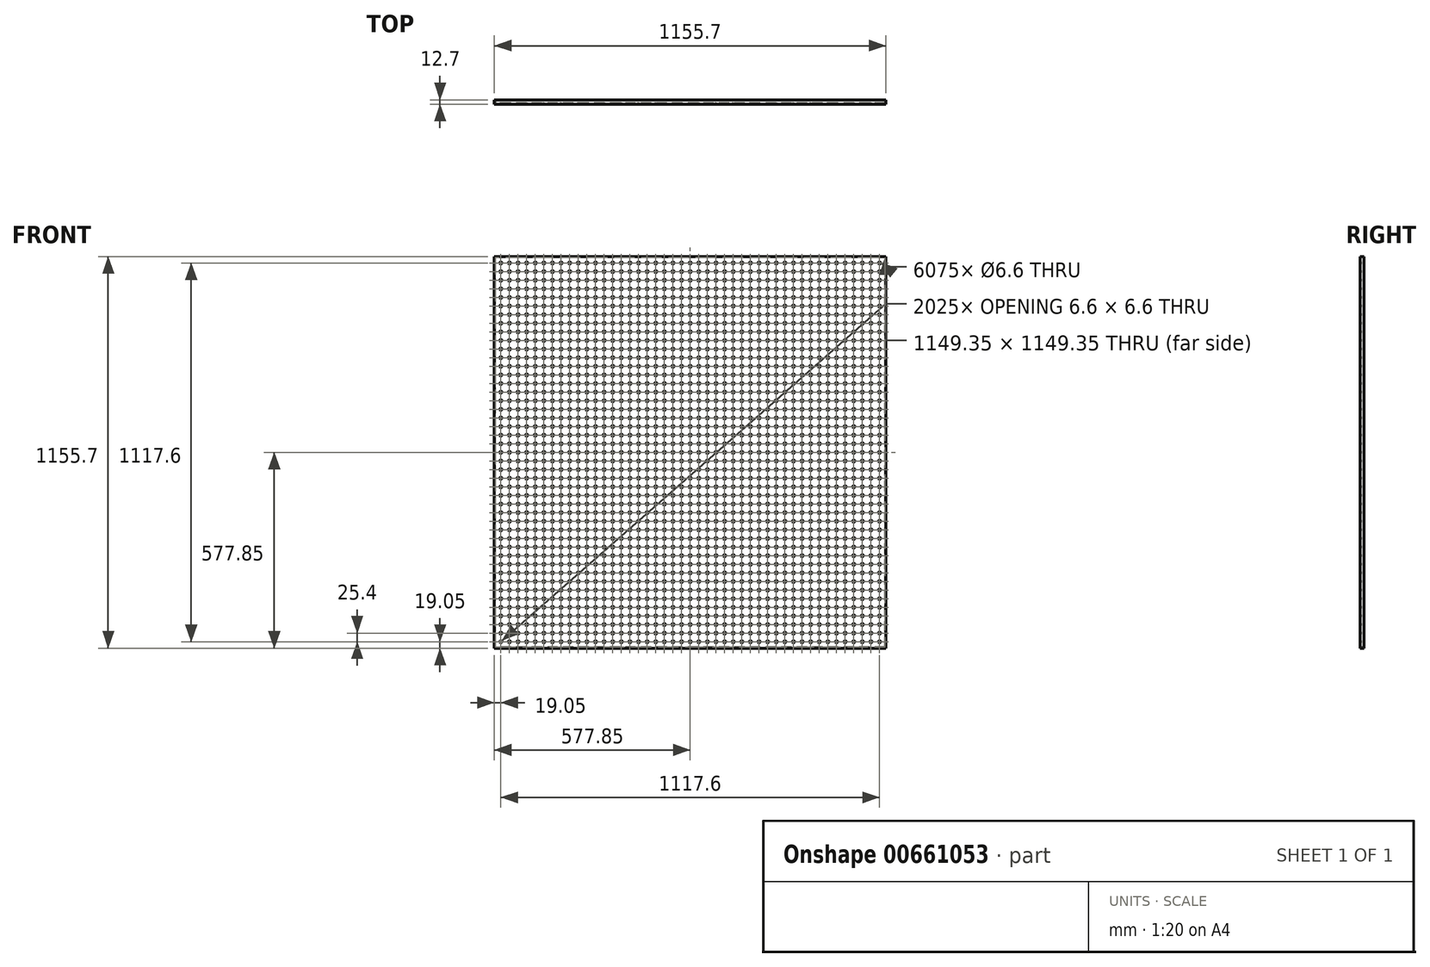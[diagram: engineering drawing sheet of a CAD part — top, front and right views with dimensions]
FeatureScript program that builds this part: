
annotation { "Feature Type Name" : "Feature", "Feature Type Description" : "" }
export const myFeature = defineFeature(function(context is Context, id is Id, definition is map)
    precondition{}
    {
        {
            var Q0;
            Q0=qCreatedBy(makeId("Front.planeOp"),FACE);
            var sketch = newSketch(context, id + "F0", { "sketchPlane" : qUnion([Q0])});
            skLineSegment(sketch, "E0.bottom", {"start": v(577.85, -577.85) * mm, "end": v(-577.85, -577.85) * mm});
            skLineSegment(sketch, "E0.top", {"start": v(577.85, 577.85) * mm, "end": v(-577.85, 577.85) * mm});
            skLineSegment(sketch, "E0.left", {"start": v(577.85, -577.85) * mm, "end": v(577.85, 577.85) * mm});
            skLineSegment(sketch, "E0.right", {"start": v(-577.85, -577.85) * mm, "end": v(-577.85, 577.85) * mm});
            skPoint(sketch, "E0.middle", {"position": v(0, 0) * mm});
            skCircle(sketch, "E1", {"center": v(-558.8, 558.8) * mm, "radius": 3.3 * mm});
            skCircle(sketch, "E2.0.1.0", {"center": v(-558.8, 533.4) * mm, "radius": 3.3 * mm});
            skCircle(sketch, "E2.0.2.0", {"center": v(-558.8, 508) * mm, "radius": 3.3 * mm});
            skCircle(sketch, "E2.0.3.0", {"center": v(-558.8, 482.6) * mm, "radius": 3.3 * mm});
            skCircle(sketch, "E2.0.4.0", {"center": v(-558.8, 457.2) * mm, "radius": 3.3 * mm});
            skCircle(sketch, "E2.0.5.0", {"center": v(-558.8, 431.8) * mm, "radius": 3.3 * mm});
            skCircle(sketch, "E2.0.6.0", {"center": v(-558.8, 406.4) * mm, "radius": 3.3 * mm});
            skCircle(sketch, "E2.0.7.0", {"center": v(-558.8, 381) * mm, "radius": 3.3 * mm});
            skCircle(sketch, "E2.0.8.0", {"center": v(-558.8, 355.6) * mm, "radius": 3.3 * mm});
            skCircle(sketch, "E2.0.9.0", {"center": v(-558.8, 330.2) * mm, "radius": 3.3 * mm});
            skCircle(sketch, "E2.0.10.0", {"center": v(-558.8, 304.8) * mm, "radius": 3.3 * mm});
            skCircle(sketch, "E2.0.11.0", {"center": v(-558.8, 279.4) * mm, "radius": 3.3 * mm});
            skCircle(sketch, "E2.0.12.0", {"center": v(-558.8, 254) * mm, "radius": 3.3 * mm});
            skCircle(sketch, "E2.0.13.0", {"center": v(-558.8, 228.6) * mm, "radius": 3.3 * mm});
            skCircle(sketch, "E2.0.14.0", {"center": v(-558.8, 203.2) * mm, "radius": 3.3 * mm});
            skCircle(sketch, "E2.0.15.0", {"center": v(-558.8, 177.8) * mm, "radius": 3.3 * mm});
            skCircle(sketch, "E2.0.16.0", {"center": v(-558.8, 152.4) * mm, "radius": 3.3 * mm});
            skCircle(sketch, "E2.0.17.0", {"center": v(-558.8, 127) * mm, "radius": 3.3 * mm});
            skCircle(sketch, "E2.0.18.0", {"center": v(-558.8, 101.6) * mm, "radius": 3.3 * mm});
            skCircle(sketch, "E2.0.19.0", {"center": v(-558.8, 76.2) * mm, "radius": 3.3 * mm});
            skCircle(sketch, "E2.0.20.0", {"center": v(-558.8, 50.8) * mm, "radius": 3.3 * mm});
            skCircle(sketch, "E2.0.21.0", {"center": v(-558.8, 25.4) * mm, "radius": 3.3 * mm});
            skCircle(sketch, "E2.0.22.0", {"center": v(-558.8, 0) * mm, "radius": 3.3 * mm});
            skCircle(sketch, "E2.0.23.0", {"center": v(-558.8, -25.4) * mm, "radius": 3.3 * mm});
            skCircle(sketch, "E2.0.24.0", {"center": v(-558.8, -50.8) * mm, "radius": 3.3 * mm});
            skCircle(sketch, "E2.0.25.0", {"center": v(-558.8, -76.2) * mm, "radius": 3.3 * mm});
            skCircle(sketch, "E2.0.26.0", {"center": v(-558.8, -101.6) * mm, "radius": 3.3 * mm});
            skCircle(sketch, "E2.0.27.0", {"center": v(-558.8, -127) * mm, "radius": 3.3 * mm});
            skCircle(sketch, "E2.0.28.0", {"center": v(-558.8, -152.4) * mm, "radius": 3.3 * mm});
            skCircle(sketch, "E2.0.29.0", {"center": v(-558.8, -177.8) * mm, "radius": 3.3 * mm});
            skCircle(sketch, "E2.0.30.0", {"center": v(-558.8, -203.2) * mm, "radius": 3.3 * mm});
            skCircle(sketch, "E2.0.31.0", {"center": v(-558.8, -228.6) * mm, "radius": 3.3 * mm});
            skCircle(sketch, "E2.0.32.0", {"center": v(-558.8, -254) * mm, "radius": 3.3 * mm});
            skCircle(sketch, "E2.0.33.0", {"center": v(-558.8, -279.4) * mm, "radius": 3.3 * mm});
            skCircle(sketch, "E2.0.34.0", {"center": v(-558.8, -304.8) * mm, "radius": 3.3 * mm});
            skCircle(sketch, "E2.0.35.0", {"center": v(-558.8, -330.2) * mm, "radius": 3.3 * mm});
            skCircle(sketch, "E2.0.36.0", {"center": v(-558.8, -355.6) * mm, "radius": 3.3 * mm});
            skCircle(sketch, "E2.0.37.0", {"center": v(-558.8, -381) * mm, "radius": 3.3 * mm});
            skCircle(sketch, "E2.0.38.0", {"center": v(-558.8, -406.4) * mm, "radius": 3.3 * mm});
            skCircle(sketch, "E2.0.39.0", {"center": v(-558.8, -431.8) * mm, "radius": 3.3 * mm});
            skCircle(sketch, "E2.0.40.0", {"center": v(-558.8, -457.2) * mm, "radius": 3.3 * mm});
            skCircle(sketch, "E2.0.41.0", {"center": v(-558.8, -482.6) * mm, "radius": 3.3 * mm});
            skCircle(sketch, "E2.0.42.0", {"center": v(-558.8, -508) * mm, "radius": 3.3 * mm});
            skCircle(sketch, "E2.0.43.0", {"center": v(-558.8, -533.4) * mm, "radius": 3.3 * mm});
            skCircle(sketch, "E2.0.44.0", {"center": v(-558.8, -558.8) * mm, "radius": 3.3 * mm});
            skCircle(sketch, "E2.1.0.0", {"center": v(-533.4, 558.8) * mm, "radius": 3.3 * mm});
            skCircle(sketch, "E2.1.1.0", {"center": v(-533.4, 533.4) * mm, "radius": 3.3 * mm});
            skCircle(sketch, "E2.1.2.0", {"center": v(-533.4, 508) * mm, "radius": 3.3 * mm});
            skCircle(sketch, "E2.1.3.0", {"center": v(-533.4, 482.6) * mm, "radius": 3.3 * mm});
            skCircle(sketch, "E2.1.4.0", {"center": v(-533.4, 457.2) * mm, "radius": 3.3 * mm});
            skCircle(sketch, "E2.1.5.0", {"center": v(-533.4, 431.8) * mm, "radius": 3.3 * mm});
            skCircle(sketch, "E2.1.6.0", {"center": v(-533.4, 406.4) * mm, "radius": 3.3 * mm});
            skCircle(sketch, "E2.1.7.0", {"center": v(-533.4, 381) * mm, "radius": 3.3 * mm});
            skCircle(sketch, "E2.1.8.0", {"center": v(-533.4, 355.6) * mm, "radius": 3.3 * mm});
            skCircle(sketch, "E2.1.9.0", {"center": v(-533.4, 330.2) * mm, "radius": 3.3 * mm});
            skCircle(sketch, "E2.1.10.0", {"center": v(-533.4, 304.8) * mm, "radius": 3.3 * mm});
            skCircle(sketch, "E2.1.11.0", {"center": v(-533.4, 279.4) * mm, "radius": 3.3 * mm});
            skCircle(sketch, "E2.1.12.0", {"center": v(-533.4, 254) * mm, "radius": 3.3 * mm});
            skCircle(sketch, "E2.1.13.0", {"center": v(-533.4, 228.6) * mm, "radius": 3.3 * mm});
            skCircle(sketch, "E2.1.14.0", {"center": v(-533.4, 203.2) * mm, "radius": 3.3 * mm});
            skCircle(sketch, "E2.1.15.0", {"center": v(-533.4, 177.8) * mm, "radius": 3.3 * mm});
            skCircle(sketch, "E2.1.16.0", {"center": v(-533.4, 152.4) * mm, "radius": 3.3 * mm});
            skCircle(sketch, "E2.1.17.0", {"center": v(-533.4, 127) * mm, "radius": 3.3 * mm});
            skCircle(sketch, "E2.1.18.0", {"center": v(-533.4, 101.6) * mm, "radius": 3.3 * mm});
            skCircle(sketch, "E2.1.19.0", {"center": v(-533.4, 76.2) * mm, "radius": 3.3 * mm});
            skCircle(sketch, "E2.1.20.0", {"center": v(-533.4, 50.8) * mm, "radius": 3.3 * mm});
            skCircle(sketch, "E2.1.21.0", {"center": v(-533.4, 25.4) * mm, "radius": 3.3 * mm});
            skCircle(sketch, "E2.1.22.0", {"center": v(-533.4, 0) * mm, "radius": 3.3 * mm});
            skCircle(sketch, "E2.1.23.0", {"center": v(-533.4, -25.4) * mm, "radius": 3.3 * mm});
            skCircle(sketch, "E2.1.24.0", {"center": v(-533.4, -50.8) * mm, "radius": 3.3 * mm});
            skCircle(sketch, "E2.1.25.0", {"center": v(-533.4, -76.2) * mm, "radius": 3.3 * mm});
            skCircle(sketch, "E2.1.26.0", {"center": v(-533.4, -101.6) * mm, "radius": 3.3 * mm});
            skCircle(sketch, "E2.1.27.0", {"center": v(-533.4, -127) * mm, "radius": 3.3 * mm});
            skCircle(sketch, "E2.1.28.0", {"center": v(-533.4, -152.4) * mm, "radius": 3.3 * mm});
            skCircle(sketch, "E2.1.29.0", {"center": v(-533.4, -177.8) * mm, "radius": 3.3 * mm});
            skCircle(sketch, "E2.1.30.0", {"center": v(-533.4, -203.2) * mm, "radius": 3.3 * mm});
            skCircle(sketch, "E2.1.31.0", {"center": v(-533.4, -228.6) * mm, "radius": 3.3 * mm});
            skCircle(sketch, "E2.1.32.0", {"center": v(-533.4, -254) * mm, "radius": 3.3 * mm});
            skCircle(sketch, "E2.1.33.0", {"center": v(-533.4, -279.4) * mm, "radius": 3.3 * mm});
            skCircle(sketch, "E2.1.34.0", {"center": v(-533.4, -304.8) * mm, "radius": 3.3 * mm});
            skCircle(sketch, "E2.1.35.0", {"center": v(-533.4, -330.2) * mm, "radius": 3.3 * mm});
            skCircle(sketch, "E2.1.36.0", {"center": v(-533.4, -355.6) * mm, "radius": 3.3 * mm});
            skCircle(sketch, "E2.1.37.0", {"center": v(-533.4, -381) * mm, "radius": 3.3 * mm});
            skCircle(sketch, "E2.1.38.0", {"center": v(-533.4, -406.4) * mm, "radius": 3.3 * mm});
            skCircle(sketch, "E2.1.39.0", {"center": v(-533.4, -431.8) * mm, "radius": 3.3 * mm});
            skCircle(sketch, "E2.1.40.0", {"center": v(-533.4, -457.2) * mm, "radius": 3.3 * mm});
            skCircle(sketch, "E2.1.41.0", {"center": v(-533.4, -482.6) * mm, "radius": 3.3 * mm});
            skCircle(sketch, "E2.1.42.0", {"center": v(-533.4, -508) * mm, "radius": 3.3 * mm});
            skCircle(sketch, "E2.1.43.0", {"center": v(-533.4, -533.4) * mm, "radius": 3.3 * mm});
            skCircle(sketch, "E2.1.44.0", {"center": v(-533.4, -558.8) * mm, "radius": 3.3 * mm});
            skCircle(sketch, "E2.2.0.0", {"center": v(-508, 558.8) * mm, "radius": 3.3 * mm});
            skCircle(sketch, "E2.2.1.0", {"center": v(-508, 533.4) * mm, "radius": 3.3 * mm});
            skCircle(sketch, "E2.2.2.0", {"center": v(-508, 508) * mm, "radius": 3.3 * mm});
            skCircle(sketch, "E2.2.3.0", {"center": v(-508, 482.6) * mm, "radius": 3.3 * mm});
            skCircle(sketch, "E2.2.4.0", {"center": v(-508, 457.2) * mm, "radius": 3.3 * mm});
            skCircle(sketch, "E2.2.5.0", {"center": v(-508, 431.8) * mm, "radius": 3.3 * mm});
            skCircle(sketch, "E2.2.6.0", {"center": v(-508, 406.4) * mm, "radius": 3.3 * mm});
            skCircle(sketch, "E2.2.7.0", {"center": v(-508, 381) * mm, "radius": 3.3 * mm});
            skCircle(sketch, "E2.2.8.0", {"center": v(-508, 355.6) * mm, "radius": 3.3 * mm});
            skCircle(sketch, "E2.2.9.0", {"center": v(-508, 330.2) * mm, "radius": 3.3 * mm});
            skCircle(sketch, "E2.2.10.0", {"center": v(-508, 304.8) * mm, "radius": 3.3 * mm});
            skCircle(sketch, "E2.2.11.0", {"center": v(-508, 279.4) * mm, "radius": 3.3 * mm});
            skCircle(sketch, "E2.2.12.0", {"center": v(-508, 254) * mm, "radius": 3.3 * mm});
            skCircle(sketch, "E2.2.13.0", {"center": v(-508, 228.6) * mm, "radius": 3.3 * mm});
            skCircle(sketch, "E2.2.14.0", {"center": v(-508, 203.2) * mm, "radius": 3.3 * mm});
            skCircle(sketch, "E2.2.15.0", {"center": v(-508, 177.8) * mm, "radius": 3.3 * mm});
            skCircle(sketch, "E2.2.16.0", {"center": v(-508, 152.4) * mm, "radius": 3.3 * mm});
            skCircle(sketch, "E2.2.17.0", {"center": v(-508, 127) * mm, "radius": 3.3 * mm});
            skCircle(sketch, "E2.2.18.0", {"center": v(-508, 101.6) * mm, "radius": 3.3 * mm});
            skCircle(sketch, "E2.2.19.0", {"center": v(-508, 76.2) * mm, "radius": 3.3 * mm});
            skCircle(sketch, "E2.2.20.0", {"center": v(-508, 50.8) * mm, "radius": 3.3 * mm});
            skCircle(sketch, "E2.2.21.0", {"center": v(-508, 25.4) * mm, "radius": 3.3 * mm});
            skCircle(sketch, "E2.2.22.0", {"center": v(-508, 0) * mm, "radius": 3.3 * mm});
            skCircle(sketch, "E2.2.23.0", {"center": v(-508, -25.4) * mm, "radius": 3.3 * mm});
            skCircle(sketch, "E2.2.24.0", {"center": v(-508, -50.8) * mm, "radius": 3.3 * mm});
            skCircle(sketch, "E2.2.25.0", {"center": v(-508, -76.2) * mm, "radius": 3.3 * mm});
            skCircle(sketch, "E2.2.26.0", {"center": v(-508, -101.6) * mm, "radius": 3.3 * mm});
            skCircle(sketch, "E2.2.27.0", {"center": v(-508, -127) * mm, "radius": 3.3 * mm});
            skCircle(sketch, "E2.2.28.0", {"center": v(-508, -152.4) * mm, "radius": 3.3 * mm});
            skCircle(sketch, "E2.2.29.0", {"center": v(-508, -177.8) * mm, "radius": 3.3 * mm});
            skCircle(sketch, "E2.2.30.0", {"center": v(-508, -203.2) * mm, "radius": 3.3 * mm});
            skCircle(sketch, "E2.2.31.0", {"center": v(-508, -228.6) * mm, "radius": 3.3 * mm});
            skCircle(sketch, "E2.2.32.0", {"center": v(-508, -254) * mm, "radius": 3.3 * mm});
            skCircle(sketch, "E2.2.33.0", {"center": v(-508, -279.4) * mm, "radius": 3.3 * mm});
            skCircle(sketch, "E2.2.34.0", {"center": v(-508, -304.8) * mm, "radius": 3.3 * mm});
            skCircle(sketch, "E2.2.35.0", {"center": v(-508, -330.2) * mm, "radius": 3.3 * mm});
            skCircle(sketch, "E2.2.36.0", {"center": v(-508, -355.6) * mm, "radius": 3.3 * mm});
            skCircle(sketch, "E2.2.37.0", {"center": v(-508, -381) * mm, "radius": 3.3 * mm});
            skCircle(sketch, "E2.2.38.0", {"center": v(-508, -406.4) * mm, "radius": 3.3 * mm});
            skCircle(sketch, "E2.2.39.0", {"center": v(-508, -431.8) * mm, "radius": 3.3 * mm});
            skCircle(sketch, "E2.2.40.0", {"center": v(-508, -457.2) * mm, "radius": 3.3 * mm});
            skCircle(sketch, "E2.2.41.0", {"center": v(-508, -482.6) * mm, "radius": 3.3 * mm});
            skCircle(sketch, "E2.2.42.0", {"center": v(-508, -508) * mm, "radius": 3.3 * mm});
            skCircle(sketch, "E2.2.43.0", {"center": v(-508, -533.4) * mm, "radius": 3.3 * mm});
            skCircle(sketch, "E2.2.44.0", {"center": v(-508, -558.8) * mm, "radius": 3.3 * mm});
            skCircle(sketch, "E2.3.0.0", {"center": v(-482.6, 558.8) * mm, "radius": 3.3 * mm});
            skCircle(sketch, "E2.3.1.0", {"center": v(-482.6, 533.4) * mm, "radius": 3.3 * mm});
            skCircle(sketch, "E2.3.2.0", {"center": v(-482.6, 508) * mm, "radius": 3.3 * mm});
            skCircle(sketch, "E2.3.3.0", {"center": v(-482.6, 482.6) * mm, "radius": 3.3 * mm});
            skCircle(sketch, "E2.3.4.0", {"center": v(-482.6, 457.2) * mm, "radius": 3.3 * mm});
            skCircle(sketch, "E2.3.5.0", {"center": v(-482.6, 431.8) * mm, "radius": 3.3 * mm});
            skCircle(sketch, "E2.3.6.0", {"center": v(-482.6, 406.4) * mm, "radius": 3.3 * mm});
            skCircle(sketch, "E2.3.7.0", {"center": v(-482.6, 381) * mm, "radius": 3.3 * mm});
            skCircle(sketch, "E2.3.8.0", {"center": v(-482.6, 355.6) * mm, "radius": 3.3 * mm});
            skCircle(sketch, "E2.3.9.0", {"center": v(-482.6, 330.2) * mm, "radius": 3.3 * mm});
            skCircle(sketch, "E2.3.10.0", {"center": v(-482.6, 304.8) * mm, "radius": 3.3 * mm});
            skCircle(sketch, "E2.3.11.0", {"center": v(-482.6, 279.4) * mm, "radius": 3.3 * mm});
            skCircle(sketch, "E2.3.12.0", {"center": v(-482.6, 254) * mm, "radius": 3.3 * mm});
            skCircle(sketch, "E2.3.13.0", {"center": v(-482.6, 228.6) * mm, "radius": 3.3 * mm});
            skCircle(sketch, "E2.3.14.0", {"center": v(-482.6, 203.2) * mm, "radius": 3.3 * mm});
            skCircle(sketch, "E2.3.15.0", {"center": v(-482.6, 177.8) * mm, "radius": 3.3 * mm});
            skCircle(sketch, "E2.3.16.0", {"center": v(-482.6, 152.4) * mm, "radius": 3.3 * mm});
            skCircle(sketch, "E2.3.17.0", {"center": v(-482.6, 127) * mm, "radius": 3.3 * mm});
            skCircle(sketch, "E2.3.18.0", {"center": v(-482.6, 101.6) * mm, "radius": 3.3 * mm});
            skCircle(sketch, "E2.3.19.0", {"center": v(-482.6, 76.2) * mm, "radius": 3.3 * mm});
            skCircle(sketch, "E2.3.20.0", {"center": v(-482.6, 50.8) * mm, "radius": 3.3 * mm});
            skCircle(sketch, "E2.3.21.0", {"center": v(-482.6, 25.4) * mm, "radius": 3.3 * mm});
            skCircle(sketch, "E2.3.22.0", {"center": v(-482.6, 0) * mm, "radius": 3.3 * mm});
            skCircle(sketch, "E2.3.23.0", {"center": v(-482.6, -25.4) * mm, "radius": 3.3 * mm});
            skCircle(sketch, "E2.3.24.0", {"center": v(-482.6, -50.8) * mm, "radius": 3.3 * mm});
            skCircle(sketch, "E2.3.25.0", {"center": v(-482.6, -76.2) * mm, "radius": 3.3 * mm});
            skCircle(sketch, "E2.3.26.0", {"center": v(-482.6, -101.6) * mm, "radius": 3.3 * mm});
            skCircle(sketch, "E2.3.27.0", {"center": v(-482.6, -127) * mm, "radius": 3.3 * mm});
            skCircle(sketch, "E2.3.28.0", {"center": v(-482.6, -152.4) * mm, "radius": 3.3 * mm});
            skCircle(sketch, "E2.3.29.0", {"center": v(-482.6, -177.8) * mm, "radius": 3.3 * mm});
            skCircle(sketch, "E2.3.30.0", {"center": v(-482.6, -203.2) * mm, "radius": 3.3 * mm});
            skCircle(sketch, "E2.3.31.0", {"center": v(-482.6, -228.6) * mm, "radius": 3.3 * mm});
            skCircle(sketch, "E2.3.32.0", {"center": v(-482.6, -254) * mm, "radius": 3.3 * mm});
            skCircle(sketch, "E2.3.33.0", {"center": v(-482.6, -279.4) * mm, "radius": 3.3 * mm});
            skCircle(sketch, "E2.3.34.0", {"center": v(-482.6, -304.8) * mm, "radius": 3.3 * mm});
            skCircle(sketch, "E2.3.35.0", {"center": v(-482.6, -330.2) * mm, "radius": 3.3 * mm});
            skCircle(sketch, "E2.3.36.0", {"center": v(-482.6, -355.6) * mm, "radius": 3.3 * mm});
            skCircle(sketch, "E2.3.37.0", {"center": v(-482.6, -381) * mm, "radius": 3.3 * mm});
            skCircle(sketch, "E2.3.38.0", {"center": v(-482.6, -406.4) * mm, "radius": 3.3 * mm});
            skCircle(sketch, "E2.3.39.0", {"center": v(-482.6, -431.8) * mm, "radius": 3.3 * mm});
            skCircle(sketch, "E2.3.40.0", {"center": v(-482.6, -457.2) * mm, "radius": 3.3 * mm});
            skCircle(sketch, "E2.3.41.0", {"center": v(-482.6, -482.6) * mm, "radius": 3.3 * mm});
            skCircle(sketch, "E2.3.42.0", {"center": v(-482.6, -508) * mm, "radius": 3.3 * mm});
            skCircle(sketch, "E2.3.43.0", {"center": v(-482.6, -533.4) * mm, "radius": 3.3 * mm});
            skCircle(sketch, "E2.3.44.0", {"center": v(-482.6, -558.8) * mm, "radius": 3.3 * mm});
            skCircle(sketch, "E2.4.0.0", {"center": v(-457.2, 558.8) * mm, "radius": 3.3 * mm});
            skCircle(sketch, "E2.4.1.0", {"center": v(-457.2, 533.4) * mm, "radius": 3.3 * mm});
            skCircle(sketch, "E2.4.2.0", {"center": v(-457.2, 508) * mm, "radius": 3.3 * mm});
            skCircle(sketch, "E2.4.3.0", {"center": v(-457.2, 482.6) * mm, "radius": 3.3 * mm});
            skCircle(sketch, "E2.4.4.0", {"center": v(-457.2, 457.2) * mm, "radius": 3.3 * mm});
            skCircle(sketch, "E2.4.5.0", {"center": v(-457.2, 431.8) * mm, "radius": 3.3 * mm});
            skCircle(sketch, "E2.4.6.0", {"center": v(-457.2, 406.4) * mm, "radius": 3.3 * mm});
            skCircle(sketch, "E2.4.7.0", {"center": v(-457.2, 381) * mm, "radius": 3.3 * mm});
            skCircle(sketch, "E2.4.8.0", {"center": v(-457.2, 355.6) * mm, "radius": 3.3 * mm});
            skCircle(sketch, "E2.4.9.0", {"center": v(-457.2, 330.2) * mm, "radius": 3.3 * mm});
            skCircle(sketch, "E2.4.10.0", {"center": v(-457.2, 304.8) * mm, "radius": 3.3 * mm});
            skCircle(sketch, "E2.4.11.0", {"center": v(-457.2, 279.4) * mm, "radius": 3.3 * mm});
            skCircle(sketch, "E2.4.12.0", {"center": v(-457.2, 254) * mm, "radius": 3.3 * mm});
            skCircle(sketch, "E2.4.13.0", {"center": v(-457.2, 228.6) * mm, "radius": 3.3 * mm});
            skCircle(sketch, "E2.4.14.0", {"center": v(-457.2, 203.2) * mm, "radius": 3.3 * mm});
            skCircle(sketch, "E2.4.15.0", {"center": v(-457.2, 177.8) * mm, "radius": 3.3 * mm});
            skCircle(sketch, "E2.4.16.0", {"center": v(-457.2, 152.4) * mm, "radius": 3.3 * mm});
            skCircle(sketch, "E2.4.17.0", {"center": v(-457.2, 127) * mm, "radius": 3.3 * mm});
            skCircle(sketch, "E2.4.18.0", {"center": v(-457.2, 101.6) * mm, "radius": 3.3 * mm});
            skCircle(sketch, "E2.4.19.0", {"center": v(-457.2, 76.2) * mm, "radius": 3.3 * mm});
            skCircle(sketch, "E2.4.20.0", {"center": v(-457.2, 50.8) * mm, "radius": 3.3 * mm});
            skCircle(sketch, "E2.4.21.0", {"center": v(-457.2, 25.4) * mm, "radius": 3.3 * mm});
            skCircle(sketch, "E2.4.22.0", {"center": v(-457.2, 0) * mm, "radius": 3.3 * mm});
            skCircle(sketch, "E2.4.23.0", {"center": v(-457.2, -25.4) * mm, "radius": 3.3 * mm});
            skCircle(sketch, "E2.4.24.0", {"center": v(-457.2, -50.8) * mm, "radius": 3.3 * mm});
            skCircle(sketch, "E2.4.25.0", {"center": v(-457.2, -76.2) * mm, "radius": 3.3 * mm});
            skCircle(sketch, "E2.4.26.0", {"center": v(-457.2, -101.6) * mm, "radius": 3.3 * mm});
            skCircle(sketch, "E2.4.27.0", {"center": v(-457.2, -127) * mm, "radius": 3.3 * mm});
            skCircle(sketch, "E2.4.28.0", {"center": v(-457.2, -152.4) * mm, "radius": 3.3 * mm});
            skCircle(sketch, "E2.4.29.0", {"center": v(-457.2, -177.8) * mm, "radius": 3.3 * mm});
            skCircle(sketch, "E2.4.30.0", {"center": v(-457.2, -203.2) * mm, "radius": 3.3 * mm});
            skCircle(sketch, "E2.4.31.0", {"center": v(-457.2, -228.6) * mm, "radius": 3.3 * mm});
            skCircle(sketch, "E2.4.32.0", {"center": v(-457.2, -254) * mm, "radius": 3.3 * mm});
            skCircle(sketch, "E2.4.33.0", {"center": v(-457.2, -279.4) * mm, "radius": 3.3 * mm});
            skCircle(sketch, "E2.4.34.0", {"center": v(-457.2, -304.8) * mm, "radius": 3.3 * mm});
            skCircle(sketch, "E2.4.35.0", {"center": v(-457.2, -330.2) * mm, "radius": 3.3 * mm});
            skCircle(sketch, "E2.4.36.0", {"center": v(-457.2, -355.6) * mm, "radius": 3.3 * mm});
            skCircle(sketch, "E2.4.37.0", {"center": v(-457.2, -381) * mm, "radius": 3.3 * mm});
            skCircle(sketch, "E2.4.38.0", {"center": v(-457.2, -406.4) * mm, "radius": 3.3 * mm});
            skCircle(sketch, "E2.4.39.0", {"center": v(-457.2, -431.8) * mm, "radius": 3.3 * mm});
            skCircle(sketch, "E2.4.40.0", {"center": v(-457.2, -457.2) * mm, "radius": 3.3 * mm});
            skCircle(sketch, "E2.4.41.0", {"center": v(-457.2, -482.6) * mm, "radius": 3.3 * mm});
            skCircle(sketch, "E2.4.42.0", {"center": v(-457.2, -508) * mm, "radius": 3.3 * mm});
            skCircle(sketch, "E2.4.43.0", {"center": v(-457.2, -533.4) * mm, "radius": 3.3 * mm});
            skCircle(sketch, "E2.4.44.0", {"center": v(-457.2, -558.8) * mm, "radius": 3.3 * mm});
            skCircle(sketch, "E2.5.0.0", {"center": v(-431.8, 558.8) * mm, "radius": 3.3 * mm});
            skCircle(sketch, "E2.5.1.0", {"center": v(-431.8, 533.4) * mm, "radius": 3.3 * mm});
            skCircle(sketch, "E2.5.2.0", {"center": v(-431.8, 508) * mm, "radius": 3.3 * mm});
            skCircle(sketch, "E2.5.3.0", {"center": v(-431.8, 482.6) * mm, "radius": 3.3 * mm});
            skCircle(sketch, "E2.5.4.0", {"center": v(-431.8, 457.2) * mm, "radius": 3.3 * mm});
            skCircle(sketch, "E2.5.5.0", {"center": v(-431.8, 431.8) * mm, "radius": 3.3 * mm});
            skCircle(sketch, "E2.5.6.0", {"center": v(-431.8, 406.4) * mm, "radius": 3.3 * mm});
            skCircle(sketch, "E2.5.7.0", {"center": v(-431.8, 381) * mm, "radius": 3.3 * mm});
            skCircle(sketch, "E2.5.8.0", {"center": v(-431.8, 355.6) * mm, "radius": 3.3 * mm});
            skCircle(sketch, "E2.5.9.0", {"center": v(-431.8, 330.2) * mm, "radius": 3.3 * mm});
            skCircle(sketch, "E2.5.10.0", {"center": v(-431.8, 304.8) * mm, "radius": 3.3 * mm});
            skCircle(sketch, "E2.5.11.0", {"center": v(-431.8, 279.4) * mm, "radius": 3.3 * mm});
            skCircle(sketch, "E2.5.12.0", {"center": v(-431.8, 254) * mm, "radius": 3.3 * mm});
            skCircle(sketch, "E2.5.13.0", {"center": v(-431.8, 228.6) * mm, "radius": 3.3 * mm});
            skCircle(sketch, "E2.5.14.0", {"center": v(-431.8, 203.2) * mm, "radius": 3.3 * mm});
            skCircle(sketch, "E2.5.15.0", {"center": v(-431.8, 177.8) * mm, "radius": 3.3 * mm});
            skCircle(sketch, "E2.5.16.0", {"center": v(-431.8, 152.4) * mm, "radius": 3.3 * mm});
            skCircle(sketch, "E2.5.17.0", {"center": v(-431.8, 127) * mm, "radius": 3.3 * mm});
            skCircle(sketch, "E2.5.18.0", {"center": v(-431.8, 101.6) * mm, "radius": 3.3 * mm});
            skCircle(sketch, "E2.5.19.0", {"center": v(-431.8, 76.2) * mm, "radius": 3.3 * mm});
            skCircle(sketch, "E2.5.20.0", {"center": v(-431.8, 50.8) * mm, "radius": 3.3 * mm});
            skCircle(sketch, "E2.5.21.0", {"center": v(-431.8, 25.4) * mm, "radius": 3.3 * mm});
            skCircle(sketch, "E2.5.22.0", {"center": v(-431.8, 0) * mm, "radius": 3.3 * mm});
            skCircle(sketch, "E2.5.23.0", {"center": v(-431.8, -25.4) * mm, "radius": 3.3 * mm});
            skCircle(sketch, "E2.5.24.0", {"center": v(-431.8, -50.8) * mm, "radius": 3.3 * mm});
            skCircle(sketch, "E2.5.25.0", {"center": v(-431.8, -76.2) * mm, "radius": 3.3 * mm});
            skCircle(sketch, "E2.5.26.0", {"center": v(-431.8, -101.6) * mm, "radius": 3.3 * mm});
            skCircle(sketch, "E2.5.27.0", {"center": v(-431.8, -127) * mm, "radius": 3.3 * mm});
            skCircle(sketch, "E2.5.28.0", {"center": v(-431.8, -152.4) * mm, "radius": 3.3 * mm});
            skCircle(sketch, "E2.5.29.0", {"center": v(-431.8, -177.8) * mm, "radius": 3.3 * mm});
            skCircle(sketch, "E2.5.30.0", {"center": v(-431.8, -203.2) * mm, "radius": 3.3 * mm});
            skCircle(sketch, "E2.5.31.0", {"center": v(-431.8, -228.6) * mm, "radius": 3.3 * mm});
            skCircle(sketch, "E2.5.32.0", {"center": v(-431.8, -254) * mm, "radius": 3.3 * mm});
            skCircle(sketch, "E2.5.33.0", {"center": v(-431.8, -279.4) * mm, "radius": 3.3 * mm});
            skCircle(sketch, "E2.5.34.0", {"center": v(-431.8, -304.8) * mm, "radius": 3.3 * mm});
            skCircle(sketch, "E2.5.35.0", {"center": v(-431.8, -330.2) * mm, "radius": 3.3 * mm});
            skCircle(sketch, "E2.5.36.0", {"center": v(-431.8, -355.6) * mm, "radius": 3.3 * mm});
            skCircle(sketch, "E2.5.37.0", {"center": v(-431.8, -381) * mm, "radius": 3.3 * mm});
            skCircle(sketch, "E2.5.38.0", {"center": v(-431.8, -406.4) * mm, "radius": 3.3 * mm});
            skCircle(sketch, "E2.5.39.0", {"center": v(-431.8, -431.8) * mm, "radius": 3.3 * mm});
            skCircle(sketch, "E2.5.40.0", {"center": v(-431.8, -457.2) * mm, "radius": 3.3 * mm});
            skCircle(sketch, "E2.5.41.0", {"center": v(-431.8, -482.6) * mm, "radius": 3.3 * mm});
            skCircle(sketch, "E2.5.42.0", {"center": v(-431.8, -508) * mm, "radius": 3.3 * mm});
            skCircle(sketch, "E2.5.43.0", {"center": v(-431.8, -533.4) * mm, "radius": 3.3 * mm});
            skCircle(sketch, "E2.5.44.0", {"center": v(-431.8, -558.8) * mm, "radius": 3.3 * mm});
            skCircle(sketch, "E2.6.0.0", {"center": v(-406.4, 558.8) * mm, "radius": 3.3 * mm});
            skCircle(sketch, "E2.6.1.0", {"center": v(-406.4, 533.4) * mm, "radius": 3.3 * mm});
            skCircle(sketch, "E2.6.2.0", {"center": v(-406.4, 508) * mm, "radius": 3.3 * mm});
            skCircle(sketch, "E2.6.3.0", {"center": v(-406.4, 482.6) * mm, "radius": 3.3 * mm});
            skCircle(sketch, "E2.6.4.0", {"center": v(-406.4, 457.2) * mm, "radius": 3.3 * mm});
            skCircle(sketch, "E2.6.5.0", {"center": v(-406.4, 431.8) * mm, "radius": 3.3 * mm});
            skCircle(sketch, "E2.6.6.0", {"center": v(-406.4, 406.4) * mm, "radius": 3.3 * mm});
            skCircle(sketch, "E2.6.7.0", {"center": v(-406.4, 381) * mm, "radius": 3.3 * mm});
            skCircle(sketch, "E2.6.8.0", {"center": v(-406.4, 355.6) * mm, "radius": 3.3 * mm});
            skCircle(sketch, "E2.6.9.0", {"center": v(-406.4, 330.2) * mm, "radius": 3.3 * mm});
            skCircle(sketch, "E2.6.10.0", {"center": v(-406.4, 304.8) * mm, "radius": 3.3 * mm});
            skCircle(sketch, "E2.6.11.0", {"center": v(-406.4, 279.4) * mm, "radius": 3.3 * mm});
            skCircle(sketch, "E2.6.12.0", {"center": v(-406.4, 254) * mm, "radius": 3.3 * mm});
            skCircle(sketch, "E2.6.13.0", {"center": v(-406.4, 228.6) * mm, "radius": 3.3 * mm});
            skCircle(sketch, "E2.6.14.0", {"center": v(-406.4, 203.2) * mm, "radius": 3.3 * mm});
            skCircle(sketch, "E2.6.15.0", {"center": v(-406.4, 177.8) * mm, "radius": 3.3 * mm});
            skCircle(sketch, "E2.6.16.0", {"center": v(-406.4, 152.4) * mm, "radius": 3.3 * mm});
            skCircle(sketch, "E2.6.17.0", {"center": v(-406.4, 127) * mm, "radius": 3.3 * mm});
            skCircle(sketch, "E2.6.18.0", {"center": v(-406.4, 101.6) * mm, "radius": 3.3 * mm});
            skCircle(sketch, "E2.6.19.0", {"center": v(-406.4, 76.2) * mm, "radius": 3.3 * mm});
            skCircle(sketch, "E2.6.20.0", {"center": v(-406.4, 50.8) * mm, "radius": 3.3 * mm});
            skCircle(sketch, "E2.6.21.0", {"center": v(-406.4, 25.4) * mm, "radius": 3.3 * mm});
            skCircle(sketch, "E2.6.22.0", {"center": v(-406.4, 0) * mm, "radius": 3.3 * mm});
            skCircle(sketch, "E2.6.23.0", {"center": v(-406.4, -25.4) * mm, "radius": 3.3 * mm});
            skCircle(sketch, "E2.6.24.0", {"center": v(-406.4, -50.8) * mm, "radius": 3.3 * mm});
            skCircle(sketch, "E2.6.25.0", {"center": v(-406.4, -76.2) * mm, "radius": 3.3 * mm});
            skCircle(sketch, "E2.6.26.0", {"center": v(-406.4, -101.6) * mm, "radius": 3.3 * mm});
            skCircle(sketch, "E2.6.27.0", {"center": v(-406.4, -127) * mm, "radius": 3.3 * mm});
            skCircle(sketch, "E2.6.28.0", {"center": v(-406.4, -152.4) * mm, "radius": 3.3 * mm});
            skCircle(sketch, "E2.6.29.0", {"center": v(-406.4, -177.8) * mm, "radius": 3.3 * mm});
            skCircle(sketch, "E2.6.30.0", {"center": v(-406.4, -203.2) * mm, "radius": 3.3 * mm});
            skCircle(sketch, "E2.6.31.0", {"center": v(-406.4, -228.6) * mm, "radius": 3.3 * mm});
            skCircle(sketch, "E2.6.32.0", {"center": v(-406.4, -254) * mm, "radius": 3.3 * mm});
            skCircle(sketch, "E2.6.33.0", {"center": v(-406.4, -279.4) * mm, "radius": 3.3 * mm});
            skCircle(sketch, "E2.6.34.0", {"center": v(-406.4, -304.8) * mm, "radius": 3.3 * mm});
            skCircle(sketch, "E2.6.35.0", {"center": v(-406.4, -330.2) * mm, "radius": 3.3 * mm});
            skCircle(sketch, "E2.6.36.0", {"center": v(-406.4, -355.6) * mm, "radius": 3.3 * mm});
            skCircle(sketch, "E2.6.37.0", {"center": v(-406.4, -381) * mm, "radius": 3.3 * mm});
            skCircle(sketch, "E2.6.38.0", {"center": v(-406.4, -406.4) * mm, "radius": 3.3 * mm});
            skCircle(sketch, "E2.6.39.0", {"center": v(-406.4, -431.8) * mm, "radius": 3.3 * mm});
            skCircle(sketch, "E2.6.40.0", {"center": v(-406.4, -457.2) * mm, "radius": 3.3 * mm});
            skCircle(sketch, "E2.6.41.0", {"center": v(-406.4, -482.6) * mm, "radius": 3.3 * mm});
            skCircle(sketch, "E2.6.42.0", {"center": v(-406.4, -508) * mm, "radius": 3.3 * mm});
            skCircle(sketch, "E2.6.43.0", {"center": v(-406.4, -533.4) * mm, "radius": 3.3 * mm});
            skCircle(sketch, "E2.6.44.0", {"center": v(-406.4, -558.8) * mm, "radius": 3.3 * mm});
            skCircle(sketch, "E2.7.0.0", {"center": v(-381, 558.8) * mm, "radius": 3.3 * mm});
            skCircle(sketch, "E2.7.1.0", {"center": v(-381, 533.4) * mm, "radius": 3.3 * mm});
            skCircle(sketch, "E2.7.2.0", {"center": v(-381, 508) * mm, "radius": 3.3 * mm});
            skCircle(sketch, "E2.7.3.0", {"center": v(-381, 482.6) * mm, "radius": 3.3 * mm});
            skCircle(sketch, "E2.7.4.0", {"center": v(-381, 457.2) * mm, "radius": 3.3 * mm});
            skCircle(sketch, "E2.7.5.0", {"center": v(-381, 431.8) * mm, "radius": 3.3 * mm});
            skCircle(sketch, "E2.7.6.0", {"center": v(-381, 406.4) * mm, "radius": 3.3 * mm});
            skCircle(sketch, "E2.7.7.0", {"center": v(-381, 381) * mm, "radius": 3.3 * mm});
            skCircle(sketch, "E2.7.8.0", {"center": v(-381, 355.6) * mm, "radius": 3.3 * mm});
            skCircle(sketch, "E2.7.9.0", {"center": v(-381, 330.2) * mm, "radius": 3.3 * mm});
            skCircle(sketch, "E2.7.10.0", {"center": v(-381, 304.8) * mm, "radius": 3.3 * mm});
            skCircle(sketch, "E2.7.11.0", {"center": v(-381, 279.4) * mm, "radius": 3.3 * mm});
            skCircle(sketch, "E2.7.12.0", {"center": v(-381, 254) * mm, "radius": 3.3 * mm});
            skCircle(sketch, "E2.7.13.0", {"center": v(-381, 228.6) * mm, "radius": 3.3 * mm});
            skCircle(sketch, "E2.7.14.0", {"center": v(-381, 203.2) * mm, "radius": 3.3 * mm});
            skCircle(sketch, "E2.7.15.0", {"center": v(-381, 177.8) * mm, "radius": 3.3 * mm});
            skCircle(sketch, "E2.7.16.0", {"center": v(-381, 152.4) * mm, "radius": 3.3 * mm});
            skCircle(sketch, "E2.7.17.0", {"center": v(-381, 127) * mm, "radius": 3.3 * mm});
            skCircle(sketch, "E2.7.18.0", {"center": v(-381, 101.6) * mm, "radius": 3.3 * mm});
            skCircle(sketch, "E2.7.19.0", {"center": v(-381, 76.2) * mm, "radius": 3.3 * mm});
            skCircle(sketch, "E2.7.20.0", {"center": v(-381, 50.8) * mm, "radius": 3.3 * mm});
            skCircle(sketch, "E2.7.21.0", {"center": v(-381, 25.4) * mm, "radius": 3.3 * mm});
            skCircle(sketch, "E2.7.22.0", {"center": v(-381, 0) * mm, "radius": 3.3 * mm});
            skCircle(sketch, "E2.7.23.0", {"center": v(-381, -25.4) * mm, "radius": 3.3 * mm});
            skCircle(sketch, "E2.7.24.0", {"center": v(-381, -50.8) * mm, "radius": 3.3 * mm});
            skCircle(sketch, "E2.7.25.0", {"center": v(-381, -76.2) * mm, "radius": 3.3 * mm});
            skCircle(sketch, "E2.7.26.0", {"center": v(-381, -101.6) * mm, "radius": 3.3 * mm});
            skCircle(sketch, "E2.7.27.0", {"center": v(-381, -127) * mm, "radius": 3.3 * mm});
            skCircle(sketch, "E2.7.28.0", {"center": v(-381, -152.4) * mm, "radius": 3.3 * mm});
            skCircle(sketch, "E2.7.29.0", {"center": v(-381, -177.8) * mm, "radius": 3.3 * mm});
            skCircle(sketch, "E2.7.30.0", {"center": v(-381, -203.2) * mm, "radius": 3.3 * mm});
            skCircle(sketch, "E2.7.31.0", {"center": v(-381, -228.6) * mm, "radius": 3.3 * mm});
            skCircle(sketch, "E2.7.32.0", {"center": v(-381, -254) * mm, "radius": 3.3 * mm});
            skCircle(sketch, "E2.7.33.0", {"center": v(-381, -279.4) * mm, "radius": 3.3 * mm});
            skCircle(sketch, "E2.7.34.0", {"center": v(-381, -304.8) * mm, "radius": 3.3 * mm});
            skCircle(sketch, "E2.7.35.0", {"center": v(-381, -330.2) * mm, "radius": 3.3 * mm});
            skCircle(sketch, "E2.7.36.0", {"center": v(-381, -355.6) * mm, "radius": 3.3 * mm});
            skCircle(sketch, "E2.7.37.0", {"center": v(-381, -381) * mm, "radius": 3.3 * mm});
            skCircle(sketch, "E2.7.38.0", {"center": v(-381, -406.4) * mm, "radius": 3.3 * mm});
            skCircle(sketch, "E2.7.39.0", {"center": v(-381, -431.8) * mm, "radius": 3.3 * mm});
            skCircle(sketch, "E2.7.40.0", {"center": v(-381, -457.2) * mm, "radius": 3.3 * mm});
            skCircle(sketch, "E2.7.41.0", {"center": v(-381, -482.6) * mm, "radius": 3.3 * mm});
            skCircle(sketch, "E2.7.42.0", {"center": v(-381, -508) * mm, "radius": 3.3 * mm});
            skCircle(sketch, "E2.7.43.0", {"center": v(-381, -533.4) * mm, "radius": 3.3 * mm});
            skCircle(sketch, "E2.7.44.0", {"center": v(-381, -558.8) * mm, "radius": 3.3 * mm});
            skCircle(sketch, "E2.8.0.0", {"center": v(-355.6, 558.8) * mm, "radius": 3.3 * mm});
            skCircle(sketch, "E2.8.1.0", {"center": v(-355.6, 533.4) * mm, "radius": 3.3 * mm});
            skCircle(sketch, "E2.8.2.0", {"center": v(-355.6, 508) * mm, "radius": 3.3 * mm});
            skCircle(sketch, "E2.8.3.0", {"center": v(-355.6, 482.6) * mm, "radius": 3.3 * mm});
            skCircle(sketch, "E2.8.4.0", {"center": v(-355.6, 457.2) * mm, "radius": 3.3 * mm});
            skCircle(sketch, "E2.8.5.0", {"center": v(-355.6, 431.8) * mm, "radius": 3.3 * mm});
            skCircle(sketch, "E2.8.6.0", {"center": v(-355.6, 406.4) * mm, "radius": 3.3 * mm});
            skCircle(sketch, "E2.8.7.0", {"center": v(-355.6, 381) * mm, "radius": 3.3 * mm});
            skCircle(sketch, "E2.8.8.0", {"center": v(-355.6, 355.6) * mm, "radius": 3.3 * mm});
            skCircle(sketch, "E2.8.9.0", {"center": v(-355.6, 330.2) * mm, "radius": 3.3 * mm});
            skCircle(sketch, "E2.8.10.0", {"center": v(-355.6, 304.8) * mm, "radius": 3.3 * mm});
            skCircle(sketch, "E2.8.11.0", {"center": v(-355.6, 279.4) * mm, "radius": 3.3 * mm});
            skCircle(sketch, "E2.8.12.0", {"center": v(-355.6, 254) * mm, "radius": 3.3 * mm});
            skCircle(sketch, "E2.8.13.0", {"center": v(-355.6, 228.6) * mm, "radius": 3.3 * mm});
            skCircle(sketch, "E2.8.14.0", {"center": v(-355.6, 203.2) * mm, "radius": 3.3 * mm});
            skCircle(sketch, "E2.8.15.0", {"center": v(-355.6, 177.8) * mm, "radius": 3.3 * mm});
            skCircle(sketch, "E2.8.16.0", {"center": v(-355.6, 152.4) * mm, "radius": 3.3 * mm});
            skCircle(sketch, "E2.8.17.0", {"center": v(-355.6, 127) * mm, "radius": 3.3 * mm});
            skCircle(sketch, "E2.8.18.0", {"center": v(-355.6, 101.6) * mm, "radius": 3.3 * mm});
            skCircle(sketch, "E2.8.19.0", {"center": v(-355.6, 76.2) * mm, "radius": 3.3 * mm});
            skCircle(sketch, "E2.8.20.0", {"center": v(-355.6, 50.8) * mm, "radius": 3.3 * mm});
            skCircle(sketch, "E2.8.21.0", {"center": v(-355.6, 25.4) * mm, "radius": 3.3 * mm});
            skCircle(sketch, "E2.8.22.0", {"center": v(-355.6, 0) * mm, "radius": 3.3 * mm});
            skCircle(sketch, "E2.8.23.0", {"center": v(-355.6, -25.4) * mm, "radius": 3.3 * mm});
            skCircle(sketch, "E2.8.24.0", {"center": v(-355.6, -50.8) * mm, "radius": 3.3 * mm});
            skCircle(sketch, "E2.8.25.0", {"center": v(-355.6, -76.2) * mm, "radius": 3.3 * mm});
            skCircle(sketch, "E2.8.26.0", {"center": v(-355.6, -101.6) * mm, "radius": 3.3 * mm});
            skCircle(sketch, "E2.8.27.0", {"center": v(-355.6, -127) * mm, "radius": 3.3 * mm});
            skCircle(sketch, "E2.8.28.0", {"center": v(-355.6, -152.4) * mm, "radius": 3.3 * mm});
            skCircle(sketch, "E2.8.29.0", {"center": v(-355.6, -177.8) * mm, "radius": 3.3 * mm});
            skCircle(sketch, "E2.8.30.0", {"center": v(-355.6, -203.2) * mm, "radius": 3.3 * mm});
            skCircle(sketch, "E2.8.31.0", {"center": v(-355.6, -228.6) * mm, "radius": 3.3 * mm});
            skCircle(sketch, "E2.8.32.0", {"center": v(-355.6, -254) * mm, "radius": 3.3 * mm});
            skCircle(sketch, "E2.8.33.0", {"center": v(-355.6, -279.4) * mm, "radius": 3.3 * mm});
            skCircle(sketch, "E2.8.34.0", {"center": v(-355.6, -304.8) * mm, "radius": 3.3 * mm});
            skCircle(sketch, "E2.8.35.0", {"center": v(-355.6, -330.2) * mm, "radius": 3.3 * mm});
            skCircle(sketch, "E2.8.36.0", {"center": v(-355.6, -355.6) * mm, "radius": 3.3 * mm});
            skCircle(sketch, "E2.8.37.0", {"center": v(-355.6, -381) * mm, "radius": 3.3 * mm});
            skCircle(sketch, "E2.8.38.0", {"center": v(-355.6, -406.4) * mm, "radius": 3.3 * mm});
            skCircle(sketch, "E2.8.39.0", {"center": v(-355.6, -431.8) * mm, "radius": 3.3 * mm});
            skCircle(sketch, "E2.8.40.0", {"center": v(-355.6, -457.2) * mm, "radius": 3.3 * mm});
            skCircle(sketch, "E2.8.41.0", {"center": v(-355.6, -482.6) * mm, "radius": 3.3 * mm});
            skCircle(sketch, "E2.8.42.0", {"center": v(-355.6, -508) * mm, "radius": 3.3 * mm});
            skCircle(sketch, "E2.8.43.0", {"center": v(-355.6, -533.4) * mm, "radius": 3.3 * mm});
            skCircle(sketch, "E2.8.44.0", {"center": v(-355.6, -558.8) * mm, "radius": 3.3 * mm});
            skCircle(sketch, "E2.9.0.0", {"center": v(-330.2, 558.8) * mm, "radius": 3.3 * mm});
            skCircle(sketch, "E2.9.1.0", {"center": v(-330.2, 533.4) * mm, "radius": 3.3 * mm});
            skCircle(sketch, "E2.9.2.0", {"center": v(-330.2, 508) * mm, "radius": 3.3 * mm});
            skCircle(sketch, "E2.9.3.0", {"center": v(-330.2, 482.6) * mm, "radius": 3.3 * mm});
            skCircle(sketch, "E2.9.4.0", {"center": v(-330.2, 457.2) * mm, "radius": 3.3 * mm});
            skCircle(sketch, "E2.9.5.0", {"center": v(-330.2, 431.8) * mm, "radius": 3.3 * mm});
            skCircle(sketch, "E2.9.6.0", {"center": v(-330.2, 406.4) * mm, "radius": 3.3 * mm});
            skCircle(sketch, "E2.9.7.0", {"center": v(-330.2, 381) * mm, "radius": 3.3 * mm});
            skCircle(sketch, "E2.9.8.0", {"center": v(-330.2, 355.6) * mm, "radius": 3.3 * mm});
            skCircle(sketch, "E2.9.9.0", {"center": v(-330.2, 330.2) * mm, "radius": 3.3 * mm});
            skCircle(sketch, "E2.9.10.0", {"center": v(-330.2, 304.8) * mm, "radius": 3.3 * mm});
            skCircle(sketch, "E2.9.11.0", {"center": v(-330.2, 279.4) * mm, "radius": 3.3 * mm});
            skCircle(sketch, "E2.9.12.0", {"center": v(-330.2, 254) * mm, "radius": 3.3 * mm});
            skCircle(sketch, "E2.9.13.0", {"center": v(-330.2, 228.6) * mm, "radius": 3.3 * mm});
            skCircle(sketch, "E2.9.14.0", {"center": v(-330.2, 203.2) * mm, "radius": 3.3 * mm});
            skCircle(sketch, "E2.9.15.0", {"center": v(-330.2, 177.8) * mm, "radius": 3.3 * mm});
            skCircle(sketch, "E2.9.16.0", {"center": v(-330.2, 152.4) * mm, "radius": 3.3 * mm});
            skCircle(sketch, "E2.9.17.0", {"center": v(-330.2, 127) * mm, "radius": 3.3 * mm});
            skCircle(sketch, "E2.9.18.0", {"center": v(-330.2, 101.6) * mm, "radius": 3.3 * mm});
            skCircle(sketch, "E2.9.19.0", {"center": v(-330.2, 76.2) * mm, "radius": 3.3 * mm});
            skCircle(sketch, "E2.9.20.0", {"center": v(-330.2, 50.8) * mm, "radius": 3.3 * mm});
            skCircle(sketch, "E2.9.21.0", {"center": v(-330.2, 25.4) * mm, "radius": 3.3 * mm});
            skCircle(sketch, "E2.9.22.0", {"center": v(-330.2, 0) * mm, "radius": 3.3 * mm});
            skCircle(sketch, "E2.9.23.0", {"center": v(-330.2, -25.4) * mm, "radius": 3.3 * mm});
            skCircle(sketch, "E2.9.24.0", {"center": v(-330.2, -50.8) * mm, "radius": 3.3 * mm});
            skCircle(sketch, "E2.9.25.0", {"center": v(-330.2, -76.2) * mm, "radius": 3.3 * mm});
            skCircle(sketch, "E2.9.26.0", {"center": v(-330.2, -101.6) * mm, "radius": 3.3 * mm});
            skCircle(sketch, "E2.9.27.0", {"center": v(-330.2, -127) * mm, "radius": 3.3 * mm});
            skCircle(sketch, "E2.9.28.0", {"center": v(-330.2, -152.4) * mm, "radius": 3.3 * mm});
            skCircle(sketch, "E2.9.29.0", {"center": v(-330.2, -177.8) * mm, "radius": 3.3 * mm});
            skCircle(sketch, "E2.9.30.0", {"center": v(-330.2, -203.2) * mm, "radius": 3.3 * mm});
            skCircle(sketch, "E2.9.31.0", {"center": v(-330.2, -228.6) * mm, "radius": 3.3 * mm});
            skCircle(sketch, "E2.9.32.0", {"center": v(-330.2, -254) * mm, "radius": 3.3 * mm});
            skCircle(sketch, "E2.9.33.0", {"center": v(-330.2, -279.4) * mm, "radius": 3.3 * mm});
            skCircle(sketch, "E2.9.34.0", {"center": v(-330.2, -304.8) * mm, "radius": 3.3 * mm});
            skCircle(sketch, "E2.9.35.0", {"center": v(-330.2, -330.2) * mm, "radius": 3.3 * mm});
            skCircle(sketch, "E2.9.36.0", {"center": v(-330.2, -355.6) * mm, "radius": 3.3 * mm});
            skCircle(sketch, "E2.9.37.0", {"center": v(-330.2, -381) * mm, "radius": 3.3 * mm});
            skCircle(sketch, "E2.9.38.0", {"center": v(-330.2, -406.4) * mm, "radius": 3.3 * mm});
            skCircle(sketch, "E2.9.39.0", {"center": v(-330.2, -431.8) * mm, "radius": 3.3 * mm});
            skCircle(sketch, "E2.9.40.0", {"center": v(-330.2, -457.2) * mm, "radius": 3.3 * mm});
            skCircle(sketch, "E2.9.41.0", {"center": v(-330.2, -482.6) * mm, "radius": 3.3 * mm});
            skCircle(sketch, "E2.9.42.0", {"center": v(-330.2, -508) * mm, "radius": 3.3 * mm});
            skCircle(sketch, "E2.9.43.0", {"center": v(-330.2, -533.4) * mm, "radius": 3.3 * mm});
            skCircle(sketch, "E2.9.44.0", {"center": v(-330.2, -558.8) * mm, "radius": 3.3 * mm});
            skCircle(sketch, "E2.10.0.0", {"center": v(-304.8, 558.8) * mm, "radius": 3.3 * mm});
            skCircle(sketch, "E2.10.1.0", {"center": v(-304.8, 533.4) * mm, "radius": 3.3 * mm});
            skCircle(sketch, "E2.10.2.0", {"center": v(-304.8, 508) * mm, "radius": 3.3 * mm});
            skCircle(sketch, "E2.10.3.0", {"center": v(-304.8, 482.6) * mm, "radius": 3.3 * mm});
            skCircle(sketch, "E2.10.4.0", {"center": v(-304.8, 457.2) * mm, "radius": 3.3 * mm});
            skCircle(sketch, "E2.10.5.0", {"center": v(-304.8, 431.8) * mm, "radius": 3.3 * mm});
            skCircle(sketch, "E2.10.6.0", {"center": v(-304.8, 406.4) * mm, "radius": 3.3 * mm});
            skCircle(sketch, "E2.10.7.0", {"center": v(-304.8, 381) * mm, "radius": 3.3 * mm});
            skCircle(sketch, "E2.10.8.0", {"center": v(-304.8, 355.6) * mm, "radius": 3.3 * mm});
            skCircle(sketch, "E2.10.9.0", {"center": v(-304.8, 330.2) * mm, "radius": 3.3 * mm});
            skCircle(sketch, "E2.10.10.0", {"center": v(-304.8, 304.8) * mm, "radius": 3.3 * mm});
            skCircle(sketch, "E2.10.11.0", {"center": v(-304.8, 279.4) * mm, "radius": 3.3 * mm});
            skCircle(sketch, "E2.10.12.0", {"center": v(-304.8, 254) * mm, "radius": 3.3 * mm});
            skCircle(sketch, "E2.10.13.0", {"center": v(-304.8, 228.6) * mm, "radius": 3.3 * mm});
            skCircle(sketch, "E2.10.14.0", {"center": v(-304.8, 203.2) * mm, "radius": 3.3 * mm});
            skCircle(sketch, "E2.10.15.0", {"center": v(-304.8, 177.8) * mm, "radius": 3.3 * mm});
            skCircle(sketch, "E2.10.16.0", {"center": v(-304.8, 152.4) * mm, "radius": 3.3 * mm});
            skCircle(sketch, "E2.10.17.0", {"center": v(-304.8, 127) * mm, "radius": 3.3 * mm});
            skCircle(sketch, "E2.10.18.0", {"center": v(-304.8, 101.6) * mm, "radius": 3.3 * mm});
            skCircle(sketch, "E2.10.19.0", {"center": v(-304.8, 76.2) * mm, "radius": 3.3 * mm});
            skCircle(sketch, "E2.10.20.0", {"center": v(-304.8, 50.8) * mm, "radius": 3.3 * mm});
            skCircle(sketch, "E2.10.21.0", {"center": v(-304.8, 25.4) * mm, "radius": 3.3 * mm});
            skCircle(sketch, "E2.10.22.0", {"center": v(-304.8, 0) * mm, "radius": 3.3 * mm});
            skCircle(sketch, "E2.10.23.0", {"center": v(-304.8, -25.4) * mm, "radius": 3.3 * mm});
            skCircle(sketch, "E2.10.24.0", {"center": v(-304.8, -50.8) * mm, "radius": 3.3 * mm});
            skCircle(sketch, "E2.10.25.0", {"center": v(-304.8, -76.2) * mm, "radius": 3.3 * mm});
            skCircle(sketch, "E2.10.26.0", {"center": v(-304.8, -101.6) * mm, "radius": 3.3 * mm});
            skCircle(sketch, "E2.10.27.0", {"center": v(-304.8, -127) * mm, "radius": 3.3 * mm});
            skCircle(sketch, "E2.10.28.0", {"center": v(-304.8, -152.4) * mm, "radius": 3.3 * mm});
            skCircle(sketch, "E2.10.29.0", {"center": v(-304.8, -177.8) * mm, "radius": 3.3 * mm});
            skCircle(sketch, "E2.10.30.0", {"center": v(-304.8, -203.2) * mm, "radius": 3.3 * mm});
            skCircle(sketch, "E2.10.31.0", {"center": v(-304.8, -228.6) * mm, "radius": 3.3 * mm});
            skCircle(sketch, "E2.10.32.0", {"center": v(-304.8, -254) * mm, "radius": 3.3 * mm});
            skCircle(sketch, "E2.10.33.0", {"center": v(-304.8, -279.4) * mm, "radius": 3.3 * mm});
            skCircle(sketch, "E2.10.34.0", {"center": v(-304.8, -304.8) * mm, "radius": 3.3 * mm});
            skCircle(sketch, "E2.10.35.0", {"center": v(-304.8, -330.2) * mm, "radius": 3.3 * mm});
            skCircle(sketch, "E2.10.36.0", {"center": v(-304.8, -355.6) * mm, "radius": 3.3 * mm});
            skCircle(sketch, "E2.10.37.0", {"center": v(-304.8, -381) * mm, "radius": 3.3 * mm});
            skCircle(sketch, "E2.10.38.0", {"center": v(-304.8, -406.4) * mm, "radius": 3.3 * mm});
            skCircle(sketch, "E2.10.39.0", {"center": v(-304.8, -431.8) * mm, "radius": 3.3 * mm});
            skCircle(sketch, "E2.10.40.0", {"center": v(-304.8, -457.2) * mm, "radius": 3.3 * mm});
            skCircle(sketch, "E2.10.41.0", {"center": v(-304.8, -482.6) * mm, "radius": 3.3 * mm});
            skCircle(sketch, "E2.10.42.0", {"center": v(-304.8, -508) * mm, "radius": 3.3 * mm});
            skCircle(sketch, "E2.10.43.0", {"center": v(-304.8, -533.4) * mm, "radius": 3.3 * mm});
            skCircle(sketch, "E2.10.44.0", {"center": v(-304.8, -558.8) * mm, "radius": 3.3 * mm});
            skCircle(sketch, "E2.11.0.0", {"center": v(-279.4, 558.8) * mm, "radius": 3.3 * mm});
            skCircle(sketch, "E2.11.1.0", {"center": v(-279.4, 533.4) * mm, "radius": 3.3 * mm});
            skCircle(sketch, "E2.11.2.0", {"center": v(-279.4, 508) * mm, "radius": 3.3 * mm});
            skCircle(sketch, "E2.11.3.0", {"center": v(-279.4, 482.6) * mm, "radius": 3.3 * mm});
            skCircle(sketch, "E2.11.4.0", {"center": v(-279.4, 457.2) * mm, "radius": 3.3 * mm});
            skCircle(sketch, "E2.11.5.0", {"center": v(-279.4, 431.8) * mm, "radius": 3.3 * mm});
            skCircle(sketch, "E2.11.6.0", {"center": v(-279.4, 406.4) * mm, "radius": 3.3 * mm});
            skCircle(sketch, "E2.11.7.0", {"center": v(-279.4, 381) * mm, "radius": 3.3 * mm});
            skCircle(sketch, "E2.11.8.0", {"center": v(-279.4, 355.6) * mm, "radius": 3.3 * mm});
            skCircle(sketch, "E2.11.9.0", {"center": v(-279.4, 330.2) * mm, "radius": 3.3 * mm});
            skCircle(sketch, "E2.11.10.0", {"center": v(-279.4, 304.8) * mm, "radius": 3.3 * mm});
            skCircle(sketch, "E2.11.11.0", {"center": v(-279.4, 279.4) * mm, "radius": 3.3 * mm});
            skCircle(sketch, "E2.11.12.0", {"center": v(-279.4, 254) * mm, "radius": 3.3 * mm});
            skCircle(sketch, "E2.11.13.0", {"center": v(-279.4, 228.6) * mm, "radius": 3.3 * mm});
            skCircle(sketch, "E2.11.14.0", {"center": v(-279.4, 203.2) * mm, "radius": 3.3 * mm});
            skCircle(sketch, "E2.11.15.0", {"center": v(-279.4, 177.8) * mm, "radius": 3.3 * mm});
            skCircle(sketch, "E2.11.16.0", {"center": v(-279.4, 152.4) * mm, "radius": 3.3 * mm});
            skCircle(sketch, "E2.11.17.0", {"center": v(-279.4, 127) * mm, "radius": 3.3 * mm});
            skCircle(sketch, "E2.11.18.0", {"center": v(-279.4, 101.6) * mm, "radius": 3.3 * mm});
            skCircle(sketch, "E2.11.19.0", {"center": v(-279.4, 76.2) * mm, "radius": 3.3 * mm});
            skCircle(sketch, "E2.11.20.0", {"center": v(-279.4, 50.8) * mm, "radius": 3.3 * mm});
            skCircle(sketch, "E2.11.21.0", {"center": v(-279.4, 25.4) * mm, "radius": 3.3 * mm});
            skCircle(sketch, "E2.11.22.0", {"center": v(-279.4, 0) * mm, "radius": 3.3 * mm});
            skCircle(sketch, "E2.11.23.0", {"center": v(-279.4, -25.4) * mm, "radius": 3.3 * mm});
            skCircle(sketch, "E2.11.24.0", {"center": v(-279.4, -50.8) * mm, "radius": 3.3 * mm});
            skCircle(sketch, "E2.11.25.0", {"center": v(-279.4, -76.2) * mm, "radius": 3.3 * mm});
            skCircle(sketch, "E2.11.26.0", {"center": v(-279.4, -101.6) * mm, "radius": 3.3 * mm});
            skCircle(sketch, "E2.11.27.0", {"center": v(-279.4, -127) * mm, "radius": 3.3 * mm});
            skCircle(sketch, "E2.11.28.0", {"center": v(-279.4, -152.4) * mm, "radius": 3.3 * mm});
            skCircle(sketch, "E2.11.29.0", {"center": v(-279.4, -177.8) * mm, "radius": 3.3 * mm});
            skCircle(sketch, "E2.11.30.0", {"center": v(-279.4, -203.2) * mm, "radius": 3.3 * mm});
            skCircle(sketch, "E2.11.31.0", {"center": v(-279.4, -228.6) * mm, "radius": 3.3 * mm});
            skCircle(sketch, "E2.11.32.0", {"center": v(-279.4, -254) * mm, "radius": 3.3 * mm});
            skCircle(sketch, "E2.11.33.0", {"center": v(-279.4, -279.4) * mm, "radius": 3.3 * mm});
            skCircle(sketch, "E2.11.34.0", {"center": v(-279.4, -304.8) * mm, "radius": 3.3 * mm});
            skCircle(sketch, "E2.11.35.0", {"center": v(-279.4, -330.2) * mm, "radius": 3.3 * mm});
            skCircle(sketch, "E2.11.36.0", {"center": v(-279.4, -355.6) * mm, "radius": 3.3 * mm});
            skCircle(sketch, "E2.11.37.0", {"center": v(-279.4, -381) * mm, "radius": 3.3 * mm});
            skCircle(sketch, "E2.11.38.0", {"center": v(-279.4, -406.4) * mm, "radius": 3.3 * mm});
            skCircle(sketch, "E2.11.39.0", {"center": v(-279.4, -431.8) * mm, "radius": 3.3 * mm});
            skCircle(sketch, "E2.11.40.0", {"center": v(-279.4, -457.2) * mm, "radius": 3.3 * mm});
            skCircle(sketch, "E2.11.41.0", {"center": v(-279.4, -482.6) * mm, "radius": 3.3 * mm});
            skCircle(sketch, "E2.11.42.0", {"center": v(-279.4, -508) * mm, "radius": 3.3 * mm});
            skCircle(sketch, "E2.11.43.0", {"center": v(-279.4, -533.4) * mm, "radius": 3.3 * mm});
            skCircle(sketch, "E2.11.44.0", {"center": v(-279.4, -558.8) * mm, "radius": 3.3 * mm});
            skCircle(sketch, "E2.12.0.0", {"center": v(-254, 558.8) * mm, "radius": 3.3 * mm});
            skCircle(sketch, "E2.12.1.0", {"center": v(-254, 533.4) * mm, "radius": 3.3 * mm});
            skCircle(sketch, "E2.12.2.0", {"center": v(-254, 508) * mm, "radius": 3.3 * mm});
            skCircle(sketch, "E2.12.3.0", {"center": v(-254, 482.6) * mm, "radius": 3.3 * mm});
            skCircle(sketch, "E2.12.4.0", {"center": v(-254, 457.2) * mm, "radius": 3.3 * mm});
            skCircle(sketch, "E2.12.5.0", {"center": v(-254, 431.8) * mm, "radius": 3.3 * mm});
            skCircle(sketch, "E2.12.6.0", {"center": v(-254, 406.4) * mm, "radius": 3.3 * mm});
            skCircle(sketch, "E2.12.7.0", {"center": v(-254, 381) * mm, "radius": 3.3 * mm});
            skCircle(sketch, "E2.12.8.0", {"center": v(-254, 355.6) * mm, "radius": 3.3 * mm});
            skCircle(sketch, "E2.12.9.0", {"center": v(-254, 330.2) * mm, "radius": 3.3 * mm});
            skCircle(sketch, "E2.12.10.0", {"center": v(-254, 304.8) * mm, "radius": 3.3 * mm});
            skCircle(sketch, "E2.12.11.0", {"center": v(-254, 279.4) * mm, "radius": 3.3 * mm});
            skCircle(sketch, "E2.12.12.0", {"center": v(-254, 254) * mm, "radius": 3.3 * mm});
            skCircle(sketch, "E2.12.13.0", {"center": v(-254, 228.6) * mm, "radius": 3.3 * mm});
            skCircle(sketch, "E2.12.14.0", {"center": v(-254, 203.2) * mm, "radius": 3.3 * mm});
            skCircle(sketch, "E2.12.15.0", {"center": v(-254, 177.8) * mm, "radius": 3.3 * mm});
            skCircle(sketch, "E2.12.16.0", {"center": v(-254, 152.4) * mm, "radius": 3.3 * mm});
            skCircle(sketch, "E2.12.17.0", {"center": v(-254, 127) * mm, "radius": 3.3 * mm});
            skCircle(sketch, "E2.12.18.0", {"center": v(-254, 101.6) * mm, "radius": 3.3 * mm});
            skCircle(sketch, "E2.12.19.0", {"center": v(-254, 76.2) * mm, "radius": 3.3 * mm});
            skCircle(sketch, "E2.12.20.0", {"center": v(-254, 50.8) * mm, "radius": 3.3 * mm});
            skCircle(sketch, "E2.12.21.0", {"center": v(-254, 25.4) * mm, "radius": 3.3 * mm});
            skCircle(sketch, "E2.12.22.0", {"center": v(-254, 0) * mm, "radius": 3.3 * mm});
            skCircle(sketch, "E2.12.23.0", {"center": v(-254, -25.4) * mm, "radius": 3.3 * mm});
            skCircle(sketch, "E2.12.24.0", {"center": v(-254, -50.8) * mm, "radius": 3.3 * mm});
            skCircle(sketch, "E2.12.25.0", {"center": v(-254, -76.2) * mm, "radius": 3.3 * mm});
            skCircle(sketch, "E2.12.26.0", {"center": v(-254, -101.6) * mm, "radius": 3.3 * mm});
            skCircle(sketch, "E2.12.27.0", {"center": v(-254, -127) * mm, "radius": 3.3 * mm});
            skCircle(sketch, "E2.12.28.0", {"center": v(-254, -152.4) * mm, "radius": 3.3 * mm});
            skCircle(sketch, "E2.12.29.0", {"center": v(-254, -177.8) * mm, "radius": 3.3 * mm});
            skCircle(sketch, "E2.12.30.0", {"center": v(-254, -203.2) * mm, "radius": 3.3 * mm});
            skCircle(sketch, "E2.12.31.0", {"center": v(-254, -228.6) * mm, "radius": 3.3 * mm});
            skCircle(sketch, "E2.12.32.0", {"center": v(-254, -254) * mm, "radius": 3.3 * mm});
            skCircle(sketch, "E2.12.33.0", {"center": v(-254, -279.4) * mm, "radius": 3.3 * mm});
            skCircle(sketch, "E2.12.34.0", {"center": v(-254, -304.8) * mm, "radius": 3.3 * mm});
            skCircle(sketch, "E2.12.35.0", {"center": v(-254, -330.2) * mm, "radius": 3.3 * mm});
            skCircle(sketch, "E2.12.36.0", {"center": v(-254, -355.6) * mm, "radius": 3.3 * mm});
            skCircle(sketch, "E2.12.37.0", {"center": v(-254, -381) * mm, "radius": 3.3 * mm});
            skCircle(sketch, "E2.12.38.0", {"center": v(-254, -406.4) * mm, "radius": 3.3 * mm});
            skCircle(sketch, "E2.12.39.0", {"center": v(-254, -431.8) * mm, "radius": 3.3 * mm});
            skCircle(sketch, "E2.12.40.0", {"center": v(-254, -457.2) * mm, "radius": 3.3 * mm});
            skCircle(sketch, "E2.12.41.0", {"center": v(-254, -482.6) * mm, "radius": 3.3 * mm});
            skCircle(sketch, "E2.12.42.0", {"center": v(-254, -508) * mm, "radius": 3.3 * mm});
            skCircle(sketch, "E2.12.43.0", {"center": v(-254, -533.4) * mm, "radius": 3.3 * mm});
            skCircle(sketch, "E2.12.44.0", {"center": v(-254, -558.8) * mm, "radius": 3.3 * mm});
            skCircle(sketch, "E2.13.0.0", {"center": v(-228.6, 558.8) * mm, "radius": 3.3 * mm});
            skCircle(sketch, "E2.13.1.0", {"center": v(-228.6, 533.4) * mm, "radius": 3.3 * mm});
            skCircle(sketch, "E2.13.2.0", {"center": v(-228.6, 508) * mm, "radius": 3.3 * mm});
            skCircle(sketch, "E2.13.3.0", {"center": v(-228.6, 482.6) * mm, "radius": 3.3 * mm});
            skCircle(sketch, "E2.13.4.0", {"center": v(-228.6, 457.2) * mm, "radius": 3.3 * mm});
            skCircle(sketch, "E2.13.5.0", {"center": v(-228.6, 431.8) * mm, "radius": 3.3 * mm});
            skCircle(sketch, "E2.13.6.0", {"center": v(-228.6, 406.4) * mm, "radius": 3.3 * mm});
            skCircle(sketch, "E2.13.7.0", {"center": v(-228.6, 381) * mm, "radius": 3.3 * mm});
            skCircle(sketch, "E2.13.8.0", {"center": v(-228.6, 355.6) * mm, "radius": 3.3 * mm});
            skCircle(sketch, "E2.13.9.0", {"center": v(-228.6, 330.2) * mm, "radius": 3.3 * mm});
            skCircle(sketch, "E2.13.10.0", {"center": v(-228.6, 304.8) * mm, "radius": 3.3 * mm});
            skCircle(sketch, "E2.13.11.0", {"center": v(-228.6, 279.4) * mm, "radius": 3.3 * mm});
            skCircle(sketch, "E2.13.12.0", {"center": v(-228.6, 254) * mm, "radius": 3.3 * mm});
            skCircle(sketch, "E2.13.13.0", {"center": v(-228.6, 228.6) * mm, "radius": 3.3 * mm});
            skCircle(sketch, "E2.13.14.0", {"center": v(-228.6, 203.2) * mm, "radius": 3.3 * mm});
            skCircle(sketch, "E2.13.15.0", {"center": v(-228.6, 177.8) * mm, "radius": 3.3 * mm});
            skCircle(sketch, "E2.13.16.0", {"center": v(-228.6, 152.4) * mm, "radius": 3.3 * mm});
            skCircle(sketch, "E2.13.17.0", {"center": v(-228.6, 127) * mm, "radius": 3.3 * mm});
            skCircle(sketch, "E2.13.18.0", {"center": v(-228.6, 101.6) * mm, "radius": 3.3 * mm});
            skCircle(sketch, "E2.13.19.0", {"center": v(-228.6, 76.2) * mm, "radius": 3.3 * mm});
            skCircle(sketch, "E2.13.20.0", {"center": v(-228.6, 50.8) * mm, "radius": 3.3 * mm});
            skCircle(sketch, "E2.13.21.0", {"center": v(-228.6, 25.4) * mm, "radius": 3.3 * mm});
            skCircle(sketch, "E2.13.22.0", {"center": v(-228.6, 0) * mm, "radius": 3.3 * mm});
            skCircle(sketch, "E2.13.23.0", {"center": v(-228.6, -25.4) * mm, "radius": 3.3 * mm});
            skCircle(sketch, "E2.13.24.0", {"center": v(-228.6, -50.8) * mm, "radius": 3.3 * mm});
            skCircle(sketch, "E2.13.25.0", {"center": v(-228.6, -76.2) * mm, "radius": 3.3 * mm});
            skCircle(sketch, "E2.13.26.0", {"center": v(-228.6, -101.6) * mm, "radius": 3.3 * mm});
            skCircle(sketch, "E2.13.27.0", {"center": v(-228.6, -127) * mm, "radius": 3.3 * mm});
            skCircle(sketch, "E2.13.28.0", {"center": v(-228.6, -152.4) * mm, "radius": 3.3 * mm});
            skCircle(sketch, "E2.13.29.0", {"center": v(-228.6, -177.8) * mm, "radius": 3.3 * mm});
            skCircle(sketch, "E2.13.30.0", {"center": v(-228.6, -203.2) * mm, "radius": 3.3 * mm});
            skCircle(sketch, "E2.13.31.0", {"center": v(-228.6, -228.6) * mm, "radius": 3.3 * mm});
            skCircle(sketch, "E2.13.32.0", {"center": v(-228.6, -254) * mm, "radius": 3.3 * mm});
            skCircle(sketch, "E2.13.33.0", {"center": v(-228.6, -279.4) * mm, "radius": 3.3 * mm});
            skCircle(sketch, "E2.13.34.0", {"center": v(-228.6, -304.8) * mm, "radius": 3.3 * mm});
            skCircle(sketch, "E2.13.35.0", {"center": v(-228.6, -330.2) * mm, "radius": 3.3 * mm});
            skCircle(sketch, "E2.13.36.0", {"center": v(-228.6, -355.6) * mm, "radius": 3.3 * mm});
            skCircle(sketch, "E2.13.37.0", {"center": v(-228.6, -381) * mm, "radius": 3.3 * mm});
            skCircle(sketch, "E2.13.38.0", {"center": v(-228.6, -406.4) * mm, "radius": 3.3 * mm});
            skCircle(sketch, "E2.13.39.0", {"center": v(-228.6, -431.8) * mm, "radius": 3.3 * mm});
            skCircle(sketch, "E2.13.40.0", {"center": v(-228.6, -457.2) * mm, "radius": 3.3 * mm});
            skCircle(sketch, "E2.13.41.0", {"center": v(-228.6, -482.6) * mm, "radius": 3.3 * mm});
            skCircle(sketch, "E2.13.42.0", {"center": v(-228.6, -508) * mm, "radius": 3.3 * mm});
            skCircle(sketch, "E2.13.43.0", {"center": v(-228.6, -533.4) * mm, "radius": 3.3 * mm});
            skCircle(sketch, "E2.13.44.0", {"center": v(-228.6, -558.8) * mm, "radius": 3.3 * mm});
            skCircle(sketch, "E2.14.0.0", {"center": v(-203.2, 558.8) * mm, "radius": 3.3 * mm});
            skCircle(sketch, "E2.14.1.0", {"center": v(-203.2, 533.4) * mm, "radius": 3.3 * mm});
            skCircle(sketch, "E2.14.2.0", {"center": v(-203.2, 508) * mm, "radius": 3.3 * mm});
            skCircle(sketch, "E2.14.3.0", {"center": v(-203.2, 482.6) * mm, "radius": 3.3 * mm});
            skCircle(sketch, "E2.14.4.0", {"center": v(-203.2, 457.2) * mm, "radius": 3.3 * mm});
            skCircle(sketch, "E2.14.5.0", {"center": v(-203.2, 431.8) * mm, "radius": 3.3 * mm});
            skCircle(sketch, "E2.14.6.0", {"center": v(-203.2, 406.4) * mm, "radius": 3.3 * mm});
            skCircle(sketch, "E2.14.7.0", {"center": v(-203.2, 381) * mm, "radius": 3.3 * mm});
            skCircle(sketch, "E2.14.8.0", {"center": v(-203.2, 355.6) * mm, "radius": 3.3 * mm});
            skCircle(sketch, "E2.14.9.0", {"center": v(-203.2, 330.2) * mm, "radius": 3.3 * mm});
            skCircle(sketch, "E2.14.10.0", {"center": v(-203.2, 304.8) * mm, "radius": 3.3 * mm});
            skCircle(sketch, "E2.14.11.0", {"center": v(-203.2, 279.4) * mm, "radius": 3.3 * mm});
            skCircle(sketch, "E2.14.12.0", {"center": v(-203.2, 254) * mm, "radius": 3.3 * mm});
            skCircle(sketch, "E2.14.13.0", {"center": v(-203.2, 228.6) * mm, "radius": 3.3 * mm});
            skCircle(sketch, "E2.14.14.0", {"center": v(-203.2, 203.2) * mm, "radius": 3.3 * mm});
            skCircle(sketch, "E2.14.15.0", {"center": v(-203.2, 177.8) * mm, "radius": 3.3 * mm});
            skCircle(sketch, "E2.14.16.0", {"center": v(-203.2, 152.4) * mm, "radius": 3.3 * mm});
            skCircle(sketch, "E2.14.17.0", {"center": v(-203.2, 127) * mm, "radius": 3.3 * mm});
            skCircle(sketch, "E2.14.18.0", {"center": v(-203.2, 101.6) * mm, "radius": 3.3 * mm});
            skCircle(sketch, "E2.14.19.0", {"center": v(-203.2, 76.2) * mm, "radius": 3.3 * mm});
            skCircle(sketch, "E2.14.20.0", {"center": v(-203.2, 50.8) * mm, "radius": 3.3 * mm});
            skCircle(sketch, "E2.14.21.0", {"center": v(-203.2, 25.4) * mm, "radius": 3.3 * mm});
            skCircle(sketch, "E2.14.22.0", {"center": v(-203.2, 0) * mm, "radius": 3.3 * mm});
            skCircle(sketch, "E2.14.23.0", {"center": v(-203.2, -25.4) * mm, "radius": 3.3 * mm});
            skCircle(sketch, "E2.14.24.0", {"center": v(-203.2, -50.8) * mm, "radius": 3.3 * mm});
            skCircle(sketch, "E2.14.25.0", {"center": v(-203.2, -76.2) * mm, "radius": 3.3 * mm});
            skCircle(sketch, "E2.14.26.0", {"center": v(-203.2, -101.6) * mm, "radius": 3.3 * mm});
            skCircle(sketch, "E2.14.27.0", {"center": v(-203.2, -127) * mm, "radius": 3.3 * mm});
            skCircle(sketch, "E2.14.28.0", {"center": v(-203.2, -152.4) * mm, "radius": 3.3 * mm});
            skCircle(sketch, "E2.14.29.0", {"center": v(-203.2, -177.8) * mm, "radius": 3.3 * mm});
            skCircle(sketch, "E2.14.30.0", {"center": v(-203.2, -203.2) * mm, "radius": 3.3 * mm});
            skCircle(sketch, "E2.14.31.0", {"center": v(-203.2, -228.6) * mm, "radius": 3.3 * mm});
            skCircle(sketch, "E2.14.32.0", {"center": v(-203.2, -254) * mm, "radius": 3.3 * mm});
            skCircle(sketch, "E2.14.33.0", {"center": v(-203.2, -279.4) * mm, "radius": 3.3 * mm});
            skCircle(sketch, "E2.14.34.0", {"center": v(-203.2, -304.8) * mm, "radius": 3.3 * mm});
            skCircle(sketch, "E2.14.35.0", {"center": v(-203.2, -330.2) * mm, "radius": 3.3 * mm});
            skCircle(sketch, "E2.14.36.0", {"center": v(-203.2, -355.6) * mm, "radius": 3.3 * mm});
            skCircle(sketch, "E2.14.37.0", {"center": v(-203.2, -381) * mm, "radius": 3.3 * mm});
            skCircle(sketch, "E2.14.38.0", {"center": v(-203.2, -406.4) * mm, "radius": 3.3 * mm});
            skCircle(sketch, "E2.14.39.0", {"center": v(-203.2, -431.8) * mm, "radius": 3.3 * mm});
            skCircle(sketch, "E2.14.40.0", {"center": v(-203.2, -457.2) * mm, "radius": 3.3 * mm});
            skCircle(sketch, "E2.14.41.0", {"center": v(-203.2, -482.6) * mm, "radius": 3.3 * mm});
            skCircle(sketch, "E2.14.42.0", {"center": v(-203.2, -508) * mm, "radius": 3.3 * mm});
            skCircle(sketch, "E2.14.43.0", {"center": v(-203.2, -533.4) * mm, "radius": 3.3 * mm});
            skCircle(sketch, "E2.14.44.0", {"center": v(-203.2, -558.8) * mm, "radius": 3.3 * mm});
            skCircle(sketch, "E2.15.0.0", {"center": v(-177.8, 558.8) * mm, "radius": 3.3 * mm});
            skCircle(sketch, "E2.15.1.0", {"center": v(-177.8, 533.4) * mm, "radius": 3.3 * mm});
            skCircle(sketch, "E2.15.2.0", {"center": v(-177.8, 508) * mm, "radius": 3.3 * mm});
            skCircle(sketch, "E2.15.3.0", {"center": v(-177.8, 482.6) * mm, "radius": 3.3 * mm});
            skCircle(sketch, "E2.15.4.0", {"center": v(-177.8, 457.2) * mm, "radius": 3.3 * mm});
            skCircle(sketch, "E2.15.5.0", {"center": v(-177.8, 431.8) * mm, "radius": 3.3 * mm});
            skCircle(sketch, "E2.15.6.0", {"center": v(-177.8, 406.4) * mm, "radius": 3.3 * mm});
            skCircle(sketch, "E2.15.7.0", {"center": v(-177.8, 381) * mm, "radius": 3.3 * mm});
            skCircle(sketch, "E2.15.8.0", {"center": v(-177.8, 355.6) * mm, "radius": 3.3 * mm});
            skCircle(sketch, "E2.15.9.0", {"center": v(-177.8, 330.2) * mm, "radius": 3.3 * mm});
            skCircle(sketch, "E2.15.10.0", {"center": v(-177.8, 304.8) * mm, "radius": 3.3 * mm});
            skCircle(sketch, "E2.15.11.0", {"center": v(-177.8, 279.4) * mm, "radius": 3.3 * mm});
            skCircle(sketch, "E2.15.12.0", {"center": v(-177.8, 254) * mm, "radius": 3.3 * mm});
            skCircle(sketch, "E2.15.13.0", {"center": v(-177.8, 228.6) * mm, "radius": 3.3 * mm});
            skCircle(sketch, "E2.15.14.0", {"center": v(-177.8, 203.2) * mm, "radius": 3.3 * mm});
            skCircle(sketch, "E2.15.15.0", {"center": v(-177.8, 177.8) * mm, "radius": 3.3 * mm});
            skCircle(sketch, "E2.15.16.0", {"center": v(-177.8, 152.4) * mm, "radius": 3.3 * mm});
            skCircle(sketch, "E2.15.17.0", {"center": v(-177.8, 127) * mm, "radius": 3.3 * mm});
            skCircle(sketch, "E2.15.18.0", {"center": v(-177.8, 101.6) * mm, "radius": 3.3 * mm});
            skCircle(sketch, "E2.15.19.0", {"center": v(-177.8, 76.2) * mm, "radius": 3.3 * mm});
            skCircle(sketch, "E2.15.20.0", {"center": v(-177.8, 50.8) * mm, "radius": 3.3 * mm});
            skCircle(sketch, "E2.15.21.0", {"center": v(-177.8, 25.4) * mm, "radius": 3.3 * mm});
            skCircle(sketch, "E2.15.22.0", {"center": v(-177.8, 0) * mm, "radius": 3.3 * mm});
            skCircle(sketch, "E2.15.23.0", {"center": v(-177.8, -25.4) * mm, "radius": 3.3 * mm});
            skCircle(sketch, "E2.15.24.0", {"center": v(-177.8, -50.8) * mm, "radius": 3.3 * mm});
            skCircle(sketch, "E2.15.25.0", {"center": v(-177.8, -76.2) * mm, "radius": 3.3 * mm});
            skCircle(sketch, "E2.15.26.0", {"center": v(-177.8, -101.6) * mm, "radius": 3.3 * mm});
            skCircle(sketch, "E2.15.27.0", {"center": v(-177.8, -127) * mm, "radius": 3.3 * mm});
            skCircle(sketch, "E2.15.28.0", {"center": v(-177.8, -152.4) * mm, "radius": 3.3 * mm});
            skCircle(sketch, "E2.15.29.0", {"center": v(-177.8, -177.8) * mm, "radius": 3.3 * mm});
            skCircle(sketch, "E2.15.30.0", {"center": v(-177.8, -203.2) * mm, "radius": 3.3 * mm});
            skCircle(sketch, "E2.15.31.0", {"center": v(-177.8, -228.6) * mm, "radius": 3.3 * mm});
            skCircle(sketch, "E2.15.32.0", {"center": v(-177.8, -254) * mm, "radius": 3.3 * mm});
            skCircle(sketch, "E2.15.33.0", {"center": v(-177.8, -279.4) * mm, "radius": 3.3 * mm});
            skCircle(sketch, "E2.15.34.0", {"center": v(-177.8, -304.8) * mm, "radius": 3.3 * mm});
            skCircle(sketch, "E2.15.35.0", {"center": v(-177.8, -330.2) * mm, "radius": 3.3 * mm});
            skCircle(sketch, "E2.15.36.0", {"center": v(-177.8, -355.6) * mm, "radius": 3.3 * mm});
            skCircle(sketch, "E2.15.37.0", {"center": v(-177.8, -381) * mm, "radius": 3.3 * mm});
            skCircle(sketch, "E2.15.38.0", {"center": v(-177.8, -406.4) * mm, "radius": 3.3 * mm});
            skCircle(sketch, "E2.15.39.0", {"center": v(-177.8, -431.8) * mm, "radius": 3.3 * mm});
            skCircle(sketch, "E2.15.40.0", {"center": v(-177.8, -457.2) * mm, "radius": 3.3 * mm});
            skCircle(sketch, "E2.15.41.0", {"center": v(-177.8, -482.6) * mm, "radius": 3.3 * mm});
            skCircle(sketch, "E2.15.42.0", {"center": v(-177.8, -508) * mm, "radius": 3.3 * mm});
            skCircle(sketch, "E2.15.43.0", {"center": v(-177.8, -533.4) * mm, "radius": 3.3 * mm});
            skCircle(sketch, "E2.15.44.0", {"center": v(-177.8, -558.8) * mm, "radius": 3.3 * mm});
            skCircle(sketch, "E2.16.0.0", {"center": v(-152.4, 558.8) * mm, "radius": 3.3 * mm});
            skCircle(sketch, "E2.16.1.0", {"center": v(-152.4, 533.4) * mm, "radius": 3.3 * mm});
            skCircle(sketch, "E2.16.2.0", {"center": v(-152.4, 508) * mm, "radius": 3.3 * mm});
            skCircle(sketch, "E2.16.3.0", {"center": v(-152.4, 482.6) * mm, "radius": 3.3 * mm});
            skCircle(sketch, "E2.16.4.0", {"center": v(-152.4, 457.2) * mm, "radius": 3.3 * mm});
            skCircle(sketch, "E2.16.5.0", {"center": v(-152.4, 431.8) * mm, "radius": 3.3 * mm});
            skCircle(sketch, "E2.16.6.0", {"center": v(-152.4, 406.4) * mm, "radius": 3.3 * mm});
            skCircle(sketch, "E2.16.7.0", {"center": v(-152.4, 381) * mm, "radius": 3.3 * mm});
            skCircle(sketch, "E2.16.8.0", {"center": v(-152.4, 355.6) * mm, "radius": 3.3 * mm});
            skCircle(sketch, "E2.16.9.0", {"center": v(-152.4, 330.2) * mm, "radius": 3.3 * mm});
            skCircle(sketch, "E2.16.10.0", {"center": v(-152.4, 304.8) * mm, "radius": 3.3 * mm});
            skCircle(sketch, "E2.16.11.0", {"center": v(-152.4, 279.4) * mm, "radius": 3.3 * mm});
            skCircle(sketch, "E2.16.12.0", {"center": v(-152.4, 254) * mm, "radius": 3.3 * mm});
            skCircle(sketch, "E2.16.13.0", {"center": v(-152.4, 228.6) * mm, "radius": 3.3 * mm});
            skCircle(sketch, "E2.16.14.0", {"center": v(-152.4, 203.2) * mm, "radius": 3.3 * mm});
            skCircle(sketch, "E2.16.15.0", {"center": v(-152.4, 177.8) * mm, "radius": 3.3 * mm});
            skCircle(sketch, "E2.16.16.0", {"center": v(-152.4, 152.4) * mm, "radius": 3.3 * mm});
            skCircle(sketch, "E2.16.17.0", {"center": v(-152.4, 127) * mm, "radius": 3.3 * mm});
            skCircle(sketch, "E2.16.18.0", {"center": v(-152.4, 101.6) * mm, "radius": 3.3 * mm});
            skCircle(sketch, "E2.16.19.0", {"center": v(-152.4, 76.2) * mm, "radius": 3.3 * mm});
            skCircle(sketch, "E2.16.20.0", {"center": v(-152.4, 50.8) * mm, "radius": 3.3 * mm});
            skCircle(sketch, "E2.16.21.0", {"center": v(-152.4, 25.4) * mm, "radius": 3.3 * mm});
            skCircle(sketch, "E2.16.22.0", {"center": v(-152.4, 0) * mm, "radius": 3.3 * mm});
            skCircle(sketch, "E2.16.23.0", {"center": v(-152.4, -25.4) * mm, "radius": 3.3 * mm});
            skCircle(sketch, "E2.16.24.0", {"center": v(-152.4, -50.8) * mm, "radius": 3.3 * mm});
            skCircle(sketch, "E2.16.25.0", {"center": v(-152.4, -76.2) * mm, "radius": 3.3 * mm});
            skCircle(sketch, "E2.16.26.0", {"center": v(-152.4, -101.6) * mm, "radius": 3.3 * mm});
            skCircle(sketch, "E2.16.27.0", {"center": v(-152.4, -127) * mm, "radius": 3.3 * mm});
            skCircle(sketch, "E2.16.28.0", {"center": v(-152.4, -152.4) * mm, "radius": 3.3 * mm});
            skCircle(sketch, "E2.16.29.0", {"center": v(-152.4, -177.8) * mm, "radius": 3.3 * mm});
            skCircle(sketch, "E2.16.30.0", {"center": v(-152.4, -203.2) * mm, "radius": 3.3 * mm});
            skCircle(sketch, "E2.16.31.0", {"center": v(-152.4, -228.6) * mm, "radius": 3.3 * mm});
            skCircle(sketch, "E2.16.32.0", {"center": v(-152.4, -254) * mm, "radius": 3.3 * mm});
            skCircle(sketch, "E2.16.33.0", {"center": v(-152.4, -279.4) * mm, "radius": 3.3 * mm});
            skCircle(sketch, "E2.16.34.0", {"center": v(-152.4, -304.8) * mm, "radius": 3.3 * mm});
            skCircle(sketch, "E2.16.35.0", {"center": v(-152.4, -330.2) * mm, "radius": 3.3 * mm});
            skCircle(sketch, "E2.16.36.0", {"center": v(-152.4, -355.6) * mm, "radius": 3.3 * mm});
            skCircle(sketch, "E2.16.37.0", {"center": v(-152.4, -381) * mm, "radius": 3.3 * mm});
            skCircle(sketch, "E2.16.38.0", {"center": v(-152.4, -406.4) * mm, "radius": 3.3 * mm});
            skCircle(sketch, "E2.16.39.0", {"center": v(-152.4, -431.8) * mm, "radius": 3.3 * mm});
            skCircle(sketch, "E2.16.40.0", {"center": v(-152.4, -457.2) * mm, "radius": 3.3 * mm});
            skCircle(sketch, "E2.16.41.0", {"center": v(-152.4, -482.6) * mm, "radius": 3.3 * mm});
            skCircle(sketch, "E2.16.42.0", {"center": v(-152.4, -508) * mm, "radius": 3.3 * mm});
            skCircle(sketch, "E2.16.43.0", {"center": v(-152.4, -533.4) * mm, "radius": 3.3 * mm});
            skCircle(sketch, "E2.16.44.0", {"center": v(-152.4, -558.8) * mm, "radius": 3.3 * mm});
            skCircle(sketch, "E2.17.0.0", {"center": v(-127, 558.8) * mm, "radius": 3.3 * mm});
            skCircle(sketch, "E2.17.1.0", {"center": v(-127, 533.4) * mm, "radius": 3.3 * mm});
            skCircle(sketch, "E2.17.2.0", {"center": v(-127, 508) * mm, "radius": 3.3 * mm});
            skCircle(sketch, "E2.17.3.0", {"center": v(-127, 482.6) * mm, "radius": 3.3 * mm});
            skCircle(sketch, "E2.17.4.0", {"center": v(-127, 457.2) * mm, "radius": 3.3 * mm});
            skCircle(sketch, "E2.17.5.0", {"center": v(-127, 431.8) * mm, "radius": 3.3 * mm});
            skCircle(sketch, "E2.17.6.0", {"center": v(-127, 406.4) * mm, "radius": 3.3 * mm});
            skCircle(sketch, "E2.17.7.0", {"center": v(-127, 381) * mm, "radius": 3.3 * mm});
            skCircle(sketch, "E2.17.8.0", {"center": v(-127, 355.6) * mm, "radius": 3.3 * mm});
            skCircle(sketch, "E2.17.9.0", {"center": v(-127, 330.2) * mm, "radius": 3.3 * mm});
            skCircle(sketch, "E2.17.10.0", {"center": v(-127, 304.8) * mm, "radius": 3.3 * mm});
            skCircle(sketch, "E2.17.11.0", {"center": v(-127, 279.4) * mm, "radius": 3.3 * mm});
            skCircle(sketch, "E2.17.12.0", {"center": v(-127, 254) * mm, "radius": 3.3 * mm});
            skCircle(sketch, "E2.17.13.0", {"center": v(-127, 228.6) * mm, "radius": 3.3 * mm});
            skCircle(sketch, "E2.17.14.0", {"center": v(-127, 203.2) * mm, "radius": 3.3 * mm});
            skCircle(sketch, "E2.17.15.0", {"center": v(-127, 177.8) * mm, "radius": 3.3 * mm});
            skCircle(sketch, "E2.17.16.0", {"center": v(-127, 152.4) * mm, "radius": 3.3 * mm});
            skCircle(sketch, "E2.17.17.0", {"center": v(-127, 127) * mm, "radius": 3.3 * mm});
            skCircle(sketch, "E2.17.18.0", {"center": v(-127, 101.6) * mm, "radius": 3.3 * mm});
            skCircle(sketch, "E2.17.19.0", {"center": v(-127, 76.2) * mm, "radius": 3.3 * mm});
            skCircle(sketch, "E2.17.20.0", {"center": v(-127, 50.8) * mm, "radius": 3.3 * mm});
            skCircle(sketch, "E2.17.21.0", {"center": v(-127, 25.4) * mm, "radius": 3.3 * mm});
            skCircle(sketch, "E2.17.22.0", {"center": v(-127, 0) * mm, "radius": 3.3 * mm});
            skCircle(sketch, "E2.17.23.0", {"center": v(-127, -25.4) * mm, "radius": 3.3 * mm});
            skCircle(sketch, "E2.17.24.0", {"center": v(-127, -50.8) * mm, "radius": 3.3 * mm});
            skCircle(sketch, "E2.17.25.0", {"center": v(-127, -76.2) * mm, "radius": 3.3 * mm});
            skCircle(sketch, "E2.17.26.0", {"center": v(-127, -101.6) * mm, "radius": 3.3 * mm});
            skCircle(sketch, "E2.17.27.0", {"center": v(-127, -127) * mm, "radius": 3.3 * mm});
            skCircle(sketch, "E2.17.28.0", {"center": v(-127, -152.4) * mm, "radius": 3.3 * mm});
            skCircle(sketch, "E2.17.29.0", {"center": v(-127, -177.8) * mm, "radius": 3.3 * mm});
            skCircle(sketch, "E2.17.30.0", {"center": v(-127, -203.2) * mm, "radius": 3.3 * mm});
            skCircle(sketch, "E2.17.31.0", {"center": v(-127, -228.6) * mm, "radius": 3.3 * mm});
            skCircle(sketch, "E2.17.32.0", {"center": v(-127, -254) * mm, "radius": 3.3 * mm});
            skCircle(sketch, "E2.17.33.0", {"center": v(-127, -279.4) * mm, "radius": 3.3 * mm});
            skCircle(sketch, "E2.17.34.0", {"center": v(-127, -304.8) * mm, "radius": 3.3 * mm});
            skCircle(sketch, "E2.17.35.0", {"center": v(-127, -330.2) * mm, "radius": 3.3 * mm});
            skCircle(sketch, "E2.17.36.0", {"center": v(-127, -355.6) * mm, "radius": 3.3 * mm});
            skCircle(sketch, "E2.17.37.0", {"center": v(-127, -381) * mm, "radius": 3.3 * mm});
            skCircle(sketch, "E2.17.38.0", {"center": v(-127, -406.4) * mm, "radius": 3.3 * mm});
            skCircle(sketch, "E2.17.39.0", {"center": v(-127, -431.8) * mm, "radius": 3.3 * mm});
            skCircle(sketch, "E2.17.40.0", {"center": v(-127, -457.2) * mm, "radius": 3.3 * mm});
            skCircle(sketch, "E2.17.41.0", {"center": v(-127, -482.6) * mm, "radius": 3.3 * mm});
            skCircle(sketch, "E2.17.42.0", {"center": v(-127, -508) * mm, "radius": 3.3 * mm});
            skCircle(sketch, "E2.17.43.0", {"center": v(-127, -533.4) * mm, "radius": 3.3 * mm});
            skCircle(sketch, "E2.17.44.0", {"center": v(-127, -558.8) * mm, "radius": 3.3 * mm});
            skCircle(sketch, "E2.18.0.0", {"center": v(-101.6, 558.8) * mm, "radius": 3.3 * mm});
            skCircle(sketch, "E2.18.1.0", {"center": v(-101.6, 533.4) * mm, "radius": 3.3 * mm});
            skCircle(sketch, "E2.18.2.0", {"center": v(-101.6, 508) * mm, "radius": 3.3 * mm});
            skCircle(sketch, "E2.18.3.0", {"center": v(-101.6, 482.6) * mm, "radius": 3.3 * mm});
            skCircle(sketch, "E2.18.4.0", {"center": v(-101.6, 457.2) * mm, "radius": 3.3 * mm});
            skCircle(sketch, "E2.18.5.0", {"center": v(-101.6, 431.8) * mm, "radius": 3.3 * mm});
            skCircle(sketch, "E2.18.6.0", {"center": v(-101.6, 406.4) * mm, "radius": 3.3 * mm});
            skCircle(sketch, "E2.18.7.0", {"center": v(-101.6, 381) * mm, "radius": 3.3 * mm});
            skCircle(sketch, "E2.18.8.0", {"center": v(-101.6, 355.6) * mm, "radius": 3.3 * mm});
            skCircle(sketch, "E2.18.9.0", {"center": v(-101.6, 330.2) * mm, "radius": 3.3 * mm});
            skCircle(sketch, "E2.18.10.0", {"center": v(-101.6, 304.8) * mm, "radius": 3.3 * mm});
            skCircle(sketch, "E2.18.11.0", {"center": v(-101.6, 279.4) * mm, "radius": 3.3 * mm});
            skCircle(sketch, "E2.18.12.0", {"center": v(-101.6, 254) * mm, "radius": 3.3 * mm});
            skCircle(sketch, "E2.18.13.0", {"center": v(-101.6, 228.6) * mm, "radius": 3.3 * mm});
            skCircle(sketch, "E2.18.14.0", {"center": v(-101.6, 203.2) * mm, "radius": 3.3 * mm});
            skCircle(sketch, "E2.18.15.0", {"center": v(-101.6, 177.8) * mm, "radius": 3.3 * mm});
            skCircle(sketch, "E2.18.16.0", {"center": v(-101.6, 152.4) * mm, "radius": 3.3 * mm});
            skCircle(sketch, "E2.18.17.0", {"center": v(-101.6, 127) * mm, "radius": 3.3 * mm});
            skCircle(sketch, "E2.18.18.0", {"center": v(-101.6, 101.6) * mm, "radius": 3.3 * mm});
            skCircle(sketch, "E2.18.19.0", {"center": v(-101.6, 76.2) * mm, "radius": 3.3 * mm});
            skCircle(sketch, "E2.18.20.0", {"center": v(-101.6, 50.8) * mm, "radius": 3.3 * mm});
            skCircle(sketch, "E2.18.21.0", {"center": v(-101.6, 25.4) * mm, "radius": 3.3 * mm});
            skCircle(sketch, "E2.18.22.0", {"center": v(-101.6, 0) * mm, "radius": 3.3 * mm});
            skCircle(sketch, "E2.18.23.0", {"center": v(-101.6, -25.4) * mm, "radius": 3.3 * mm});
            skCircle(sketch, "E2.18.24.0", {"center": v(-101.6, -50.8) * mm, "radius": 3.3 * mm});
            skCircle(sketch, "E2.18.25.0", {"center": v(-101.6, -76.2) * mm, "radius": 3.3 * mm});
            skCircle(sketch, "E2.18.26.0", {"center": v(-101.6, -101.6) * mm, "radius": 3.3 * mm});
            skCircle(sketch, "E2.18.27.0", {"center": v(-101.6, -127) * mm, "radius": 3.3 * mm});
            skCircle(sketch, "E2.18.28.0", {"center": v(-101.6, -152.4) * mm, "radius": 3.3 * mm});
            skCircle(sketch, "E2.18.29.0", {"center": v(-101.6, -177.8) * mm, "radius": 3.3 * mm});
            skCircle(sketch, "E2.18.30.0", {"center": v(-101.6, -203.2) * mm, "radius": 3.3 * mm});
            skCircle(sketch, "E2.18.31.0", {"center": v(-101.6, -228.6) * mm, "radius": 3.3 * mm});
            skCircle(sketch, "E2.18.32.0", {"center": v(-101.6, -254) * mm, "radius": 3.3 * mm});
            skCircle(sketch, "E2.18.33.0", {"center": v(-101.6, -279.4) * mm, "radius": 3.3 * mm});
            skCircle(sketch, "E2.18.34.0", {"center": v(-101.6, -304.8) * mm, "radius": 3.3 * mm});
            skCircle(sketch, "E2.18.35.0", {"center": v(-101.6, -330.2) * mm, "radius": 3.3 * mm});
            skCircle(sketch, "E2.18.36.0", {"center": v(-101.6, -355.6) * mm, "radius": 3.3 * mm});
            skCircle(sketch, "E2.18.37.0", {"center": v(-101.6, -381) * mm, "radius": 3.3 * mm});
            skCircle(sketch, "E2.18.38.0", {"center": v(-101.6, -406.4) * mm, "radius": 3.3 * mm});
            skCircle(sketch, "E2.18.39.0", {"center": v(-101.6, -431.8) * mm, "radius": 3.3 * mm});
            skCircle(sketch, "E2.18.40.0", {"center": v(-101.6, -457.2) * mm, "radius": 3.3 * mm});
            skCircle(sketch, "E2.18.41.0", {"center": v(-101.6, -482.6) * mm, "radius": 3.3 * mm});
            skCircle(sketch, "E2.18.42.0", {"center": v(-101.6, -508) * mm, "radius": 3.3 * mm});
            skCircle(sketch, "E2.18.43.0", {"center": v(-101.6, -533.4) * mm, "radius": 3.3 * mm});
            skCircle(sketch, "E2.18.44.0", {"center": v(-101.6, -558.8) * mm, "radius": 3.3 * mm});
            skCircle(sketch, "E2.19.0.0", {"center": v(-76.2, 558.8) * mm, "radius": 3.3 * mm});
            skCircle(sketch, "E2.19.1.0", {"center": v(-76.2, 533.4) * mm, "radius": 3.3 * mm});
            skCircle(sketch, "E2.19.2.0", {"center": v(-76.2, 508) * mm, "radius": 3.3 * mm});
            skCircle(sketch, "E2.19.3.0", {"center": v(-76.2, 482.6) * mm, "radius": 3.3 * mm});
            skCircle(sketch, "E2.19.4.0", {"center": v(-76.2, 457.2) * mm, "radius": 3.3 * mm});
            skCircle(sketch, "E2.19.5.0", {"center": v(-76.2, 431.8) * mm, "radius": 3.3 * mm});
            skCircle(sketch, "E2.19.6.0", {"center": v(-76.2, 406.4) * mm, "radius": 3.3 * mm});
            skCircle(sketch, "E2.19.7.0", {"center": v(-76.2, 381) * mm, "radius": 3.3 * mm});
            skCircle(sketch, "E2.19.8.0", {"center": v(-76.2, 355.6) * mm, "radius": 3.3 * mm});
            skCircle(sketch, "E2.19.9.0", {"center": v(-76.2, 330.2) * mm, "radius": 3.3 * mm});
            skCircle(sketch, "E2.19.10.0", {"center": v(-76.2, 304.8) * mm, "radius": 3.3 * mm});
            skCircle(sketch, "E2.19.11.0", {"center": v(-76.2, 279.4) * mm, "radius": 3.3 * mm});
            skCircle(sketch, "E2.19.12.0", {"center": v(-76.2, 254) * mm, "radius": 3.3 * mm});
            skCircle(sketch, "E2.19.13.0", {"center": v(-76.2, 228.6) * mm, "radius": 3.3 * mm});
            skCircle(sketch, "E2.19.14.0", {"center": v(-76.2, 203.2) * mm, "radius": 3.3 * mm});
            skCircle(sketch, "E2.19.15.0", {"center": v(-76.2, 177.8) * mm, "radius": 3.3 * mm});
            skCircle(sketch, "E2.19.16.0", {"center": v(-76.2, 152.4) * mm, "radius": 3.3 * mm});
            skCircle(sketch, "E2.19.17.0", {"center": v(-76.2, 127) * mm, "radius": 3.3 * mm});
            skCircle(sketch, "E2.19.18.0", {"center": v(-76.2, 101.6) * mm, "radius": 3.3 * mm});
            skCircle(sketch, "E2.19.19.0", {"center": v(-76.2, 76.2) * mm, "radius": 3.3 * mm});
            skCircle(sketch, "E2.19.20.0", {"center": v(-76.2, 50.8) * mm, "radius": 3.3 * mm});
            skCircle(sketch, "E2.19.21.0", {"center": v(-76.2, 25.4) * mm, "radius": 3.3 * mm});
            skCircle(sketch, "E2.19.22.0", {"center": v(-76.2, 0) * mm, "radius": 3.3 * mm});
            skCircle(sketch, "E2.19.23.0", {"center": v(-76.2, -25.4) * mm, "radius": 3.3 * mm});
            skCircle(sketch, "E2.19.24.0", {"center": v(-76.2, -50.8) * mm, "radius": 3.3 * mm});
            skCircle(sketch, "E2.19.25.0", {"center": v(-76.2, -76.2) * mm, "radius": 3.3 * mm});
            skCircle(sketch, "E2.19.26.0", {"center": v(-76.2, -101.6) * mm, "radius": 3.3 * mm});
            skCircle(sketch, "E2.19.27.0", {"center": v(-76.2, -127) * mm, "radius": 3.3 * mm});
            skCircle(sketch, "E2.19.28.0", {"center": v(-76.2, -152.4) * mm, "radius": 3.3 * mm});
            skCircle(sketch, "E2.19.29.0", {"center": v(-76.2, -177.8) * mm, "radius": 3.3 * mm});
            skCircle(sketch, "E2.19.30.0", {"center": v(-76.2, -203.2) * mm, "radius": 3.3 * mm});
            skCircle(sketch, "E2.19.31.0", {"center": v(-76.2, -228.6) * mm, "radius": 3.3 * mm});
            skCircle(sketch, "E2.19.32.0", {"center": v(-76.2, -254) * mm, "radius": 3.3 * mm});
            skCircle(sketch, "E2.19.33.0", {"center": v(-76.2, -279.4) * mm, "radius": 3.3 * mm});
            skCircle(sketch, "E2.19.34.0", {"center": v(-76.2, -304.8) * mm, "radius": 3.3 * mm});
            skCircle(sketch, "E2.19.35.0", {"center": v(-76.2, -330.2) * mm, "radius": 3.3 * mm});
            skCircle(sketch, "E2.19.36.0", {"center": v(-76.2, -355.6) * mm, "radius": 3.3 * mm});
            skCircle(sketch, "E2.19.37.0", {"center": v(-76.2, -381) * mm, "radius": 3.3 * mm});
            skCircle(sketch, "E2.19.38.0", {"center": v(-76.2, -406.4) * mm, "radius": 3.3 * mm});
            skCircle(sketch, "E2.19.39.0", {"center": v(-76.2, -431.8) * mm, "radius": 3.3 * mm});
            skCircle(sketch, "E2.19.40.0", {"center": v(-76.2, -457.2) * mm, "radius": 3.3 * mm});
            skCircle(sketch, "E2.19.41.0", {"center": v(-76.2, -482.6) * mm, "radius": 3.3 * mm});
            skCircle(sketch, "E2.19.42.0", {"center": v(-76.2, -508) * mm, "radius": 3.3 * mm});
            skCircle(sketch, "E2.19.43.0", {"center": v(-76.2, -533.4) * mm, "radius": 3.3 * mm});
            skCircle(sketch, "E2.19.44.0", {"center": v(-76.2, -558.8) * mm, "radius": 3.3 * mm});
            skCircle(sketch, "E2.20.0.0", {"center": v(-50.8, 558.8) * mm, "radius": 3.3 * mm});
            skCircle(sketch, "E2.20.1.0", {"center": v(-50.8, 533.4) * mm, "radius": 3.3 * mm});
            skCircle(sketch, "E2.20.2.0", {"center": v(-50.8, 508) * mm, "radius": 3.3 * mm});
            skCircle(sketch, "E2.20.3.0", {"center": v(-50.8, 482.6) * mm, "radius": 3.3 * mm});
            skCircle(sketch, "E2.20.4.0", {"center": v(-50.8, 457.2) * mm, "radius": 3.3 * mm});
            skCircle(sketch, "E2.20.5.0", {"center": v(-50.8, 431.8) * mm, "radius": 3.3 * mm});
            skCircle(sketch, "E2.20.6.0", {"center": v(-50.8, 406.4) * mm, "radius": 3.3 * mm});
            skCircle(sketch, "E2.20.7.0", {"center": v(-50.8, 381) * mm, "radius": 3.3 * mm});
            skCircle(sketch, "E2.20.8.0", {"center": v(-50.8, 355.6) * mm, "radius": 3.3 * mm});
            skCircle(sketch, "E2.20.9.0", {"center": v(-50.8, 330.2) * mm, "radius": 3.3 * mm});
            skCircle(sketch, "E2.20.10.0", {"center": v(-50.8, 304.8) * mm, "radius": 3.3 * mm});
            skCircle(sketch, "E2.20.11.0", {"center": v(-50.8, 279.4) * mm, "radius": 3.3 * mm});
            skCircle(sketch, "E2.20.12.0", {"center": v(-50.8, 254) * mm, "radius": 3.3 * mm});
            skCircle(sketch, "E2.20.13.0", {"center": v(-50.8, 228.6) * mm, "radius": 3.3 * mm});
            skCircle(sketch, "E2.20.14.0", {"center": v(-50.8, 203.2) * mm, "radius": 3.3 * mm});
            skCircle(sketch, "E2.20.15.0", {"center": v(-50.8, 177.8) * mm, "radius": 3.3 * mm});
            skCircle(sketch, "E2.20.16.0", {"center": v(-50.8, 152.4) * mm, "radius": 3.3 * mm});
            skCircle(sketch, "E2.20.17.0", {"center": v(-50.8, 127) * mm, "radius": 3.3 * mm});
            skCircle(sketch, "E2.20.18.0", {"center": v(-50.8, 101.6) * mm, "radius": 3.3 * mm});
            skCircle(sketch, "E2.20.19.0", {"center": v(-50.8, 76.2) * mm, "radius": 3.3 * mm});
            skCircle(sketch, "E2.20.20.0", {"center": v(-50.8, 50.8) * mm, "radius": 3.3 * mm});
            skCircle(sketch, "E2.20.21.0", {"center": v(-50.8, 25.4) * mm, "radius": 3.3 * mm});
            skCircle(sketch, "E2.20.22.0", {"center": v(-50.8, 0) * mm, "radius": 3.3 * mm});
            skCircle(sketch, "E2.20.23.0", {"center": v(-50.8, -25.4) * mm, "radius": 3.3 * mm});
            skCircle(sketch, "E2.20.24.0", {"center": v(-50.8, -50.8) * mm, "radius": 3.3 * mm});
            skCircle(sketch, "E2.20.25.0", {"center": v(-50.8, -76.2) * mm, "radius": 3.3 * mm});
            skCircle(sketch, "E2.20.26.0", {"center": v(-50.8, -101.6) * mm, "radius": 3.3 * mm});
            skCircle(sketch, "E2.20.27.0", {"center": v(-50.8, -127) * mm, "radius": 3.3 * mm});
            skCircle(sketch, "E2.20.28.0", {"center": v(-50.8, -152.4) * mm, "radius": 3.3 * mm});
            skCircle(sketch, "E2.20.29.0", {"center": v(-50.8, -177.8) * mm, "radius": 3.3 * mm});
            skCircle(sketch, "E2.20.30.0", {"center": v(-50.8, -203.2) * mm, "radius": 3.3 * mm});
            skCircle(sketch, "E2.20.31.0", {"center": v(-50.8, -228.6) * mm, "radius": 3.3 * mm});
            skCircle(sketch, "E2.20.32.0", {"center": v(-50.8, -254) * mm, "radius": 3.3 * mm});
            skCircle(sketch, "E2.20.33.0", {"center": v(-50.8, -279.4) * mm, "radius": 3.3 * mm});
            skCircle(sketch, "E2.20.34.0", {"center": v(-50.8, -304.8) * mm, "radius": 3.3 * mm});
            skCircle(sketch, "E2.20.35.0", {"center": v(-50.8, -330.2) * mm, "radius": 3.3 * mm});
            skCircle(sketch, "E2.20.36.0", {"center": v(-50.8, -355.6) * mm, "radius": 3.3 * mm});
            skCircle(sketch, "E2.20.37.0", {"center": v(-50.8, -381) * mm, "radius": 3.3 * mm});
            skCircle(sketch, "E2.20.38.0", {"center": v(-50.8, -406.4) * mm, "radius": 3.3 * mm});
            skCircle(sketch, "E2.20.39.0", {"center": v(-50.8, -431.8) * mm, "radius": 3.3 * mm});
            skCircle(sketch, "E2.20.40.0", {"center": v(-50.8, -457.2) * mm, "radius": 3.3 * mm});
            skCircle(sketch, "E2.20.41.0", {"center": v(-50.8, -482.6) * mm, "radius": 3.3 * mm});
            skCircle(sketch, "E2.20.42.0", {"center": v(-50.8, -508) * mm, "radius": 3.3 * mm});
            skCircle(sketch, "E2.20.43.0", {"center": v(-50.8, -533.4) * mm, "radius": 3.3 * mm});
            skCircle(sketch, "E2.20.44.0", {"center": v(-50.8, -558.8) * mm, "radius": 3.3 * mm});
            skCircle(sketch, "E2.21.0.0", {"center": v(-25.4, 558.8) * mm, "radius": 3.3 * mm});
            skCircle(sketch, "E2.21.1.0", {"center": v(-25.4, 533.4) * mm, "radius": 3.3 * mm});
            skCircle(sketch, "E2.21.2.0", {"center": v(-25.4, 508) * mm, "radius": 3.3 * mm});
            skCircle(sketch, "E2.21.3.0", {"center": v(-25.4, 482.6) * mm, "radius": 3.3 * mm});
            skCircle(sketch, "E2.21.4.0", {"center": v(-25.4, 457.2) * mm, "radius": 3.3 * mm});
            skCircle(sketch, "E2.21.5.0", {"center": v(-25.4, 431.8) * mm, "radius": 3.3 * mm});
            skCircle(sketch, "E2.21.6.0", {"center": v(-25.4, 406.4) * mm, "radius": 3.3 * mm});
            skCircle(sketch, "E2.21.7.0", {"center": v(-25.4, 381) * mm, "radius": 3.3 * mm});
            skCircle(sketch, "E2.21.8.0", {"center": v(-25.4, 355.6) * mm, "radius": 3.3 * mm});
            skCircle(sketch, "E2.21.9.0", {"center": v(-25.4, 330.2) * mm, "radius": 3.3 * mm});
            skCircle(sketch, "E2.21.10.0", {"center": v(-25.4, 304.8) * mm, "radius": 3.3 * mm});
            skCircle(sketch, "E2.21.11.0", {"center": v(-25.4, 279.4) * mm, "radius": 3.3 * mm});
            skCircle(sketch, "E2.21.12.0", {"center": v(-25.4, 254) * mm, "radius": 3.3 * mm});
            skCircle(sketch, "E2.21.13.0", {"center": v(-25.4, 228.6) * mm, "radius": 3.3 * mm});
            skCircle(sketch, "E2.21.14.0", {"center": v(-25.4, 203.2) * mm, "radius": 3.3 * mm});
            skCircle(sketch, "E2.21.15.0", {"center": v(-25.4, 177.8) * mm, "radius": 3.3 * mm});
            skCircle(sketch, "E2.21.16.0", {"center": v(-25.4, 152.4) * mm, "radius": 3.3 * mm});
            skCircle(sketch, "E2.21.17.0", {"center": v(-25.4, 127) * mm, "radius": 3.3 * mm});
            skCircle(sketch, "E2.21.18.0", {"center": v(-25.4, 101.6) * mm, "radius": 3.3 * mm});
            skCircle(sketch, "E2.21.19.0", {"center": v(-25.4, 76.2) * mm, "radius": 3.3 * mm});
            skCircle(sketch, "E2.21.20.0", {"center": v(-25.4, 50.8) * mm, "radius": 3.3 * mm});
            skCircle(sketch, "E2.21.21.0", {"center": v(-25.4, 25.4) * mm, "radius": 3.3 * mm});
            skCircle(sketch, "E2.21.22.0", {"center": v(-25.4, 0) * mm, "radius": 3.3 * mm});
            skCircle(sketch, "E2.21.23.0", {"center": v(-25.4, -25.4) * mm, "radius": 3.3 * mm});
            skCircle(sketch, "E2.21.24.0", {"center": v(-25.4, -50.8) * mm, "radius": 3.3 * mm});
            skCircle(sketch, "E2.21.25.0", {"center": v(-25.4, -76.2) * mm, "radius": 3.3 * mm});
            skCircle(sketch, "E2.21.26.0", {"center": v(-25.4, -101.6) * mm, "radius": 3.3 * mm});
            skCircle(sketch, "E2.21.27.0", {"center": v(-25.4, -127) * mm, "radius": 3.3 * mm});
            skCircle(sketch, "E2.21.28.0", {"center": v(-25.4, -152.4) * mm, "radius": 3.3 * mm});
            skCircle(sketch, "E2.21.29.0", {"center": v(-25.4, -177.8) * mm, "radius": 3.3 * mm});
            skCircle(sketch, "E2.21.30.0", {"center": v(-25.4, -203.2) * mm, "radius": 3.3 * mm});
            skCircle(sketch, "E2.21.31.0", {"center": v(-25.4, -228.6) * mm, "radius": 3.3 * mm});
            skCircle(sketch, "E2.21.32.0", {"center": v(-25.4, -254) * mm, "radius": 3.3 * mm});
            skCircle(sketch, "E2.21.33.0", {"center": v(-25.4, -279.4) * mm, "radius": 3.3 * mm});
            skCircle(sketch, "E2.21.34.0", {"center": v(-25.4, -304.8) * mm, "radius": 3.3 * mm});
            skCircle(sketch, "E2.21.35.0", {"center": v(-25.4, -330.2) * mm, "radius": 3.3 * mm});
            skCircle(sketch, "E2.21.36.0", {"center": v(-25.4, -355.6) * mm, "radius": 3.3 * mm});
            skCircle(sketch, "E2.21.37.0", {"center": v(-25.4, -381) * mm, "radius": 3.3 * mm});
            skCircle(sketch, "E2.21.38.0", {"center": v(-25.4, -406.4) * mm, "radius": 3.3 * mm});
            skCircle(sketch, "E2.21.39.0", {"center": v(-25.4, -431.8) * mm, "radius": 3.3 * mm});
            skCircle(sketch, "E2.21.40.0", {"center": v(-25.4, -457.2) * mm, "radius": 3.3 * mm});
            skCircle(sketch, "E2.21.41.0", {"center": v(-25.4, -482.6) * mm, "radius": 3.3 * mm});
            skCircle(sketch, "E2.21.42.0", {"center": v(-25.4, -508) * mm, "radius": 3.3 * mm});
            skCircle(sketch, "E2.21.43.0", {"center": v(-25.4, -533.4) * mm, "radius": 3.3 * mm});
            skCircle(sketch, "E2.21.44.0", {"center": v(-25.4, -558.8) * mm, "radius": 3.3 * mm});
            skCircle(sketch, "E2.22.0.0", {"center": v(0, 558.8) * mm, "radius": 3.3 * mm});
            skCircle(sketch, "E2.22.1.0", {"center": v(0, 533.4) * mm, "radius": 3.3 * mm});
            skCircle(sketch, "E2.22.2.0", {"center": v(0, 508) * mm, "radius": 3.3 * mm});
            skCircle(sketch, "E2.22.3.0", {"center": v(0, 482.6) * mm, "radius": 3.3 * mm});
            skCircle(sketch, "E2.22.4.0", {"center": v(0, 457.2) * mm, "radius": 3.3 * mm});
            skCircle(sketch, "E2.22.5.0", {"center": v(0, 431.8) * mm, "radius": 3.3 * mm});
            skCircle(sketch, "E2.22.6.0", {"center": v(0, 406.4) * mm, "radius": 3.3 * mm});
            skCircle(sketch, "E2.22.7.0", {"center": v(0, 381) * mm, "radius": 3.3 * mm});
            skCircle(sketch, "E2.22.8.0", {"center": v(0, 355.6) * mm, "radius": 3.3 * mm});
            skCircle(sketch, "E2.22.9.0", {"center": v(0, 330.2) * mm, "radius": 3.3 * mm});
            skCircle(sketch, "E2.22.10.0", {"center": v(0, 304.8) * mm, "radius": 3.3 * mm});
            skCircle(sketch, "E2.22.11.0", {"center": v(0, 279.4) * mm, "radius": 3.3 * mm});
            skCircle(sketch, "E2.22.12.0", {"center": v(0, 254) * mm, "radius": 3.3 * mm});
            skCircle(sketch, "E2.22.13.0", {"center": v(0, 228.6) * mm, "radius": 3.3 * mm});
            skCircle(sketch, "E2.22.14.0", {"center": v(0, 203.2) * mm, "radius": 3.3 * mm});
            skCircle(sketch, "E2.22.15.0", {"center": v(0, 177.8) * mm, "radius": 3.3 * mm});
            skCircle(sketch, "E2.22.16.0", {"center": v(0, 152.4) * mm, "radius": 3.3 * mm});
            skCircle(sketch, "E2.22.17.0", {"center": v(0, 127) * mm, "radius": 3.3 * mm});
            skCircle(sketch, "E2.22.18.0", {"center": v(0, 101.6) * mm, "radius": 3.3 * mm});
            skCircle(sketch, "E2.22.19.0", {"center": v(0, 76.2) * mm, "radius": 3.3 * mm});
            skCircle(sketch, "E2.22.20.0", {"center": v(0, 50.8) * mm, "radius": 3.3 * mm});
            skCircle(sketch, "E2.22.21.0", {"center": v(0, 25.4) * mm, "radius": 3.3 * mm});
            skCircle(sketch, "E2.22.22.0", {"center": v(0, 0) * mm, "radius": 3.3 * mm});
            skCircle(sketch, "E2.22.23.0", {"center": v(0, -25.4) * mm, "radius": 3.3 * mm});
            skCircle(sketch, "E2.22.24.0", {"center": v(0, -50.8) * mm, "radius": 3.3 * mm});
            skCircle(sketch, "E2.22.25.0", {"center": v(0, -76.2) * mm, "radius": 3.3 * mm});
            skCircle(sketch, "E2.22.26.0", {"center": v(0, -101.6) * mm, "radius": 3.3 * mm});
            skCircle(sketch, "E2.22.27.0", {"center": v(0, -127) * mm, "radius": 3.3 * mm});
            skCircle(sketch, "E2.22.28.0", {"center": v(0, -152.4) * mm, "radius": 3.3 * mm});
            skCircle(sketch, "E2.22.29.0", {"center": v(0, -177.8) * mm, "radius": 3.3 * mm});
            skCircle(sketch, "E2.22.30.0", {"center": v(0, -203.2) * mm, "radius": 3.3 * mm});
            skCircle(sketch, "E2.22.31.0", {"center": v(0, -228.6) * mm, "radius": 3.3 * mm});
            skCircle(sketch, "E2.22.32.0", {"center": v(0, -254) * mm, "radius": 3.3 * mm});
            skCircle(sketch, "E2.22.33.0", {"center": v(0, -279.4) * mm, "radius": 3.3 * mm});
            skCircle(sketch, "E2.22.34.0", {"center": v(0, -304.8) * mm, "radius": 3.3 * mm});
            skCircle(sketch, "E2.22.35.0", {"center": v(0, -330.2) * mm, "radius": 3.3 * mm});
            skCircle(sketch, "E2.22.36.0", {"center": v(0, -355.6) * mm, "radius": 3.3 * mm});
            skCircle(sketch, "E2.22.37.0", {"center": v(0, -381) * mm, "radius": 3.3 * mm});
            skCircle(sketch, "E2.22.38.0", {"center": v(0, -406.4) * mm, "radius": 3.3 * mm});
            skCircle(sketch, "E2.22.39.0", {"center": v(0, -431.8) * mm, "radius": 3.3 * mm});
            skCircle(sketch, "E2.22.40.0", {"center": v(0, -457.2) * mm, "radius": 3.3 * mm});
            skCircle(sketch, "E2.22.41.0", {"center": v(0, -482.6) * mm, "radius": 3.3 * mm});
            skCircle(sketch, "E2.22.42.0", {"center": v(0, -508) * mm, "radius": 3.3 * mm});
            skCircle(sketch, "E2.22.43.0", {"center": v(0, -533.4) * mm, "radius": 3.3 * mm});
            skCircle(sketch, "E2.22.44.0", {"center": v(0, -558.8) * mm, "radius": 3.3 * mm});
            skCircle(sketch, "E2.23.0.0", {"center": v(25.4, 558.8) * mm, "radius": 3.3 * mm});
            skCircle(sketch, "E2.23.1.0", {"center": v(25.4, 533.4) * mm, "radius": 3.3 * mm});
            skCircle(sketch, "E2.23.2.0", {"center": v(25.4, 508) * mm, "radius": 3.3 * mm});
            skCircle(sketch, "E2.23.3.0", {"center": v(25.4, 482.6) * mm, "radius": 3.3 * mm});
            skCircle(sketch, "E2.23.4.0", {"center": v(25.4, 457.2) * mm, "radius": 3.3 * mm});
            skCircle(sketch, "E2.23.5.0", {"center": v(25.4, 431.8) * mm, "radius": 3.3 * mm});
            skCircle(sketch, "E2.23.6.0", {"center": v(25.4, 406.4) * mm, "radius": 3.3 * mm});
            skCircle(sketch, "E2.23.7.0", {"center": v(25.4, 381) * mm, "radius": 3.3 * mm});
            skCircle(sketch, "E2.23.8.0", {"center": v(25.4, 355.6) * mm, "radius": 3.3 * mm});
            skCircle(sketch, "E2.23.9.0", {"center": v(25.4, 330.2) * mm, "radius": 3.3 * mm});
            skCircle(sketch, "E2.23.10.0", {"center": v(25.4, 304.8) * mm, "radius": 3.3 * mm});
            skCircle(sketch, "E2.23.11.0", {"center": v(25.4, 279.4) * mm, "radius": 3.3 * mm});
            skCircle(sketch, "E2.23.12.0", {"center": v(25.4, 254) * mm, "radius": 3.3 * mm});
            skCircle(sketch, "E2.23.13.0", {"center": v(25.4, 228.6) * mm, "radius": 3.3 * mm});
            skCircle(sketch, "E2.23.14.0", {"center": v(25.4, 203.2) * mm, "radius": 3.3 * mm});
            skCircle(sketch, "E2.23.15.0", {"center": v(25.4, 177.8) * mm, "radius": 3.3 * mm});
            skCircle(sketch, "E2.23.16.0", {"center": v(25.4, 152.4) * mm, "radius": 3.3 * mm});
            skCircle(sketch, "E2.23.17.0", {"center": v(25.4, 127) * mm, "radius": 3.3 * mm});
            skCircle(sketch, "E2.23.18.0", {"center": v(25.4, 101.6) * mm, "radius": 3.3 * mm});
            skCircle(sketch, "E2.23.19.0", {"center": v(25.4, 76.2) * mm, "radius": 3.3 * mm});
            skCircle(sketch, "E2.23.20.0", {"center": v(25.4, 50.8) * mm, "radius": 3.3 * mm});
            skCircle(sketch, "E2.23.21.0", {"center": v(25.4, 25.4) * mm, "radius": 3.3 * mm});
            skCircle(sketch, "E2.23.22.0", {"center": v(25.4, 0) * mm, "radius": 3.3 * mm});
            skCircle(sketch, "E2.23.23.0", {"center": v(25.4, -25.4) * mm, "radius": 3.3 * mm});
            skCircle(sketch, "E2.23.24.0", {"center": v(25.4, -50.8) * mm, "radius": 3.3 * mm});
            skCircle(sketch, "E2.23.25.0", {"center": v(25.4, -76.2) * mm, "radius": 3.3 * mm});
            skCircle(sketch, "E2.23.26.0", {"center": v(25.4, -101.6) * mm, "radius": 3.3 * mm});
            skCircle(sketch, "E2.23.27.0", {"center": v(25.4, -127) * mm, "radius": 3.3 * mm});
            skCircle(sketch, "E2.23.28.0", {"center": v(25.4, -152.4) * mm, "radius": 3.3 * mm});
            skCircle(sketch, "E2.23.29.0", {"center": v(25.4, -177.8) * mm, "radius": 3.3 * mm});
            skCircle(sketch, "E2.23.30.0", {"center": v(25.4, -203.2) * mm, "radius": 3.3 * mm});
            skCircle(sketch, "E2.23.31.0", {"center": v(25.4, -228.6) * mm, "radius": 3.3 * mm});
            skCircle(sketch, "E2.23.32.0", {"center": v(25.4, -254) * mm, "radius": 3.3 * mm});
            skCircle(sketch, "E2.23.33.0", {"center": v(25.4, -279.4) * mm, "radius": 3.3 * mm});
            skCircle(sketch, "E2.23.34.0", {"center": v(25.4, -304.8) * mm, "radius": 3.3 * mm});
            skCircle(sketch, "E2.23.35.0", {"center": v(25.4, -330.2) * mm, "radius": 3.3 * mm});
            skCircle(sketch, "E2.23.36.0", {"center": v(25.4, -355.6) * mm, "radius": 3.3 * mm});
            skCircle(sketch, "E2.23.37.0", {"center": v(25.4, -381) * mm, "radius": 3.3 * mm});
            skCircle(sketch, "E2.23.38.0", {"center": v(25.4, -406.4) * mm, "radius": 3.3 * mm});
            skCircle(sketch, "E2.23.39.0", {"center": v(25.4, -431.8) * mm, "radius": 3.3 * mm});
            skCircle(sketch, "E2.23.40.0", {"center": v(25.4, -457.2) * mm, "radius": 3.3 * mm});
            skCircle(sketch, "E2.23.41.0", {"center": v(25.4, -482.6) * mm, "radius": 3.3 * mm});
            skCircle(sketch, "E2.23.42.0", {"center": v(25.4, -508) * mm, "radius": 3.3 * mm});
            skCircle(sketch, "E2.23.43.0", {"center": v(25.4, -533.4) * mm, "radius": 3.3 * mm});
            skCircle(sketch, "E2.23.44.0", {"center": v(25.4, -558.8) * mm, "radius": 3.3 * mm});
            skCircle(sketch, "E2.24.0.0", {"center": v(50.8, 558.8) * mm, "radius": 3.3 * mm});
            skCircle(sketch, "E2.24.1.0", {"center": v(50.8, 533.4) * mm, "radius": 3.3 * mm});
            skCircle(sketch, "E2.24.2.0", {"center": v(50.8, 508) * mm, "radius": 3.3 * mm});
            skCircle(sketch, "E2.24.3.0", {"center": v(50.8, 482.6) * mm, "radius": 3.3 * mm});
            skCircle(sketch, "E2.24.4.0", {"center": v(50.8, 457.2) * mm, "radius": 3.3 * mm});
            skCircle(sketch, "E2.24.5.0", {"center": v(50.8, 431.8) * mm, "radius": 3.3 * mm});
            skCircle(sketch, "E2.24.6.0", {"center": v(50.8, 406.4) * mm, "radius": 3.3 * mm});
            skCircle(sketch, "E2.24.7.0", {"center": v(50.8, 381) * mm, "radius": 3.3 * mm});
            skCircle(sketch, "E2.24.8.0", {"center": v(50.8, 355.6) * mm, "radius": 3.3 * mm});
            skCircle(sketch, "E2.24.9.0", {"center": v(50.8, 330.2) * mm, "radius": 3.3 * mm});
            skCircle(sketch, "E2.24.10.0", {"center": v(50.8, 304.8) * mm, "radius": 3.3 * mm});
            skCircle(sketch, "E2.24.11.0", {"center": v(50.8, 279.4) * mm, "radius": 3.3 * mm});
            skCircle(sketch, "E2.24.12.0", {"center": v(50.8, 254) * mm, "radius": 3.3 * mm});
            skCircle(sketch, "E2.24.13.0", {"center": v(50.8, 228.6) * mm, "radius": 3.3 * mm});
            skCircle(sketch, "E2.24.14.0", {"center": v(50.8, 203.2) * mm, "radius": 3.3 * mm});
            skCircle(sketch, "E2.24.15.0", {"center": v(50.8, 177.8) * mm, "radius": 3.3 * mm});
            skCircle(sketch, "E2.24.16.0", {"center": v(50.8, 152.4) * mm, "radius": 3.3 * mm});
            skCircle(sketch, "E2.24.17.0", {"center": v(50.8, 127) * mm, "radius": 3.3 * mm});
            skCircle(sketch, "E2.24.18.0", {"center": v(50.8, 101.6) * mm, "radius": 3.3 * mm});
            skCircle(sketch, "E2.24.19.0", {"center": v(50.8, 76.2) * mm, "radius": 3.3 * mm});
            skCircle(sketch, "E2.24.20.0", {"center": v(50.8, 50.8) * mm, "radius": 3.3 * mm});
            skCircle(sketch, "E2.24.21.0", {"center": v(50.8, 25.4) * mm, "radius": 3.3 * mm});
            skCircle(sketch, "E2.24.22.0", {"center": v(50.8, 0) * mm, "radius": 3.3 * mm});
            skCircle(sketch, "E2.24.23.0", {"center": v(50.8, -25.4) * mm, "radius": 3.3 * mm});
            skCircle(sketch, "E2.24.24.0", {"center": v(50.8, -50.8) * mm, "radius": 3.3 * mm});
            skCircle(sketch, "E2.24.25.0", {"center": v(50.8, -76.2) * mm, "radius": 3.3 * mm});
            skCircle(sketch, "E2.24.26.0", {"center": v(50.8, -101.6) * mm, "radius": 3.3 * mm});
            skCircle(sketch, "E2.24.27.0", {"center": v(50.8, -127) * mm, "radius": 3.3 * mm});
            skCircle(sketch, "E2.24.28.0", {"center": v(50.8, -152.4) * mm, "radius": 3.3 * mm});
            skCircle(sketch, "E2.24.29.0", {"center": v(50.8, -177.8) * mm, "radius": 3.3 * mm});
            skCircle(sketch, "E2.24.30.0", {"center": v(50.8, -203.2) * mm, "radius": 3.3 * mm});
            skCircle(sketch, "E2.24.31.0", {"center": v(50.8, -228.6) * mm, "radius": 3.3 * mm});
            skCircle(sketch, "E2.24.32.0", {"center": v(50.8, -254) * mm, "radius": 3.3 * mm});
            skCircle(sketch, "E2.24.33.0", {"center": v(50.8, -279.4) * mm, "radius": 3.3 * mm});
            skCircle(sketch, "E2.24.34.0", {"center": v(50.8, -304.8) * mm, "radius": 3.3 * mm});
            skCircle(sketch, "E2.24.35.0", {"center": v(50.8, -330.2) * mm, "radius": 3.3 * mm});
            skCircle(sketch, "E2.24.36.0", {"center": v(50.8, -355.6) * mm, "radius": 3.3 * mm});
            skCircle(sketch, "E2.24.37.0", {"center": v(50.8, -381) * mm, "radius": 3.3 * mm});
            skCircle(sketch, "E2.24.38.0", {"center": v(50.8, -406.4) * mm, "radius": 3.3 * mm});
            skCircle(sketch, "E2.24.39.0", {"center": v(50.8, -431.8) * mm, "radius": 3.3 * mm});
            skCircle(sketch, "E2.24.40.0", {"center": v(50.8, -457.2) * mm, "radius": 3.3 * mm});
            skCircle(sketch, "E2.24.41.0", {"center": v(50.8, -482.6) * mm, "radius": 3.3 * mm});
            skCircle(sketch, "E2.24.42.0", {"center": v(50.8, -508) * mm, "radius": 3.3 * mm});
            skCircle(sketch, "E2.24.43.0", {"center": v(50.8, -533.4) * mm, "radius": 3.3 * mm});
            skCircle(sketch, "E2.24.44.0", {"center": v(50.8, -558.8) * mm, "radius": 3.3 * mm});
            skCircle(sketch, "E2.25.0.0", {"center": v(76.2, 558.8) * mm, "radius": 3.3 * mm});
            skCircle(sketch, "E2.25.1.0", {"center": v(76.2, 533.4) * mm, "radius": 3.3 * mm});
            skCircle(sketch, "E2.25.2.0", {"center": v(76.2, 508) * mm, "radius": 3.3 * mm});
            skCircle(sketch, "E2.25.3.0", {"center": v(76.2, 482.6) * mm, "radius": 3.3 * mm});
            skCircle(sketch, "E2.25.4.0", {"center": v(76.2, 457.2) * mm, "radius": 3.3 * mm});
            skCircle(sketch, "E2.25.5.0", {"center": v(76.2, 431.8) * mm, "radius": 3.3 * mm});
            skCircle(sketch, "E2.25.6.0", {"center": v(76.2, 406.4) * mm, "radius": 3.3 * mm});
            skCircle(sketch, "E2.25.7.0", {"center": v(76.2, 381) * mm, "radius": 3.3 * mm});
            skCircle(sketch, "E2.25.8.0", {"center": v(76.2, 355.6) * mm, "radius": 3.3 * mm});
            skCircle(sketch, "E2.25.9.0", {"center": v(76.2, 330.2) * mm, "radius": 3.3 * mm});
            skCircle(sketch, "E2.25.10.0", {"center": v(76.2, 304.8) * mm, "radius": 3.3 * mm});
            skCircle(sketch, "E2.25.11.0", {"center": v(76.2, 279.4) * mm, "radius": 3.3 * mm});
            skCircle(sketch, "E2.25.12.0", {"center": v(76.2, 254) * mm, "radius": 3.3 * mm});
            skCircle(sketch, "E2.25.13.0", {"center": v(76.2, 228.6) * mm, "radius": 3.3 * mm});
            skCircle(sketch, "E2.25.14.0", {"center": v(76.2, 203.2) * mm, "radius": 3.3 * mm});
            skCircle(sketch, "E2.25.15.0", {"center": v(76.2, 177.8) * mm, "radius": 3.3 * mm});
            skCircle(sketch, "E2.25.16.0", {"center": v(76.2, 152.4) * mm, "radius": 3.3 * mm});
            skCircle(sketch, "E2.25.17.0", {"center": v(76.2, 127) * mm, "radius": 3.3 * mm});
            skCircle(sketch, "E2.25.18.0", {"center": v(76.2, 101.6) * mm, "radius": 3.3 * mm});
            skCircle(sketch, "E2.25.19.0", {"center": v(76.2, 76.2) * mm, "radius": 3.3 * mm});
            skCircle(sketch, "E2.25.20.0", {"center": v(76.2, 50.8) * mm, "radius": 3.3 * mm});
            skCircle(sketch, "E2.25.21.0", {"center": v(76.2, 25.4) * mm, "radius": 3.3 * mm});
            skCircle(sketch, "E2.25.22.0", {"center": v(76.2, 0) * mm, "radius": 3.3 * mm});
            skCircle(sketch, "E2.25.23.0", {"center": v(76.2, -25.4) * mm, "radius": 3.3 * mm});
            skCircle(sketch, "E2.25.24.0", {"center": v(76.2, -50.8) * mm, "radius": 3.3 * mm});
            skCircle(sketch, "E2.25.25.0", {"center": v(76.2, -76.2) * mm, "radius": 3.3 * mm});
            skCircle(sketch, "E2.25.26.0", {"center": v(76.2, -101.6) * mm, "radius": 3.3 * mm});
            skCircle(sketch, "E2.25.27.0", {"center": v(76.2, -127) * mm, "radius": 3.3 * mm});
            skCircle(sketch, "E2.25.28.0", {"center": v(76.2, -152.4) * mm, "radius": 3.3 * mm});
            skCircle(sketch, "E2.25.29.0", {"center": v(76.2, -177.8) * mm, "radius": 3.3 * mm});
            skCircle(sketch, "E2.25.30.0", {"center": v(76.2, -203.2) * mm, "radius": 3.3 * mm});
            skCircle(sketch, "E2.25.31.0", {"center": v(76.2, -228.6) * mm, "radius": 3.3 * mm});
            skCircle(sketch, "E2.25.32.0", {"center": v(76.2, -254) * mm, "radius": 3.3 * mm});
            skCircle(sketch, "E2.25.33.0", {"center": v(76.2, -279.4) * mm, "radius": 3.3 * mm});
            skCircle(sketch, "E2.25.34.0", {"center": v(76.2, -304.8) * mm, "radius": 3.3 * mm});
            skCircle(sketch, "E2.25.35.0", {"center": v(76.2, -330.2) * mm, "radius": 3.3 * mm});
            skCircle(sketch, "E2.25.36.0", {"center": v(76.2, -355.6) * mm, "radius": 3.3 * mm});
            skCircle(sketch, "E2.25.37.0", {"center": v(76.2, -381) * mm, "radius": 3.3 * mm});
            skCircle(sketch, "E2.25.38.0", {"center": v(76.2, -406.4) * mm, "radius": 3.3 * mm});
            skCircle(sketch, "E2.25.39.0", {"center": v(76.2, -431.8) * mm, "radius": 3.3 * mm});
            skCircle(sketch, "E2.25.40.0", {"center": v(76.2, -457.2) * mm, "radius": 3.3 * mm});
            skCircle(sketch, "E2.25.41.0", {"center": v(76.2, -482.6) * mm, "radius": 3.3 * mm});
            skCircle(sketch, "E2.25.42.0", {"center": v(76.2, -508) * mm, "radius": 3.3 * mm});
            skCircle(sketch, "E2.25.43.0", {"center": v(76.2, -533.4) * mm, "radius": 3.3 * mm});
            skCircle(sketch, "E2.25.44.0", {"center": v(76.2, -558.8) * mm, "radius": 3.3 * mm});
            skCircle(sketch, "E2.26.0.0", {"center": v(101.6, 558.8) * mm, "radius": 3.3 * mm});
            skCircle(sketch, "E2.26.1.0", {"center": v(101.6, 533.4) * mm, "radius": 3.3 * mm});
            skCircle(sketch, "E2.26.2.0", {"center": v(101.6, 508) * mm, "radius": 3.3 * mm});
            skCircle(sketch, "E2.26.3.0", {"center": v(101.6, 482.6) * mm, "radius": 3.3 * mm});
            skCircle(sketch, "E2.26.4.0", {"center": v(101.6, 457.2) * mm, "radius": 3.3 * mm});
            skCircle(sketch, "E2.26.5.0", {"center": v(101.6, 431.8) * mm, "radius": 3.3 * mm});
            skCircle(sketch, "E2.26.6.0", {"center": v(101.6, 406.4) * mm, "radius": 3.3 * mm});
            skCircle(sketch, "E2.26.7.0", {"center": v(101.6, 381) * mm, "radius": 3.3 * mm});
            skCircle(sketch, "E2.26.8.0", {"center": v(101.6, 355.6) * mm, "radius": 3.3 * mm});
            skCircle(sketch, "E2.26.9.0", {"center": v(101.6, 330.2) * mm, "radius": 3.3 * mm});
            skCircle(sketch, "E2.26.10.0", {"center": v(101.6, 304.8) * mm, "radius": 3.3 * mm});
            skCircle(sketch, "E2.26.11.0", {"center": v(101.6, 279.4) * mm, "radius": 3.3 * mm});
            skCircle(sketch, "E2.26.12.0", {"center": v(101.6, 254) * mm, "radius": 3.3 * mm});
            skCircle(sketch, "E2.26.13.0", {"center": v(101.6, 228.6) * mm, "radius": 3.3 * mm});
            skCircle(sketch, "E2.26.14.0", {"center": v(101.6, 203.2) * mm, "radius": 3.3 * mm});
            skCircle(sketch, "E2.26.15.0", {"center": v(101.6, 177.8) * mm, "radius": 3.3 * mm});
            skCircle(sketch, "E2.26.16.0", {"center": v(101.6, 152.4) * mm, "radius": 3.3 * mm});
            skCircle(sketch, "E2.26.17.0", {"center": v(101.6, 127) * mm, "radius": 3.3 * mm});
            skCircle(sketch, "E2.26.18.0", {"center": v(101.6, 101.6) * mm, "radius": 3.3 * mm});
            skCircle(sketch, "E2.26.19.0", {"center": v(101.6, 76.2) * mm, "radius": 3.3 * mm});
            skCircle(sketch, "E2.26.20.0", {"center": v(101.6, 50.8) * mm, "radius": 3.3 * mm});
            skCircle(sketch, "E2.26.21.0", {"center": v(101.6, 25.4) * mm, "radius": 3.3 * mm});
            skCircle(sketch, "E2.26.22.0", {"center": v(101.6, 0) * mm, "radius": 3.3 * mm});
            skCircle(sketch, "E2.26.23.0", {"center": v(101.6, -25.4) * mm, "radius": 3.3 * mm});
            skCircle(sketch, "E2.26.24.0", {"center": v(101.6, -50.8) * mm, "radius": 3.3 * mm});
            skCircle(sketch, "E2.26.25.0", {"center": v(101.6, -76.2) * mm, "radius": 3.3 * mm});
            skCircle(sketch, "E2.26.26.0", {"center": v(101.6, -101.6) * mm, "radius": 3.3 * mm});
            skCircle(sketch, "E2.26.27.0", {"center": v(101.6, -127) * mm, "radius": 3.3 * mm});
            skCircle(sketch, "E2.26.28.0", {"center": v(101.6, -152.4) * mm, "radius": 3.3 * mm});
            skCircle(sketch, "E2.26.29.0", {"center": v(101.6, -177.8) * mm, "radius": 3.3 * mm});
            skCircle(sketch, "E2.26.30.0", {"center": v(101.6, -203.2) * mm, "radius": 3.3 * mm});
            skCircle(sketch, "E2.26.31.0", {"center": v(101.6, -228.6) * mm, "radius": 3.3 * mm});
            skCircle(sketch, "E2.26.32.0", {"center": v(101.6, -254) * mm, "radius": 3.3 * mm});
            skCircle(sketch, "E2.26.33.0", {"center": v(101.6, -279.4) * mm, "radius": 3.3 * mm});
            skCircle(sketch, "E2.26.34.0", {"center": v(101.6, -304.8) * mm, "radius": 3.3 * mm});
            skCircle(sketch, "E2.26.35.0", {"center": v(101.6, -330.2) * mm, "radius": 3.3 * mm});
            skCircle(sketch, "E2.26.36.0", {"center": v(101.6, -355.6) * mm, "radius": 3.3 * mm});
            skCircle(sketch, "E2.26.37.0", {"center": v(101.6, -381) * mm, "radius": 3.3 * mm});
            skCircle(sketch, "E2.26.38.0", {"center": v(101.6, -406.4) * mm, "radius": 3.3 * mm});
            skCircle(sketch, "E2.26.39.0", {"center": v(101.6, -431.8) * mm, "radius": 3.3 * mm});
            skCircle(sketch, "E2.26.40.0", {"center": v(101.6, -457.2) * mm, "radius": 3.3 * mm});
            skCircle(sketch, "E2.26.41.0", {"center": v(101.6, -482.6) * mm, "radius": 3.3 * mm});
            skCircle(sketch, "E2.26.42.0", {"center": v(101.6, -508) * mm, "radius": 3.3 * mm});
            skCircle(sketch, "E2.26.43.0", {"center": v(101.6, -533.4) * mm, "radius": 3.3 * mm});
            skCircle(sketch, "E2.26.44.0", {"center": v(101.6, -558.8) * mm, "radius": 3.3 * mm});
            skCircle(sketch, "E2.27.0.0", {"center": v(127, 558.8) * mm, "radius": 3.3 * mm});
            skCircle(sketch, "E2.27.1.0", {"center": v(127, 533.4) * mm, "radius": 3.3 * mm});
            skCircle(sketch, "E2.27.2.0", {"center": v(127, 508) * mm, "radius": 3.3 * mm});
            skCircle(sketch, "E2.27.3.0", {"center": v(127, 482.6) * mm, "radius": 3.3 * mm});
            skCircle(sketch, "E2.27.4.0", {"center": v(127, 457.2) * mm, "radius": 3.3 * mm});
            skCircle(sketch, "E2.27.5.0", {"center": v(127, 431.8) * mm, "radius": 3.3 * mm});
            skCircle(sketch, "E2.27.6.0", {"center": v(127, 406.4) * mm, "radius": 3.3 * mm});
            skCircle(sketch, "E2.27.7.0", {"center": v(127, 381) * mm, "radius": 3.3 * mm});
            skCircle(sketch, "E2.27.8.0", {"center": v(127, 355.6) * mm, "radius": 3.3 * mm});
            skCircle(sketch, "E2.27.9.0", {"center": v(127, 330.2) * mm, "radius": 3.3 * mm});
            skCircle(sketch, "E2.27.10.0", {"center": v(127, 304.8) * mm, "radius": 3.3 * mm});
            skCircle(sketch, "E2.27.11.0", {"center": v(127, 279.4) * mm, "radius": 3.3 * mm});
            skCircle(sketch, "E2.27.12.0", {"center": v(127, 254) * mm, "radius": 3.3 * mm});
            skCircle(sketch, "E2.27.13.0", {"center": v(127, 228.6) * mm, "radius": 3.3 * mm});
            skCircle(sketch, "E2.27.14.0", {"center": v(127, 203.2) * mm, "radius": 3.3 * mm});
            skCircle(sketch, "E2.27.15.0", {"center": v(127, 177.8) * mm, "radius": 3.3 * mm});
            skCircle(sketch, "E2.27.16.0", {"center": v(127, 152.4) * mm, "radius": 3.3 * mm});
            skCircle(sketch, "E2.27.17.0", {"center": v(127, 127) * mm, "radius": 3.3 * mm});
            skCircle(sketch, "E2.27.18.0", {"center": v(127, 101.6) * mm, "radius": 3.3 * mm});
            skCircle(sketch, "E2.27.19.0", {"center": v(127, 76.2) * mm, "radius": 3.3 * mm});
            skCircle(sketch, "E2.27.20.0", {"center": v(127, 50.8) * mm, "radius": 3.3 * mm});
            skCircle(sketch, "E2.27.21.0", {"center": v(127, 25.4) * mm, "radius": 3.3 * mm});
            skCircle(sketch, "E2.27.22.0", {"center": v(127, 0) * mm, "radius": 3.3 * mm});
            skCircle(sketch, "E2.27.23.0", {"center": v(127, -25.4) * mm, "radius": 3.3 * mm});
            skCircle(sketch, "E2.27.24.0", {"center": v(127, -50.8) * mm, "radius": 3.3 * mm});
            skCircle(sketch, "E2.27.25.0", {"center": v(127, -76.2) * mm, "radius": 3.3 * mm});
            skCircle(sketch, "E2.27.26.0", {"center": v(127, -101.6) * mm, "radius": 3.3 * mm});
            skCircle(sketch, "E2.27.27.0", {"center": v(127, -127) * mm, "radius": 3.3 * mm});
            skCircle(sketch, "E2.27.28.0", {"center": v(127, -152.4) * mm, "radius": 3.3 * mm});
            skCircle(sketch, "E2.27.29.0", {"center": v(127, -177.8) * mm, "radius": 3.3 * mm});
            skCircle(sketch, "E2.27.30.0", {"center": v(127, -203.2) * mm, "radius": 3.3 * mm});
            skCircle(sketch, "E2.27.31.0", {"center": v(127, -228.6) * mm, "radius": 3.3 * mm});
            skCircle(sketch, "E2.27.32.0", {"center": v(127, -254) * mm, "radius": 3.3 * mm});
            skCircle(sketch, "E2.27.33.0", {"center": v(127, -279.4) * mm, "radius": 3.3 * mm});
            skCircle(sketch, "E2.27.34.0", {"center": v(127, -304.8) * mm, "radius": 3.3 * mm});
            skCircle(sketch, "E2.27.35.0", {"center": v(127, -330.2) * mm, "radius": 3.3 * mm});
            skCircle(sketch, "E2.27.36.0", {"center": v(127, -355.6) * mm, "radius": 3.3 * mm});
            skCircle(sketch, "E2.27.37.0", {"center": v(127, -381) * mm, "radius": 3.3 * mm});
            skCircle(sketch, "E2.27.38.0", {"center": v(127, -406.4) * mm, "radius": 3.3 * mm});
            skCircle(sketch, "E2.27.39.0", {"center": v(127, -431.8) * mm, "radius": 3.3 * mm});
            skCircle(sketch, "E2.27.40.0", {"center": v(127, -457.2) * mm, "radius": 3.3 * mm});
            skCircle(sketch, "E2.27.41.0", {"center": v(127, -482.6) * mm, "radius": 3.3 * mm});
            skCircle(sketch, "E2.27.42.0", {"center": v(127, -508) * mm, "radius": 3.3 * mm});
            skCircle(sketch, "E2.27.43.0", {"center": v(127, -533.4) * mm, "radius": 3.3 * mm});
            skCircle(sketch, "E2.27.44.0", {"center": v(127, -558.8) * mm, "radius": 3.3 * mm});
            skCircle(sketch, "E2.28.0.0", {"center": v(152.4, 558.8) * mm, "radius": 3.3 * mm});
            skCircle(sketch, "E2.28.1.0", {"center": v(152.4, 533.4) * mm, "radius": 3.3 * mm});
            skCircle(sketch, "E2.28.2.0", {"center": v(152.4, 508) * mm, "radius": 3.3 * mm});
            skCircle(sketch, "E2.28.3.0", {"center": v(152.4, 482.6) * mm, "radius": 3.3 * mm});
            skCircle(sketch, "E2.28.4.0", {"center": v(152.4, 457.2) * mm, "radius": 3.3 * mm});
            skCircle(sketch, "E2.28.5.0", {"center": v(152.4, 431.8) * mm, "radius": 3.3 * mm});
            skCircle(sketch, "E2.28.6.0", {"center": v(152.4, 406.4) * mm, "radius": 3.3 * mm});
            skCircle(sketch, "E2.28.7.0", {"center": v(152.4, 381) * mm, "radius": 3.3 * mm});
            skCircle(sketch, "E2.28.8.0", {"center": v(152.4, 355.6) * mm, "radius": 3.3 * mm});
            skCircle(sketch, "E2.28.9.0", {"center": v(152.4, 330.2) * mm, "radius": 3.3 * mm});
            skCircle(sketch, "E2.28.10.0", {"center": v(152.4, 304.8) * mm, "radius": 3.3 * mm});
            skCircle(sketch, "E2.28.11.0", {"center": v(152.4, 279.4) * mm, "radius": 3.3 * mm});
            skCircle(sketch, "E2.28.12.0", {"center": v(152.4, 254) * mm, "radius": 3.3 * mm});
            skCircle(sketch, "E2.28.13.0", {"center": v(152.4, 228.6) * mm, "radius": 3.3 * mm});
            skCircle(sketch, "E2.28.14.0", {"center": v(152.4, 203.2) * mm, "radius": 3.3 * mm});
            skCircle(sketch, "E2.28.15.0", {"center": v(152.4, 177.8) * mm, "radius": 3.3 * mm});
            skCircle(sketch, "E2.28.16.0", {"center": v(152.4, 152.4) * mm, "radius": 3.3 * mm});
            skCircle(sketch, "E2.28.17.0", {"center": v(152.4, 127) * mm, "radius": 3.3 * mm});
            skCircle(sketch, "E2.28.18.0", {"center": v(152.4, 101.6) * mm, "radius": 3.3 * mm});
            skCircle(sketch, "E2.28.19.0", {"center": v(152.4, 76.2) * mm, "radius": 3.3 * mm});
            skCircle(sketch, "E2.28.20.0", {"center": v(152.4, 50.8) * mm, "radius": 3.3 * mm});
            skCircle(sketch, "E2.28.21.0", {"center": v(152.4, 25.4) * mm, "radius": 3.3 * mm});
            skCircle(sketch, "E2.28.22.0", {"center": v(152.4, 0) * mm, "radius": 3.3 * mm});
            skCircle(sketch, "E2.28.23.0", {"center": v(152.4, -25.4) * mm, "radius": 3.3 * mm});
            skCircle(sketch, "E2.28.24.0", {"center": v(152.4, -50.8) * mm, "radius": 3.3 * mm});
            skCircle(sketch, "E2.28.25.0", {"center": v(152.4, -76.2) * mm, "radius": 3.3 * mm});
            skCircle(sketch, "E2.28.26.0", {"center": v(152.4, -101.6) * mm, "radius": 3.3 * mm});
            skCircle(sketch, "E2.28.27.0", {"center": v(152.4, -127) * mm, "radius": 3.3 * mm});
            skCircle(sketch, "E2.28.28.0", {"center": v(152.4, -152.4) * mm, "radius": 3.3 * mm});
            skCircle(sketch, "E2.28.29.0", {"center": v(152.4, -177.8) * mm, "radius": 3.3 * mm});
            skCircle(sketch, "E2.28.30.0", {"center": v(152.4, -203.2) * mm, "radius": 3.3 * mm});
            skCircle(sketch, "E2.28.31.0", {"center": v(152.4, -228.6) * mm, "radius": 3.3 * mm});
            skCircle(sketch, "E2.28.32.0", {"center": v(152.4, -254) * mm, "radius": 3.3 * mm});
            skCircle(sketch, "E2.28.33.0", {"center": v(152.4, -279.4) * mm, "radius": 3.3 * mm});
            skCircle(sketch, "E2.28.34.0", {"center": v(152.4, -304.8) * mm, "radius": 3.3 * mm});
            skCircle(sketch, "E2.28.35.0", {"center": v(152.4, -330.2) * mm, "radius": 3.3 * mm});
            skCircle(sketch, "E2.28.36.0", {"center": v(152.4, -355.6) * mm, "radius": 3.3 * mm});
            skCircle(sketch, "E2.28.37.0", {"center": v(152.4, -381) * mm, "radius": 3.3 * mm});
            skCircle(sketch, "E2.28.38.0", {"center": v(152.4, -406.4) * mm, "radius": 3.3 * mm});
            skCircle(sketch, "E2.28.39.0", {"center": v(152.4, -431.8) * mm, "radius": 3.3 * mm});
            skCircle(sketch, "E2.28.40.0", {"center": v(152.4, -457.2) * mm, "radius": 3.3 * mm});
            skCircle(sketch, "E2.28.41.0", {"center": v(152.4, -482.6) * mm, "radius": 3.3 * mm});
            skCircle(sketch, "E2.28.42.0", {"center": v(152.4, -508) * mm, "radius": 3.3 * mm});
            skCircle(sketch, "E2.28.43.0", {"center": v(152.4, -533.4) * mm, "radius": 3.3 * mm});
            skCircle(sketch, "E2.28.44.0", {"center": v(152.4, -558.8) * mm, "radius": 3.3 * mm});
            skCircle(sketch, "E2.29.0.0", {"center": v(177.8, 558.8) * mm, "radius": 3.3 * mm});
            skCircle(sketch, "E2.29.1.0", {"center": v(177.8, 533.4) * mm, "radius": 3.3 * mm});
            skCircle(sketch, "E2.29.2.0", {"center": v(177.8, 508) * mm, "radius": 3.3 * mm});
            skCircle(sketch, "E2.29.3.0", {"center": v(177.8, 482.6) * mm, "radius": 3.3 * mm});
            skCircle(sketch, "E2.29.4.0", {"center": v(177.8, 457.2) * mm, "radius": 3.3 * mm});
            skCircle(sketch, "E2.29.5.0", {"center": v(177.8, 431.8) * mm, "radius": 3.3 * mm});
            skCircle(sketch, "E2.29.6.0", {"center": v(177.8, 406.4) * mm, "radius": 3.3 * mm});
            skCircle(sketch, "E2.29.7.0", {"center": v(177.8, 381) * mm, "radius": 3.3 * mm});
            skCircle(sketch, "E2.29.8.0", {"center": v(177.8, 355.6) * mm, "radius": 3.3 * mm});
            skCircle(sketch, "E2.29.9.0", {"center": v(177.8, 330.2) * mm, "radius": 3.3 * mm});
            skCircle(sketch, "E2.29.10.0", {"center": v(177.8, 304.8) * mm, "radius": 3.3 * mm});
            skCircle(sketch, "E2.29.11.0", {"center": v(177.8, 279.4) * mm, "radius": 3.3 * mm});
            skCircle(sketch, "E2.29.12.0", {"center": v(177.8, 254) * mm, "radius": 3.3 * mm});
            skCircle(sketch, "E2.29.13.0", {"center": v(177.8, 228.6) * mm, "radius": 3.3 * mm});
            skCircle(sketch, "E2.29.14.0", {"center": v(177.8, 203.2) * mm, "radius": 3.3 * mm});
            skCircle(sketch, "E2.29.15.0", {"center": v(177.8, 177.8) * mm, "radius": 3.3 * mm});
            skCircle(sketch, "E2.29.16.0", {"center": v(177.8, 152.4) * mm, "radius": 3.3 * mm});
            skCircle(sketch, "E2.29.17.0", {"center": v(177.8, 127) * mm, "radius": 3.3 * mm});
            skCircle(sketch, "E2.29.18.0", {"center": v(177.8, 101.6) * mm, "radius": 3.3 * mm});
            skCircle(sketch, "E2.29.19.0", {"center": v(177.8, 76.2) * mm, "radius": 3.3 * mm});
            skCircle(sketch, "E2.29.20.0", {"center": v(177.8, 50.8) * mm, "radius": 3.3 * mm});
            skCircle(sketch, "E2.29.21.0", {"center": v(177.8, 25.4) * mm, "radius": 3.3 * mm});
            skCircle(sketch, "E2.29.22.0", {"center": v(177.8, 0) * mm, "radius": 3.3 * mm});
            skCircle(sketch, "E2.29.23.0", {"center": v(177.8, -25.4) * mm, "radius": 3.3 * mm});
            skCircle(sketch, "E2.29.24.0", {"center": v(177.8, -50.8) * mm, "radius": 3.3 * mm});
            skCircle(sketch, "E2.29.25.0", {"center": v(177.8, -76.2) * mm, "radius": 3.3 * mm});
            skCircle(sketch, "E2.29.26.0", {"center": v(177.8, -101.6) * mm, "radius": 3.3 * mm});
            skCircle(sketch, "E2.29.27.0", {"center": v(177.8, -127) * mm, "radius": 3.3 * mm});
            skCircle(sketch, "E2.29.28.0", {"center": v(177.8, -152.4) * mm, "radius": 3.3 * mm});
            skCircle(sketch, "E2.29.29.0", {"center": v(177.8, -177.8) * mm, "radius": 3.3 * mm});
            skCircle(sketch, "E2.29.30.0", {"center": v(177.8, -203.2) * mm, "radius": 3.3 * mm});
            skCircle(sketch, "E2.29.31.0", {"center": v(177.8, -228.6) * mm, "radius": 3.3 * mm});
            skCircle(sketch, "E2.29.32.0", {"center": v(177.8, -254) * mm, "radius": 3.3 * mm});
            skCircle(sketch, "E2.29.33.0", {"center": v(177.8, -279.4) * mm, "radius": 3.3 * mm});
            skCircle(sketch, "E2.29.34.0", {"center": v(177.8, -304.8) * mm, "radius": 3.3 * mm});
            skCircle(sketch, "E2.29.35.0", {"center": v(177.8, -330.2) * mm, "radius": 3.3 * mm});
            skCircle(sketch, "E2.29.36.0", {"center": v(177.8, -355.6) * mm, "radius": 3.3 * mm});
            skCircle(sketch, "E2.29.37.0", {"center": v(177.8, -381) * mm, "radius": 3.3 * mm});
            skCircle(sketch, "E2.29.38.0", {"center": v(177.8, -406.4) * mm, "radius": 3.3 * mm});
            skCircle(sketch, "E2.29.39.0", {"center": v(177.8, -431.8) * mm, "radius": 3.3 * mm});
            skCircle(sketch, "E2.29.40.0", {"center": v(177.8, -457.2) * mm, "radius": 3.3 * mm});
            skCircle(sketch, "E2.29.41.0", {"center": v(177.8, -482.6) * mm, "radius": 3.3 * mm});
            skCircle(sketch, "E2.29.42.0", {"center": v(177.8, -508) * mm, "radius": 3.3 * mm});
            skCircle(sketch, "E2.29.43.0", {"center": v(177.8, -533.4) * mm, "radius": 3.3 * mm});
            skCircle(sketch, "E2.29.44.0", {"center": v(177.8, -558.8) * mm, "radius": 3.3 * mm});
            skCircle(sketch, "E2.30.0.0", {"center": v(203.2, 558.8) * mm, "radius": 3.3 * mm});
            skCircle(sketch, "E2.30.1.0", {"center": v(203.2, 533.4) * mm, "radius": 3.3 * mm});
            skCircle(sketch, "E2.30.2.0", {"center": v(203.2, 508) * mm, "radius": 3.3 * mm});
            skCircle(sketch, "E2.30.3.0", {"center": v(203.2, 482.6) * mm, "radius": 3.3 * mm});
            skCircle(sketch, "E2.30.4.0", {"center": v(203.2, 457.2) * mm, "radius": 3.3 * mm});
            skCircle(sketch, "E2.30.5.0", {"center": v(203.2, 431.8) * mm, "radius": 3.3 * mm});
            skCircle(sketch, "E2.30.6.0", {"center": v(203.2, 406.4) * mm, "radius": 3.3 * mm});
            skCircle(sketch, "E2.30.7.0", {"center": v(203.2, 381) * mm, "radius": 3.3 * mm});
            skCircle(sketch, "E2.30.8.0", {"center": v(203.2, 355.6) * mm, "radius": 3.3 * mm});
            skCircle(sketch, "E2.30.9.0", {"center": v(203.2, 330.2) * mm, "radius": 3.3 * mm});
            skCircle(sketch, "E2.30.10.0", {"center": v(203.2, 304.8) * mm, "radius": 3.3 * mm});
            skCircle(sketch, "E2.30.11.0", {"center": v(203.2, 279.4) * mm, "radius": 3.3 * mm});
            skCircle(sketch, "E2.30.12.0", {"center": v(203.2, 254) * mm, "radius": 3.3 * mm});
            skCircle(sketch, "E2.30.13.0", {"center": v(203.2, 228.6) * mm, "radius": 3.3 * mm});
            skCircle(sketch, "E2.30.14.0", {"center": v(203.2, 203.2) * mm, "radius": 3.3 * mm});
            skCircle(sketch, "E2.30.15.0", {"center": v(203.2, 177.8) * mm, "radius": 3.3 * mm});
            skCircle(sketch, "E2.30.16.0", {"center": v(203.2, 152.4) * mm, "radius": 3.3 * mm});
            skCircle(sketch, "E2.30.17.0", {"center": v(203.2, 127) * mm, "radius": 3.3 * mm});
            skCircle(sketch, "E2.30.18.0", {"center": v(203.2, 101.6) * mm, "radius": 3.3 * mm});
            skCircle(sketch, "E2.30.19.0", {"center": v(203.2, 76.2) * mm, "radius": 3.3 * mm});
            skCircle(sketch, "E2.30.20.0", {"center": v(203.2, 50.8) * mm, "radius": 3.3 * mm});
            skCircle(sketch, "E2.30.21.0", {"center": v(203.2, 25.4) * mm, "radius": 3.3 * mm});
            skCircle(sketch, "E2.30.22.0", {"center": v(203.2, 0) * mm, "radius": 3.3 * mm});
            skCircle(sketch, "E2.30.23.0", {"center": v(203.2, -25.4) * mm, "radius": 3.3 * mm});
            skCircle(sketch, "E2.30.24.0", {"center": v(203.2, -50.8) * mm, "radius": 3.3 * mm});
            skCircle(sketch, "E2.30.25.0", {"center": v(203.2, -76.2) * mm, "radius": 3.3 * mm});
            skCircle(sketch, "E2.30.26.0", {"center": v(203.2, -101.6) * mm, "radius": 3.3 * mm});
            skCircle(sketch, "E2.30.27.0", {"center": v(203.2, -127) * mm, "radius": 3.3 * mm});
            skCircle(sketch, "E2.30.28.0", {"center": v(203.2, -152.4) * mm, "radius": 3.3 * mm});
            skCircle(sketch, "E2.30.29.0", {"center": v(203.2, -177.8) * mm, "radius": 3.3 * mm});
            skCircle(sketch, "E2.30.30.0", {"center": v(203.2, -203.2) * mm, "radius": 3.3 * mm});
            skCircle(sketch, "E2.30.31.0", {"center": v(203.2, -228.6) * mm, "radius": 3.3 * mm});
            skCircle(sketch, "E2.30.32.0", {"center": v(203.2, -254) * mm, "radius": 3.3 * mm});
            skCircle(sketch, "E2.30.33.0", {"center": v(203.2, -279.4) * mm, "radius": 3.3 * mm});
            skCircle(sketch, "E2.30.34.0", {"center": v(203.2, -304.8) * mm, "radius": 3.3 * mm});
            skCircle(sketch, "E2.30.35.0", {"center": v(203.2, -330.2) * mm, "radius": 3.3 * mm});
            skCircle(sketch, "E2.30.36.0", {"center": v(203.2, -355.6) * mm, "radius": 3.3 * mm});
            skCircle(sketch, "E2.30.37.0", {"center": v(203.2, -381) * mm, "radius": 3.3 * mm});
            skCircle(sketch, "E2.30.38.0", {"center": v(203.2, -406.4) * mm, "radius": 3.3 * mm});
            skCircle(sketch, "E2.30.39.0", {"center": v(203.2, -431.8) * mm, "radius": 3.3 * mm});
            skCircle(sketch, "E2.30.40.0", {"center": v(203.2, -457.2) * mm, "radius": 3.3 * mm});
            skCircle(sketch, "E2.30.41.0", {"center": v(203.2, -482.6) * mm, "radius": 3.3 * mm});
            skCircle(sketch, "E2.30.42.0", {"center": v(203.2, -508) * mm, "radius": 3.3 * mm});
            skCircle(sketch, "E2.30.43.0", {"center": v(203.2, -533.4) * mm, "radius": 3.3 * mm});
            skCircle(sketch, "E2.30.44.0", {"center": v(203.2, -558.8) * mm, "radius": 3.3 * mm});
            skCircle(sketch, "E2.31.0.0", {"center": v(228.6, 558.8) * mm, "radius": 3.3 * mm});
            skCircle(sketch, "E2.31.1.0", {"center": v(228.6, 533.4) * mm, "radius": 3.3 * mm});
            skCircle(sketch, "E2.31.2.0", {"center": v(228.6, 508) * mm, "radius": 3.3 * mm});
            skCircle(sketch, "E2.31.3.0", {"center": v(228.6, 482.6) * mm, "radius": 3.3 * mm});
            skCircle(sketch, "E2.31.4.0", {"center": v(228.6, 457.2) * mm, "radius": 3.3 * mm});
            skCircle(sketch, "E2.31.5.0", {"center": v(228.6, 431.8) * mm, "radius": 3.3 * mm});
            skCircle(sketch, "E2.31.6.0", {"center": v(228.6, 406.4) * mm, "radius": 3.3 * mm});
            skCircle(sketch, "E2.31.7.0", {"center": v(228.6, 381) * mm, "radius": 3.3 * mm});
            skCircle(sketch, "E2.31.8.0", {"center": v(228.6, 355.6) * mm, "radius": 3.3 * mm});
            skCircle(sketch, "E2.31.9.0", {"center": v(228.6, 330.2) * mm, "radius": 3.3 * mm});
            skCircle(sketch, "E2.31.10.0", {"center": v(228.6, 304.8) * mm, "radius": 3.3 * mm});
            skCircle(sketch, "E2.31.11.0", {"center": v(228.6, 279.4) * mm, "radius": 3.3 * mm});
            skCircle(sketch, "E2.31.12.0", {"center": v(228.6, 254) * mm, "radius": 3.3 * mm});
            skCircle(sketch, "E2.31.13.0", {"center": v(228.6, 228.6) * mm, "radius": 3.3 * mm});
            skCircle(sketch, "E2.31.14.0", {"center": v(228.6, 203.2) * mm, "radius": 3.3 * mm});
            skCircle(sketch, "E2.31.15.0", {"center": v(228.6, 177.8) * mm, "radius": 3.3 * mm});
            skCircle(sketch, "E2.31.16.0", {"center": v(228.6, 152.4) * mm, "radius": 3.3 * mm});
            skCircle(sketch, "E2.31.17.0", {"center": v(228.6, 127) * mm, "radius": 3.3 * mm});
            skCircle(sketch, "E2.31.18.0", {"center": v(228.6, 101.6) * mm, "radius": 3.3 * mm});
            skCircle(sketch, "E2.31.19.0", {"center": v(228.6, 76.2) * mm, "radius": 3.3 * mm});
            skCircle(sketch, "E2.31.20.0", {"center": v(228.6, 50.8) * mm, "radius": 3.3 * mm});
            skCircle(sketch, "E2.31.21.0", {"center": v(228.6, 25.4) * mm, "radius": 3.3 * mm});
            skCircle(sketch, "E2.31.22.0", {"center": v(228.6, 0) * mm, "radius": 3.3 * mm});
            skCircle(sketch, "E2.31.23.0", {"center": v(228.6, -25.4) * mm, "radius": 3.3 * mm});
            skCircle(sketch, "E2.31.24.0", {"center": v(228.6, -50.8) * mm, "radius": 3.3 * mm});
            skCircle(sketch, "E2.31.25.0", {"center": v(228.6, -76.2) * mm, "radius": 3.3 * mm});
            skCircle(sketch, "E2.31.26.0", {"center": v(228.6, -101.6) * mm, "radius": 3.3 * mm});
            skCircle(sketch, "E2.31.27.0", {"center": v(228.6, -127) * mm, "radius": 3.3 * mm});
            skCircle(sketch, "E2.31.28.0", {"center": v(228.6, -152.4) * mm, "radius": 3.3 * mm});
            skCircle(sketch, "E2.31.29.0", {"center": v(228.6, -177.8) * mm, "radius": 3.3 * mm});
            skCircle(sketch, "E2.31.30.0", {"center": v(228.6, -203.2) * mm, "radius": 3.3 * mm});
            skCircle(sketch, "E2.31.31.0", {"center": v(228.6, -228.6) * mm, "radius": 3.3 * mm});
            skCircle(sketch, "E2.31.32.0", {"center": v(228.6, -254) * mm, "radius": 3.3 * mm});
            skCircle(sketch, "E2.31.33.0", {"center": v(228.6, -279.4) * mm, "radius": 3.3 * mm});
            skCircle(sketch, "E2.31.34.0", {"center": v(228.6, -304.8) * mm, "radius": 3.3 * mm});
            skCircle(sketch, "E2.31.35.0", {"center": v(228.6, -330.2) * mm, "radius": 3.3 * mm});
            skCircle(sketch, "E2.31.36.0", {"center": v(228.6, -355.6) * mm, "radius": 3.3 * mm});
            skCircle(sketch, "E2.31.37.0", {"center": v(228.6, -381) * mm, "radius": 3.3 * mm});
            skCircle(sketch, "E2.31.38.0", {"center": v(228.6, -406.4) * mm, "radius": 3.3 * mm});
            skCircle(sketch, "E2.31.39.0", {"center": v(228.6, -431.8) * mm, "radius": 3.3 * mm});
            skCircle(sketch, "E2.31.40.0", {"center": v(228.6, -457.2) * mm, "radius": 3.3 * mm});
            skCircle(sketch, "E2.31.41.0", {"center": v(228.6, -482.6) * mm, "radius": 3.3 * mm});
            skCircle(sketch, "E2.31.42.0", {"center": v(228.6, -508) * mm, "radius": 3.3 * mm});
            skCircle(sketch, "E2.31.43.0", {"center": v(228.6, -533.4) * mm, "radius": 3.3 * mm});
            skCircle(sketch, "E2.31.44.0", {"center": v(228.6, -558.8) * mm, "radius": 3.3 * mm});
            skCircle(sketch, "E2.32.0.0", {"center": v(254, 558.8) * mm, "radius": 3.3 * mm});
            skCircle(sketch, "E2.32.1.0", {"center": v(254, 533.4) * mm, "radius": 3.3 * mm});
            skCircle(sketch, "E2.32.2.0", {"center": v(254, 508) * mm, "radius": 3.3 * mm});
            skCircle(sketch, "E2.32.3.0", {"center": v(254, 482.6) * mm, "radius": 3.3 * mm});
            skCircle(sketch, "E2.32.4.0", {"center": v(254, 457.2) * mm, "radius": 3.3 * mm});
            skCircle(sketch, "E2.32.5.0", {"center": v(254, 431.8) * mm, "radius": 3.3 * mm});
            skCircle(sketch, "E2.32.6.0", {"center": v(254, 406.4) * mm, "radius": 3.3 * mm});
            skCircle(sketch, "E2.32.7.0", {"center": v(254, 381) * mm, "radius": 3.3 * mm});
            skCircle(sketch, "E2.32.8.0", {"center": v(254, 355.6) * mm, "radius": 3.3 * mm});
            skCircle(sketch, "E2.32.9.0", {"center": v(254, 330.2) * mm, "radius": 3.3 * mm});
            skCircle(sketch, "E2.32.10.0", {"center": v(254, 304.8) * mm, "radius": 3.3 * mm});
            skCircle(sketch, "E2.32.11.0", {"center": v(254, 279.4) * mm, "radius": 3.3 * mm});
            skCircle(sketch, "E2.32.12.0", {"center": v(254, 254) * mm, "radius": 3.3 * mm});
            skCircle(sketch, "E2.32.13.0", {"center": v(254, 228.6) * mm, "radius": 3.3 * mm});
            skCircle(sketch, "E2.32.14.0", {"center": v(254, 203.2) * mm, "radius": 3.3 * mm});
            skCircle(sketch, "E2.32.15.0", {"center": v(254, 177.8) * mm, "radius": 3.3 * mm});
            skCircle(sketch, "E2.32.16.0", {"center": v(254, 152.4) * mm, "radius": 3.3 * mm});
            skCircle(sketch, "E2.32.17.0", {"center": v(254, 127) * mm, "radius": 3.3 * mm});
            skCircle(sketch, "E2.32.18.0", {"center": v(254, 101.6) * mm, "radius": 3.3 * mm});
            skCircle(sketch, "E2.32.19.0", {"center": v(254, 76.2) * mm, "radius": 3.3 * mm});
            skCircle(sketch, "E2.32.20.0", {"center": v(254, 50.8) * mm, "radius": 3.3 * mm});
            skCircle(sketch, "E2.32.21.0", {"center": v(254, 25.4) * mm, "radius": 3.3 * mm});
            skCircle(sketch, "E2.32.22.0", {"center": v(254, 0) * mm, "radius": 3.3 * mm});
            skCircle(sketch, "E2.32.23.0", {"center": v(254, -25.4) * mm, "radius": 3.3 * mm});
            skCircle(sketch, "E2.32.24.0", {"center": v(254, -50.8) * mm, "radius": 3.3 * mm});
            skCircle(sketch, "E2.32.25.0", {"center": v(254, -76.2) * mm, "radius": 3.3 * mm});
            skCircle(sketch, "E2.32.26.0", {"center": v(254, -101.6) * mm, "radius": 3.3 * mm});
            skCircle(sketch, "E2.32.27.0", {"center": v(254, -127) * mm, "radius": 3.3 * mm});
            skCircle(sketch, "E2.32.28.0", {"center": v(254, -152.4) * mm, "radius": 3.3 * mm});
            skCircle(sketch, "E2.32.29.0", {"center": v(254, -177.8) * mm, "radius": 3.3 * mm});
            skCircle(sketch, "E2.32.30.0", {"center": v(254, -203.2) * mm, "radius": 3.3 * mm});
            skCircle(sketch, "E2.32.31.0", {"center": v(254, -228.6) * mm, "radius": 3.3 * mm});
            skCircle(sketch, "E2.32.32.0", {"center": v(254, -254) * mm, "radius": 3.3 * mm});
            skCircle(sketch, "E2.32.33.0", {"center": v(254, -279.4) * mm, "radius": 3.3 * mm});
            skCircle(sketch, "E2.32.34.0", {"center": v(254, -304.8) * mm, "radius": 3.3 * mm});
            skCircle(sketch, "E2.32.35.0", {"center": v(254, -330.2) * mm, "radius": 3.3 * mm});
            skCircle(sketch, "E2.32.36.0", {"center": v(254, -355.6) * mm, "radius": 3.3 * mm});
            skCircle(sketch, "E2.32.37.0", {"center": v(254, -381) * mm, "radius": 3.3 * mm});
            skCircle(sketch, "E2.32.38.0", {"center": v(254, -406.4) * mm, "radius": 3.3 * mm});
            skCircle(sketch, "E2.32.39.0", {"center": v(254, -431.8) * mm, "radius": 3.3 * mm});
            skCircle(sketch, "E2.32.40.0", {"center": v(254, -457.2) * mm, "radius": 3.3 * mm});
            skCircle(sketch, "E2.32.41.0", {"center": v(254, -482.6) * mm, "radius": 3.3 * mm});
            skCircle(sketch, "E2.32.42.0", {"center": v(254, -508) * mm, "radius": 3.3 * mm});
            skCircle(sketch, "E2.32.43.0", {"center": v(254, -533.4) * mm, "radius": 3.3 * mm});
            skCircle(sketch, "E2.32.44.0", {"center": v(254, -558.8) * mm, "radius": 3.3 * mm});
            skCircle(sketch, "E2.33.0.0", {"center": v(279.4, 558.8) * mm, "radius": 3.3 * mm});
            skCircle(sketch, "E2.33.1.0", {"center": v(279.4, 533.4) * mm, "radius": 3.3 * mm});
            skCircle(sketch, "E2.33.2.0", {"center": v(279.4, 508) * mm, "radius": 3.3 * mm});
            skCircle(sketch, "E2.33.3.0", {"center": v(279.4, 482.6) * mm, "radius": 3.3 * mm});
            skCircle(sketch, "E2.33.4.0", {"center": v(279.4, 457.2) * mm, "radius": 3.3 * mm});
            skCircle(sketch, "E2.33.5.0", {"center": v(279.4, 431.8) * mm, "radius": 3.3 * mm});
            skCircle(sketch, "E2.33.6.0", {"center": v(279.4, 406.4) * mm, "radius": 3.3 * mm});
            skCircle(sketch, "E2.33.7.0", {"center": v(279.4, 381) * mm, "radius": 3.3 * mm});
            skCircle(sketch, "E2.33.8.0", {"center": v(279.4, 355.6) * mm, "radius": 3.3 * mm});
            skCircle(sketch, "E2.33.9.0", {"center": v(279.4, 330.2) * mm, "radius": 3.3 * mm});
            skCircle(sketch, "E2.33.10.0", {"center": v(279.4, 304.8) * mm, "radius": 3.3 * mm});
            skCircle(sketch, "E2.33.11.0", {"center": v(279.4, 279.4) * mm, "radius": 3.3 * mm});
            skCircle(sketch, "E2.33.12.0", {"center": v(279.4, 254) * mm, "radius": 3.3 * mm});
            skCircle(sketch, "E2.33.13.0", {"center": v(279.4, 228.6) * mm, "radius": 3.3 * mm});
            skCircle(sketch, "E2.33.14.0", {"center": v(279.4, 203.2) * mm, "radius": 3.3 * mm});
            skCircle(sketch, "E2.33.15.0", {"center": v(279.4, 177.8) * mm, "radius": 3.3 * mm});
            skCircle(sketch, "E2.33.16.0", {"center": v(279.4, 152.4) * mm, "radius": 3.3 * mm});
            skCircle(sketch, "E2.33.17.0", {"center": v(279.4, 127) * mm, "radius": 3.3 * mm});
            skCircle(sketch, "E2.33.18.0", {"center": v(279.4, 101.6) * mm, "radius": 3.3 * mm});
            skCircle(sketch, "E2.33.19.0", {"center": v(279.4, 76.2) * mm, "radius": 3.3 * mm});
            skCircle(sketch, "E2.33.20.0", {"center": v(279.4, 50.8) * mm, "radius": 3.3 * mm});
            skCircle(sketch, "E2.33.21.0", {"center": v(279.4, 25.4) * mm, "radius": 3.3 * mm});
            skCircle(sketch, "E2.33.22.0", {"center": v(279.4, 0) * mm, "radius": 3.3 * mm});
            skCircle(sketch, "E2.33.23.0", {"center": v(279.4, -25.4) * mm, "radius": 3.3 * mm});
            skCircle(sketch, "E2.33.24.0", {"center": v(279.4, -50.8) * mm, "radius": 3.3 * mm});
            skCircle(sketch, "E2.33.25.0", {"center": v(279.4, -76.2) * mm, "radius": 3.3 * mm});
            skCircle(sketch, "E2.33.26.0", {"center": v(279.4, -101.6) * mm, "radius": 3.3 * mm});
            skCircle(sketch, "E2.33.27.0", {"center": v(279.4, -127) * mm, "radius": 3.3 * mm});
            skCircle(sketch, "E2.33.28.0", {"center": v(279.4, -152.4) * mm, "radius": 3.3 * mm});
            skCircle(sketch, "E2.33.29.0", {"center": v(279.4, -177.8) * mm, "radius": 3.3 * mm});
            skCircle(sketch, "E2.33.30.0", {"center": v(279.4, -203.2) * mm, "radius": 3.3 * mm});
            skCircle(sketch, "E2.33.31.0", {"center": v(279.4, -228.6) * mm, "radius": 3.3 * mm});
            skCircle(sketch, "E2.33.32.0", {"center": v(279.4, -254) * mm, "radius": 3.3 * mm});
            skCircle(sketch, "E2.33.33.0", {"center": v(279.4, -279.4) * mm, "radius": 3.3 * mm});
            skCircle(sketch, "E2.33.34.0", {"center": v(279.4, -304.8) * mm, "radius": 3.3 * mm});
            skCircle(sketch, "E2.33.35.0", {"center": v(279.4, -330.2) * mm, "radius": 3.3 * mm});
            skCircle(sketch, "E2.33.36.0", {"center": v(279.4, -355.6) * mm, "radius": 3.3 * mm});
            skCircle(sketch, "E2.33.37.0", {"center": v(279.4, -381) * mm, "radius": 3.3 * mm});
            skCircle(sketch, "E2.33.38.0", {"center": v(279.4, -406.4) * mm, "radius": 3.3 * mm});
            skCircle(sketch, "E2.33.39.0", {"center": v(279.4, -431.8) * mm, "radius": 3.3 * mm});
            skCircle(sketch, "E2.33.40.0", {"center": v(279.4, -457.2) * mm, "radius": 3.3 * mm});
            skCircle(sketch, "E2.33.41.0", {"center": v(279.4, -482.6) * mm, "radius": 3.3 * mm});
            skCircle(sketch, "E2.33.42.0", {"center": v(279.4, -508) * mm, "radius": 3.3 * mm});
            skCircle(sketch, "E2.33.43.0", {"center": v(279.4, -533.4) * mm, "radius": 3.3 * mm});
            skCircle(sketch, "E2.33.44.0", {"center": v(279.4, -558.8) * mm, "radius": 3.3 * mm});
            skCircle(sketch, "E2.34.0.0", {"center": v(304.8, 558.8) * mm, "radius": 3.3 * mm});
            skCircle(sketch, "E2.34.1.0", {"center": v(304.8, 533.4) * mm, "radius": 3.3 * mm});
            skCircle(sketch, "E2.34.2.0", {"center": v(304.8, 508) * mm, "radius": 3.3 * mm});
            skCircle(sketch, "E2.34.3.0", {"center": v(304.8, 482.6) * mm, "radius": 3.3 * mm});
            skCircle(sketch, "E2.34.4.0", {"center": v(304.8, 457.2) * mm, "radius": 3.3 * mm});
            skCircle(sketch, "E2.34.5.0", {"center": v(304.8, 431.8) * mm, "radius": 3.3 * mm});
            skCircle(sketch, "E2.34.6.0", {"center": v(304.8, 406.4) * mm, "radius": 3.3 * mm});
            skCircle(sketch, "E2.34.7.0", {"center": v(304.8, 381) * mm, "radius": 3.3 * mm});
            skCircle(sketch, "E2.34.8.0", {"center": v(304.8, 355.6) * mm, "radius": 3.3 * mm});
            skCircle(sketch, "E2.34.9.0", {"center": v(304.8, 330.2) * mm, "radius": 3.3 * mm});
            skCircle(sketch, "E2.34.10.0", {"center": v(304.8, 304.8) * mm, "radius": 3.3 * mm});
            skCircle(sketch, "E2.34.11.0", {"center": v(304.8, 279.4) * mm, "radius": 3.3 * mm});
            skCircle(sketch, "E2.34.12.0", {"center": v(304.8, 254) * mm, "radius": 3.3 * mm});
            skCircle(sketch, "E2.34.13.0", {"center": v(304.8, 228.6) * mm, "radius": 3.3 * mm});
            skCircle(sketch, "E2.34.14.0", {"center": v(304.8, 203.2) * mm, "radius": 3.3 * mm});
            skCircle(sketch, "E2.34.15.0", {"center": v(304.8, 177.8) * mm, "radius": 3.3 * mm});
            skCircle(sketch, "E2.34.16.0", {"center": v(304.8, 152.4) * mm, "radius": 3.3 * mm});
            skCircle(sketch, "E2.34.17.0", {"center": v(304.8, 127) * mm, "radius": 3.3 * mm});
            skCircle(sketch, "E2.34.18.0", {"center": v(304.8, 101.6) * mm, "radius": 3.3 * mm});
            skCircle(sketch, "E2.34.19.0", {"center": v(304.8, 76.2) * mm, "radius": 3.3 * mm});
            skCircle(sketch, "E2.34.20.0", {"center": v(304.8, 50.8) * mm, "radius": 3.3 * mm});
            skCircle(sketch, "E2.34.21.0", {"center": v(304.8, 25.4) * mm, "radius": 3.3 * mm});
            skCircle(sketch, "E2.34.22.0", {"center": v(304.8, 0) * mm, "radius": 3.3 * mm});
            skCircle(sketch, "E2.34.23.0", {"center": v(304.8, -25.4) * mm, "radius": 3.3 * mm});
            skCircle(sketch, "E2.34.24.0", {"center": v(304.8, -50.8) * mm, "radius": 3.3 * mm});
            skCircle(sketch, "E2.34.25.0", {"center": v(304.8, -76.2) * mm, "radius": 3.3 * mm});
            skCircle(sketch, "E2.34.26.0", {"center": v(304.8, -101.6) * mm, "radius": 3.3 * mm});
            skCircle(sketch, "E2.34.27.0", {"center": v(304.8, -127) * mm, "radius": 3.3 * mm});
            skCircle(sketch, "E2.34.28.0", {"center": v(304.8, -152.4) * mm, "radius": 3.3 * mm});
            skCircle(sketch, "E2.34.29.0", {"center": v(304.8, -177.8) * mm, "radius": 3.3 * mm});
            skCircle(sketch, "E2.34.30.0", {"center": v(304.8, -203.2) * mm, "radius": 3.3 * mm});
            skCircle(sketch, "E2.34.31.0", {"center": v(304.8, -228.6) * mm, "radius": 3.3 * mm});
            skCircle(sketch, "E2.34.32.0", {"center": v(304.8, -254) * mm, "radius": 3.3 * mm});
            skCircle(sketch, "E2.34.33.0", {"center": v(304.8, -279.4) * mm, "radius": 3.3 * mm});
            skCircle(sketch, "E2.34.34.0", {"center": v(304.8, -304.8) * mm, "radius": 3.3 * mm});
            skCircle(sketch, "E2.34.35.0", {"center": v(304.8, -330.2) * mm, "radius": 3.3 * mm});
            skCircle(sketch, "E2.34.36.0", {"center": v(304.8, -355.6) * mm, "radius": 3.3 * mm});
            skCircle(sketch, "E2.34.37.0", {"center": v(304.8, -381) * mm, "radius": 3.3 * mm});
            skCircle(sketch, "E2.34.38.0", {"center": v(304.8, -406.4) * mm, "radius": 3.3 * mm});
            skCircle(sketch, "E2.34.39.0", {"center": v(304.8, -431.8) * mm, "radius": 3.3 * mm});
            skCircle(sketch, "E2.34.40.0", {"center": v(304.8, -457.2) * mm, "radius": 3.3 * mm});
            skCircle(sketch, "E2.34.41.0", {"center": v(304.8, -482.6) * mm, "radius": 3.3 * mm});
            skCircle(sketch, "E2.34.42.0", {"center": v(304.8, -508) * mm, "radius": 3.3 * mm});
            skCircle(sketch, "E2.34.43.0", {"center": v(304.8, -533.4) * mm, "radius": 3.3 * mm});
            skCircle(sketch, "E2.34.44.0", {"center": v(304.8, -558.8) * mm, "radius": 3.3 * mm});
            skCircle(sketch, "E2.35.0.0", {"center": v(330.2, 558.8) * mm, "radius": 3.3 * mm});
            skCircle(sketch, "E2.35.1.0", {"center": v(330.2, 533.4) * mm, "radius": 3.3 * mm});
            skCircle(sketch, "E2.35.2.0", {"center": v(330.2, 508) * mm, "radius": 3.3 * mm});
            skCircle(sketch, "E2.35.3.0", {"center": v(330.2, 482.6) * mm, "radius": 3.3 * mm});
            skCircle(sketch, "E2.35.4.0", {"center": v(330.2, 457.2) * mm, "radius": 3.3 * mm});
            skCircle(sketch, "E2.35.5.0", {"center": v(330.2, 431.8) * mm, "radius": 3.3 * mm});
            skCircle(sketch, "E2.35.6.0", {"center": v(330.2, 406.4) * mm, "radius": 3.3 * mm});
            skCircle(sketch, "E2.35.7.0", {"center": v(330.2, 381) * mm, "radius": 3.3 * mm});
            skCircle(sketch, "E2.35.8.0", {"center": v(330.2, 355.6) * mm, "radius": 3.3 * mm});
            skCircle(sketch, "E2.35.9.0", {"center": v(330.2, 330.2) * mm, "radius": 3.3 * mm});
            skCircle(sketch, "E2.35.10.0", {"center": v(330.2, 304.8) * mm, "radius": 3.3 * mm});
            skCircle(sketch, "E2.35.11.0", {"center": v(330.2, 279.4) * mm, "radius": 3.3 * mm});
            skCircle(sketch, "E2.35.12.0", {"center": v(330.2, 254) * mm, "radius": 3.3 * mm});
            skCircle(sketch, "E2.35.13.0", {"center": v(330.2, 228.6) * mm, "radius": 3.3 * mm});
            skCircle(sketch, "E2.35.14.0", {"center": v(330.2, 203.2) * mm, "radius": 3.3 * mm});
            skCircle(sketch, "E2.35.15.0", {"center": v(330.2, 177.8) * mm, "radius": 3.3 * mm});
            skCircle(sketch, "E2.35.16.0", {"center": v(330.2, 152.4) * mm, "radius": 3.3 * mm});
            skCircle(sketch, "E2.35.17.0", {"center": v(330.2, 127) * mm, "radius": 3.3 * mm});
            skCircle(sketch, "E2.35.18.0", {"center": v(330.2, 101.6) * mm, "radius": 3.3 * mm});
            skCircle(sketch, "E2.35.19.0", {"center": v(330.2, 76.2) * mm, "radius": 3.3 * mm});
            skCircle(sketch, "E2.35.20.0", {"center": v(330.2, 50.8) * mm, "radius": 3.3 * mm});
            skCircle(sketch, "E2.35.21.0", {"center": v(330.2, 25.4) * mm, "radius": 3.3 * mm});
            skCircle(sketch, "E2.35.22.0", {"center": v(330.2, 0) * mm, "radius": 3.3 * mm});
            skCircle(sketch, "E2.35.23.0", {"center": v(330.2, -25.4) * mm, "radius": 3.3 * mm});
            skCircle(sketch, "E2.35.24.0", {"center": v(330.2, -50.8) * mm, "radius": 3.3 * mm});
            skCircle(sketch, "E2.35.25.0", {"center": v(330.2, -76.2) * mm, "radius": 3.3 * mm});
            skCircle(sketch, "E2.35.26.0", {"center": v(330.2, -101.6) * mm, "radius": 3.3 * mm});
            skCircle(sketch, "E2.35.27.0", {"center": v(330.2, -127) * mm, "radius": 3.3 * mm});
            skCircle(sketch, "E2.35.28.0", {"center": v(330.2, -152.4) * mm, "radius": 3.3 * mm});
            skCircle(sketch, "E2.35.29.0", {"center": v(330.2, -177.8) * mm, "radius": 3.3 * mm});
            skCircle(sketch, "E2.35.30.0", {"center": v(330.2, -203.2) * mm, "radius": 3.3 * mm});
            skCircle(sketch, "E2.35.31.0", {"center": v(330.2, -228.6) * mm, "radius": 3.3 * mm});
            skCircle(sketch, "E2.35.32.0", {"center": v(330.2, -254) * mm, "radius": 3.3 * mm});
            skCircle(sketch, "E2.35.33.0", {"center": v(330.2, -279.4) * mm, "radius": 3.3 * mm});
            skCircle(sketch, "E2.35.34.0", {"center": v(330.2, -304.8) * mm, "radius": 3.3 * mm});
            skCircle(sketch, "E2.35.35.0", {"center": v(330.2, -330.2) * mm, "radius": 3.3 * mm});
            skCircle(sketch, "E2.35.36.0", {"center": v(330.2, -355.6) * mm, "radius": 3.3 * mm});
            skCircle(sketch, "E2.35.37.0", {"center": v(330.2, -381) * mm, "radius": 3.3 * mm});
            skCircle(sketch, "E2.35.38.0", {"center": v(330.2, -406.4) * mm, "radius": 3.3 * mm});
            skCircle(sketch, "E2.35.39.0", {"center": v(330.2, -431.8) * mm, "radius": 3.3 * mm});
            skCircle(sketch, "E2.35.40.0", {"center": v(330.2, -457.2) * mm, "radius": 3.3 * mm});
            skCircle(sketch, "E2.35.41.0", {"center": v(330.2, -482.6) * mm, "radius": 3.3 * mm});
            skCircle(sketch, "E2.35.42.0", {"center": v(330.2, -508) * mm, "radius": 3.3 * mm});
            skCircle(sketch, "E2.35.43.0", {"center": v(330.2, -533.4) * mm, "radius": 3.3 * mm});
            skCircle(sketch, "E2.35.44.0", {"center": v(330.2, -558.8) * mm, "radius": 3.3 * mm});
            skCircle(sketch, "E2.36.0.0", {"center": v(355.6, 558.8) * mm, "radius": 3.3 * mm});
            skCircle(sketch, "E2.36.1.0", {"center": v(355.6, 533.4) * mm, "radius": 3.3 * mm});
            skCircle(sketch, "E2.36.2.0", {"center": v(355.6, 508) * mm, "radius": 3.3 * mm});
            skCircle(sketch, "E2.36.3.0", {"center": v(355.6, 482.6) * mm, "radius": 3.3 * mm});
            skCircle(sketch, "E2.36.4.0", {"center": v(355.6, 457.2) * mm, "radius": 3.3 * mm});
            skCircle(sketch, "E2.36.5.0", {"center": v(355.6, 431.8) * mm, "radius": 3.3 * mm});
            skCircle(sketch, "E2.36.6.0", {"center": v(355.6, 406.4) * mm, "radius": 3.3 * mm});
            skCircle(sketch, "E2.36.7.0", {"center": v(355.6, 381) * mm, "radius": 3.3 * mm});
            skCircle(sketch, "E2.36.8.0", {"center": v(355.6, 355.6) * mm, "radius": 3.3 * mm});
            skCircle(sketch, "E2.36.9.0", {"center": v(355.6, 330.2) * mm, "radius": 3.3 * mm});
            skCircle(sketch, "E2.36.10.0", {"center": v(355.6, 304.8) * mm, "radius": 3.3 * mm});
            skCircle(sketch, "E2.36.11.0", {"center": v(355.6, 279.4) * mm, "radius": 3.3 * mm});
            skCircle(sketch, "E2.36.12.0", {"center": v(355.6, 254) * mm, "radius": 3.3 * mm});
            skCircle(sketch, "E2.36.13.0", {"center": v(355.6, 228.6) * mm, "radius": 3.3 * mm});
            skCircle(sketch, "E2.36.14.0", {"center": v(355.6, 203.2) * mm, "radius": 3.3 * mm});
            skCircle(sketch, "E2.36.15.0", {"center": v(355.6, 177.8) * mm, "radius": 3.3 * mm});
            skCircle(sketch, "E2.36.16.0", {"center": v(355.6, 152.4) * mm, "radius": 3.3 * mm});
            skCircle(sketch, "E2.36.17.0", {"center": v(355.6, 127) * mm, "radius": 3.3 * mm});
            skCircle(sketch, "E2.36.18.0", {"center": v(355.6, 101.6) * mm, "radius": 3.3 * mm});
            skCircle(sketch, "E2.36.19.0", {"center": v(355.6, 76.2) * mm, "radius": 3.3 * mm});
            skCircle(sketch, "E2.36.20.0", {"center": v(355.6, 50.8) * mm, "radius": 3.3 * mm});
            skCircle(sketch, "E2.36.21.0", {"center": v(355.6, 25.4) * mm, "radius": 3.3 * mm});
            skCircle(sketch, "E2.36.22.0", {"center": v(355.6, 0) * mm, "radius": 3.3 * mm});
            skCircle(sketch, "E2.36.23.0", {"center": v(355.6, -25.4) * mm, "radius": 3.3 * mm});
            skCircle(sketch, "E2.36.24.0", {"center": v(355.6, -50.8) * mm, "radius": 3.3 * mm});
            skCircle(sketch, "E2.36.25.0", {"center": v(355.6, -76.2) * mm, "radius": 3.3 * mm});
            skCircle(sketch, "E2.36.26.0", {"center": v(355.6, -101.6) * mm, "radius": 3.3 * mm});
            skCircle(sketch, "E2.36.27.0", {"center": v(355.6, -127) * mm, "radius": 3.3 * mm});
            skCircle(sketch, "E2.36.28.0", {"center": v(355.6, -152.4) * mm, "radius": 3.3 * mm});
            skCircle(sketch, "E2.36.29.0", {"center": v(355.6, -177.8) * mm, "radius": 3.3 * mm});
            skCircle(sketch, "E2.36.30.0", {"center": v(355.6, -203.2) * mm, "radius": 3.3 * mm});
            skCircle(sketch, "E2.36.31.0", {"center": v(355.6, -228.6) * mm, "radius": 3.3 * mm});
            skCircle(sketch, "E2.36.32.0", {"center": v(355.6, -254) * mm, "radius": 3.3 * mm});
            skCircle(sketch, "E2.36.33.0", {"center": v(355.6, -279.4) * mm, "radius": 3.3 * mm});
            skCircle(sketch, "E2.36.34.0", {"center": v(355.6, -304.8) * mm, "radius": 3.3 * mm});
            skCircle(sketch, "E2.36.35.0", {"center": v(355.6, -330.2) * mm, "radius": 3.3 * mm});
            skCircle(sketch, "E2.36.36.0", {"center": v(355.6, -355.6) * mm, "radius": 3.3 * mm});
            skCircle(sketch, "E2.36.37.0", {"center": v(355.6, -381) * mm, "radius": 3.3 * mm});
            skCircle(sketch, "E2.36.38.0", {"center": v(355.6, -406.4) * mm, "radius": 3.3 * mm});
            skCircle(sketch, "E2.36.39.0", {"center": v(355.6, -431.8) * mm, "radius": 3.3 * mm});
            skCircle(sketch, "E2.36.40.0", {"center": v(355.6, -457.2) * mm, "radius": 3.3 * mm});
            skCircle(sketch, "E2.36.41.0", {"center": v(355.6, -482.6) * mm, "radius": 3.3 * mm});
            skCircle(sketch, "E2.36.42.0", {"center": v(355.6, -508) * mm, "radius": 3.3 * mm});
            skCircle(sketch, "E2.36.43.0", {"center": v(355.6, -533.4) * mm, "radius": 3.3 * mm});
            skCircle(sketch, "E2.36.44.0", {"center": v(355.6, -558.8) * mm, "radius": 3.3 * mm});
            skCircle(sketch, "E2.37.0.0", {"center": v(381, 558.8) * mm, "radius": 3.3 * mm});
            skCircle(sketch, "E2.37.1.0", {"center": v(381, 533.4) * mm, "radius": 3.3 * mm});
            skCircle(sketch, "E2.37.2.0", {"center": v(381, 508) * mm, "radius": 3.3 * mm});
            skCircle(sketch, "E2.37.3.0", {"center": v(381, 482.6) * mm, "radius": 3.3 * mm});
            skCircle(sketch, "E2.37.4.0", {"center": v(381, 457.2) * mm, "radius": 3.3 * mm});
            skCircle(sketch, "E2.37.5.0", {"center": v(381, 431.8) * mm, "radius": 3.3 * mm});
            skCircle(sketch, "E2.37.6.0", {"center": v(381, 406.4) * mm, "radius": 3.3 * mm});
            skCircle(sketch, "E2.37.7.0", {"center": v(381, 381) * mm, "radius": 3.3 * mm});
            skCircle(sketch, "E2.37.8.0", {"center": v(381, 355.6) * mm, "radius": 3.3 * mm});
            skCircle(sketch, "E2.37.9.0", {"center": v(381, 330.2) * mm, "radius": 3.3 * mm});
            skCircle(sketch, "E2.37.10.0", {"center": v(381, 304.8) * mm, "radius": 3.3 * mm});
            skCircle(sketch, "E2.37.11.0", {"center": v(381, 279.4) * mm, "radius": 3.3 * mm});
            skCircle(sketch, "E2.37.12.0", {"center": v(381, 254) * mm, "radius": 3.3 * mm});
            skCircle(sketch, "E2.37.13.0", {"center": v(381, 228.6) * mm, "radius": 3.3 * mm});
            skCircle(sketch, "E2.37.14.0", {"center": v(381, 203.2) * mm, "radius": 3.3 * mm});
            skCircle(sketch, "E2.37.15.0", {"center": v(381, 177.8) * mm, "radius": 3.3 * mm});
            skCircle(sketch, "E2.37.16.0", {"center": v(381, 152.4) * mm, "radius": 3.3 * mm});
            skCircle(sketch, "E2.37.17.0", {"center": v(381, 127) * mm, "radius": 3.3 * mm});
            skCircle(sketch, "E2.37.18.0", {"center": v(381, 101.6) * mm, "radius": 3.3 * mm});
            skCircle(sketch, "E2.37.19.0", {"center": v(381, 76.2) * mm, "radius": 3.3 * mm});
            skCircle(sketch, "E2.37.20.0", {"center": v(381, 50.8) * mm, "radius": 3.3 * mm});
            skCircle(sketch, "E2.37.21.0", {"center": v(381, 25.4) * mm, "radius": 3.3 * mm});
            skCircle(sketch, "E2.37.22.0", {"center": v(381, 0) * mm, "radius": 3.3 * mm});
            skCircle(sketch, "E2.37.23.0", {"center": v(381, -25.4) * mm, "radius": 3.3 * mm});
            skCircle(sketch, "E2.37.24.0", {"center": v(381, -50.8) * mm, "radius": 3.3 * mm});
            skCircle(sketch, "E2.37.25.0", {"center": v(381, -76.2) * mm, "radius": 3.3 * mm});
            skCircle(sketch, "E2.37.26.0", {"center": v(381, -101.6) * mm, "radius": 3.3 * mm});
            skCircle(sketch, "E2.37.27.0", {"center": v(381, -127) * mm, "radius": 3.3 * mm});
            skCircle(sketch, "E2.37.28.0", {"center": v(381, -152.4) * mm, "radius": 3.3 * mm});
            skCircle(sketch, "E2.37.29.0", {"center": v(381, -177.8) * mm, "radius": 3.3 * mm});
            skCircle(sketch, "E2.37.30.0", {"center": v(381, -203.2) * mm, "radius": 3.3 * mm});
            skCircle(sketch, "E2.37.31.0", {"center": v(381, -228.6) * mm, "radius": 3.3 * mm});
            skCircle(sketch, "E2.37.32.0", {"center": v(381, -254) * mm, "radius": 3.3 * mm});
            skCircle(sketch, "E2.37.33.0", {"center": v(381, -279.4) * mm, "radius": 3.3 * mm});
            skCircle(sketch, "E2.37.34.0", {"center": v(381, -304.8) * mm, "radius": 3.3 * mm});
            skCircle(sketch, "E2.37.35.0", {"center": v(381, -330.2) * mm, "radius": 3.3 * mm});
            skCircle(sketch, "E2.37.36.0", {"center": v(381, -355.6) * mm, "radius": 3.3 * mm});
            skCircle(sketch, "E2.37.37.0", {"center": v(381, -381) * mm, "radius": 3.3 * mm});
            skCircle(sketch, "E2.37.38.0", {"center": v(381, -406.4) * mm, "radius": 3.3 * mm});
            skCircle(sketch, "E2.37.39.0", {"center": v(381, -431.8) * mm, "radius": 3.3 * mm});
            skCircle(sketch, "E2.37.40.0", {"center": v(381, -457.2) * mm, "radius": 3.3 * mm});
            skCircle(sketch, "E2.37.41.0", {"center": v(381, -482.6) * mm, "radius": 3.3 * mm});
            skCircle(sketch, "E2.37.42.0", {"center": v(381, -508) * mm, "radius": 3.3 * mm});
            skCircle(sketch, "E2.37.43.0", {"center": v(381, -533.4) * mm, "radius": 3.3 * mm});
            skCircle(sketch, "E2.37.44.0", {"center": v(381, -558.8) * mm, "radius": 3.3 * mm});
            skCircle(sketch, "E2.38.0.0", {"center": v(406.4, 558.8) * mm, "radius": 3.3 * mm});
            skCircle(sketch, "E2.38.1.0", {"center": v(406.4, 533.4) * mm, "radius": 3.3 * mm});
            skCircle(sketch, "E2.38.2.0", {"center": v(406.4, 508) * mm, "radius": 3.3 * mm});
            skCircle(sketch, "E2.38.3.0", {"center": v(406.4, 482.6) * mm, "radius": 3.3 * mm});
            skCircle(sketch, "E2.38.4.0", {"center": v(406.4, 457.2) * mm, "radius": 3.3 * mm});
            skCircle(sketch, "E2.38.5.0", {"center": v(406.4, 431.8) * mm, "radius": 3.3 * mm});
            skCircle(sketch, "E2.38.6.0", {"center": v(406.4, 406.4) * mm, "radius": 3.3 * mm});
            skCircle(sketch, "E2.38.7.0", {"center": v(406.4, 381) * mm, "radius": 3.3 * mm});
            skCircle(sketch, "E2.38.8.0", {"center": v(406.4, 355.6) * mm, "radius": 3.3 * mm});
            skCircle(sketch, "E2.38.9.0", {"center": v(406.4, 330.2) * mm, "radius": 3.3 * mm});
            skCircle(sketch, "E2.38.10.0", {"center": v(406.4, 304.8) * mm, "radius": 3.3 * mm});
            skCircle(sketch, "E2.38.11.0", {"center": v(406.4, 279.4) * mm, "radius": 3.3 * mm});
            skCircle(sketch, "E2.38.12.0", {"center": v(406.4, 254) * mm, "radius": 3.3 * mm});
            skCircle(sketch, "E2.38.13.0", {"center": v(406.4, 228.6) * mm, "radius": 3.3 * mm});
            skCircle(sketch, "E2.38.14.0", {"center": v(406.4, 203.2) * mm, "radius": 3.3 * mm});
            skCircle(sketch, "E2.38.15.0", {"center": v(406.4, 177.8) * mm, "radius": 3.3 * mm});
            skCircle(sketch, "E2.38.16.0", {"center": v(406.4, 152.4) * mm, "radius": 3.3 * mm});
            skCircle(sketch, "E2.38.17.0", {"center": v(406.4, 127) * mm, "radius": 3.3 * mm});
            skCircle(sketch, "E2.38.18.0", {"center": v(406.4, 101.6) * mm, "radius": 3.3 * mm});
            skCircle(sketch, "E2.38.19.0", {"center": v(406.4, 76.2) * mm, "radius": 3.3 * mm});
            skCircle(sketch, "E2.38.20.0", {"center": v(406.4, 50.8) * mm, "radius": 3.3 * mm});
            skCircle(sketch, "E2.38.21.0", {"center": v(406.4, 25.4) * mm, "radius": 3.3 * mm});
            skCircle(sketch, "E2.38.22.0", {"center": v(406.4, 0) * mm, "radius": 3.3 * mm});
            skCircle(sketch, "E2.38.23.0", {"center": v(406.4, -25.4) * mm, "radius": 3.3 * mm});
            skCircle(sketch, "E2.38.24.0", {"center": v(406.4, -50.8) * mm, "radius": 3.3 * mm});
            skCircle(sketch, "E2.38.25.0", {"center": v(406.4, -76.2) * mm, "radius": 3.3 * mm});
            skCircle(sketch, "E2.38.26.0", {"center": v(406.4, -101.6) * mm, "radius": 3.3 * mm});
            skCircle(sketch, "E2.38.27.0", {"center": v(406.4, -127) * mm, "radius": 3.3 * mm});
            skCircle(sketch, "E2.38.28.0", {"center": v(406.4, -152.4) * mm, "radius": 3.3 * mm});
            skCircle(sketch, "E2.38.29.0", {"center": v(406.4, -177.8) * mm, "radius": 3.3 * mm});
            skCircle(sketch, "E2.38.30.0", {"center": v(406.4, -203.2) * mm, "radius": 3.3 * mm});
            skCircle(sketch, "E2.38.31.0", {"center": v(406.4, -228.6) * mm, "radius": 3.3 * mm});
            skCircle(sketch, "E2.38.32.0", {"center": v(406.4, -254) * mm, "radius": 3.3 * mm});
            skCircle(sketch, "E2.38.33.0", {"center": v(406.4, -279.4) * mm, "radius": 3.3 * mm});
            skCircle(sketch, "E2.38.34.0", {"center": v(406.4, -304.8) * mm, "radius": 3.3 * mm});
            skCircle(sketch, "E2.38.35.0", {"center": v(406.4, -330.2) * mm, "radius": 3.3 * mm});
            skCircle(sketch, "E2.38.36.0", {"center": v(406.4, -355.6) * mm, "radius": 3.3 * mm});
            skCircle(sketch, "E2.38.37.0", {"center": v(406.4, -381) * mm, "radius": 3.3 * mm});
            skCircle(sketch, "E2.38.38.0", {"center": v(406.4, -406.4) * mm, "radius": 3.3 * mm});
            skCircle(sketch, "E2.38.39.0", {"center": v(406.4, -431.8) * mm, "radius": 3.3 * mm});
            skCircle(sketch, "E2.38.40.0", {"center": v(406.4, -457.2) * mm, "radius": 3.3 * mm});
            skCircle(sketch, "E2.38.41.0", {"center": v(406.4, -482.6) * mm, "radius": 3.3 * mm});
            skCircle(sketch, "E2.38.42.0", {"center": v(406.4, -508) * mm, "radius": 3.3 * mm});
            skCircle(sketch, "E2.38.43.0", {"center": v(406.4, -533.4) * mm, "radius": 3.3 * mm});
            skCircle(sketch, "E2.38.44.0", {"center": v(406.4, -558.8) * mm, "radius": 3.3 * mm});
            skCircle(sketch, "E2.39.0.0", {"center": v(431.8, 558.8) * mm, "radius": 3.3 * mm});
            skCircle(sketch, "E2.39.1.0", {"center": v(431.8, 533.4) * mm, "radius": 3.3 * mm});
            skCircle(sketch, "E2.39.2.0", {"center": v(431.8, 508) * mm, "radius": 3.3 * mm});
            skCircle(sketch, "E2.39.3.0", {"center": v(431.8, 482.6) * mm, "radius": 3.3 * mm});
            skCircle(sketch, "E2.39.4.0", {"center": v(431.8, 457.2) * mm, "radius": 3.3 * mm});
            skCircle(sketch, "E2.39.5.0", {"center": v(431.8, 431.8) * mm, "radius": 3.3 * mm});
            skCircle(sketch, "E2.39.6.0", {"center": v(431.8, 406.4) * mm, "radius": 3.3 * mm});
            skCircle(sketch, "E2.39.7.0", {"center": v(431.8, 381) * mm, "radius": 3.3 * mm});
            skCircle(sketch, "E2.39.8.0", {"center": v(431.8, 355.6) * mm, "radius": 3.3 * mm});
            skCircle(sketch, "E2.39.9.0", {"center": v(431.8, 330.2) * mm, "radius": 3.3 * mm});
            skCircle(sketch, "E2.39.10.0", {"center": v(431.8, 304.8) * mm, "radius": 3.3 * mm});
            skCircle(sketch, "E2.39.11.0", {"center": v(431.8, 279.4) * mm, "radius": 3.3 * mm});
            skCircle(sketch, "E2.39.12.0", {"center": v(431.8, 254) * mm, "radius": 3.3 * mm});
            skCircle(sketch, "E2.39.13.0", {"center": v(431.8, 228.6) * mm, "radius": 3.3 * mm});
            skCircle(sketch, "E2.39.14.0", {"center": v(431.8, 203.2) * mm, "radius": 3.3 * mm});
            skCircle(sketch, "E2.39.15.0", {"center": v(431.8, 177.8) * mm, "radius": 3.3 * mm});
            skCircle(sketch, "E2.39.16.0", {"center": v(431.8, 152.4) * mm, "radius": 3.3 * mm});
            skCircle(sketch, "E2.39.17.0", {"center": v(431.8, 127) * mm, "radius": 3.3 * mm});
            skCircle(sketch, "E2.39.18.0", {"center": v(431.8, 101.6) * mm, "radius": 3.3 * mm});
            skCircle(sketch, "E2.39.19.0", {"center": v(431.8, 76.2) * mm, "radius": 3.3 * mm});
            skCircle(sketch, "E2.39.20.0", {"center": v(431.8, 50.8) * mm, "radius": 3.3 * mm});
            skCircle(sketch, "E2.39.21.0", {"center": v(431.8, 25.4) * mm, "radius": 3.3 * mm});
            skCircle(sketch, "E2.39.22.0", {"center": v(431.8, 0) * mm, "radius": 3.3 * mm});
            skCircle(sketch, "E2.39.23.0", {"center": v(431.8, -25.4) * mm, "radius": 3.3 * mm});
            skCircle(sketch, "E2.39.24.0", {"center": v(431.8, -50.8) * mm, "radius": 3.3 * mm});
            skCircle(sketch, "E2.39.25.0", {"center": v(431.8, -76.2) * mm, "radius": 3.3 * mm});
            skCircle(sketch, "E2.39.26.0", {"center": v(431.8, -101.6) * mm, "radius": 3.3 * mm});
            skCircle(sketch, "E2.39.27.0", {"center": v(431.8, -127) * mm, "radius": 3.3 * mm});
            skCircle(sketch, "E2.39.28.0", {"center": v(431.8, -152.4) * mm, "radius": 3.3 * mm});
            skCircle(sketch, "E2.39.29.0", {"center": v(431.8, -177.8) * mm, "radius": 3.3 * mm});
            skCircle(sketch, "E2.39.30.0", {"center": v(431.8, -203.2) * mm, "radius": 3.3 * mm});
            skCircle(sketch, "E2.39.31.0", {"center": v(431.8, -228.6) * mm, "radius": 3.3 * mm});
            skCircle(sketch, "E2.39.32.0", {"center": v(431.8, -254) * mm, "radius": 3.3 * mm});
            skCircle(sketch, "E2.39.33.0", {"center": v(431.8, -279.4) * mm, "radius": 3.3 * mm});
            skCircle(sketch, "E2.39.34.0", {"center": v(431.8, -304.8) * mm, "radius": 3.3 * mm});
            skCircle(sketch, "E2.39.35.0", {"center": v(431.8, -330.2) * mm, "radius": 3.3 * mm});
            skCircle(sketch, "E2.39.36.0", {"center": v(431.8, -355.6) * mm, "radius": 3.3 * mm});
            skCircle(sketch, "E2.39.37.0", {"center": v(431.8, -381) * mm, "radius": 3.3 * mm});
            skCircle(sketch, "E2.39.38.0", {"center": v(431.8, -406.4) * mm, "radius": 3.3 * mm});
            skCircle(sketch, "E2.39.39.0", {"center": v(431.8, -431.8) * mm, "radius": 3.3 * mm});
            skCircle(sketch, "E2.39.40.0", {"center": v(431.8, -457.2) * mm, "radius": 3.3 * mm});
            skCircle(sketch, "E2.39.41.0", {"center": v(431.8, -482.6) * mm, "radius": 3.3 * mm});
            skCircle(sketch, "E2.39.42.0", {"center": v(431.8, -508) * mm, "radius": 3.3 * mm});
            skCircle(sketch, "E2.39.43.0", {"center": v(431.8, -533.4) * mm, "radius": 3.3 * mm});
            skCircle(sketch, "E2.39.44.0", {"center": v(431.8, -558.8) * mm, "radius": 3.3 * mm});
            skCircle(sketch, "E2.40.0.0", {"center": v(457.2, 558.8) * mm, "radius": 3.3 * mm});
            skCircle(sketch, "E2.40.1.0", {"center": v(457.2, 533.4) * mm, "radius": 3.3 * mm});
            skCircle(sketch, "E2.40.2.0", {"center": v(457.2, 508) * mm, "radius": 3.3 * mm});
            skCircle(sketch, "E2.40.3.0", {"center": v(457.2, 482.6) * mm, "radius": 3.3 * mm});
            skCircle(sketch, "E2.40.4.0", {"center": v(457.2, 457.2) * mm, "radius": 3.3 * mm});
            skCircle(sketch, "E2.40.5.0", {"center": v(457.2, 431.8) * mm, "radius": 3.3 * mm});
            skCircle(sketch, "E2.40.6.0", {"center": v(457.2, 406.4) * mm, "radius": 3.3 * mm});
            skCircle(sketch, "E2.40.7.0", {"center": v(457.2, 381) * mm, "radius": 3.3 * mm});
            skCircle(sketch, "E2.40.8.0", {"center": v(457.2, 355.6) * mm, "radius": 3.3 * mm});
            skCircle(sketch, "E2.40.9.0", {"center": v(457.2, 330.2) * mm, "radius": 3.3 * mm});
            skCircle(sketch, "E2.40.10.0", {"center": v(457.2, 304.8) * mm, "radius": 3.3 * mm});
            skCircle(sketch, "E2.40.11.0", {"center": v(457.2, 279.4) * mm, "radius": 3.3 * mm});
            skCircle(sketch, "E2.40.12.0", {"center": v(457.2, 254) * mm, "radius": 3.3 * mm});
            skCircle(sketch, "E2.40.13.0", {"center": v(457.2, 228.6) * mm, "radius": 3.3 * mm});
            skCircle(sketch, "E2.40.14.0", {"center": v(457.2, 203.2) * mm, "radius": 3.3 * mm});
            skCircle(sketch, "E2.40.15.0", {"center": v(457.2, 177.8) * mm, "radius": 3.3 * mm});
            skCircle(sketch, "E2.40.16.0", {"center": v(457.2, 152.4) * mm, "radius": 3.3 * mm});
            skCircle(sketch, "E2.40.17.0", {"center": v(457.2, 127) * mm, "radius": 3.3 * mm});
            skCircle(sketch, "E2.40.18.0", {"center": v(457.2, 101.6) * mm, "radius": 3.3 * mm});
            skCircle(sketch, "E2.40.19.0", {"center": v(457.2, 76.2) * mm, "radius": 3.3 * mm});
            skCircle(sketch, "E2.40.20.0", {"center": v(457.2, 50.8) * mm, "radius": 3.3 * mm});
            skCircle(sketch, "E2.40.21.0", {"center": v(457.2, 25.4) * mm, "radius": 3.3 * mm});
            skCircle(sketch, "E2.40.22.0", {"center": v(457.2, 0) * mm, "radius": 3.3 * mm});
            skCircle(sketch, "E2.40.23.0", {"center": v(457.2, -25.4) * mm, "radius": 3.3 * mm});
            skCircle(sketch, "E2.40.24.0", {"center": v(457.2, -50.8) * mm, "radius": 3.3 * mm});
            skCircle(sketch, "E2.40.25.0", {"center": v(457.2, -76.2) * mm, "radius": 3.3 * mm});
            skCircle(sketch, "E2.40.26.0", {"center": v(457.2, -101.6) * mm, "radius": 3.3 * mm});
            skCircle(sketch, "E2.40.27.0", {"center": v(457.2, -127) * mm, "radius": 3.3 * mm});
            skCircle(sketch, "E2.40.28.0", {"center": v(457.2, -152.4) * mm, "radius": 3.3 * mm});
            skCircle(sketch, "E2.40.29.0", {"center": v(457.2, -177.8) * mm, "radius": 3.3 * mm});
            skCircle(sketch, "E2.40.30.0", {"center": v(457.2, -203.2) * mm, "radius": 3.3 * mm});
            skCircle(sketch, "E2.40.31.0", {"center": v(457.2, -228.6) * mm, "radius": 3.3 * mm});
            skCircle(sketch, "E2.40.32.0", {"center": v(457.2, -254) * mm, "radius": 3.3 * mm});
            skCircle(sketch, "E2.40.33.0", {"center": v(457.2, -279.4) * mm, "radius": 3.3 * mm});
            skCircle(sketch, "E2.40.34.0", {"center": v(457.2, -304.8) * mm, "radius": 3.3 * mm});
            skCircle(sketch, "E2.40.35.0", {"center": v(457.2, -330.2) * mm, "radius": 3.3 * mm});
            skCircle(sketch, "E2.40.36.0", {"center": v(457.2, -355.6) * mm, "radius": 3.3 * mm});
            skCircle(sketch, "E2.40.37.0", {"center": v(457.2, -381) * mm, "radius": 3.3 * mm});
            skCircle(sketch, "E2.40.38.0", {"center": v(457.2, -406.4) * mm, "radius": 3.3 * mm});
            skCircle(sketch, "E2.40.39.0", {"center": v(457.2, -431.8) * mm, "radius": 3.3 * mm});
            skCircle(sketch, "E2.40.40.0", {"center": v(457.2, -457.2) * mm, "radius": 3.3 * mm});
            skCircle(sketch, "E2.40.41.0", {"center": v(457.2, -482.6) * mm, "radius": 3.3 * mm});
            skCircle(sketch, "E2.40.42.0", {"center": v(457.2, -508) * mm, "radius": 3.3 * mm});
            skCircle(sketch, "E2.40.43.0", {"center": v(457.2, -533.4) * mm, "radius": 3.3 * mm});
            skCircle(sketch, "E2.40.44.0", {"center": v(457.2, -558.8) * mm, "radius": 3.3 * mm});
            skCircle(sketch, "E2.41.0.0", {"center": v(482.6, 558.8) * mm, "radius": 3.3 * mm});
            skCircle(sketch, "E2.41.1.0", {"center": v(482.6, 533.4) * mm, "radius": 3.3 * mm});
            skCircle(sketch, "E2.41.2.0", {"center": v(482.6, 508) * mm, "radius": 3.3 * mm});
            skCircle(sketch, "E2.41.3.0", {"center": v(482.6, 482.6) * mm, "radius": 3.3 * mm});
            skCircle(sketch, "E2.41.4.0", {"center": v(482.6, 457.2) * mm, "radius": 3.3 * mm});
            skCircle(sketch, "E2.41.5.0", {"center": v(482.6, 431.8) * mm, "radius": 3.3 * mm});
            skCircle(sketch, "E2.41.6.0", {"center": v(482.6, 406.4) * mm, "radius": 3.3 * mm});
            skCircle(sketch, "E2.41.7.0", {"center": v(482.6, 381) * mm, "radius": 3.3 * mm});
            skCircle(sketch, "E2.41.8.0", {"center": v(482.6, 355.6) * mm, "radius": 3.3 * mm});
            skCircle(sketch, "E2.41.9.0", {"center": v(482.6, 330.2) * mm, "radius": 3.3 * mm});
            skCircle(sketch, "E2.41.10.0", {"center": v(482.6, 304.8) * mm, "radius": 3.3 * mm});
            skCircle(sketch, "E2.41.11.0", {"center": v(482.6, 279.4) * mm, "radius": 3.3 * mm});
            skCircle(sketch, "E2.41.12.0", {"center": v(482.6, 254) * mm, "radius": 3.3 * mm});
            skCircle(sketch, "E2.41.13.0", {"center": v(482.6, 228.6) * mm, "radius": 3.3 * mm});
            skCircle(sketch, "E2.41.14.0", {"center": v(482.6, 203.2) * mm, "radius": 3.3 * mm});
            skCircle(sketch, "E2.41.15.0", {"center": v(482.6, 177.8) * mm, "radius": 3.3 * mm});
            skCircle(sketch, "E2.41.16.0", {"center": v(482.6, 152.4) * mm, "radius": 3.3 * mm});
            skCircle(sketch, "E2.41.17.0", {"center": v(482.6, 127) * mm, "radius": 3.3 * mm});
            skCircle(sketch, "E2.41.18.0", {"center": v(482.6, 101.6) * mm, "radius": 3.3 * mm});
            skCircle(sketch, "E2.41.19.0", {"center": v(482.6, 76.2) * mm, "radius": 3.3 * mm});
            skCircle(sketch, "E2.41.20.0", {"center": v(482.6, 50.8) * mm, "radius": 3.3 * mm});
            skCircle(sketch, "E2.41.21.0", {"center": v(482.6, 25.4) * mm, "radius": 3.3 * mm});
            skCircle(sketch, "E2.41.22.0", {"center": v(482.6, 0) * mm, "radius": 3.3 * mm});
            skCircle(sketch, "E2.41.23.0", {"center": v(482.6, -25.4) * mm, "radius": 3.3 * mm});
            skCircle(sketch, "E2.41.24.0", {"center": v(482.6, -50.8) * mm, "radius": 3.3 * mm});
            skCircle(sketch, "E2.41.25.0", {"center": v(482.6, -76.2) * mm, "radius": 3.3 * mm});
            skCircle(sketch, "E2.41.26.0", {"center": v(482.6, -101.6) * mm, "radius": 3.3 * mm});
            skCircle(sketch, "E2.41.27.0", {"center": v(482.6, -127) * mm, "radius": 3.3 * mm});
            skCircle(sketch, "E2.41.28.0", {"center": v(482.6, -152.4) * mm, "radius": 3.3 * mm});
            skCircle(sketch, "E2.41.29.0", {"center": v(482.6, -177.8) * mm, "radius": 3.3 * mm});
            skCircle(sketch, "E2.41.30.0", {"center": v(482.6, -203.2) * mm, "radius": 3.3 * mm});
            skCircle(sketch, "E2.41.31.0", {"center": v(482.6, -228.6) * mm, "radius": 3.3 * mm});
            skCircle(sketch, "E2.41.32.0", {"center": v(482.6, -254) * mm, "radius": 3.3 * mm});
            skCircle(sketch, "E2.41.33.0", {"center": v(482.6, -279.4) * mm, "radius": 3.3 * mm});
            skCircle(sketch, "E2.41.34.0", {"center": v(482.6, -304.8) * mm, "radius": 3.3 * mm});
            skCircle(sketch, "E2.41.35.0", {"center": v(482.6, -330.2) * mm, "radius": 3.3 * mm});
            skCircle(sketch, "E2.41.36.0", {"center": v(482.6, -355.6) * mm, "radius": 3.3 * mm});
            skCircle(sketch, "E2.41.37.0", {"center": v(482.6, -381) * mm, "radius": 3.3 * mm});
            skCircle(sketch, "E2.41.38.0", {"center": v(482.6, -406.4) * mm, "radius": 3.3 * mm});
            skCircle(sketch, "E2.41.39.0", {"center": v(482.6, -431.8) * mm, "radius": 3.3 * mm});
            skCircle(sketch, "E2.41.40.0", {"center": v(482.6, -457.2) * mm, "radius": 3.3 * mm});
            skCircle(sketch, "E2.41.41.0", {"center": v(482.6, -482.6) * mm, "radius": 3.3 * mm});
            skCircle(sketch, "E2.41.42.0", {"center": v(482.6, -508) * mm, "radius": 3.3 * mm});
            skCircle(sketch, "E2.41.43.0", {"center": v(482.6, -533.4) * mm, "radius": 3.3 * mm});
            skCircle(sketch, "E2.41.44.0", {"center": v(482.6, -558.8) * mm, "radius": 3.3 * mm});
            skCircle(sketch, "E2.42.0.0", {"center": v(508, 558.8) * mm, "radius": 3.3 * mm});
            skCircle(sketch, "E2.42.1.0", {"center": v(508, 533.4) * mm, "radius": 3.3 * mm});
            skCircle(sketch, "E2.42.2.0", {"center": v(508, 508) * mm, "radius": 3.3 * mm});
            skCircle(sketch, "E2.42.3.0", {"center": v(508, 482.6) * mm, "radius": 3.3 * mm});
            skCircle(sketch, "E2.42.4.0", {"center": v(508, 457.2) * mm, "radius": 3.3 * mm});
            skCircle(sketch, "E2.42.5.0", {"center": v(508, 431.8) * mm, "radius": 3.3 * mm});
            skCircle(sketch, "E2.42.6.0", {"center": v(508, 406.4) * mm, "radius": 3.3 * mm});
            skCircle(sketch, "E2.42.7.0", {"center": v(508, 381) * mm, "radius": 3.3 * mm});
            skCircle(sketch, "E2.42.8.0", {"center": v(508, 355.6) * mm, "radius": 3.3 * mm});
            skCircle(sketch, "E2.42.9.0", {"center": v(508, 330.2) * mm, "radius": 3.3 * mm});
            skCircle(sketch, "E2.42.10.0", {"center": v(508, 304.8) * mm, "radius": 3.3 * mm});
            skCircle(sketch, "E2.42.11.0", {"center": v(508, 279.4) * mm, "radius": 3.3 * mm});
            skCircle(sketch, "E2.42.12.0", {"center": v(508, 254) * mm, "radius": 3.3 * mm});
            skCircle(sketch, "E2.42.13.0", {"center": v(508, 228.6) * mm, "radius": 3.3 * mm});
            skCircle(sketch, "E2.42.14.0", {"center": v(508, 203.2) * mm, "radius": 3.3 * mm});
            skCircle(sketch, "E2.42.15.0", {"center": v(508, 177.8) * mm, "radius": 3.3 * mm});
            skCircle(sketch, "E2.42.16.0", {"center": v(508, 152.4) * mm, "radius": 3.3 * mm});
            skCircle(sketch, "E2.42.17.0", {"center": v(508, 127) * mm, "radius": 3.3 * mm});
            skCircle(sketch, "E2.42.18.0", {"center": v(508, 101.6) * mm, "radius": 3.3 * mm});
            skCircle(sketch, "E2.42.19.0", {"center": v(508, 76.2) * mm, "radius": 3.3 * mm});
            skCircle(sketch, "E2.42.20.0", {"center": v(508, 50.8) * mm, "radius": 3.3 * mm});
            skCircle(sketch, "E2.42.21.0", {"center": v(508, 25.4) * mm, "radius": 3.3 * mm});
            skCircle(sketch, "E2.42.22.0", {"center": v(508, 0) * mm, "radius": 3.3 * mm});
            skCircle(sketch, "E2.42.23.0", {"center": v(508, -25.4) * mm, "radius": 3.3 * mm});
            skCircle(sketch, "E2.42.24.0", {"center": v(508, -50.8) * mm, "radius": 3.3 * mm});
            skCircle(sketch, "E2.42.25.0", {"center": v(508, -76.2) * mm, "radius": 3.3 * mm});
            skCircle(sketch, "E2.42.26.0", {"center": v(508, -101.6) * mm, "radius": 3.3 * mm});
            skCircle(sketch, "E2.42.27.0", {"center": v(508, -127) * mm, "radius": 3.3 * mm});
            skCircle(sketch, "E2.42.28.0", {"center": v(508, -152.4) * mm, "radius": 3.3 * mm});
            skCircle(sketch, "E2.42.29.0", {"center": v(508, -177.8) * mm, "radius": 3.3 * mm});
            skCircle(sketch, "E2.42.30.0", {"center": v(508, -203.2) * mm, "radius": 3.3 * mm});
            skCircle(sketch, "E2.42.31.0", {"center": v(508, -228.6) * mm, "radius": 3.3 * mm});
            skCircle(sketch, "E2.42.32.0", {"center": v(508, -254) * mm, "radius": 3.3 * mm});
            skCircle(sketch, "E2.42.33.0", {"center": v(508, -279.4) * mm, "radius": 3.3 * mm});
            skCircle(sketch, "E2.42.34.0", {"center": v(508, -304.8) * mm, "radius": 3.3 * mm});
            skCircle(sketch, "E2.42.35.0", {"center": v(508, -330.2) * mm, "radius": 3.3 * mm});
            skCircle(sketch, "E2.42.36.0", {"center": v(508, -355.6) * mm, "radius": 3.3 * mm});
            skCircle(sketch, "E2.42.37.0", {"center": v(508, -381) * mm, "radius": 3.3 * mm});
            skCircle(sketch, "E2.42.38.0", {"center": v(508, -406.4) * mm, "radius": 3.3 * mm});
            skCircle(sketch, "E2.42.39.0", {"center": v(508, -431.8) * mm, "radius": 3.3 * mm});
            skCircle(sketch, "E2.42.40.0", {"center": v(508, -457.2) * mm, "radius": 3.3 * mm});
            skCircle(sketch, "E2.42.41.0", {"center": v(508, -482.6) * mm, "radius": 3.3 * mm});
            skCircle(sketch, "E2.42.42.0", {"center": v(508, -508) * mm, "radius": 3.3 * mm});
            skCircle(sketch, "E2.42.43.0", {"center": v(508, -533.4) * mm, "radius": 3.3 * mm});
            skCircle(sketch, "E2.42.44.0", {"center": v(508, -558.8) * mm, "radius": 3.3 * mm});
            skCircle(sketch, "E2.43.0.0", {"center": v(533.4, 558.8) * mm, "radius": 3.3 * mm});
            skCircle(sketch, "E2.43.1.0", {"center": v(533.4, 533.4) * mm, "radius": 3.3 * mm});
            skCircle(sketch, "E2.43.2.0", {"center": v(533.4, 508) * mm, "radius": 3.3 * mm});
            skCircle(sketch, "E2.43.3.0", {"center": v(533.4, 482.6) * mm, "radius": 3.3 * mm});
            skCircle(sketch, "E2.43.4.0", {"center": v(533.4, 457.2) * mm, "radius": 3.3 * mm});
            skCircle(sketch, "E2.43.5.0", {"center": v(533.4, 431.8) * mm, "radius": 3.3 * mm});
            skCircle(sketch, "E2.43.6.0", {"center": v(533.4, 406.4) * mm, "radius": 3.3 * mm});
            skCircle(sketch, "E2.43.7.0", {"center": v(533.4, 381) * mm, "radius": 3.3 * mm});
            skCircle(sketch, "E2.43.8.0", {"center": v(533.4, 355.6) * mm, "radius": 3.3 * mm});
            skCircle(sketch, "E2.43.9.0", {"center": v(533.4, 330.2) * mm, "radius": 3.3 * mm});
            skCircle(sketch, "E2.43.10.0", {"center": v(533.4, 304.8) * mm, "radius": 3.3 * mm});
            skCircle(sketch, "E2.43.11.0", {"center": v(533.4, 279.4) * mm, "radius": 3.3 * mm});
            skCircle(sketch, "E2.43.12.0", {"center": v(533.4, 254) * mm, "radius": 3.3 * mm});
            skCircle(sketch, "E2.43.13.0", {"center": v(533.4, 228.6) * mm, "radius": 3.3 * mm});
            skCircle(sketch, "E2.43.14.0", {"center": v(533.4, 203.2) * mm, "radius": 3.3 * mm});
            skCircle(sketch, "E2.43.15.0", {"center": v(533.4, 177.8) * mm, "radius": 3.3 * mm});
            skCircle(sketch, "E2.43.16.0", {"center": v(533.4, 152.4) * mm, "radius": 3.3 * mm});
            skCircle(sketch, "E2.43.17.0", {"center": v(533.4, 127) * mm, "radius": 3.3 * mm});
            skCircle(sketch, "E2.43.18.0", {"center": v(533.4, 101.6) * mm, "radius": 3.3 * mm});
            skCircle(sketch, "E2.43.19.0", {"center": v(533.4, 76.2) * mm, "radius": 3.3 * mm});
            skCircle(sketch, "E2.43.20.0", {"center": v(533.4, 50.8) * mm, "radius": 3.3 * mm});
            skCircle(sketch, "E2.43.21.0", {"center": v(533.4, 25.4) * mm, "radius": 3.3 * mm});
            skCircle(sketch, "E2.43.22.0", {"center": v(533.4, 0) * mm, "radius": 3.3 * mm});
            skCircle(sketch, "E2.43.23.0", {"center": v(533.4, -25.4) * mm, "radius": 3.3 * mm});
            skCircle(sketch, "E2.43.24.0", {"center": v(533.4, -50.8) * mm, "radius": 3.3 * mm});
            skCircle(sketch, "E2.43.25.0", {"center": v(533.4, -76.2) * mm, "radius": 3.3 * mm});
            skCircle(sketch, "E2.43.26.0", {"center": v(533.4, -101.6) * mm, "radius": 3.3 * mm});
            skCircle(sketch, "E2.43.27.0", {"center": v(533.4, -127) * mm, "radius": 3.3 * mm});
            skCircle(sketch, "E2.43.28.0", {"center": v(533.4, -152.4) * mm, "radius": 3.3 * mm});
            skCircle(sketch, "E2.43.29.0", {"center": v(533.4, -177.8) * mm, "radius": 3.3 * mm});
            skCircle(sketch, "E2.43.30.0", {"center": v(533.4, -203.2) * mm, "radius": 3.3 * mm});
            skCircle(sketch, "E2.43.31.0", {"center": v(533.4, -228.6) * mm, "radius": 3.3 * mm});
            skCircle(sketch, "E2.43.32.0", {"center": v(533.4, -254) * mm, "radius": 3.3 * mm});
            skCircle(sketch, "E2.43.33.0", {"center": v(533.4, -279.4) * mm, "radius": 3.3 * mm});
            skCircle(sketch, "E2.43.34.0", {"center": v(533.4, -304.8) * mm, "radius": 3.3 * mm});
            skCircle(sketch, "E2.43.35.0", {"center": v(533.4, -330.2) * mm, "radius": 3.3 * mm});
            skCircle(sketch, "E2.43.36.0", {"center": v(533.4, -355.6) * mm, "radius": 3.3 * mm});
            skCircle(sketch, "E2.43.37.0", {"center": v(533.4, -381) * mm, "radius": 3.3 * mm});
            skCircle(sketch, "E2.43.38.0", {"center": v(533.4, -406.4) * mm, "radius": 3.3 * mm});
            skCircle(sketch, "E2.43.39.0", {"center": v(533.4, -431.8) * mm, "radius": 3.3 * mm});
            skCircle(sketch, "E2.43.40.0", {"center": v(533.4, -457.2) * mm, "radius": 3.3 * mm});
            skCircle(sketch, "E2.43.41.0", {"center": v(533.4, -482.6) * mm, "radius": 3.3 * mm});
            skCircle(sketch, "E2.43.42.0", {"center": v(533.4, -508) * mm, "radius": 3.3 * mm});
            skCircle(sketch, "E2.43.43.0", {"center": v(533.4, -533.4) * mm, "radius": 3.3 * mm});
            skCircle(sketch, "E2.43.44.0", {"center": v(533.4, -558.8) * mm, "radius": 3.3 * mm});
            skCircle(sketch, "E2.44.0.0", {"center": v(558.8, 558.8) * mm, "radius": 3.3 * mm});
            skCircle(sketch, "E2.44.1.0", {"center": v(558.8, 533.4) * mm, "radius": 3.3 * mm});
            skCircle(sketch, "E2.44.2.0", {"center": v(558.8, 508) * mm, "radius": 3.3 * mm});
            skCircle(sketch, "E2.44.3.0", {"center": v(558.8, 482.6) * mm, "radius": 3.3 * mm});
            skCircle(sketch, "E2.44.4.0", {"center": v(558.8, 457.2) * mm, "radius": 3.3 * mm});
            skCircle(sketch, "E2.44.5.0", {"center": v(558.8, 431.8) * mm, "radius": 3.3 * mm});
            skCircle(sketch, "E2.44.6.0", {"center": v(558.8, 406.4) * mm, "radius": 3.3 * mm});
            skCircle(sketch, "E2.44.7.0", {"center": v(558.8, 381) * mm, "radius": 3.3 * mm});
            skCircle(sketch, "E2.44.8.0", {"center": v(558.8, 355.6) * mm, "radius": 3.3 * mm});
            skCircle(sketch, "E2.44.9.0", {"center": v(558.8, 330.2) * mm, "radius": 3.3 * mm});
            skCircle(sketch, "E2.44.10.0", {"center": v(558.8, 304.8) * mm, "radius": 3.3 * mm});
            skCircle(sketch, "E2.44.11.0", {"center": v(558.8, 279.4) * mm, "radius": 3.3 * mm});
            skCircle(sketch, "E2.44.12.0", {"center": v(558.8, 254) * mm, "radius": 3.3 * mm});
            skCircle(sketch, "E2.44.13.0", {"center": v(558.8, 228.6) * mm, "radius": 3.3 * mm});
            skCircle(sketch, "E2.44.14.0", {"center": v(558.8, 203.2) * mm, "radius": 3.3 * mm});
            skCircle(sketch, "E2.44.15.0", {"center": v(558.8, 177.8) * mm, "radius": 3.3 * mm});
            skCircle(sketch, "E2.44.16.0", {"center": v(558.8, 152.4) * mm, "radius": 3.3 * mm});
            skCircle(sketch, "E2.44.17.0", {"center": v(558.8, 127) * mm, "radius": 3.3 * mm});
            skCircle(sketch, "E2.44.18.0", {"center": v(558.8, 101.6) * mm, "radius": 3.3 * mm});
            skCircle(sketch, "E2.44.19.0", {"center": v(558.8, 76.2) * mm, "radius": 3.3 * mm});
            skCircle(sketch, "E2.44.20.0", {"center": v(558.8, 50.8) * mm, "radius": 3.3 * mm});
            skCircle(sketch, "E2.44.21.0", {"center": v(558.8, 25.4) * mm, "radius": 3.3 * mm});
            skCircle(sketch, "E2.44.22.0", {"center": v(558.8, 0) * mm, "radius": 3.3 * mm});
            skCircle(sketch, "E2.44.23.0", {"center": v(558.8, -25.4) * mm, "radius": 3.3 * mm});
            skCircle(sketch, "E2.44.24.0", {"center": v(558.8, -50.8) * mm, "radius": 3.3 * mm});
            skCircle(sketch, "E2.44.25.0", {"center": v(558.8, -76.2) * mm, "radius": 3.3 * mm});
            skCircle(sketch, "E2.44.26.0", {"center": v(558.8, -101.6) * mm, "radius": 3.3 * mm});
            skCircle(sketch, "E2.44.27.0", {"center": v(558.8, -127) * mm, "radius": 3.3 * mm});
            skCircle(sketch, "E2.44.28.0", {"center": v(558.8, -152.4) * mm, "radius": 3.3 * mm});
            skCircle(sketch, "E2.44.29.0", {"center": v(558.8, -177.8) * mm, "radius": 3.3 * mm});
            skCircle(sketch, "E2.44.30.0", {"center": v(558.8, -203.2) * mm, "radius": 3.3 * mm});
            skCircle(sketch, "E2.44.31.0", {"center": v(558.8, -228.6) * mm, "radius": 3.3 * mm});
            skCircle(sketch, "E2.44.32.0", {"center": v(558.8, -254) * mm, "radius": 3.3 * mm});
            skCircle(sketch, "E2.44.33.0", {"center": v(558.8, -279.4) * mm, "radius": 3.3 * mm});
            skCircle(sketch, "E2.44.34.0", {"center": v(558.8, -304.8) * mm, "radius": 3.3 * mm});
            skCircle(sketch, "E2.44.35.0", {"center": v(558.8, -330.2) * mm, "radius": 3.3 * mm});
            skCircle(sketch, "E2.44.36.0", {"center": v(558.8, -355.6) * mm, "radius": 3.3 * mm});
            skCircle(sketch, "E2.44.37.0", {"center": v(558.8, -381) * mm, "radius": 3.3 * mm});
            skCircle(sketch, "E2.44.38.0", {"center": v(558.8, -406.4) * mm, "radius": 3.3 * mm});
            skCircle(sketch, "E2.44.39.0", {"center": v(558.8, -431.8) * mm, "radius": 3.3 * mm});
            skCircle(sketch, "E2.44.40.0", {"center": v(558.8, -457.2) * mm, "radius": 3.3 * mm});
            skCircle(sketch, "E2.44.41.0", {"center": v(558.8, -482.6) * mm, "radius": 3.3 * mm});
            skCircle(sketch, "E2.44.42.0", {"center": v(558.8, -508) * mm, "radius": 3.3 * mm});
            skCircle(sketch, "E2.44.43.0", {"center": v(558.8, -533.4) * mm, "radius": 3.3 * mm});
            skCircle(sketch, "E2.44.44.0", {"center": v(558.8, -558.8) * mm, "radius": 3.3 * mm});
            skLineSegment(sketch, "E2.direction1", {"start": v(-558.8, 558.8) * mm, "end": v(-533.4, 558.8) * mm, "construction": true});
            skLineSegment(sketch, "E2.direction2", {"start": v(-558.8, 558.8) * mm, "end": v(-558.8, 533.4) * mm, "construction": true});
            skSolve(sketch);
        }
        {
            var Q0;
            Q0 = qSketchRegion(id + "F0", true);
            extrude(context, id + "F1", {"entities" : qUnion([Q0]), "oppositeDirection" : true, "depth" : 12.7 * mm, "offsetDistance" : 25.4 * mm});
        }
        {
            var Q0;
            Q0=makeQuery(id+"F1.opExtrude","CAP_FACE",FACE,{"disambiguationData":[OSD([sQuery(id+"F0.wireOp",EDGE,"E0.bottom"),sQuery(id+"F0.wireOp",EDGE,"E0.top"),sQuery(id+"F0.wireOp",EDGE,"E0.left"),sQuery(id+"F0.wireOp",EDGE,"E0.right"),sQuery(id+"F0.wireOp",EDGE,"E1"),sQuery(id+"F0.wireOp",EDGE,"E2.0.1.0"),sQuery(id+"F0.wireOp",EDGE,"E2.0.2.0"),sQuery(id+"F0.wireOp",EDGE,"E2.0.3.0"),sQuery(id+"F0.wireOp",EDGE,"E2.0.4.0"),sQuery(id+"F0.wireOp",EDGE,"E2.0.5.0"),sQuery(id+"F0.wireOp",EDGE,"E2.0.6.0"),sQuery(id+"F0.wireOp",EDGE,"E2.0.7.0"),sQuery(id+"F0.wireOp",EDGE,"E2.0.8.0"),sQuery(id+"F0.wireOp",EDGE,"E2.0.9.0"),sQuery(id+"F0.wireOp",EDGE,"E2.0.10.0"),sQuery(id+"F0.wireOp",EDGE,"E2.0.11.0"),sQuery(id+"F0.wireOp",EDGE,"E2.0.12.0"),sQuery(id+"F0.wireOp",EDGE,"E2.0.13.0"),sQuery(id+"F0.wireOp",EDGE,"E2.0.14.0"),sQuery(id+"F0.wireOp",EDGE,"E2.0.15.0"),sQuery(id+"F0.wireOp",EDGE,"E2.0.16.0"),sQuery(id+"F0.wireOp",EDGE,"E2.0.17.0"),sQuery(id+"F0.wireOp",EDGE,"E2.0.18.0"),sQuery(id+"F0.wireOp",EDGE,"E2.0.19.0"),sQuery(id+"F0.wireOp",EDGE,"E2.0.20.0"),sQuery(id+"F0.wireOp",EDGE,"E2.0.21.0"),sQuery(id+"F0.wireOp",EDGE,"E2.0.22.0"),sQuery(id+"F0.wireOp",EDGE,"E2.0.23.0"),sQuery(id+"F0.wireOp",EDGE,"E2.0.24.0"),sQuery(id+"F0.wireOp",EDGE,"E2.0.25.0"),sQuery(id+"F0.wireOp",EDGE,"E2.0.26.0"),sQuery(id+"F0.wireOp",EDGE,"E2.0.27.0"),sQuery(id+"F0.wireOp",EDGE,"E2.0.28.0"),sQuery(id+"F0.wireOp",EDGE,"E2.0.29.0"),sQuery(id+"F0.wireOp",EDGE,"E2.0.30.0"),sQuery(id+"F0.wireOp",EDGE,"E2.0.31.0"),sQuery(id+"F0.wireOp",EDGE,"E2.0.32.0"),sQuery(id+"F0.wireOp",EDGE,"E2.0.33.0"),sQuery(id+"F0.wireOp",EDGE,"E2.0.34.0"),sQuery(id+"F0.wireOp",EDGE,"E2.0.35.0"),sQuery(id+"F0.wireOp",EDGE,"E2.0.36.0"),sQuery(id+"F0.wireOp",EDGE,"E2.0.37.0"),sQuery(id+"F0.wireOp",EDGE,"E2.0.38.0"),sQuery(id+"F0.wireOp",EDGE,"E2.0.39.0"),sQuery(id+"F0.wireOp",EDGE,"E2.0.40.0"),sQuery(id+"F0.wireOp",EDGE,"E2.0.41.0"),sQuery(id+"F0.wireOp",EDGE,"E2.0.42.0"),sQuery(id+"F0.wireOp",EDGE,"E2.0.43.0"),sQuery(id+"F0.wireOp",EDGE,"E2.0.44.0"),sQuery(id+"F0.wireOp",EDGE,"E2.1.0.0"),sQuery(id+"F0.wireOp",EDGE,"E2.1.1.0"),sQuery(id+"F0.wireOp",EDGE,"E2.1.2.0"),sQuery(id+"F0.wireOp",EDGE,"E2.1.3.0"),sQuery(id+"F0.wireOp",EDGE,"E2.1.4.0"),sQuery(id+"F0.wireOp",EDGE,"E2.1.5.0"),sQuery(id+"F0.wireOp",EDGE,"E2.1.6.0"),sQuery(id+"F0.wireOp",EDGE,"E2.1.7.0"),sQuery(id+"F0.wireOp",EDGE,"E2.1.8.0"),sQuery(id+"F0.wireOp",EDGE,"E2.1.9.0"),sQuery(id+"F0.wireOp",EDGE,"E2.1.10.0"),sQuery(id+"F0.wireOp",EDGE,"E2.1.11.0"),sQuery(id+"F0.wireOp",EDGE,"E2.1.12.0"),sQuery(id+"F0.wireOp",EDGE,"E2.1.13.0"),sQuery(id+"F0.wireOp",EDGE,"E2.1.14.0"),sQuery(id+"F0.wireOp",EDGE,"E2.1.15.0"),sQuery(id+"F0.wireOp",EDGE,"E2.1.16.0"),sQuery(id+"F0.wireOp",EDGE,"E2.1.17.0"),sQuery(id+"F0.wireOp",EDGE,"E2.1.18.0"),sQuery(id+"F0.wireOp",EDGE,"E2.1.19.0"),sQuery(id+"F0.wireOp",EDGE,"E2.1.20.0"),sQuery(id+"F0.wireOp",EDGE,"E2.1.21.0"),sQuery(id+"F0.wireOp",EDGE,"E2.1.22.0"),sQuery(id+"F0.wireOp",EDGE,"E2.1.23.0"),sQuery(id+"F0.wireOp",EDGE,"E2.1.24.0"),sQuery(id+"F0.wireOp",EDGE,"E2.1.25.0"),sQuery(id+"F0.wireOp",EDGE,"E2.1.26.0"),sQuery(id+"F0.wireOp",EDGE,"E2.1.27.0"),sQuery(id+"F0.wireOp",EDGE,"E2.1.28.0"),sQuery(id+"F0.wireOp",EDGE,"E2.1.29.0"),sQuery(id+"F0.wireOp",EDGE,"E2.1.30.0"),sQuery(id+"F0.wireOp",EDGE,"E2.1.31.0"),sQuery(id+"F0.wireOp",EDGE,"E2.1.32.0"),sQuery(id+"F0.wireOp",EDGE,"E2.1.33.0"),sQuery(id+"F0.wireOp",EDGE,"E2.1.34.0"),sQuery(id+"F0.wireOp",EDGE,"E2.1.35.0"),sQuery(id+"F0.wireOp",EDGE,"E2.1.36.0"),sQuery(id+"F0.wireOp",EDGE,"E2.1.37.0"),sQuery(id+"F0.wireOp",EDGE,"E2.1.38.0"),sQuery(id+"F0.wireOp",EDGE,"E2.1.39.0"),sQuery(id+"F0.wireOp",EDGE,"E2.1.40.0"),sQuery(id+"F0.wireOp",EDGE,"E2.1.41.0"),sQuery(id+"F0.wireOp",EDGE,"E2.1.42.0"),sQuery(id+"F0.wireOp",EDGE,"E2.1.43.0"),sQuery(id+"F0.wireOp",EDGE,"E2.1.44.0"),sQuery(id+"F0.wireOp",EDGE,"E2.2.0.0"),sQuery(id+"F0.wireOp",EDGE,"E2.2.1.0"),sQuery(id+"F0.wireOp",EDGE,"E2.2.2.0"),sQuery(id+"F0.wireOp",EDGE,"E2.2.3.0"),sQuery(id+"F0.wireOp",EDGE,"E2.2.4.0"),sQuery(id+"F0.wireOp",EDGE,"E2.2.5.0"),sQuery(id+"F0.wireOp",EDGE,"E2.2.6.0"),sQuery(id+"F0.wireOp",EDGE,"E2.2.7.0"),sQuery(id+"F0.wireOp",EDGE,"E2.2.8.0"),sQuery(id+"F0.wireOp",EDGE,"E2.2.9.0"),sQuery(id+"F0.wireOp",EDGE,"E2.2.10.0"),sQuery(id+"F0.wireOp",EDGE,"E2.2.11.0"),sQuery(id+"F0.wireOp",EDGE,"E2.2.12.0"),sQuery(id+"F0.wireOp",EDGE,"E2.2.13.0"),sQuery(id+"F0.wireOp",EDGE,"E2.2.14.0"),sQuery(id+"F0.wireOp",EDGE,"E2.2.15.0"),sQuery(id+"F0.wireOp",EDGE,"E2.2.16.0"),sQuery(id+"F0.wireOp",EDGE,"E2.2.17.0"),sQuery(id+"F0.wireOp",EDGE,"E2.2.18.0"),sQuery(id+"F0.wireOp",EDGE,"E2.2.19.0"),sQuery(id+"F0.wireOp",EDGE,"E2.2.20.0"),sQuery(id+"F0.wireOp",EDGE,"E2.2.21.0"),sQuery(id+"F0.wireOp",EDGE,"E2.2.22.0"),sQuery(id+"F0.wireOp",EDGE,"E2.2.23.0"),sQuery(id+"F0.wireOp",EDGE,"E2.2.24.0"),sQuery(id+"F0.wireOp",EDGE,"E2.2.25.0"),sQuery(id+"F0.wireOp",EDGE,"E2.2.26.0"),sQuery(id+"F0.wireOp",EDGE,"E2.2.27.0"),sQuery(id+"F0.wireOp",EDGE,"E2.2.28.0"),sQuery(id+"F0.wireOp",EDGE,"E2.2.29.0"),sQuery(id+"F0.wireOp",EDGE,"E2.2.30.0"),sQuery(id+"F0.wireOp",EDGE,"E2.2.31.0"),sQuery(id+"F0.wireOp",EDGE,"E2.2.32.0"),sQuery(id+"F0.wireOp",EDGE,"E2.2.33.0"),sQuery(id+"F0.wireOp",EDGE,"E2.2.34.0"),sQuery(id+"F0.wireOp",EDGE,"E2.2.35.0"),sQuery(id+"F0.wireOp",EDGE,"E2.2.36.0"),sQuery(id+"F0.wireOp",EDGE,"E2.2.37.0"),sQuery(id+"F0.wireOp",EDGE,"E2.2.38.0"),sQuery(id+"F0.wireOp",EDGE,"E2.2.39.0"),sQuery(id+"F0.wireOp",EDGE,"E2.2.40.0"),sQuery(id+"F0.wireOp",EDGE,"E2.2.41.0"),sQuery(id+"F0.wireOp",EDGE,"E2.2.42.0"),sQuery(id+"F0.wireOp",EDGE,"E2.2.43.0"),sQuery(id+"F0.wireOp",EDGE,"E2.2.44.0"),sQuery(id+"F0.wireOp",EDGE,"E2.3.0.0"),sQuery(id+"F0.wireOp",EDGE,"E2.3.1.0"),sQuery(id+"F0.wireOp",EDGE,"E2.3.2.0"),sQuery(id+"F0.wireOp",EDGE,"E2.3.3.0"),sQuery(id+"F0.wireOp",EDGE,"E2.3.4.0"),sQuery(id+"F0.wireOp",EDGE,"E2.3.5.0"),sQuery(id+"F0.wireOp",EDGE,"E2.3.6.0"),sQuery(id+"F0.wireOp",EDGE,"E2.3.7.0"),sQuery(id+"F0.wireOp",EDGE,"E2.3.8.0"),sQuery(id+"F0.wireOp",EDGE,"E2.3.9.0"),sQuery(id+"F0.wireOp",EDGE,"E2.3.10.0"),sQuery(id+"F0.wireOp",EDGE,"E2.3.11.0"),sQuery(id+"F0.wireOp",EDGE,"E2.3.12.0"),sQuery(id+"F0.wireOp",EDGE,"E2.3.13.0"),sQuery(id+"F0.wireOp",EDGE,"E2.3.14.0"),sQuery(id+"F0.wireOp",EDGE,"E2.3.15.0"),sQuery(id+"F0.wireOp",EDGE,"E2.3.16.0"),sQuery(id+"F0.wireOp",EDGE,"E2.3.17.0"),sQuery(id+"F0.wireOp",EDGE,"E2.3.18.0"),sQuery(id+"F0.wireOp",EDGE,"E2.3.19.0"),sQuery(id+"F0.wireOp",EDGE,"E2.3.20.0"),sQuery(id+"F0.wireOp",EDGE,"E2.3.21.0"),sQuery(id+"F0.wireOp",EDGE,"E2.3.22.0"),sQuery(id+"F0.wireOp",EDGE,"E2.3.23.0"),sQuery(id+"F0.wireOp",EDGE,"E2.3.24.0"),sQuery(id+"F0.wireOp",EDGE,"E2.3.25.0"),sQuery(id+"F0.wireOp",EDGE,"E2.3.26.0"),sQuery(id+"F0.wireOp",EDGE,"E2.3.27.0"),sQuery(id+"F0.wireOp",EDGE,"E2.3.28.0"),sQuery(id+"F0.wireOp",EDGE,"E2.3.29.0"),sQuery(id+"F0.wireOp",EDGE,"E2.3.30.0"),sQuery(id+"F0.wireOp",EDGE,"E2.3.31.0"),sQuery(id+"F0.wireOp",EDGE,"E2.3.32.0"),sQuery(id+"F0.wireOp",EDGE,"E2.3.33.0"),sQuery(id+"F0.wireOp",EDGE,"E2.3.34.0"),sQuery(id+"F0.wireOp",EDGE,"E2.3.35.0"),sQuery(id+"F0.wireOp",EDGE,"E2.3.36.0"),sQuery(id+"F0.wireOp",EDGE,"E2.3.37.0"),sQuery(id+"F0.wireOp",EDGE,"E2.3.38.0"),sQuery(id+"F0.wireOp",EDGE,"E2.3.39.0"),sQuery(id+"F0.wireOp",EDGE,"E2.3.40.0"),sQuery(id+"F0.wireOp",EDGE,"E2.3.41.0"),sQuery(id+"F0.wireOp",EDGE,"E2.3.42.0"),sQuery(id+"F0.wireOp",EDGE,"E2.3.43.0"),sQuery(id+"F0.wireOp",EDGE,"E2.3.44.0"),sQuery(id+"F0.wireOp",EDGE,"E2.4.0.0"),sQuery(id+"F0.wireOp",EDGE,"E2.4.1.0"),sQuery(id+"F0.wireOp",EDGE,"E2.4.2.0"),sQuery(id+"F0.wireOp",EDGE,"E2.4.3.0"),sQuery(id+"F0.wireOp",EDGE,"E2.4.4.0"),sQuery(id+"F0.wireOp",EDGE,"E2.4.5.0"),sQuery(id+"F0.wireOp",EDGE,"E2.4.6.0"),sQuery(id+"F0.wireOp",EDGE,"E2.4.7.0"),sQuery(id+"F0.wireOp",EDGE,"E2.4.8.0"),sQuery(id+"F0.wireOp",EDGE,"E2.4.9.0"),sQuery(id+"F0.wireOp",EDGE,"E2.4.10.0"),sQuery(id+"F0.wireOp",EDGE,"E2.4.11.0"),sQuery(id+"F0.wireOp",EDGE,"E2.4.12.0"),sQuery(id+"F0.wireOp",EDGE,"E2.4.13.0"),sQuery(id+"F0.wireOp",EDGE,"E2.4.14.0"),sQuery(id+"F0.wireOp",EDGE,"E2.4.15.0"),sQuery(id+"F0.wireOp",EDGE,"E2.4.16.0"),sQuery(id+"F0.wireOp",EDGE,"E2.4.17.0"),sQuery(id+"F0.wireOp",EDGE,"E2.4.18.0"),sQuery(id+"F0.wireOp",EDGE,"E2.4.19.0"),sQuery(id+"F0.wireOp",EDGE,"E2.4.20.0"),sQuery(id+"F0.wireOp",EDGE,"E2.4.21.0"),sQuery(id+"F0.wireOp",EDGE,"E2.4.22.0"),sQuery(id+"F0.wireOp",EDGE,"E2.4.23.0"),sQuery(id+"F0.wireOp",EDGE,"E2.4.24.0"),sQuery(id+"F0.wireOp",EDGE,"E2.4.25.0"),sQuery(id+"F0.wireOp",EDGE,"E2.4.26.0"),sQuery(id+"F0.wireOp",EDGE,"E2.4.27.0"),sQuery(id+"F0.wireOp",EDGE,"E2.4.28.0"),sQuery(id+"F0.wireOp",EDGE,"E2.4.29.0"),sQuery(id+"F0.wireOp",EDGE,"E2.4.30.0"),sQuery(id+"F0.wireOp",EDGE,"E2.4.31.0"),sQuery(id+"F0.wireOp",EDGE,"E2.4.32.0"),sQuery(id+"F0.wireOp",EDGE,"E2.4.33.0"),sQuery(id+"F0.wireOp",EDGE,"E2.4.34.0"),sQuery(id+"F0.wireOp",EDGE,"E2.4.35.0"),sQuery(id+"F0.wireOp",EDGE,"E2.4.36.0"),sQuery(id+"F0.wireOp",EDGE,"E2.4.37.0"),sQuery(id+"F0.wireOp",EDGE,"E2.4.38.0"),sQuery(id+"F0.wireOp",EDGE,"E2.4.39.0"),sQuery(id+"F0.wireOp",EDGE,"E2.4.40.0"),sQuery(id+"F0.wireOp",EDGE,"E2.4.41.0"),sQuery(id+"F0.wireOp",EDGE,"E2.4.42.0"),sQuery(id+"F0.wireOp",EDGE,"E2.4.43.0"),sQuery(id+"F0.wireOp",EDGE,"E2.4.44.0"),sQuery(id+"F0.wireOp",EDGE,"E2.5.0.0"),sQuery(id+"F0.wireOp",EDGE,"E2.5.1.0"),sQuery(id+"F0.wireOp",EDGE,"E2.5.2.0"),sQuery(id+"F0.wireOp",EDGE,"E2.5.3.0"),sQuery(id+"F0.wireOp",EDGE,"E2.5.4.0"),sQuery(id+"F0.wireOp",EDGE,"E2.5.5.0"),sQuery(id+"F0.wireOp",EDGE,"E2.5.6.0"),sQuery(id+"F0.wireOp",EDGE,"E2.5.7.0"),sQuery(id+"F0.wireOp",EDGE,"E2.5.8.0"),sQuery(id+"F0.wireOp",EDGE,"E2.5.9.0"),sQuery(id+"F0.wireOp",EDGE,"E2.5.10.0"),sQuery(id+"F0.wireOp",EDGE,"E2.5.11.0"),sQuery(id+"F0.wireOp",EDGE,"E2.5.12.0"),sQuery(id+"F0.wireOp",EDGE,"E2.5.13.0"),sQuery(id+"F0.wireOp",EDGE,"E2.5.14.0"),sQuery(id+"F0.wireOp",EDGE,"E2.5.15.0"),sQuery(id+"F0.wireOp",EDGE,"E2.5.16.0"),sQuery(id+"F0.wireOp",EDGE,"E2.5.17.0"),sQuery(id+"F0.wireOp",EDGE,"E2.5.18.0"),sQuery(id+"F0.wireOp",EDGE,"E2.5.19.0"),sQuery(id+"F0.wireOp",EDGE,"E2.5.20.0"),sQuery(id+"F0.wireOp",EDGE,"E2.5.21.0"),sQuery(id+"F0.wireOp",EDGE,"E2.5.22.0"),sQuery(id+"F0.wireOp",EDGE,"E2.5.23.0"),sQuery(id+"F0.wireOp",EDGE,"E2.5.24.0"),sQuery(id+"F0.wireOp",EDGE,"E2.5.25.0"),sQuery(id+"F0.wireOp",EDGE,"E2.5.26.0"),sQuery(id+"F0.wireOp",EDGE,"E2.5.27.0"),sQuery(id+"F0.wireOp",EDGE,"E2.5.28.0"),sQuery(id+"F0.wireOp",EDGE,"E2.5.29.0"),sQuery(id+"F0.wireOp",EDGE,"E2.5.30.0"),sQuery(id+"F0.wireOp",EDGE,"E2.5.31.0"),sQuery(id+"F0.wireOp",EDGE,"E2.5.32.0"),sQuery(id+"F0.wireOp",EDGE,"E2.5.33.0"),sQuery(id+"F0.wireOp",EDGE,"E2.5.34.0"),sQuery(id+"F0.wireOp",EDGE,"E2.5.35.0"),sQuery(id+"F0.wireOp",EDGE,"E2.5.36.0"),sQuery(id+"F0.wireOp",EDGE,"E2.5.37.0"),sQuery(id+"F0.wireOp",EDGE,"E2.5.38.0"),sQuery(id+"F0.wireOp",EDGE,"E2.5.39.0"),sQuery(id+"F0.wireOp",EDGE,"E2.5.40.0"),sQuery(id+"F0.wireOp",EDGE,"E2.5.41.0"),sQuery(id+"F0.wireOp",EDGE,"E2.5.42.0"),sQuery(id+"F0.wireOp",EDGE,"E2.5.43.0"),sQuery(id+"F0.wireOp",EDGE,"E2.5.44.0"),sQuery(id+"F0.wireOp",EDGE,"E2.6.0.0"),sQuery(id+"F0.wireOp",EDGE,"E2.6.1.0"),sQuery(id+"F0.wireOp",EDGE,"E2.6.2.0"),sQuery(id+"F0.wireOp",EDGE,"E2.6.3.0"),sQuery(id+"F0.wireOp",EDGE,"E2.6.4.0"),sQuery(id+"F0.wireOp",EDGE,"E2.6.5.0"),sQuery(id+"F0.wireOp",EDGE,"E2.6.6.0"),sQuery(id+"F0.wireOp",EDGE,"E2.6.7.0"),sQuery(id+"F0.wireOp",EDGE,"E2.6.8.0"),sQuery(id+"F0.wireOp",EDGE,"E2.6.9.0"),sQuery(id+"F0.wireOp",EDGE,"E2.6.10.0"),sQuery(id+"F0.wireOp",EDGE,"E2.6.11.0"),sQuery(id+"F0.wireOp",EDGE,"E2.6.12.0"),sQuery(id+"F0.wireOp",EDGE,"E2.6.13.0"),sQuery(id+"F0.wireOp",EDGE,"E2.6.14.0"),sQuery(id+"F0.wireOp",EDGE,"E2.6.15.0"),sQuery(id+"F0.wireOp",EDGE,"E2.6.16.0"),sQuery(id+"F0.wireOp",EDGE,"E2.6.17.0"),sQuery(id+"F0.wireOp",EDGE,"E2.6.18.0"),sQuery(id+"F0.wireOp",EDGE,"E2.6.19.0"),sQuery(id+"F0.wireOp",EDGE,"E2.6.20.0"),sQuery(id+"F0.wireOp",EDGE,"E2.6.21.0"),sQuery(id+"F0.wireOp",EDGE,"E2.6.22.0"),sQuery(id+"F0.wireOp",EDGE,"E2.6.23.0"),sQuery(id+"F0.wireOp",EDGE,"E2.6.24.0"),sQuery(id+"F0.wireOp",EDGE,"E2.6.25.0"),sQuery(id+"F0.wireOp",EDGE,"E2.6.26.0"),sQuery(id+"F0.wireOp",EDGE,"E2.6.27.0"),sQuery(id+"F0.wireOp",EDGE,"E2.6.28.0"),sQuery(id+"F0.wireOp",EDGE,"E2.6.29.0"),sQuery(id+"F0.wireOp",EDGE,"E2.6.30.0"),sQuery(id+"F0.wireOp",EDGE,"E2.6.31.0"),sQuery(id+"F0.wireOp",EDGE,"E2.6.32.0"),sQuery(id+"F0.wireOp",EDGE,"E2.6.33.0"),sQuery(id+"F0.wireOp",EDGE,"E2.6.34.0"),sQuery(id+"F0.wireOp",EDGE,"E2.6.35.0"),sQuery(id+"F0.wireOp",EDGE,"E2.6.36.0"),sQuery(id+"F0.wireOp",EDGE,"E2.6.37.0"),sQuery(id+"F0.wireOp",EDGE,"E2.6.38.0"),sQuery(id+"F0.wireOp",EDGE,"E2.6.39.0"),sQuery(id+"F0.wireOp",EDGE,"E2.6.40.0"),sQuery(id+"F0.wireOp",EDGE,"E2.6.41.0"),sQuery(id+"F0.wireOp",EDGE,"E2.6.42.0"),sQuery(id+"F0.wireOp",EDGE,"E2.6.43.0"),sQuery(id+"F0.wireOp",EDGE,"E2.6.44.0"),sQuery(id+"F0.wireOp",EDGE,"E2.7.0.0"),sQuery(id+"F0.wireOp",EDGE,"E2.7.1.0"),sQuery(id+"F0.wireOp",EDGE,"E2.7.2.0"),sQuery(id+"F0.wireOp",EDGE,"E2.7.3.0"),sQuery(id+"F0.wireOp",EDGE,"E2.7.4.0"),sQuery(id+"F0.wireOp",EDGE,"E2.7.5.0"),sQuery(id+"F0.wireOp",EDGE,"E2.7.6.0"),sQuery(id+"F0.wireOp",EDGE,"E2.7.7.0"),sQuery(id+"F0.wireOp",EDGE,"E2.7.8.0"),sQuery(id+"F0.wireOp",EDGE,"E2.7.9.0"),sQuery(id+"F0.wireOp",EDGE,"E2.7.10.0"),sQuery(id+"F0.wireOp",EDGE,"E2.7.11.0"),sQuery(id+"F0.wireOp",EDGE,"E2.7.12.0"),sQuery(id+"F0.wireOp",EDGE,"E2.7.13.0"),sQuery(id+"F0.wireOp",EDGE,"E2.7.14.0"),sQuery(id+"F0.wireOp",EDGE,"E2.7.15.0"),sQuery(id+"F0.wireOp",EDGE,"E2.7.16.0"),sQuery(id+"F0.wireOp",EDGE,"E2.7.17.0"),sQuery(id+"F0.wireOp",EDGE,"E2.7.18.0"),sQuery(id+"F0.wireOp",EDGE,"E2.7.19.0"),sQuery(id+"F0.wireOp",EDGE,"E2.7.20.0"),sQuery(id+"F0.wireOp",EDGE,"E2.7.21.0"),sQuery(id+"F0.wireOp",EDGE,"E2.7.22.0"),sQuery(id+"F0.wireOp",EDGE,"E2.7.23.0"),sQuery(id+"F0.wireOp",EDGE,"E2.7.24.0"),sQuery(id+"F0.wireOp",EDGE,"E2.7.25.0"),sQuery(id+"F0.wireOp",EDGE,"E2.7.26.0"),sQuery(id+"F0.wireOp",EDGE,"E2.7.27.0"),sQuery(id+"F0.wireOp",EDGE,"E2.7.28.0"),sQuery(id+"F0.wireOp",EDGE,"E2.7.29.0"),sQuery(id+"F0.wireOp",EDGE,"E2.7.30.0"),sQuery(id+"F0.wireOp",EDGE,"E2.7.31.0"),sQuery(id+"F0.wireOp",EDGE,"E2.7.32.0"),sQuery(id+"F0.wireOp",EDGE,"E2.7.33.0"),sQuery(id+"F0.wireOp",EDGE,"E2.7.34.0"),sQuery(id+"F0.wireOp",EDGE,"E2.7.35.0"),sQuery(id+"F0.wireOp",EDGE,"E2.7.36.0"),sQuery(id+"F0.wireOp",EDGE,"E2.7.37.0"),sQuery(id+"F0.wireOp",EDGE,"E2.7.38.0"),sQuery(id+"F0.wireOp",EDGE,"E2.7.39.0"),sQuery(id+"F0.wireOp",EDGE,"E2.7.40.0"),sQuery(id+"F0.wireOp",EDGE,"E2.7.41.0"),sQuery(id+"F0.wireOp",EDGE,"E2.7.42.0"),sQuery(id+"F0.wireOp",EDGE,"E2.7.43.0"),sQuery(id+"F0.wireOp",EDGE,"E2.7.44.0"),sQuery(id+"F0.wireOp",EDGE,"E2.8.0.0"),sQuery(id+"F0.wireOp",EDGE,"E2.8.1.0"),sQuery(id+"F0.wireOp",EDGE,"E2.8.2.0"),sQuery(id+"F0.wireOp",EDGE,"E2.8.3.0"),sQuery(id+"F0.wireOp",EDGE,"E2.8.4.0"),sQuery(id+"F0.wireOp",EDGE,"E2.8.5.0"),sQuery(id+"F0.wireOp",EDGE,"E2.8.6.0"),sQuery(id+"F0.wireOp",EDGE,"E2.8.7.0"),sQuery(id+"F0.wireOp",EDGE,"E2.8.8.0"),sQuery(id+"F0.wireOp",EDGE,"E2.8.9.0"),sQuery(id+"F0.wireOp",EDGE,"E2.8.10.0"),sQuery(id+"F0.wireOp",EDGE,"E2.8.11.0"),sQuery(id+"F0.wireOp",EDGE,"E2.8.12.0"),sQuery(id+"F0.wireOp",EDGE,"E2.8.13.0"),sQuery(id+"F0.wireOp",EDGE,"E2.8.14.0"),sQuery(id+"F0.wireOp",EDGE,"E2.8.15.0"),sQuery(id+"F0.wireOp",EDGE,"E2.8.16.0"),sQuery(id+"F0.wireOp",EDGE,"E2.8.17.0"),sQuery(id+"F0.wireOp",EDGE,"E2.8.18.0"),sQuery(id+"F0.wireOp",EDGE,"E2.8.19.0"),sQuery(id+"F0.wireOp",EDGE,"E2.8.20.0"),sQuery(id+"F0.wireOp",EDGE,"E2.8.21.0"),sQuery(id+"F0.wireOp",EDGE,"E2.8.22.0"),sQuery(id+"F0.wireOp",EDGE,"E2.8.23.0"),sQuery(id+"F0.wireOp",EDGE,"E2.8.24.0"),sQuery(id+"F0.wireOp",EDGE,"E2.8.25.0"),sQuery(id+"F0.wireOp",EDGE,"E2.8.26.0"),sQuery(id+"F0.wireOp",EDGE,"E2.8.27.0"),sQuery(id+"F0.wireOp",EDGE,"E2.8.28.0"),sQuery(id+"F0.wireOp",EDGE,"E2.8.29.0"),sQuery(id+"F0.wireOp",EDGE,"E2.8.30.0"),sQuery(id+"F0.wireOp",EDGE,"E2.8.31.0"),sQuery(id+"F0.wireOp",EDGE,"E2.8.32.0"),sQuery(id+"F0.wireOp",EDGE,"E2.8.33.0"),sQuery(id+"F0.wireOp",EDGE,"E2.8.34.0"),sQuery(id+"F0.wireOp",EDGE,"E2.8.35.0"),sQuery(id+"F0.wireOp",EDGE,"E2.8.36.0"),sQuery(id+"F0.wireOp",EDGE,"E2.8.37.0"),sQuery(id+"F0.wireOp",EDGE,"E2.8.38.0"),sQuery(id+"F0.wireOp",EDGE,"E2.8.39.0"),sQuery(id+"F0.wireOp",EDGE,"E2.8.40.0"),sQuery(id+"F0.wireOp",EDGE,"E2.8.41.0"),sQuery(id+"F0.wireOp",EDGE,"E2.8.42.0"),sQuery(id+"F0.wireOp",EDGE,"E2.8.43.0"),sQuery(id+"F0.wireOp",EDGE,"E2.8.44.0"),sQuery(id+"F0.wireOp",EDGE,"E2.9.0.0"),sQuery(id+"F0.wireOp",EDGE,"E2.9.1.0"),sQuery(id+"F0.wireOp",EDGE,"E2.9.2.0"),sQuery(id+"F0.wireOp",EDGE,"E2.9.3.0"),sQuery(id+"F0.wireOp",EDGE,"E2.9.4.0"),sQuery(id+"F0.wireOp",EDGE,"E2.9.5.0"),sQuery(id+"F0.wireOp",EDGE,"E2.9.6.0"),sQuery(id+"F0.wireOp",EDGE,"E2.9.7.0"),sQuery(id+"F0.wireOp",EDGE,"E2.9.8.0"),sQuery(id+"F0.wireOp",EDGE,"E2.9.9.0"),sQuery(id+"F0.wireOp",EDGE,"E2.9.10.0"),sQuery(id+"F0.wireOp",EDGE,"E2.9.11.0"),sQuery(id+"F0.wireOp",EDGE,"E2.9.12.0"),sQuery(id+"F0.wireOp",EDGE,"E2.9.13.0"),sQuery(id+"F0.wireOp",EDGE,"E2.9.14.0"),sQuery(id+"F0.wireOp",EDGE,"E2.9.15.0"),sQuery(id+"F0.wireOp",EDGE,"E2.9.16.0"),sQuery(id+"F0.wireOp",EDGE,"E2.9.17.0"),sQuery(id+"F0.wireOp",EDGE,"E2.9.18.0"),sQuery(id+"F0.wireOp",EDGE,"E2.9.19.0"),sQuery(id+"F0.wireOp",EDGE,"E2.9.20.0"),sQuery(id+"F0.wireOp",EDGE,"E2.9.21.0"),sQuery(id+"F0.wireOp",EDGE,"E2.9.22.0"),sQuery(id+"F0.wireOp",EDGE,"E2.9.23.0"),sQuery(id+"F0.wireOp",EDGE,"E2.9.24.0"),sQuery(id+"F0.wireOp",EDGE,"E2.9.25.0"),sQuery(id+"F0.wireOp",EDGE,"E2.9.26.0"),sQuery(id+"F0.wireOp",EDGE,"E2.9.27.0"),sQuery(id+"F0.wireOp",EDGE,"E2.9.28.0"),sQuery(id+"F0.wireOp",EDGE,"E2.9.29.0"),sQuery(id+"F0.wireOp",EDGE,"E2.9.30.0"),sQuery(id+"F0.wireOp",EDGE,"E2.9.31.0"),sQuery(id+"F0.wireOp",EDGE,"E2.9.32.0"),sQuery(id+"F0.wireOp",EDGE,"E2.9.33.0"),sQuery(id+"F0.wireOp",EDGE,"E2.9.34.0"),sQuery(id+"F0.wireOp",EDGE,"E2.9.35.0"),sQuery(id+"F0.wireOp",EDGE,"E2.9.36.0"),sQuery(id+"F0.wireOp",EDGE,"E2.9.37.0"),sQuery(id+"F0.wireOp",EDGE,"E2.9.38.0"),sQuery(id+"F0.wireOp",EDGE,"E2.9.39.0"),sQuery(id+"F0.wireOp",EDGE,"E2.9.40.0"),sQuery(id+"F0.wireOp",EDGE,"E2.9.41.0"),sQuery(id+"F0.wireOp",EDGE,"E2.9.42.0"),sQuery(id+"F0.wireOp",EDGE,"E2.9.43.0"),sQuery(id+"F0.wireOp",EDGE,"E2.9.44.0"),sQuery(id+"F0.wireOp",EDGE,"E2.10.0.0"),sQuery(id+"F0.wireOp",EDGE,"E2.10.1.0"),sQuery(id+"F0.wireOp",EDGE,"E2.10.2.0"),sQuery(id+"F0.wireOp",EDGE,"E2.10.3.0"),sQuery(id+"F0.wireOp",EDGE,"E2.10.4.0"),sQuery(id+"F0.wireOp",EDGE,"E2.10.5.0"),sQuery(id+"F0.wireOp",EDGE,"E2.10.6.0"),sQuery(id+"F0.wireOp",EDGE,"E2.10.7.0"),sQuery(id+"F0.wireOp",EDGE,"E2.10.8.0"),sQuery(id+"F0.wireOp",EDGE,"E2.10.9.0"),sQuery(id+"F0.wireOp",EDGE,"E2.10.10.0"),sQuery(id+"F0.wireOp",EDGE,"E2.10.11.0"),sQuery(id+"F0.wireOp",EDGE,"E2.10.12.0"),sQuery(id+"F0.wireOp",EDGE,"E2.10.13.0"),sQuery(id+"F0.wireOp",EDGE,"E2.10.14.0"),sQuery(id+"F0.wireOp",EDGE,"E2.10.15.0"),sQuery(id+"F0.wireOp",EDGE,"E2.10.16.0"),sQuery(id+"F0.wireOp",EDGE,"E2.10.17.0"),sQuery(id+"F0.wireOp",EDGE,"E2.10.18.0"),sQuery(id+"F0.wireOp",EDGE,"E2.10.19.0"),sQuery(id+"F0.wireOp",EDGE,"E2.10.20.0"),sQuery(id+"F0.wireOp",EDGE,"E2.10.21.0"),sQuery(id+"F0.wireOp",EDGE,"E2.10.22.0"),sQuery(id+"F0.wireOp",EDGE,"E2.10.23.0"),sQuery(id+"F0.wireOp",EDGE,"E2.10.24.0"),sQuery(id+"F0.wireOp",EDGE,"E2.10.25.0"),sQuery(id+"F0.wireOp",EDGE,"E2.10.26.0"),sQuery(id+"F0.wireOp",EDGE,"E2.10.27.0"),sQuery(id+"F0.wireOp",EDGE,"E2.10.28.0"),sQuery(id+"F0.wireOp",EDGE,"E2.10.29.0"),sQuery(id+"F0.wireOp",EDGE,"E2.10.30.0"),sQuery(id+"F0.wireOp",EDGE,"E2.10.31.0"),sQuery(id+"F0.wireOp",EDGE,"E2.10.32.0"),sQuery(id+"F0.wireOp",EDGE,"E2.10.33.0"),sQuery(id+"F0.wireOp",EDGE,"E2.10.34.0"),sQuery(id+"F0.wireOp",EDGE,"E2.10.35.0"),sQuery(id+"F0.wireOp",EDGE,"E2.10.36.0"),sQuery(id+"F0.wireOp",EDGE,"E2.10.37.0"),sQuery(id+"F0.wireOp",EDGE,"E2.10.38.0"),sQuery(id+"F0.wireOp",EDGE,"E2.10.39.0"),sQuery(id+"F0.wireOp",EDGE,"E2.10.40.0"),sQuery(id+"F0.wireOp",EDGE,"E2.10.41.0"),sQuery(id+"F0.wireOp",EDGE,"E2.10.42.0"),sQuery(id+"F0.wireOp",EDGE,"E2.10.43.0"),sQuery(id+"F0.wireOp",EDGE,"E2.10.44.0"),sQuery(id+"F0.wireOp",EDGE,"E2.11.0.0"),sQuery(id+"F0.wireOp",EDGE,"E2.11.1.0"),sQuery(id+"F0.wireOp",EDGE,"E2.11.2.0"),sQuery(id+"F0.wireOp",EDGE,"E2.11.3.0"),sQuery(id+"F0.wireOp",EDGE,"E2.11.4.0"),sQuery(id+"F0.wireOp",EDGE,"E2.11.5.0"),sQuery(id+"F0.wireOp",EDGE,"E2.11.6.0"),sQuery(id+"F0.wireOp",EDGE,"E2.11.7.0"),sQuery(id+"F0.wireOp",EDGE,"E2.11.8.0"),sQuery(id+"F0.wireOp",EDGE,"E2.11.9.0"),sQuery(id+"F0.wireOp",EDGE,"E2.11.10.0"),sQuery(id+"F0.wireOp",EDGE,"E2.11.11.0"),sQuery(id+"F0.wireOp",EDGE,"E2.11.12.0"),sQuery(id+"F0.wireOp",EDGE,"E2.11.13.0"),sQuery(id+"F0.wireOp",EDGE,"E2.11.14.0"),sQuery(id+"F0.wireOp",EDGE,"E2.11.15.0"),sQuery(id+"F0.wireOp",EDGE,"E2.11.16.0"),sQuery(id+"F0.wireOp",EDGE,"E2.11.17.0"),sQuery(id+"F0.wireOp",EDGE,"E2.11.18.0"),sQuery(id+"F0.wireOp",EDGE,"E2.11.19.0"),sQuery(id+"F0.wireOp",EDGE,"E2.11.20.0"),sQuery(id+"F0.wireOp",EDGE,"E2.11.21.0"),sQuery(id+"F0.wireOp",EDGE,"E2.11.22.0"),sQuery(id+"F0.wireOp",EDGE,"E2.11.23.0"),sQuery(id+"F0.wireOp",EDGE,"E2.11.24.0"),sQuery(id+"F0.wireOp",EDGE,"E2.11.25.0"),sQuery(id+"F0.wireOp",EDGE,"E2.11.26.0"),sQuery(id+"F0.wireOp",EDGE,"E2.11.27.0"),sQuery(id+"F0.wireOp",EDGE,"E2.11.28.0"),sQuery(id+"F0.wireOp",EDGE,"E2.11.29.0"),sQuery(id+"F0.wireOp",EDGE,"E2.11.30.0"),sQuery(id+"F0.wireOp",EDGE,"E2.11.31.0"),sQuery(id+"F0.wireOp",EDGE,"E2.11.32.0"),sQuery(id+"F0.wireOp",EDGE,"E2.11.33.0"),sQuery(id+"F0.wireOp",EDGE,"E2.11.34.0"),sQuery(id+"F0.wireOp",EDGE,"E2.11.35.0"),sQuery(id+"F0.wireOp",EDGE,"E2.11.36.0"),sQuery(id+"F0.wireOp",EDGE,"E2.11.37.0"),sQuery(id+"F0.wireOp",EDGE,"E2.11.38.0"),sQuery(id+"F0.wireOp",EDGE,"E2.11.39.0"),sQuery(id+"F0.wireOp",EDGE,"E2.11.40.0"),sQuery(id+"F0.wireOp",EDGE,"E2.11.41.0"),sQuery(id+"F0.wireOp",EDGE,"E2.11.42.0"),sQuery(id+"F0.wireOp",EDGE,"E2.11.43.0"),sQuery(id+"F0.wireOp",EDGE,"E2.11.44.0"),sQuery(id+"F0.wireOp",EDGE,"E2.12.0.0"),sQuery(id+"F0.wireOp",EDGE,"E2.12.1.0"),sQuery(id+"F0.wireOp",EDGE,"E2.12.2.0"),sQuery(id+"F0.wireOp",EDGE,"E2.12.3.0"),sQuery(id+"F0.wireOp",EDGE,"E2.12.4.0"),sQuery(id+"F0.wireOp",EDGE,"E2.12.5.0"),sQuery(id+"F0.wireOp",EDGE,"E2.12.6.0"),sQuery(id+"F0.wireOp",EDGE,"E2.12.7.0"),sQuery(id+"F0.wireOp",EDGE,"E2.12.8.0"),sQuery(id+"F0.wireOp",EDGE,"E2.12.9.0"),sQuery(id+"F0.wireOp",EDGE,"E2.12.10.0"),sQuery(id+"F0.wireOp",EDGE,"E2.12.11.0"),sQuery(id+"F0.wireOp",EDGE,"E2.12.12.0"),sQuery(id+"F0.wireOp",EDGE,"E2.12.13.0"),sQuery(id+"F0.wireOp",EDGE,"E2.12.14.0"),sQuery(id+"F0.wireOp",EDGE,"E2.12.15.0"),sQuery(id+"F0.wireOp",EDGE,"E2.12.16.0"),sQuery(id+"F0.wireOp",EDGE,"E2.12.17.0"),sQuery(id+"F0.wireOp",EDGE,"E2.12.18.0"),sQuery(id+"F0.wireOp",EDGE,"E2.12.19.0"),sQuery(id+"F0.wireOp",EDGE,"E2.12.20.0"),sQuery(id+"F0.wireOp",EDGE,"E2.12.21.0"),sQuery(id+"F0.wireOp",EDGE,"E2.12.22.0"),sQuery(id+"F0.wireOp",EDGE,"E2.12.23.0"),sQuery(id+"F0.wireOp",EDGE,"E2.12.24.0"),sQuery(id+"F0.wireOp",EDGE,"E2.12.25.0"),sQuery(id+"F0.wireOp",EDGE,"E2.12.26.0"),sQuery(id+"F0.wireOp",EDGE,"E2.12.27.0"),sQuery(id+"F0.wireOp",EDGE,"E2.12.28.0"),sQuery(id+"F0.wireOp",EDGE,"E2.12.29.0"),sQuery(id+"F0.wireOp",EDGE,"E2.12.30.0"),sQuery(id+"F0.wireOp",EDGE,"E2.12.31.0"),sQuery(id+"F0.wireOp",EDGE,"E2.12.32.0"),sQuery(id+"F0.wireOp",EDGE,"E2.12.33.0"),sQuery(id+"F0.wireOp",EDGE,"E2.12.34.0"),sQuery(id+"F0.wireOp",EDGE,"E2.12.35.0"),sQuery(id+"F0.wireOp",EDGE,"E2.12.36.0"),sQuery(id+"F0.wireOp",EDGE,"E2.12.37.0"),sQuery(id+"F0.wireOp",EDGE,"E2.12.38.0"),sQuery(id+"F0.wireOp",EDGE,"E2.12.39.0"),sQuery(id+"F0.wireOp",EDGE,"E2.12.40.0"),sQuery(id+"F0.wireOp",EDGE,"E2.12.41.0"),sQuery(id+"F0.wireOp",EDGE,"E2.12.42.0"),sQuery(id+"F0.wireOp",EDGE,"E2.12.43.0"),sQuery(id+"F0.wireOp",EDGE,"E2.12.44.0"),sQuery(id+"F0.wireOp",EDGE,"E2.13.0.0"),sQuery(id+"F0.wireOp",EDGE,"E2.13.1.0"),sQuery(id+"F0.wireOp",EDGE,"E2.13.2.0"),sQuery(id+"F0.wireOp",EDGE,"E2.13.3.0"),sQuery(id+"F0.wireOp",EDGE,"E2.13.4.0"),sQuery(id+"F0.wireOp",EDGE,"E2.13.5.0"),sQuery(id+"F0.wireOp",EDGE,"E2.13.6.0"),sQuery(id+"F0.wireOp",EDGE,"E2.13.7.0"),sQuery(id+"F0.wireOp",EDGE,"E2.13.8.0"),sQuery(id+"F0.wireOp",EDGE,"E2.13.9.0"),sQuery(id+"F0.wireOp",EDGE,"E2.13.10.0"),sQuery(id+"F0.wireOp",EDGE,"E2.13.11.0"),sQuery(id+"F0.wireOp",EDGE,"E2.13.12.0"),sQuery(id+"F0.wireOp",EDGE,"E2.13.13.0"),sQuery(id+"F0.wireOp",EDGE,"E2.13.14.0"),sQuery(id+"F0.wireOp",EDGE,"E2.13.15.0"),sQuery(id+"F0.wireOp",EDGE,"E2.13.16.0"),sQuery(id+"F0.wireOp",EDGE,"E2.13.17.0"),sQuery(id+"F0.wireOp",EDGE,"E2.13.18.0"),sQuery(id+"F0.wireOp",EDGE,"E2.13.19.0"),sQuery(id+"F0.wireOp",EDGE,"E2.13.20.0"),sQuery(id+"F0.wireOp",EDGE,"E2.13.21.0"),sQuery(id+"F0.wireOp",EDGE,"E2.13.22.0"),sQuery(id+"F0.wireOp",EDGE,"E2.13.23.0"),sQuery(id+"F0.wireOp",EDGE,"E2.13.24.0"),sQuery(id+"F0.wireOp",EDGE,"E2.13.25.0"),sQuery(id+"F0.wireOp",EDGE,"E2.13.26.0"),sQuery(id+"F0.wireOp",EDGE,"E2.13.27.0"),sQuery(id+"F0.wireOp",EDGE,"E2.13.28.0"),sQuery(id+"F0.wireOp",EDGE,"E2.13.29.0"),sQuery(id+"F0.wireOp",EDGE,"E2.13.30.0"),sQuery(id+"F0.wireOp",EDGE,"E2.13.31.0"),sQuery(id+"F0.wireOp",EDGE,"E2.13.32.0"),sQuery(id+"F0.wireOp",EDGE,"E2.13.33.0"),sQuery(id+"F0.wireOp",EDGE,"E2.13.34.0"),sQuery(id+"F0.wireOp",EDGE,"E2.13.35.0"),sQuery(id+"F0.wireOp",EDGE,"E2.13.36.0"),sQuery(id+"F0.wireOp",EDGE,"E2.13.37.0"),sQuery(id+"F0.wireOp",EDGE,"E2.13.38.0"),sQuery(id+"F0.wireOp",EDGE,"E2.13.39.0"),sQuery(id+"F0.wireOp",EDGE,"E2.13.40.0"),sQuery(id+"F0.wireOp",EDGE,"E2.13.41.0"),sQuery(id+"F0.wireOp",EDGE,"E2.13.42.0"),sQuery(id+"F0.wireOp",EDGE,"E2.13.43.0"),sQuery(id+"F0.wireOp",EDGE,"E2.13.44.0"),sQuery(id+"F0.wireOp",EDGE,"E2.14.0.0"),sQuery(id+"F0.wireOp",EDGE,"E2.14.1.0"),sQuery(id+"F0.wireOp",EDGE,"E2.14.2.0"),sQuery(id+"F0.wireOp",EDGE,"E2.14.3.0"),sQuery(id+"F0.wireOp",EDGE,"E2.14.4.0"),sQuery(id+"F0.wireOp",EDGE,"E2.14.5.0"),sQuery(id+"F0.wireOp",EDGE,"E2.14.6.0"),sQuery(id+"F0.wireOp",EDGE,"E2.14.7.0"),sQuery(id+"F0.wireOp",EDGE,"E2.14.8.0"),sQuery(id+"F0.wireOp",EDGE,"E2.14.9.0"),sQuery(id+"F0.wireOp",EDGE,"E2.14.10.0"),sQuery(id+"F0.wireOp",EDGE,"E2.14.11.0"),sQuery(id+"F0.wireOp",EDGE,"E2.14.12.0"),sQuery(id+"F0.wireOp",EDGE,"E2.14.13.0"),sQuery(id+"F0.wireOp",EDGE,"E2.14.14.0"),sQuery(id+"F0.wireOp",EDGE,"E2.14.15.0"),sQuery(id+"F0.wireOp",EDGE,"E2.14.16.0"),sQuery(id+"F0.wireOp",EDGE,"E2.14.17.0"),sQuery(id+"F0.wireOp",EDGE,"E2.14.18.0"),sQuery(id+"F0.wireOp",EDGE,"E2.14.19.0"),sQuery(id+"F0.wireOp",EDGE,"E2.14.20.0"),sQuery(id+"F0.wireOp",EDGE,"E2.14.21.0"),sQuery(id+"F0.wireOp",EDGE,"E2.14.22.0"),sQuery(id+"F0.wireOp",EDGE,"E2.14.23.0"),sQuery(id+"F0.wireOp",EDGE,"E2.14.24.0"),sQuery(id+"F0.wireOp",EDGE,"E2.14.25.0"),sQuery(id+"F0.wireOp",EDGE,"E2.14.26.0"),sQuery(id+"F0.wireOp",EDGE,"E2.14.27.0"),sQuery(id+"F0.wireOp",EDGE,"E2.14.28.0"),sQuery(id+"F0.wireOp",EDGE,"E2.14.29.0"),sQuery(id+"F0.wireOp",EDGE,"E2.14.30.0"),sQuery(id+"F0.wireOp",EDGE,"E2.14.31.0"),sQuery(id+"F0.wireOp",EDGE,"E2.14.32.0"),sQuery(id+"F0.wireOp",EDGE,"E2.14.33.0"),sQuery(id+"F0.wireOp",EDGE,"E2.14.34.0"),sQuery(id+"F0.wireOp",EDGE,"E2.14.35.0"),sQuery(id+"F0.wireOp",EDGE,"E2.14.36.0"),sQuery(id+"F0.wireOp",EDGE,"E2.14.37.0"),sQuery(id+"F0.wireOp",EDGE,"E2.14.38.0"),sQuery(id+"F0.wireOp",EDGE,"E2.14.39.0"),sQuery(id+"F0.wireOp",EDGE,"E2.14.40.0"),sQuery(id+"F0.wireOp",EDGE,"E2.14.41.0"),sQuery(id+"F0.wireOp",EDGE,"E2.14.42.0"),sQuery(id+"F0.wireOp",EDGE,"E2.14.43.0"),sQuery(id+"F0.wireOp",EDGE,"E2.14.44.0"),sQuery(id+"F0.wireOp",EDGE,"E2.15.0.0"),sQuery(id+"F0.wireOp",EDGE,"E2.15.1.0"),sQuery(id+"F0.wireOp",EDGE,"E2.15.2.0"),sQuery(id+"F0.wireOp",EDGE,"E2.15.3.0"),sQuery(id+"F0.wireOp",EDGE,"E2.15.4.0"),sQuery(id+"F0.wireOp",EDGE,"E2.15.5.0"),sQuery(id+"F0.wireOp",EDGE,"E2.15.6.0"),sQuery(id+"F0.wireOp",EDGE,"E2.15.7.0"),sQuery(id+"F0.wireOp",EDGE,"E2.15.8.0"),sQuery(id+"F0.wireOp",EDGE,"E2.15.9.0"),sQuery(id+"F0.wireOp",EDGE,"E2.15.10.0"),sQuery(id+"F0.wireOp",EDGE,"E2.15.11.0"),sQuery(id+"F0.wireOp",EDGE,"E2.15.12.0"),sQuery(id+"F0.wireOp",EDGE,"E2.15.13.0"),sQuery(id+"F0.wireOp",EDGE,"E2.15.14.0"),sQuery(id+"F0.wireOp",EDGE,"E2.15.15.0"),sQuery(id+"F0.wireOp",EDGE,"E2.15.16.0"),sQuery(id+"F0.wireOp",EDGE,"E2.15.17.0"),sQuery(id+"F0.wireOp",EDGE,"E2.15.18.0"),sQuery(id+"F0.wireOp",EDGE,"E2.15.19.0"),sQuery(id+"F0.wireOp",EDGE,"E2.15.20.0"),sQuery(id+"F0.wireOp",EDGE,"E2.15.21.0"),sQuery(id+"F0.wireOp",EDGE,"E2.15.22.0"),sQuery(id+"F0.wireOp",EDGE,"E2.15.23.0"),sQuery(id+"F0.wireOp",EDGE,"E2.15.24.0"),sQuery(id+"F0.wireOp",EDGE,"E2.15.25.0"),sQuery(id+"F0.wireOp",EDGE,"E2.15.26.0"),sQuery(id+"F0.wireOp",EDGE,"E2.15.27.0"),sQuery(id+"F0.wireOp",EDGE,"E2.15.28.0"),sQuery(id+"F0.wireOp",EDGE,"E2.15.29.0"),sQuery(id+"F0.wireOp",EDGE,"E2.15.30.0"),sQuery(id+"F0.wireOp",EDGE,"E2.15.31.0"),sQuery(id+"F0.wireOp",EDGE,"E2.15.32.0"),sQuery(id+"F0.wireOp",EDGE,"E2.15.33.0"),sQuery(id+"F0.wireOp",EDGE,"E2.15.34.0"),sQuery(id+"F0.wireOp",EDGE,"E2.15.35.0"),sQuery(id+"F0.wireOp",EDGE,"E2.15.36.0"),sQuery(id+"F0.wireOp",EDGE,"E2.15.37.0"),sQuery(id+"F0.wireOp",EDGE,"E2.15.38.0"),sQuery(id+"F0.wireOp",EDGE,"E2.15.39.0"),sQuery(id+"F0.wireOp",EDGE,"E2.15.40.0"),sQuery(id+"F0.wireOp",EDGE,"E2.15.41.0"),sQuery(id+"F0.wireOp",EDGE,"E2.15.42.0"),sQuery(id+"F0.wireOp",EDGE,"E2.15.43.0"),sQuery(id+"F0.wireOp",EDGE,"E2.15.44.0"),sQuery(id+"F0.wireOp",EDGE,"E2.16.0.0"),sQuery(id+"F0.wireOp",EDGE,"E2.16.1.0"),sQuery(id+"F0.wireOp",EDGE,"E2.16.2.0"),sQuery(id+"F0.wireOp",EDGE,"E2.16.3.0"),sQuery(id+"F0.wireOp",EDGE,"E2.16.4.0"),sQuery(id+"F0.wireOp",EDGE,"E2.16.5.0"),sQuery(id+"F0.wireOp",EDGE,"E2.16.6.0"),sQuery(id+"F0.wireOp",EDGE,"E2.16.7.0"),sQuery(id+"F0.wireOp",EDGE,"E2.16.8.0"),sQuery(id+"F0.wireOp",EDGE,"E2.16.9.0"),sQuery(id+"F0.wireOp",EDGE,"E2.16.10.0"),sQuery(id+"F0.wireOp",EDGE,"E2.16.11.0"),sQuery(id+"F0.wireOp",EDGE,"E2.16.12.0"),sQuery(id+"F0.wireOp",EDGE,"E2.16.13.0"),sQuery(id+"F0.wireOp",EDGE,"E2.16.14.0"),sQuery(id+"F0.wireOp",EDGE,"E2.16.15.0"),sQuery(id+"F0.wireOp",EDGE,"E2.16.16.0"),sQuery(id+"F0.wireOp",EDGE,"E2.16.17.0"),sQuery(id+"F0.wireOp",EDGE,"E2.16.18.0"),sQuery(id+"F0.wireOp",EDGE,"E2.16.19.0"),sQuery(id+"F0.wireOp",EDGE,"E2.16.20.0"),sQuery(id+"F0.wireOp",EDGE,"E2.16.21.0"),sQuery(id+"F0.wireOp",EDGE,"E2.16.22.0"),sQuery(id+"F0.wireOp",EDGE,"E2.16.23.0"),sQuery(id+"F0.wireOp",EDGE,"E2.16.24.0"),sQuery(id+"F0.wireOp",EDGE,"E2.16.25.0"),sQuery(id+"F0.wireOp",EDGE,"E2.16.26.0"),sQuery(id+"F0.wireOp",EDGE,"E2.16.27.0"),sQuery(id+"F0.wireOp",EDGE,"E2.16.28.0"),sQuery(id+"F0.wireOp",EDGE,"E2.16.29.0"),sQuery(id+"F0.wireOp",EDGE,"E2.16.30.0"),sQuery(id+"F0.wireOp",EDGE,"E2.16.31.0"),sQuery(id+"F0.wireOp",EDGE,"E2.16.32.0"),sQuery(id+"F0.wireOp",EDGE,"E2.16.33.0"),sQuery(id+"F0.wireOp",EDGE,"E2.16.34.0"),sQuery(id+"F0.wireOp",EDGE,"E2.16.35.0"),sQuery(id+"F0.wireOp",EDGE,"E2.16.36.0"),sQuery(id+"F0.wireOp",EDGE,"E2.16.37.0"),sQuery(id+"F0.wireOp",EDGE,"E2.16.38.0"),sQuery(id+"F0.wireOp",EDGE,"E2.16.39.0"),sQuery(id+"F0.wireOp",EDGE,"E2.16.40.0"),sQuery(id+"F0.wireOp",EDGE,"E2.16.41.0"),sQuery(id+"F0.wireOp",EDGE,"E2.16.42.0"),sQuery(id+"F0.wireOp",EDGE,"E2.16.43.0"),sQuery(id+"F0.wireOp",EDGE,"E2.16.44.0"),sQuery(id+"F0.wireOp",EDGE,"E2.17.0.0"),sQuery(id+"F0.wireOp",EDGE,"E2.17.1.0"),sQuery(id+"F0.wireOp",EDGE,"E2.17.2.0"),sQuery(id+"F0.wireOp",EDGE,"E2.17.3.0"),sQuery(id+"F0.wireOp",EDGE,"E2.17.4.0"),sQuery(id+"F0.wireOp",EDGE,"E2.17.5.0"),sQuery(id+"F0.wireOp",EDGE,"E2.17.6.0"),sQuery(id+"F0.wireOp",EDGE,"E2.17.7.0"),sQuery(id+"F0.wireOp",EDGE,"E2.17.8.0"),sQuery(id+"F0.wireOp",EDGE,"E2.17.9.0"),sQuery(id+"F0.wireOp",EDGE,"E2.17.10.0"),sQuery(id+"F0.wireOp",EDGE,"E2.17.11.0"),sQuery(id+"F0.wireOp",EDGE,"E2.17.12.0"),sQuery(id+"F0.wireOp",EDGE,"E2.17.13.0"),sQuery(id+"F0.wireOp",EDGE,"E2.17.14.0"),sQuery(id+"F0.wireOp",EDGE,"E2.17.15.0"),sQuery(id+"F0.wireOp",EDGE,"E2.17.16.0"),sQuery(id+"F0.wireOp",EDGE,"E2.17.17.0"),sQuery(id+"F0.wireOp",EDGE,"E2.17.18.0"),sQuery(id+"F0.wireOp",EDGE,"E2.17.19.0"),sQuery(id+"F0.wireOp",EDGE,"E2.17.20.0"),sQuery(id+"F0.wireOp",EDGE,"E2.17.21.0"),sQuery(id+"F0.wireOp",EDGE,"E2.17.22.0"),sQuery(id+"F0.wireOp",EDGE,"E2.17.23.0"),sQuery(id+"F0.wireOp",EDGE,"E2.17.24.0"),sQuery(id+"F0.wireOp",EDGE,"E2.17.25.0"),sQuery(id+"F0.wireOp",EDGE,"E2.17.26.0"),sQuery(id+"F0.wireOp",EDGE,"E2.17.27.0"),sQuery(id+"F0.wireOp",EDGE,"E2.17.28.0"),sQuery(id+"F0.wireOp",EDGE,"E2.17.29.0"),sQuery(id+"F0.wireOp",EDGE,"E2.17.30.0"),sQuery(id+"F0.wireOp",EDGE,"E2.17.31.0"),sQuery(id+"F0.wireOp",EDGE,"E2.17.32.0"),sQuery(id+"F0.wireOp",EDGE,"E2.17.33.0"),sQuery(id+"F0.wireOp",EDGE,"E2.17.34.0"),sQuery(id+"F0.wireOp",EDGE,"E2.17.35.0"),sQuery(id+"F0.wireOp",EDGE,"E2.17.36.0"),sQuery(id+"F0.wireOp",EDGE,"E2.17.37.0"),sQuery(id+"F0.wireOp",EDGE,"E2.17.38.0"),sQuery(id+"F0.wireOp",EDGE,"E2.17.39.0"),sQuery(id+"F0.wireOp",EDGE,"E2.17.40.0"),sQuery(id+"F0.wireOp",EDGE,"E2.17.41.0"),sQuery(id+"F0.wireOp",EDGE,"E2.17.42.0"),sQuery(id+"F0.wireOp",EDGE,"E2.17.43.0"),sQuery(id+"F0.wireOp",EDGE,"E2.17.44.0"),sQuery(id+"F0.wireOp",EDGE,"E2.18.0.0"),sQuery(id+"F0.wireOp",EDGE,"E2.18.1.0"),sQuery(id+"F0.wireOp",EDGE,"E2.18.2.0"),sQuery(id+"F0.wireOp",EDGE,"E2.18.3.0"),sQuery(id+"F0.wireOp",EDGE,"E2.18.4.0"),sQuery(id+"F0.wireOp",EDGE,"E2.18.5.0"),sQuery(id+"F0.wireOp",EDGE,"E2.18.6.0"),sQuery(id+"F0.wireOp",EDGE,"E2.18.7.0"),sQuery(id+"F0.wireOp",EDGE,"E2.18.8.0"),sQuery(id+"F0.wireOp",EDGE,"E2.18.9.0"),sQuery(id+"F0.wireOp",EDGE,"E2.18.10.0"),sQuery(id+"F0.wireOp",EDGE,"E2.18.11.0"),sQuery(id+"F0.wireOp",EDGE,"E2.18.12.0"),sQuery(id+"F0.wireOp",EDGE,"E2.18.13.0"),sQuery(id+"F0.wireOp",EDGE,"E2.18.14.0"),sQuery(id+"F0.wireOp",EDGE,"E2.18.15.0"),sQuery(id+"F0.wireOp",EDGE,"E2.18.16.0"),sQuery(id+"F0.wireOp",EDGE,"E2.18.17.0"),sQuery(id+"F0.wireOp",EDGE,"E2.18.18.0"),sQuery(id+"F0.wireOp",EDGE,"E2.18.19.0"),sQuery(id+"F0.wireOp",EDGE,"E2.18.20.0"),sQuery(id+"F0.wireOp",EDGE,"E2.18.21.0"),sQuery(id+"F0.wireOp",EDGE,"E2.18.22.0"),sQuery(id+"F0.wireOp",EDGE,"E2.18.23.0"),sQuery(id+"F0.wireOp",EDGE,"E2.18.24.0"),sQuery(id+"F0.wireOp",EDGE,"E2.18.25.0"),sQuery(id+"F0.wireOp",EDGE,"E2.18.26.0"),sQuery(id+"F0.wireOp",EDGE,"E2.18.27.0"),sQuery(id+"F0.wireOp",EDGE,"E2.18.28.0"),sQuery(id+"F0.wireOp",EDGE,"E2.18.29.0"),sQuery(id+"F0.wireOp",EDGE,"E2.18.30.0"),sQuery(id+"F0.wireOp",EDGE,"E2.18.31.0"),sQuery(id+"F0.wireOp",EDGE,"E2.18.32.0"),sQuery(id+"F0.wireOp",EDGE,"E2.18.33.0"),sQuery(id+"F0.wireOp",EDGE,"E2.18.34.0"),sQuery(id+"F0.wireOp",EDGE,"E2.18.35.0"),sQuery(id+"F0.wireOp",EDGE,"E2.18.36.0"),sQuery(id+"F0.wireOp",EDGE,"E2.18.37.0"),sQuery(id+"F0.wireOp",EDGE,"E2.18.38.0"),sQuery(id+"F0.wireOp",EDGE,"E2.18.39.0"),sQuery(id+"F0.wireOp",EDGE,"E2.18.40.0"),sQuery(id+"F0.wireOp",EDGE,"E2.18.41.0"),sQuery(id+"F0.wireOp",EDGE,"E2.18.42.0"),sQuery(id+"F0.wireOp",EDGE,"E2.18.43.0"),sQuery(id+"F0.wireOp",EDGE,"E2.18.44.0"),sQuery(id+"F0.wireOp",EDGE,"E2.19.0.0"),sQuery(id+"F0.wireOp",EDGE,"E2.19.1.0"),sQuery(id+"F0.wireOp",EDGE,"E2.19.2.0"),sQuery(id+"F0.wireOp",EDGE,"E2.19.3.0"),sQuery(id+"F0.wireOp",EDGE,"E2.19.4.0"),sQuery(id+"F0.wireOp",EDGE,"E2.19.5.0"),sQuery(id+"F0.wireOp",EDGE,"E2.19.6.0"),sQuery(id+"F0.wireOp",EDGE,"E2.19.7.0"),sQuery(id+"F0.wireOp",EDGE,"E2.19.8.0"),sQuery(id+"F0.wireOp",EDGE,"E2.19.9.0"),sQuery(id+"F0.wireOp",EDGE,"E2.19.10.0"),sQuery(id+"F0.wireOp",EDGE,"E2.19.11.0"),sQuery(id+"F0.wireOp",EDGE,"E2.19.12.0"),sQuery(id+"F0.wireOp",EDGE,"E2.19.13.0"),sQuery(id+"F0.wireOp",EDGE,"E2.19.14.0"),sQuery(id+"F0.wireOp",EDGE,"E2.19.15.0"),sQuery(id+"F0.wireOp",EDGE,"E2.19.16.0"),sQuery(id+"F0.wireOp",EDGE,"E2.19.17.0"),sQuery(id+"F0.wireOp",EDGE,"E2.19.18.0"),sQuery(id+"F0.wireOp",EDGE,"E2.19.19.0"),sQuery(id+"F0.wireOp",EDGE,"E2.19.20.0"),sQuery(id+"F0.wireOp",EDGE,"E2.19.21.0"),sQuery(id+"F0.wireOp",EDGE,"E2.19.22.0"),sQuery(id+"F0.wireOp",EDGE,"E2.19.23.0"),sQuery(id+"F0.wireOp",EDGE,"E2.19.24.0"),sQuery(id+"F0.wireOp",EDGE,"E2.19.25.0"),sQuery(id+"F0.wireOp",EDGE,"E2.19.26.0"),sQuery(id+"F0.wireOp",EDGE,"E2.19.27.0"),sQuery(id+"F0.wireOp",EDGE,"E2.19.28.0"),sQuery(id+"F0.wireOp",EDGE,"E2.19.29.0"),sQuery(id+"F0.wireOp",EDGE,"E2.19.30.0"),sQuery(id+"F0.wireOp",EDGE,"E2.19.31.0"),sQuery(id+"F0.wireOp",EDGE,"E2.19.32.0"),sQuery(id+"F0.wireOp",EDGE,"E2.19.33.0"),sQuery(id+"F0.wireOp",EDGE,"E2.19.34.0"),sQuery(id+"F0.wireOp",EDGE,"E2.19.35.0"),sQuery(id+"F0.wireOp",EDGE,"E2.19.36.0"),sQuery(id+"F0.wireOp",EDGE,"E2.19.37.0"),sQuery(id+"F0.wireOp",EDGE,"E2.19.38.0"),sQuery(id+"F0.wireOp",EDGE,"E2.19.39.0"),sQuery(id+"F0.wireOp",EDGE,"E2.19.40.0"),sQuery(id+"F0.wireOp",EDGE,"E2.19.41.0"),sQuery(id+"F0.wireOp",EDGE,"E2.19.42.0"),sQuery(id+"F0.wireOp",EDGE,"E2.19.43.0"),sQuery(id+"F0.wireOp",EDGE,"E2.19.44.0"),sQuery(id+"F0.wireOp",EDGE,"E2.20.0.0"),sQuery(id+"F0.wireOp",EDGE,"E2.20.1.0"),sQuery(id+"F0.wireOp",EDGE,"E2.20.2.0"),sQuery(id+"F0.wireOp",EDGE,"E2.20.3.0"),sQuery(id+"F0.wireOp",EDGE,"E2.20.4.0"),sQuery(id+"F0.wireOp",EDGE,"E2.20.5.0"),sQuery(id+"F0.wireOp",EDGE,"E2.20.6.0"),sQuery(id+"F0.wireOp",EDGE,"E2.20.7.0"),sQuery(id+"F0.wireOp",EDGE,"E2.20.8.0"),sQuery(id+"F0.wireOp",EDGE,"E2.20.9.0"),sQuery(id+"F0.wireOp",EDGE,"E2.20.10.0"),sQuery(id+"F0.wireOp",EDGE,"E2.20.11.0"),sQuery(id+"F0.wireOp",EDGE,"E2.20.12.0"),sQuery(id+"F0.wireOp",EDGE,"E2.20.13.0"),sQuery(id+"F0.wireOp",EDGE,"E2.20.14.0"),sQuery(id+"F0.wireOp",EDGE,"E2.20.15.0"),sQuery(id+"F0.wireOp",EDGE,"E2.20.16.0"),sQuery(id+"F0.wireOp",EDGE,"E2.20.17.0"),sQuery(id+"F0.wireOp",EDGE,"E2.20.18.0"),sQuery(id+"F0.wireOp",EDGE,"E2.20.19.0"),sQuery(id+"F0.wireOp",EDGE,"E2.20.20.0"),sQuery(id+"F0.wireOp",EDGE,"E2.20.21.0"),sQuery(id+"F0.wireOp",EDGE,"E2.20.22.0"),sQuery(id+"F0.wireOp",EDGE,"E2.20.23.0"),sQuery(id+"F0.wireOp",EDGE,"E2.20.24.0"),sQuery(id+"F0.wireOp",EDGE,"E2.20.25.0"),sQuery(id+"F0.wireOp",EDGE,"E2.20.26.0"),sQuery(id+"F0.wireOp",EDGE,"E2.20.27.0"),sQuery(id+"F0.wireOp",EDGE,"E2.20.28.0"),sQuery(id+"F0.wireOp",EDGE,"E2.20.29.0"),sQuery(id+"F0.wireOp",EDGE,"E2.20.30.0"),sQuery(id+"F0.wireOp",EDGE,"E2.20.31.0"),sQuery(id+"F0.wireOp",EDGE,"E2.20.32.0"),sQuery(id+"F0.wireOp",EDGE,"E2.20.33.0"),sQuery(id+"F0.wireOp",EDGE,"E2.20.34.0"),sQuery(id+"F0.wireOp",EDGE,"E2.20.35.0"),sQuery(id+"F0.wireOp",EDGE,"E2.20.36.0"),sQuery(id+"F0.wireOp",EDGE,"E2.20.37.0"),sQuery(id+"F0.wireOp",EDGE,"E2.20.38.0"),sQuery(id+"F0.wireOp",EDGE,"E2.20.39.0"),sQuery(id+"F0.wireOp",EDGE,"E2.20.40.0"),sQuery(id+"F0.wireOp",EDGE,"E2.20.41.0"),sQuery(id+"F0.wireOp",EDGE,"E2.20.42.0"),sQuery(id+"F0.wireOp",EDGE,"E2.20.43.0"),sQuery(id+"F0.wireOp",EDGE,"E2.20.44.0"),sQuery(id+"F0.wireOp",EDGE,"E2.21.0.0"),sQuery(id+"F0.wireOp",EDGE,"E2.21.1.0"),sQuery(id+"F0.wireOp",EDGE,"E2.21.2.0"),sQuery(id+"F0.wireOp",EDGE,"E2.21.3.0"),sQuery(id+"F0.wireOp",EDGE,"E2.21.4.0"),sQuery(id+"F0.wireOp",EDGE,"E2.21.5.0"),sQuery(id+"F0.wireOp",EDGE,"E2.21.6.0"),sQuery(id+"F0.wireOp",EDGE,"E2.21.7.0"),sQuery(id+"F0.wireOp",EDGE,"E2.21.8.0"),sQuery(id+"F0.wireOp",EDGE,"E2.21.9.0"),sQuery(id+"F0.wireOp",EDGE,"E2.21.10.0"),sQuery(id+"F0.wireOp",EDGE,"E2.21.11.0"),sQuery(id+"F0.wireOp",EDGE,"E2.21.12.0"),sQuery(id+"F0.wireOp",EDGE,"E2.21.13.0"),sQuery(id+"F0.wireOp",EDGE,"E2.21.14.0"),sQuery(id+"F0.wireOp",EDGE,"E2.21.15.0"),sQuery(id+"F0.wireOp",EDGE,"E2.21.16.0"),sQuery(id+"F0.wireOp",EDGE,"E2.21.17.0"),sQuery(id+"F0.wireOp",EDGE,"E2.21.18.0"),sQuery(id+"F0.wireOp",EDGE,"E2.21.19.0"),sQuery(id+"F0.wireOp",EDGE,"E2.21.20.0"),sQuery(id+"F0.wireOp",EDGE,"E2.21.21.0"),sQuery(id+"F0.wireOp",EDGE,"E2.21.22.0"),sQuery(id+"F0.wireOp",EDGE,"E2.21.23.0"),sQuery(id+"F0.wireOp",EDGE,"E2.21.24.0"),sQuery(id+"F0.wireOp",EDGE,"E2.21.25.0"),sQuery(id+"F0.wireOp",EDGE,"E2.21.26.0"),sQuery(id+"F0.wireOp",EDGE,"E2.21.27.0"),sQuery(id+"F0.wireOp",EDGE,"E2.21.28.0"),sQuery(id+"F0.wireOp",EDGE,"E2.21.29.0"),sQuery(id+"F0.wireOp",EDGE,"E2.21.30.0"),sQuery(id+"F0.wireOp",EDGE,"E2.21.31.0"),sQuery(id+"F0.wireOp",EDGE,"E2.21.32.0"),sQuery(id+"F0.wireOp",EDGE,"E2.21.33.0"),sQuery(id+"F0.wireOp",EDGE,"E2.21.34.0"),sQuery(id+"F0.wireOp",EDGE,"E2.21.35.0"),sQuery(id+"F0.wireOp",EDGE,"E2.21.36.0"),sQuery(id+"F0.wireOp",EDGE,"E2.21.37.0"),sQuery(id+"F0.wireOp",EDGE,"E2.21.38.0"),sQuery(id+"F0.wireOp",EDGE,"E2.21.39.0"),sQuery(id+"F0.wireOp",EDGE,"E2.21.40.0"),sQuery(id+"F0.wireOp",EDGE,"E2.21.41.0"),sQuery(id+"F0.wireOp",EDGE,"E2.21.42.0"),sQuery(id+"F0.wireOp",EDGE,"E2.21.43.0"),sQuery(id+"F0.wireOp",EDGE,"E2.21.44.0"),sQuery(id+"F0.wireOp",EDGE,"E2.22.0.0"),sQuery(id+"F0.wireOp",EDGE,"E2.22.1.0"),sQuery(id+"F0.wireOp",EDGE,"E2.22.2.0"),sQuery(id+"F0.wireOp",EDGE,"E2.22.3.0"),sQuery(id+"F0.wireOp",EDGE,"E2.22.4.0"),sQuery(id+"F0.wireOp",EDGE,"E2.22.5.0"),sQuery(id+"F0.wireOp",EDGE,"E2.22.6.0"),sQuery(id+"F0.wireOp",EDGE,"E2.22.7.0"),sQuery(id+"F0.wireOp",EDGE,"E2.22.8.0"),sQuery(id+"F0.wireOp",EDGE,"E2.22.9.0"),sQuery(id+"F0.wireOp",EDGE,"E2.22.10.0"),sQuery(id+"F0.wireOp",EDGE,"E2.22.11.0"),sQuery(id+"F0.wireOp",EDGE,"E2.22.12.0"),sQuery(id+"F0.wireOp",EDGE,"E2.22.13.0"),sQuery(id+"F0.wireOp",EDGE,"E2.22.14.0"),sQuery(id+"F0.wireOp",EDGE,"E2.22.15.0"),sQuery(id+"F0.wireOp",EDGE,"E2.22.16.0"),sQuery(id+"F0.wireOp",EDGE,"E2.22.17.0"),sQuery(id+"F0.wireOp",EDGE,"E2.22.18.0"),sQuery(id+"F0.wireOp",EDGE,"E2.22.19.0"),sQuery(id+"F0.wireOp",EDGE,"E2.22.20.0"),sQuery(id+"F0.wireOp",EDGE,"E2.22.21.0"),sQuery(id+"F0.wireOp",EDGE,"E2.22.22.0"),sQuery(id+"F0.wireOp",EDGE,"E2.22.23.0"),sQuery(id+"F0.wireOp",EDGE,"E2.22.24.0"),sQuery(id+"F0.wireOp",EDGE,"E2.22.25.0"),sQuery(id+"F0.wireOp",EDGE,"E2.22.26.0"),sQuery(id+"F0.wireOp",EDGE,"E2.22.27.0"),sQuery(id+"F0.wireOp",EDGE,"E2.22.28.0"),sQuery(id+"F0.wireOp",EDGE,"E2.22.29.0"),sQuery(id+"F0.wireOp",EDGE,"E2.22.30.0"),sQuery(id+"F0.wireOp",EDGE,"E2.22.31.0"),sQuery(id+"F0.wireOp",EDGE,"E2.22.32.0"),sQuery(id+"F0.wireOp",EDGE,"E2.22.33.0"),sQuery(id+"F0.wireOp",EDGE,"E2.22.34.0"),sQuery(id+"F0.wireOp",EDGE,"E2.22.35.0"),sQuery(id+"F0.wireOp",EDGE,"E2.22.36.0"),sQuery(id+"F0.wireOp",EDGE,"E2.22.37.0"),sQuery(id+"F0.wireOp",EDGE,"E2.22.38.0"),sQuery(id+"F0.wireOp",EDGE,"E2.22.39.0"),sQuery(id+"F0.wireOp",EDGE,"E2.22.40.0"),sQuery(id+"F0.wireOp",EDGE,"E2.22.41.0"),sQuery(id+"F0.wireOp",EDGE,"E2.22.42.0"),sQuery(id+"F0.wireOp",EDGE,"E2.22.43.0"),sQuery(id+"F0.wireOp",EDGE,"E2.22.44.0"),sQuery(id+"F0.wireOp",EDGE,"E2.23.0.0"),sQuery(id+"F0.wireOp",EDGE,"E2.23.1.0"),sQuery(id+"F0.wireOp",EDGE,"E2.23.2.0"),sQuery(id+"F0.wireOp",EDGE,"E2.23.3.0"),sQuery(id+"F0.wireOp",EDGE,"E2.23.4.0"),sQuery(id+"F0.wireOp",EDGE,"E2.23.5.0"),sQuery(id+"F0.wireOp",EDGE,"E2.23.6.0"),sQuery(id+"F0.wireOp",EDGE,"E2.23.7.0"),sQuery(id+"F0.wireOp",EDGE,"E2.23.8.0"),sQuery(id+"F0.wireOp",EDGE,"E2.23.9.0"),sQuery(id+"F0.wireOp",EDGE,"E2.23.10.0"),sQuery(id+"F0.wireOp",EDGE,"E2.23.11.0"),sQuery(id+"F0.wireOp",EDGE,"E2.23.12.0"),sQuery(id+"F0.wireOp",EDGE,"E2.23.13.0"),sQuery(id+"F0.wireOp",EDGE,"E2.23.14.0"),sQuery(id+"F0.wireOp",EDGE,"E2.23.15.0"),sQuery(id+"F0.wireOp",EDGE,"E2.23.16.0"),sQuery(id+"F0.wireOp",EDGE,"E2.23.17.0"),sQuery(id+"F0.wireOp",EDGE,"E2.23.18.0"),sQuery(id+"F0.wireOp",EDGE,"E2.23.19.0"),sQuery(id+"F0.wireOp",EDGE,"E2.23.20.0"),sQuery(id+"F0.wireOp",EDGE,"E2.23.21.0"),sQuery(id+"F0.wireOp",EDGE,"E2.23.22.0"),sQuery(id+"F0.wireOp",EDGE,"E2.23.23.0"),sQuery(id+"F0.wireOp",EDGE,"E2.23.24.0"),sQuery(id+"F0.wireOp",EDGE,"E2.23.25.0"),sQuery(id+"F0.wireOp",EDGE,"E2.23.26.0"),sQuery(id+"F0.wireOp",EDGE,"E2.23.27.0"),sQuery(id+"F0.wireOp",EDGE,"E2.23.28.0"),sQuery(id+"F0.wireOp",EDGE,"E2.23.29.0"),sQuery(id+"F0.wireOp",EDGE,"E2.23.30.0"),sQuery(id+"F0.wireOp",EDGE,"E2.23.31.0"),sQuery(id+"F0.wireOp",EDGE,"E2.23.32.0"),sQuery(id+"F0.wireOp",EDGE,"E2.23.33.0"),sQuery(id+"F0.wireOp",EDGE,"E2.23.34.0"),sQuery(id+"F0.wireOp",EDGE,"E2.23.35.0"),sQuery(id+"F0.wireOp",EDGE,"E2.23.36.0"),sQuery(id+"F0.wireOp",EDGE,"E2.23.37.0"),sQuery(id+"F0.wireOp",EDGE,"E2.23.38.0"),sQuery(id+"F0.wireOp",EDGE,"E2.23.39.0"),sQuery(id+"F0.wireOp",EDGE,"E2.23.40.0"),sQuery(id+"F0.wireOp",EDGE,"E2.23.41.0"),sQuery(id+"F0.wireOp",EDGE,"E2.23.42.0"),sQuery(id+"F0.wireOp",EDGE,"E2.23.43.0"),sQuery(id+"F0.wireOp",EDGE,"E2.23.44.0"),sQuery(id+"F0.wireOp",EDGE,"E2.24.0.0"),sQuery(id+"F0.wireOp",EDGE,"E2.24.1.0"),sQuery(id+"F0.wireOp",EDGE,"E2.24.2.0"),sQuery(id+"F0.wireOp",EDGE,"E2.24.3.0"),sQuery(id+"F0.wireOp",EDGE,"E2.24.4.0"),sQuery(id+"F0.wireOp",EDGE,"E2.24.5.0"),sQuery(id+"F0.wireOp",EDGE,"E2.24.6.0"),sQuery(id+"F0.wireOp",EDGE,"E2.24.7.0"),sQuery(id+"F0.wireOp",EDGE,"E2.24.8.0"),sQuery(id+"F0.wireOp",EDGE,"E2.24.9.0"),sQuery(id+"F0.wireOp",EDGE,"E2.24.10.0"),sQuery(id+"F0.wireOp",EDGE,"E2.24.11.0"),sQuery(id+"F0.wireOp",EDGE,"E2.24.12.0"),sQuery(id+"F0.wireOp",EDGE,"E2.24.13.0"),sQuery(id+"F0.wireOp",EDGE,"E2.24.14.0"),sQuery(id+"F0.wireOp",EDGE,"E2.24.15.0"),sQuery(id+"F0.wireOp",EDGE,"E2.24.16.0"),sQuery(id+"F0.wireOp",EDGE,"E2.24.17.0"),sQuery(id+"F0.wireOp",EDGE,"E2.24.18.0"),sQuery(id+"F0.wireOp",EDGE,"E2.24.19.0"),sQuery(id+"F0.wireOp",EDGE,"E2.24.20.0"),sQuery(id+"F0.wireOp",EDGE,"E2.24.21.0"),sQuery(id+"F0.wireOp",EDGE,"E2.24.22.0"),sQuery(id+"F0.wireOp",EDGE,"E2.24.23.0"),sQuery(id+"F0.wireOp",EDGE,"E2.24.24.0"),sQuery(id+"F0.wireOp",EDGE,"E2.24.25.0"),sQuery(id+"F0.wireOp",EDGE,"E2.24.26.0"),sQuery(id+"F0.wireOp",EDGE,"E2.24.27.0"),sQuery(id+"F0.wireOp",EDGE,"E2.24.28.0"),sQuery(id+"F0.wireOp",EDGE,"E2.24.29.0"),sQuery(id+"F0.wireOp",EDGE,"E2.24.30.0"),sQuery(id+"F0.wireOp",EDGE,"E2.24.31.0"),sQuery(id+"F0.wireOp",EDGE,"E2.24.32.0"),sQuery(id+"F0.wireOp",EDGE,"E2.24.33.0"),sQuery(id+"F0.wireOp",EDGE,"E2.24.34.0"),sQuery(id+"F0.wireOp",EDGE,"E2.24.35.0"),sQuery(id+"F0.wireOp",EDGE,"E2.24.36.0"),sQuery(id+"F0.wireOp",EDGE,"E2.24.37.0"),sQuery(id+"F0.wireOp",EDGE,"E2.24.38.0"),sQuery(id+"F0.wireOp",EDGE,"E2.24.39.0"),sQuery(id+"F0.wireOp",EDGE,"E2.24.40.0"),sQuery(id+"F0.wireOp",EDGE,"E2.24.41.0"),sQuery(id+"F0.wireOp",EDGE,"E2.24.42.0"),sQuery(id+"F0.wireOp",EDGE,"E2.24.43.0"),sQuery(id+"F0.wireOp",EDGE,"E2.24.44.0"),sQuery(id+"F0.wireOp",EDGE,"E2.25.0.0"),sQuery(id+"F0.wireOp",EDGE,"E2.25.1.0"),sQuery(id+"F0.wireOp",EDGE,"E2.25.2.0"),sQuery(id+"F0.wireOp",EDGE,"E2.25.3.0"),sQuery(id+"F0.wireOp",EDGE,"E2.25.4.0"),sQuery(id+"F0.wireOp",EDGE,"E2.25.5.0"),sQuery(id+"F0.wireOp",EDGE,"E2.25.6.0"),sQuery(id+"F0.wireOp",EDGE,"E2.25.7.0"),sQuery(id+"F0.wireOp",EDGE,"E2.25.8.0"),sQuery(id+"F0.wireOp",EDGE,"E2.25.9.0"),sQuery(id+"F0.wireOp",EDGE,"E2.25.10.0"),sQuery(id+"F0.wireOp",EDGE,"E2.25.11.0"),sQuery(id+"F0.wireOp",EDGE,"E2.25.12.0"),sQuery(id+"F0.wireOp",EDGE,"E2.25.13.0"),sQuery(id+"F0.wireOp",EDGE,"E2.25.14.0"),sQuery(id+"F0.wireOp",EDGE,"E2.25.15.0"),sQuery(id+"F0.wireOp",EDGE,"E2.25.16.0"),sQuery(id+"F0.wireOp",EDGE,"E2.25.17.0"),sQuery(id+"F0.wireOp",EDGE,"E2.25.18.0"),sQuery(id+"F0.wireOp",EDGE,"E2.25.19.0"),sQuery(id+"F0.wireOp",EDGE,"E2.25.20.0"),sQuery(id+"F0.wireOp",EDGE,"E2.25.21.0"),sQuery(id+"F0.wireOp",EDGE,"E2.25.22.0"),sQuery(id+"F0.wireOp",EDGE,"E2.25.23.0"),sQuery(id+"F0.wireOp",EDGE,"E2.25.24.0"),sQuery(id+"F0.wireOp",EDGE,"E2.25.25.0"),sQuery(id+"F0.wireOp",EDGE,"E2.25.26.0"),sQuery(id+"F0.wireOp",EDGE,"E2.25.27.0"),sQuery(id+"F0.wireOp",EDGE,"E2.25.28.0"),sQuery(id+"F0.wireOp",EDGE,"E2.25.29.0"),sQuery(id+"F0.wireOp",EDGE,"E2.25.30.0"),sQuery(id+"F0.wireOp",EDGE,"E2.25.31.0"),sQuery(id+"F0.wireOp",EDGE,"E2.25.32.0"),sQuery(id+"F0.wireOp",EDGE,"E2.25.33.0"),sQuery(id+"F0.wireOp",EDGE,"E2.25.34.0"),sQuery(id+"F0.wireOp",EDGE,"E2.25.35.0"),sQuery(id+"F0.wireOp",EDGE,"E2.25.36.0"),sQuery(id+"F0.wireOp",EDGE,"E2.25.37.0"),sQuery(id+"F0.wireOp",EDGE,"E2.25.38.0"),sQuery(id+"F0.wireOp",EDGE,"E2.25.39.0"),sQuery(id+"F0.wireOp",EDGE,"E2.25.40.0"),sQuery(id+"F0.wireOp",EDGE,"E2.25.41.0"),sQuery(id+"F0.wireOp",EDGE,"E2.25.42.0"),sQuery(id+"F0.wireOp",EDGE,"E2.25.43.0"),sQuery(id+"F0.wireOp",EDGE,"E2.25.44.0"),sQuery(id+"F0.wireOp",EDGE,"E2.26.0.0"),sQuery(id+"F0.wireOp",EDGE,"E2.26.1.0"),sQuery(id+"F0.wireOp",EDGE,"E2.26.2.0"),sQuery(id+"F0.wireOp",EDGE,"E2.26.3.0"),sQuery(id+"F0.wireOp",EDGE,"E2.26.4.0"),sQuery(id+"F0.wireOp",EDGE,"E2.26.5.0"),sQuery(id+"F0.wireOp",EDGE,"E2.26.6.0"),sQuery(id+"F0.wireOp",EDGE,"E2.26.7.0"),sQuery(id+"F0.wireOp",EDGE,"E2.26.8.0"),sQuery(id+"F0.wireOp",EDGE,"E2.26.9.0"),sQuery(id+"F0.wireOp",EDGE,"E2.26.10.0"),sQuery(id+"F0.wireOp",EDGE,"E2.26.11.0"),sQuery(id+"F0.wireOp",EDGE,"E2.26.12.0"),sQuery(id+"F0.wireOp",EDGE,"E2.26.13.0"),sQuery(id+"F0.wireOp",EDGE,"E2.26.14.0"),sQuery(id+"F0.wireOp",EDGE,"E2.26.15.0"),sQuery(id+"F0.wireOp",EDGE,"E2.26.16.0"),sQuery(id+"F0.wireOp",EDGE,"E2.26.17.0"),sQuery(id+"F0.wireOp",EDGE,"E2.26.18.0"),sQuery(id+"F0.wireOp",EDGE,"E2.26.19.0"),sQuery(id+"F0.wireOp",EDGE,"E2.26.20.0"),sQuery(id+"F0.wireOp",EDGE,"E2.26.21.0"),sQuery(id+"F0.wireOp",EDGE,"E2.26.22.0"),sQuery(id+"F0.wireOp",EDGE,"E2.26.23.0"),sQuery(id+"F0.wireOp",EDGE,"E2.26.24.0"),sQuery(id+"F0.wireOp",EDGE,"E2.26.25.0"),sQuery(id+"F0.wireOp",EDGE,"E2.26.26.0"),sQuery(id+"F0.wireOp",EDGE,"E2.26.27.0"),sQuery(id+"F0.wireOp",EDGE,"E2.26.28.0"),sQuery(id+"F0.wireOp",EDGE,"E2.26.29.0"),sQuery(id+"F0.wireOp",EDGE,"E2.26.30.0"),sQuery(id+"F0.wireOp",EDGE,"E2.26.31.0"),sQuery(id+"F0.wireOp",EDGE,"E2.26.32.0"),sQuery(id+"F0.wireOp",EDGE,"E2.26.33.0"),sQuery(id+"F0.wireOp",EDGE,"E2.26.34.0"),sQuery(id+"F0.wireOp",EDGE,"E2.26.35.0"),sQuery(id+"F0.wireOp",EDGE,"E2.26.36.0"),sQuery(id+"F0.wireOp",EDGE,"E2.26.37.0"),sQuery(id+"F0.wireOp",EDGE,"E2.26.38.0"),sQuery(id+"F0.wireOp",EDGE,"E2.26.39.0"),sQuery(id+"F0.wireOp",EDGE,"E2.26.40.0"),sQuery(id+"F0.wireOp",EDGE,"E2.26.41.0"),sQuery(id+"F0.wireOp",EDGE,"E2.26.42.0"),sQuery(id+"F0.wireOp",EDGE,"E2.26.43.0"),sQuery(id+"F0.wireOp",EDGE,"E2.26.44.0"),sQuery(id+"F0.wireOp",EDGE,"E2.27.0.0"),sQuery(id+"F0.wireOp",EDGE,"E2.27.1.0"),sQuery(id+"F0.wireOp",EDGE,"E2.27.2.0"),sQuery(id+"F0.wireOp",EDGE,"E2.27.3.0"),sQuery(id+"F0.wireOp",EDGE,"E2.27.4.0"),sQuery(id+"F0.wireOp",EDGE,"E2.27.5.0"),sQuery(id+"F0.wireOp",EDGE,"E2.27.6.0"),sQuery(id+"F0.wireOp",EDGE,"E2.27.7.0"),sQuery(id+"F0.wireOp",EDGE,"E2.27.8.0"),sQuery(id+"F0.wireOp",EDGE,"E2.27.9.0"),sQuery(id+"F0.wireOp",EDGE,"E2.27.10.0"),sQuery(id+"F0.wireOp",EDGE,"E2.27.11.0"),sQuery(id+"F0.wireOp",EDGE,"E2.27.12.0"),sQuery(id+"F0.wireOp",EDGE,"E2.27.13.0"),sQuery(id+"F0.wireOp",EDGE,"E2.27.14.0"),sQuery(id+"F0.wireOp",EDGE,"E2.27.15.0"),sQuery(id+"F0.wireOp",EDGE,"E2.27.16.0"),sQuery(id+"F0.wireOp",EDGE,"E2.27.17.0"),sQuery(id+"F0.wireOp",EDGE,"E2.27.18.0"),sQuery(id+"F0.wireOp",EDGE,"E2.27.19.0"),sQuery(id+"F0.wireOp",EDGE,"E2.27.20.0"),sQuery(id+"F0.wireOp",EDGE,"E2.27.21.0"),sQuery(id+"F0.wireOp",EDGE,"E2.27.22.0"),sQuery(id+"F0.wireOp",EDGE,"E2.27.23.0"),sQuery(id+"F0.wireOp",EDGE,"E2.27.24.0"),sQuery(id+"F0.wireOp",EDGE,"E2.27.25.0"),sQuery(id+"F0.wireOp",EDGE,"E2.27.26.0"),sQuery(id+"F0.wireOp",EDGE,"E2.27.27.0"),sQuery(id+"F0.wireOp",EDGE,"E2.27.28.0"),sQuery(id+"F0.wireOp",EDGE,"E2.27.29.0"),sQuery(id+"F0.wireOp",EDGE,"E2.27.30.0"),sQuery(id+"F0.wireOp",EDGE,"E2.27.31.0"),sQuery(id+"F0.wireOp",EDGE,"E2.27.32.0"),sQuery(id+"F0.wireOp",EDGE,"E2.27.33.0"),sQuery(id+"F0.wireOp",EDGE,"E2.27.34.0"),sQuery(id+"F0.wireOp",EDGE,"E2.27.35.0"),sQuery(id+"F0.wireOp",EDGE,"E2.27.36.0"),sQuery(id+"F0.wireOp",EDGE,"E2.27.37.0"),sQuery(id+"F0.wireOp",EDGE,"E2.27.38.0"),sQuery(id+"F0.wireOp",EDGE,"E2.27.39.0"),sQuery(id+"F0.wireOp",EDGE,"E2.27.40.0"),sQuery(id+"F0.wireOp",EDGE,"E2.27.41.0"),sQuery(id+"F0.wireOp",EDGE,"E2.27.42.0"),sQuery(id+"F0.wireOp",EDGE,"E2.27.43.0"),sQuery(id+"F0.wireOp",EDGE,"E2.27.44.0"),sQuery(id+"F0.wireOp",EDGE,"E2.28.0.0"),sQuery(id+"F0.wireOp",EDGE,"E2.28.1.0"),sQuery(id+"F0.wireOp",EDGE,"E2.28.2.0"),sQuery(id+"F0.wireOp",EDGE,"E2.28.3.0"),sQuery(id+"F0.wireOp",EDGE,"E2.28.4.0"),sQuery(id+"F0.wireOp",EDGE,"E2.28.5.0"),sQuery(id+"F0.wireOp",EDGE,"E2.28.6.0"),sQuery(id+"F0.wireOp",EDGE,"E2.28.7.0"),sQuery(id+"F0.wireOp",EDGE,"E2.28.8.0"),sQuery(id+"F0.wireOp",EDGE,"E2.28.9.0"),sQuery(id+"F0.wireOp",EDGE,"E2.28.10.0"),sQuery(id+"F0.wireOp",EDGE,"E2.28.11.0"),sQuery(id+"F0.wireOp",EDGE,"E2.28.12.0"),sQuery(id+"F0.wireOp",EDGE,"E2.28.13.0"),sQuery(id+"F0.wireOp",EDGE,"E2.28.14.0"),sQuery(id+"F0.wireOp",EDGE,"E2.28.15.0"),sQuery(id+"F0.wireOp",EDGE,"E2.28.16.0"),sQuery(id+"F0.wireOp",EDGE,"E2.28.17.0"),sQuery(id+"F0.wireOp",EDGE,"E2.28.18.0"),sQuery(id+"F0.wireOp",EDGE,"E2.28.19.0"),sQuery(id+"F0.wireOp",EDGE,"E2.28.20.0"),sQuery(id+"F0.wireOp",EDGE,"E2.28.21.0"),sQuery(id+"F0.wireOp",EDGE,"E2.28.22.0"),sQuery(id+"F0.wireOp",EDGE,"E2.28.23.0"),sQuery(id+"F0.wireOp",EDGE,"E2.28.24.0"),sQuery(id+"F0.wireOp",EDGE,"E2.28.25.0"),sQuery(id+"F0.wireOp",EDGE,"E2.28.26.0"),sQuery(id+"F0.wireOp",EDGE,"E2.28.27.0"),sQuery(id+"F0.wireOp",EDGE,"E2.28.28.0"),sQuery(id+"F0.wireOp",EDGE,"E2.28.29.0"),sQuery(id+"F0.wireOp",EDGE,"E2.28.30.0"),sQuery(id+"F0.wireOp",EDGE,"E2.28.31.0"),sQuery(id+"F0.wireOp",EDGE,"E2.28.32.0"),sQuery(id+"F0.wireOp",EDGE,"E2.28.33.0"),sQuery(id+"F0.wireOp",EDGE,"E2.28.34.0"),sQuery(id+"F0.wireOp",EDGE,"E2.28.35.0"),sQuery(id+"F0.wireOp",EDGE,"E2.28.36.0"),sQuery(id+"F0.wireOp",EDGE,"E2.28.37.0"),sQuery(id+"F0.wireOp",EDGE,"E2.28.38.0"),sQuery(id+"F0.wireOp",EDGE,"E2.28.39.0"),sQuery(id+"F0.wireOp",EDGE,"E2.28.40.0"),sQuery(id+"F0.wireOp",EDGE,"E2.28.41.0"),sQuery(id+"F0.wireOp",EDGE,"E2.28.42.0"),sQuery(id+"F0.wireOp",EDGE,"E2.28.43.0"),sQuery(id+"F0.wireOp",EDGE,"E2.28.44.0"),sQuery(id+"F0.wireOp",EDGE,"E2.29.0.0"),sQuery(id+"F0.wireOp",EDGE,"E2.29.1.0"),sQuery(id+"F0.wireOp",EDGE,"E2.29.2.0"),sQuery(id+"F0.wireOp",EDGE,"E2.29.3.0"),sQuery(id+"F0.wireOp",EDGE,"E2.29.4.0"),sQuery(id+"F0.wireOp",EDGE,"E2.29.5.0"),sQuery(id+"F0.wireOp",EDGE,"E2.29.6.0"),sQuery(id+"F0.wireOp",EDGE,"E2.29.7.0"),sQuery(id+"F0.wireOp",EDGE,"E2.29.8.0"),sQuery(id+"F0.wireOp",EDGE,"E2.29.9.0"),sQuery(id+"F0.wireOp",EDGE,"E2.29.10.0"),sQuery(id+"F0.wireOp",EDGE,"E2.29.11.0"),sQuery(id+"F0.wireOp",EDGE,"E2.29.12.0"),sQuery(id+"F0.wireOp",EDGE,"E2.29.13.0"),sQuery(id+"F0.wireOp",EDGE,"E2.29.14.0"),sQuery(id+"F0.wireOp",EDGE,"E2.29.15.0"),sQuery(id+"F0.wireOp",EDGE,"E2.29.16.0"),sQuery(id+"F0.wireOp",EDGE,"E2.29.17.0"),sQuery(id+"F0.wireOp",EDGE,"E2.29.18.0"),sQuery(id+"F0.wireOp",EDGE,"E2.29.19.0"),sQuery(id+"F0.wireOp",EDGE,"E2.29.20.0"),sQuery(id+"F0.wireOp",EDGE,"E2.29.21.0"),sQuery(id+"F0.wireOp",EDGE,"E2.29.22.0"),sQuery(id+"F0.wireOp",EDGE,"E2.29.23.0"),sQuery(id+"F0.wireOp",EDGE,"E2.29.24.0"),sQuery(id+"F0.wireOp",EDGE,"E2.29.25.0"),sQuery(id+"F0.wireOp",EDGE,"E2.29.26.0"),sQuery(id+"F0.wireOp",EDGE,"E2.29.27.0"),sQuery(id+"F0.wireOp",EDGE,"E2.29.28.0"),sQuery(id+"F0.wireOp",EDGE,"E2.29.29.0"),sQuery(id+"F0.wireOp",EDGE,"E2.29.30.0"),sQuery(id+"F0.wireOp",EDGE,"E2.29.31.0"),sQuery(id+"F0.wireOp",EDGE,"E2.29.32.0"),sQuery(id+"F0.wireOp",EDGE,"E2.29.33.0"),sQuery(id+"F0.wireOp",EDGE,"E2.29.34.0"),sQuery(id+"F0.wireOp",EDGE,"E2.29.35.0"),sQuery(id+"F0.wireOp",EDGE,"E2.29.36.0"),sQuery(id+"F0.wireOp",EDGE,"E2.29.37.0"),sQuery(id+"F0.wireOp",EDGE,"E2.29.38.0"),sQuery(id+"F0.wireOp",EDGE,"E2.29.39.0"),sQuery(id+"F0.wireOp",EDGE,"E2.29.40.0"),sQuery(id+"F0.wireOp",EDGE,"E2.29.41.0"),sQuery(id+"F0.wireOp",EDGE,"E2.29.42.0"),sQuery(id+"F0.wireOp",EDGE,"E2.29.43.0"),sQuery(id+"F0.wireOp",EDGE,"E2.29.44.0"),sQuery(id+"F0.wireOp",EDGE,"E2.30.0.0"),sQuery(id+"F0.wireOp",EDGE,"E2.30.1.0"),sQuery(id+"F0.wireOp",EDGE,"E2.30.2.0"),sQuery(id+"F0.wireOp",EDGE,"E2.30.3.0"),sQuery(id+"F0.wireOp",EDGE,"E2.30.4.0"),sQuery(id+"F0.wireOp",EDGE,"E2.30.5.0"),sQuery(id+"F0.wireOp",EDGE,"E2.30.6.0"),sQuery(id+"F0.wireOp",EDGE,"E2.30.7.0"),sQuery(id+"F0.wireOp",EDGE,"E2.30.8.0"),sQuery(id+"F0.wireOp",EDGE,"E2.30.9.0"),sQuery(id+"F0.wireOp",EDGE,"E2.30.10.0"),sQuery(id+"F0.wireOp",EDGE,"E2.30.11.0"),sQuery(id+"F0.wireOp",EDGE,"E2.30.12.0"),sQuery(id+"F0.wireOp",EDGE,"E2.30.13.0"),sQuery(id+"F0.wireOp",EDGE,"E2.30.14.0"),sQuery(id+"F0.wireOp",EDGE,"E2.30.15.0"),sQuery(id+"F0.wireOp",EDGE,"E2.30.16.0"),sQuery(id+"F0.wireOp",EDGE,"E2.30.17.0"),sQuery(id+"F0.wireOp",EDGE,"E2.30.18.0"),sQuery(id+"F0.wireOp",EDGE,"E2.30.19.0"),sQuery(id+"F0.wireOp",EDGE,"E2.30.20.0"),sQuery(id+"F0.wireOp",EDGE,"E2.30.21.0"),sQuery(id+"F0.wireOp",EDGE,"E2.30.22.0"),sQuery(id+"F0.wireOp",EDGE,"E2.30.23.0"),sQuery(id+"F0.wireOp",EDGE,"E2.30.24.0"),sQuery(id+"F0.wireOp",EDGE,"E2.30.25.0"),sQuery(id+"F0.wireOp",EDGE,"E2.30.26.0"),sQuery(id+"F0.wireOp",EDGE,"E2.30.27.0"),sQuery(id+"F0.wireOp",EDGE,"E2.30.28.0"),sQuery(id+"F0.wireOp",EDGE,"E2.30.29.0"),sQuery(id+"F0.wireOp",EDGE,"E2.30.30.0"),sQuery(id+"F0.wireOp",EDGE,"E2.30.31.0"),sQuery(id+"F0.wireOp",EDGE,"E2.30.32.0"),sQuery(id+"F0.wireOp",EDGE,"E2.30.33.0"),sQuery(id+"F0.wireOp",EDGE,"E2.30.34.0"),sQuery(id+"F0.wireOp",EDGE,"E2.30.35.0"),sQuery(id+"F0.wireOp",EDGE,"E2.30.36.0"),sQuery(id+"F0.wireOp",EDGE,"E2.30.37.0"),sQuery(id+"F0.wireOp",EDGE,"E2.30.38.0"),sQuery(id+"F0.wireOp",EDGE,"E2.30.39.0"),sQuery(id+"F0.wireOp",EDGE,"E2.30.40.0"),sQuery(id+"F0.wireOp",EDGE,"E2.30.41.0"),sQuery(id+"F0.wireOp",EDGE,"E2.30.42.0"),sQuery(id+"F0.wireOp",EDGE,"E2.30.43.0"),sQuery(id+"F0.wireOp",EDGE,"E2.30.44.0"),sQuery(id+"F0.wireOp",EDGE,"E2.31.0.0"),sQuery(id+"F0.wireOp",EDGE,"E2.31.1.0"),sQuery(id+"F0.wireOp",EDGE,"E2.31.2.0"),sQuery(id+"F0.wireOp",EDGE,"E2.31.3.0"),sQuery(id+"F0.wireOp",EDGE,"E2.31.4.0"),sQuery(id+"F0.wireOp",EDGE,"E2.31.5.0"),sQuery(id+"F0.wireOp",EDGE,"E2.31.6.0"),sQuery(id+"F0.wireOp",EDGE,"E2.31.7.0"),sQuery(id+"F0.wireOp",EDGE,"E2.31.8.0"),sQuery(id+"F0.wireOp",EDGE,"E2.31.9.0"),sQuery(id+"F0.wireOp",EDGE,"E2.31.10.0"),sQuery(id+"F0.wireOp",EDGE,"E2.31.11.0"),sQuery(id+"F0.wireOp",EDGE,"E2.31.12.0"),sQuery(id+"F0.wireOp",EDGE,"E2.31.13.0"),sQuery(id+"F0.wireOp",EDGE,"E2.31.14.0"),sQuery(id+"F0.wireOp",EDGE,"E2.31.15.0"),sQuery(id+"F0.wireOp",EDGE,"E2.31.16.0"),sQuery(id+"F0.wireOp",EDGE,"E2.31.17.0"),sQuery(id+"F0.wireOp",EDGE,"E2.31.18.0"),sQuery(id+"F0.wireOp",EDGE,"E2.31.19.0"),sQuery(id+"F0.wireOp",EDGE,"E2.31.20.0"),sQuery(id+"F0.wireOp",EDGE,"E2.31.21.0"),sQuery(id+"F0.wireOp",EDGE,"E2.31.22.0"),sQuery(id+"F0.wireOp",EDGE,"E2.31.23.0"),sQuery(id+"F0.wireOp",EDGE,"E2.31.24.0"),sQuery(id+"F0.wireOp",EDGE,"E2.31.25.0"),sQuery(id+"F0.wireOp",EDGE,"E2.31.26.0"),sQuery(id+"F0.wireOp",EDGE,"E2.31.27.0"),sQuery(id+"F0.wireOp",EDGE,"E2.31.28.0"),sQuery(id+"F0.wireOp",EDGE,"E2.31.29.0"),sQuery(id+"F0.wireOp",EDGE,"E2.31.30.0"),sQuery(id+"F0.wireOp",EDGE,"E2.31.31.0"),sQuery(id+"F0.wireOp",EDGE,"E2.31.32.0"),sQuery(id+"F0.wireOp",EDGE,"E2.31.33.0"),sQuery(id+"F0.wireOp",EDGE,"E2.31.34.0"),sQuery(id+"F0.wireOp",EDGE,"E2.31.35.0"),sQuery(id+"F0.wireOp",EDGE,"E2.31.36.0"),sQuery(id+"F0.wireOp",EDGE,"E2.31.37.0"),sQuery(id+"F0.wireOp",EDGE,"E2.31.38.0"),sQuery(id+"F0.wireOp",EDGE,"E2.31.39.0"),sQuery(id+"F0.wireOp",EDGE,"E2.31.40.0"),sQuery(id+"F0.wireOp",EDGE,"E2.31.41.0"),sQuery(id+"F0.wireOp",EDGE,"E2.31.42.0"),sQuery(id+"F0.wireOp",EDGE,"E2.31.43.0"),sQuery(id+"F0.wireOp",EDGE,"E2.31.44.0"),sQuery(id+"F0.wireOp",EDGE,"E2.32.0.0"),sQuery(id+"F0.wireOp",EDGE,"E2.32.1.0"),sQuery(id+"F0.wireOp",EDGE,"E2.32.2.0"),sQuery(id+"F0.wireOp",EDGE,"E2.32.3.0"),sQuery(id+"F0.wireOp",EDGE,"E2.32.4.0"),sQuery(id+"F0.wireOp",EDGE,"E2.32.5.0"),sQuery(id+"F0.wireOp",EDGE,"E2.32.6.0"),sQuery(id+"F0.wireOp",EDGE,"E2.32.7.0"),sQuery(id+"F0.wireOp",EDGE,"E2.32.8.0"),sQuery(id+"F0.wireOp",EDGE,"E2.32.9.0"),sQuery(id+"F0.wireOp",EDGE,"E2.32.10.0"),sQuery(id+"F0.wireOp",EDGE,"E2.32.11.0"),sQuery(id+"F0.wireOp",EDGE,"E2.32.12.0"),sQuery(id+"F0.wireOp",EDGE,"E2.32.13.0"),sQuery(id+"F0.wireOp",EDGE,"E2.32.14.0"),sQuery(id+"F0.wireOp",EDGE,"E2.32.15.0"),sQuery(id+"F0.wireOp",EDGE,"E2.32.16.0"),sQuery(id+"F0.wireOp",EDGE,"E2.32.17.0"),sQuery(id+"F0.wireOp",EDGE,"E2.32.18.0"),sQuery(id+"F0.wireOp",EDGE,"E2.32.19.0"),sQuery(id+"F0.wireOp",EDGE,"E2.32.20.0"),sQuery(id+"F0.wireOp",EDGE,"E2.32.21.0"),sQuery(id+"F0.wireOp",EDGE,"E2.32.22.0"),sQuery(id+"F0.wireOp",EDGE,"E2.32.23.0"),sQuery(id+"F0.wireOp",EDGE,"E2.32.24.0"),sQuery(id+"F0.wireOp",EDGE,"E2.32.25.0"),sQuery(id+"F0.wireOp",EDGE,"E2.32.26.0"),sQuery(id+"F0.wireOp",EDGE,"E2.32.27.0"),sQuery(id+"F0.wireOp",EDGE,"E2.32.28.0"),sQuery(id+"F0.wireOp",EDGE,"E2.32.29.0"),sQuery(id+"F0.wireOp",EDGE,"E2.32.30.0"),sQuery(id+"F0.wireOp",EDGE,"E2.32.31.0"),sQuery(id+"F0.wireOp",EDGE,"E2.32.32.0"),sQuery(id+"F0.wireOp",EDGE,"E2.32.33.0"),sQuery(id+"F0.wireOp",EDGE,"E2.32.34.0"),sQuery(id+"F0.wireOp",EDGE,"E2.32.35.0"),sQuery(id+"F0.wireOp",EDGE,"E2.32.36.0"),sQuery(id+"F0.wireOp",EDGE,"E2.32.37.0"),sQuery(id+"F0.wireOp",EDGE,"E2.32.38.0"),sQuery(id+"F0.wireOp",EDGE,"E2.32.39.0"),sQuery(id+"F0.wireOp",EDGE,"E2.32.40.0"),sQuery(id+"F0.wireOp",EDGE,"E2.32.41.0"),sQuery(id+"F0.wireOp",EDGE,"E2.32.42.0"),sQuery(id+"F0.wireOp",EDGE,"E2.32.43.0"),sQuery(id+"F0.wireOp",EDGE,"E2.32.44.0"),sQuery(id+"F0.wireOp",EDGE,"E2.33.0.0"),sQuery(id+"F0.wireOp",EDGE,"E2.33.1.0"),sQuery(id+"F0.wireOp",EDGE,"E2.33.2.0"),sQuery(id+"F0.wireOp",EDGE,"E2.33.3.0"),sQuery(id+"F0.wireOp",EDGE,"E2.33.4.0"),sQuery(id+"F0.wireOp",EDGE,"E2.33.5.0"),sQuery(id+"F0.wireOp",EDGE,"E2.33.6.0"),sQuery(id+"F0.wireOp",EDGE,"E2.33.7.0"),sQuery(id+"F0.wireOp",EDGE,"E2.33.8.0"),sQuery(id+"F0.wireOp",EDGE,"E2.33.9.0"),sQuery(id+"F0.wireOp",EDGE,"E2.33.10.0"),sQuery(id+"F0.wireOp",EDGE,"E2.33.11.0"),sQuery(id+"F0.wireOp",EDGE,"E2.33.12.0"),sQuery(id+"F0.wireOp",EDGE,"E2.33.13.0"),sQuery(id+"F0.wireOp",EDGE,"E2.33.14.0"),sQuery(id+"F0.wireOp",EDGE,"E2.33.15.0"),sQuery(id+"F0.wireOp",EDGE,"E2.33.16.0"),sQuery(id+"F0.wireOp",EDGE,"E2.33.17.0"),sQuery(id+"F0.wireOp",EDGE,"E2.33.18.0"),sQuery(id+"F0.wireOp",EDGE,"E2.33.19.0"),sQuery(id+"F0.wireOp",EDGE,"E2.33.20.0"),sQuery(id+"F0.wireOp",EDGE,"E2.33.21.0"),sQuery(id+"F0.wireOp",EDGE,"E2.33.22.0"),sQuery(id+"F0.wireOp",EDGE,"E2.33.23.0"),sQuery(id+"F0.wireOp",EDGE,"E2.33.24.0"),sQuery(id+"F0.wireOp",EDGE,"E2.33.25.0"),sQuery(id+"F0.wireOp",EDGE,"E2.33.26.0"),sQuery(id+"F0.wireOp",EDGE,"E2.33.27.0"),sQuery(id+"F0.wireOp",EDGE,"E2.33.28.0"),sQuery(id+"F0.wireOp",EDGE,"E2.33.29.0"),sQuery(id+"F0.wireOp",EDGE,"E2.33.30.0"),sQuery(id+"F0.wireOp",EDGE,"E2.33.31.0"),sQuery(id+"F0.wireOp",EDGE,"E2.33.32.0"),sQuery(id+"F0.wireOp",EDGE,"E2.33.33.0"),sQuery(id+"F0.wireOp",EDGE,"E2.33.34.0"),sQuery(id+"F0.wireOp",EDGE,"E2.33.35.0"),sQuery(id+"F0.wireOp",EDGE,"E2.33.36.0"),sQuery(id+"F0.wireOp",EDGE,"E2.33.37.0"),sQuery(id+"F0.wireOp",EDGE,"E2.33.38.0"),sQuery(id+"F0.wireOp",EDGE,"E2.33.39.0"),sQuery(id+"F0.wireOp",EDGE,"E2.33.40.0"),sQuery(id+"F0.wireOp",EDGE,"E2.33.41.0"),sQuery(id+"F0.wireOp",EDGE,"E2.33.42.0"),sQuery(id+"F0.wireOp",EDGE,"E2.33.43.0"),sQuery(id+"F0.wireOp",EDGE,"E2.33.44.0"),sQuery(id+"F0.wireOp",EDGE,"E2.34.0.0"),sQuery(id+"F0.wireOp",EDGE,"E2.34.1.0"),sQuery(id+"F0.wireOp",EDGE,"E2.34.2.0"),sQuery(id+"F0.wireOp",EDGE,"E2.34.3.0"),sQuery(id+"F0.wireOp",EDGE,"E2.34.4.0"),sQuery(id+"F0.wireOp",EDGE,"E2.34.5.0"),sQuery(id+"F0.wireOp",EDGE,"E2.34.6.0"),sQuery(id+"F0.wireOp",EDGE,"E2.34.7.0"),sQuery(id+"F0.wireOp",EDGE,"E2.34.8.0"),sQuery(id+"F0.wireOp",EDGE,"E2.34.9.0"),sQuery(id+"F0.wireOp",EDGE,"E2.34.10.0"),sQuery(id+"F0.wireOp",EDGE,"E2.34.11.0"),sQuery(id+"F0.wireOp",EDGE,"E2.34.12.0"),sQuery(id+"F0.wireOp",EDGE,"E2.34.13.0"),sQuery(id+"F0.wireOp",EDGE,"E2.34.14.0"),sQuery(id+"F0.wireOp",EDGE,"E2.34.15.0"),sQuery(id+"F0.wireOp",EDGE,"E2.34.16.0"),sQuery(id+"F0.wireOp",EDGE,"E2.34.17.0"),sQuery(id+"F0.wireOp",EDGE,"E2.34.18.0"),sQuery(id+"F0.wireOp",EDGE,"E2.34.19.0"),sQuery(id+"F0.wireOp",EDGE,"E2.34.20.0"),sQuery(id+"F0.wireOp",EDGE,"E2.34.21.0"),sQuery(id+"F0.wireOp",EDGE,"E2.34.22.0"),sQuery(id+"F0.wireOp",EDGE,"E2.34.23.0"),sQuery(id+"F0.wireOp",EDGE,"E2.34.24.0"),sQuery(id+"F0.wireOp",EDGE,"E2.34.25.0"),sQuery(id+"F0.wireOp",EDGE,"E2.34.26.0"),sQuery(id+"F0.wireOp",EDGE,"E2.34.27.0"),sQuery(id+"F0.wireOp",EDGE,"E2.34.28.0"),sQuery(id+"F0.wireOp",EDGE,"E2.34.29.0"),sQuery(id+"F0.wireOp",EDGE,"E2.34.30.0"),sQuery(id+"F0.wireOp",EDGE,"E2.34.31.0"),sQuery(id+"F0.wireOp",EDGE,"E2.34.32.0"),sQuery(id+"F0.wireOp",EDGE,"E2.34.33.0"),sQuery(id+"F0.wireOp",EDGE,"E2.34.34.0"),sQuery(id+"F0.wireOp",EDGE,"E2.34.35.0"),sQuery(id+"F0.wireOp",EDGE,"E2.34.36.0"),sQuery(id+"F0.wireOp",EDGE,"E2.34.37.0"),sQuery(id+"F0.wireOp",EDGE,"E2.34.38.0"),sQuery(id+"F0.wireOp",EDGE,"E2.34.39.0"),sQuery(id+"F0.wireOp",EDGE,"E2.34.40.0"),sQuery(id+"F0.wireOp",EDGE,"E2.34.41.0"),sQuery(id+"F0.wireOp",EDGE,"E2.34.42.0"),sQuery(id+"F0.wireOp",EDGE,"E2.34.43.0"),sQuery(id+"F0.wireOp",EDGE,"E2.34.44.0"),sQuery(id+"F0.wireOp",EDGE,"E2.35.0.0"),sQuery(id+"F0.wireOp",EDGE,"E2.35.1.0"),sQuery(id+"F0.wireOp",EDGE,"E2.35.2.0"),sQuery(id+"F0.wireOp",EDGE,"E2.35.3.0"),sQuery(id+"F0.wireOp",EDGE,"E2.35.4.0"),sQuery(id+"F0.wireOp",EDGE,"E2.35.5.0"),sQuery(id+"F0.wireOp",EDGE,"E2.35.6.0"),sQuery(id+"F0.wireOp",EDGE,"E2.35.7.0"),sQuery(id+"F0.wireOp",EDGE,"E2.35.8.0"),sQuery(id+"F0.wireOp",EDGE,"E2.35.9.0"),sQuery(id+"F0.wireOp",EDGE,"E2.35.10.0"),sQuery(id+"F0.wireOp",EDGE,"E2.35.11.0"),sQuery(id+"F0.wireOp",EDGE,"E2.35.12.0"),sQuery(id+"F0.wireOp",EDGE,"E2.35.13.0"),sQuery(id+"F0.wireOp",EDGE,"E2.35.14.0"),sQuery(id+"F0.wireOp",EDGE,"E2.35.15.0"),sQuery(id+"F0.wireOp",EDGE,"E2.35.16.0"),sQuery(id+"F0.wireOp",EDGE,"E2.35.17.0"),sQuery(id+"F0.wireOp",EDGE,"E2.35.18.0"),sQuery(id+"F0.wireOp",EDGE,"E2.35.19.0"),sQuery(id+"F0.wireOp",EDGE,"E2.35.20.0"),sQuery(id+"F0.wireOp",EDGE,"E2.35.21.0"),sQuery(id+"F0.wireOp",EDGE,"E2.35.22.0"),sQuery(id+"F0.wireOp",EDGE,"E2.35.23.0"),sQuery(id+"F0.wireOp",EDGE,"E2.35.24.0"),sQuery(id+"F0.wireOp",EDGE,"E2.35.25.0"),sQuery(id+"F0.wireOp",EDGE,"E2.35.26.0"),sQuery(id+"F0.wireOp",EDGE,"E2.35.27.0"),sQuery(id+"F0.wireOp",EDGE,"E2.35.28.0"),sQuery(id+"F0.wireOp",EDGE,"E2.35.29.0"),sQuery(id+"F0.wireOp",EDGE,"E2.35.30.0"),sQuery(id+"F0.wireOp",EDGE,"E2.35.31.0"),sQuery(id+"F0.wireOp",EDGE,"E2.35.32.0"),sQuery(id+"F0.wireOp",EDGE,"E2.35.33.0"),sQuery(id+"F0.wireOp",EDGE,"E2.35.34.0"),sQuery(id+"F0.wireOp",EDGE,"E2.35.35.0"),sQuery(id+"F0.wireOp",EDGE,"E2.35.36.0"),sQuery(id+"F0.wireOp",EDGE,"E2.35.37.0"),sQuery(id+"F0.wireOp",EDGE,"E2.35.38.0"),sQuery(id+"F0.wireOp",EDGE,"E2.35.39.0"),sQuery(id+"F0.wireOp",EDGE,"E2.35.40.0"),sQuery(id+"F0.wireOp",EDGE,"E2.35.41.0"),sQuery(id+"F0.wireOp",EDGE,"E2.35.42.0"),sQuery(id+"F0.wireOp",EDGE,"E2.35.43.0"),sQuery(id+"F0.wireOp",EDGE,"E2.35.44.0"),sQuery(id+"F0.wireOp",EDGE,"E2.36.0.0"),sQuery(id+"F0.wireOp",EDGE,"E2.36.1.0"),sQuery(id+"F0.wireOp",EDGE,"E2.36.2.0"),sQuery(id+"F0.wireOp",EDGE,"E2.36.3.0"),sQuery(id+"F0.wireOp",EDGE,"E2.36.4.0"),sQuery(id+"F0.wireOp",EDGE,"E2.36.5.0"),sQuery(id+"F0.wireOp",EDGE,"E2.36.6.0"),sQuery(id+"F0.wireOp",EDGE,"E2.36.7.0"),sQuery(id+"F0.wireOp",EDGE,"E2.36.8.0"),sQuery(id+"F0.wireOp",EDGE,"E2.36.9.0"),sQuery(id+"F0.wireOp",EDGE,"E2.36.10.0"),sQuery(id+"F0.wireOp",EDGE,"E2.36.11.0"),sQuery(id+"F0.wireOp",EDGE,"E2.36.12.0"),sQuery(id+"F0.wireOp",EDGE,"E2.36.13.0"),sQuery(id+"F0.wireOp",EDGE,"E2.36.14.0"),sQuery(id+"F0.wireOp",EDGE,"E2.36.15.0"),sQuery(id+"F0.wireOp",EDGE,"E2.36.16.0"),sQuery(id+"F0.wireOp",EDGE,"E2.36.17.0"),sQuery(id+"F0.wireOp",EDGE,"E2.36.18.0"),sQuery(id+"F0.wireOp",EDGE,"E2.36.19.0"),sQuery(id+"F0.wireOp",EDGE,"E2.36.20.0"),sQuery(id+"F0.wireOp",EDGE,"E2.36.21.0"),sQuery(id+"F0.wireOp",EDGE,"E2.36.22.0"),sQuery(id+"F0.wireOp",EDGE,"E2.36.23.0"),sQuery(id+"F0.wireOp",EDGE,"E2.36.24.0"),sQuery(id+"F0.wireOp",EDGE,"E2.36.25.0"),sQuery(id+"F0.wireOp",EDGE,"E2.36.26.0"),sQuery(id+"F0.wireOp",EDGE,"E2.36.27.0"),sQuery(id+"F0.wireOp",EDGE,"E2.36.28.0"),sQuery(id+"F0.wireOp",EDGE,"E2.36.29.0"),sQuery(id+"F0.wireOp",EDGE,"E2.36.30.0"),sQuery(id+"F0.wireOp",EDGE,"E2.36.31.0"),sQuery(id+"F0.wireOp",EDGE,"E2.36.32.0"),sQuery(id+"F0.wireOp",EDGE,"E2.36.33.0"),sQuery(id+"F0.wireOp",EDGE,"E2.36.34.0"),sQuery(id+"F0.wireOp",EDGE,"E2.36.35.0"),sQuery(id+"F0.wireOp",EDGE,"E2.36.36.0"),sQuery(id+"F0.wireOp",EDGE,"E2.36.37.0"),sQuery(id+"F0.wireOp",EDGE,"E2.36.38.0"),sQuery(id+"F0.wireOp",EDGE,"E2.36.39.0"),sQuery(id+"F0.wireOp",EDGE,"E2.36.40.0"),sQuery(id+"F0.wireOp",EDGE,"E2.36.41.0"),sQuery(id+"F0.wireOp",EDGE,"E2.36.42.0"),sQuery(id+"F0.wireOp",EDGE,"E2.36.43.0"),sQuery(id+"F0.wireOp",EDGE,"E2.36.44.0"),sQuery(id+"F0.wireOp",EDGE,"E2.37.0.0"),sQuery(id+"F0.wireOp",EDGE,"E2.37.1.0"),sQuery(id+"F0.wireOp",EDGE,"E2.37.2.0"),sQuery(id+"F0.wireOp",EDGE,"E2.37.3.0"),sQuery(id+"F0.wireOp",EDGE,"E2.37.4.0"),sQuery(id+"F0.wireOp",EDGE,"E2.37.5.0"),sQuery(id+"F0.wireOp",EDGE,"E2.37.6.0"),sQuery(id+"F0.wireOp",EDGE,"E2.37.7.0"),sQuery(id+"F0.wireOp",EDGE,"E2.37.8.0"),sQuery(id+"F0.wireOp",EDGE,"E2.37.9.0"),sQuery(id+"F0.wireOp",EDGE,"E2.37.10.0"),sQuery(id+"F0.wireOp",EDGE,"E2.37.11.0"),sQuery(id+"F0.wireOp",EDGE,"E2.37.12.0"),sQuery(id+"F0.wireOp",EDGE,"E2.37.13.0"),sQuery(id+"F0.wireOp",EDGE,"E2.37.14.0"),sQuery(id+"F0.wireOp",EDGE,"E2.37.15.0"),sQuery(id+"F0.wireOp",EDGE,"E2.37.16.0"),sQuery(id+"F0.wireOp",EDGE,"E2.37.17.0"),sQuery(id+"F0.wireOp",EDGE,"E2.37.18.0"),sQuery(id+"F0.wireOp",EDGE,"E2.37.19.0"),sQuery(id+"F0.wireOp",EDGE,"E2.37.20.0"),sQuery(id+"F0.wireOp",EDGE,"E2.37.21.0"),sQuery(id+"F0.wireOp",EDGE,"E2.37.22.0"),sQuery(id+"F0.wireOp",EDGE,"E2.37.23.0"),sQuery(id+"F0.wireOp",EDGE,"E2.37.24.0"),sQuery(id+"F0.wireOp",EDGE,"E2.37.25.0"),sQuery(id+"F0.wireOp",EDGE,"E2.37.26.0"),sQuery(id+"F0.wireOp",EDGE,"E2.37.27.0"),sQuery(id+"F0.wireOp",EDGE,"E2.37.28.0"),sQuery(id+"F0.wireOp",EDGE,"E2.37.29.0"),sQuery(id+"F0.wireOp",EDGE,"E2.37.30.0"),sQuery(id+"F0.wireOp",EDGE,"E2.37.31.0"),sQuery(id+"F0.wireOp",EDGE,"E2.37.32.0"),sQuery(id+"F0.wireOp",EDGE,"E2.37.33.0"),sQuery(id+"F0.wireOp",EDGE,"E2.37.34.0"),sQuery(id+"F0.wireOp",EDGE,"E2.37.35.0"),sQuery(id+"F0.wireOp",EDGE,"E2.37.36.0"),sQuery(id+"F0.wireOp",EDGE,"E2.37.37.0"),sQuery(id+"F0.wireOp",EDGE,"E2.37.38.0"),sQuery(id+"F0.wireOp",EDGE,"E2.37.39.0"),sQuery(id+"F0.wireOp",EDGE,"E2.37.40.0"),sQuery(id+"F0.wireOp",EDGE,"E2.37.41.0"),sQuery(id+"F0.wireOp",EDGE,"E2.37.42.0"),sQuery(id+"F0.wireOp",EDGE,"E2.37.43.0"),sQuery(id+"F0.wireOp",EDGE,"E2.37.44.0"),sQuery(id+"F0.wireOp",EDGE,"E2.38.0.0"),sQuery(id+"F0.wireOp",EDGE,"E2.38.1.0"),sQuery(id+"F0.wireOp",EDGE,"E2.38.2.0"),sQuery(id+"F0.wireOp",EDGE,"E2.38.3.0"),sQuery(id+"F0.wireOp",EDGE,"E2.38.4.0"),sQuery(id+"F0.wireOp",EDGE,"E2.38.5.0"),sQuery(id+"F0.wireOp",EDGE,"E2.38.6.0"),sQuery(id+"F0.wireOp",EDGE,"E2.38.7.0"),sQuery(id+"F0.wireOp",EDGE,"E2.38.8.0"),sQuery(id+"F0.wireOp",EDGE,"E2.38.9.0"),sQuery(id+"F0.wireOp",EDGE,"E2.38.10.0"),sQuery(id+"F0.wireOp",EDGE,"E2.38.11.0"),sQuery(id+"F0.wireOp",EDGE,"E2.38.12.0"),sQuery(id+"F0.wireOp",EDGE,"E2.38.13.0"),sQuery(id+"F0.wireOp",EDGE,"E2.38.14.0"),sQuery(id+"F0.wireOp",EDGE,"E2.38.15.0"),sQuery(id+"F0.wireOp",EDGE,"E2.38.16.0"),sQuery(id+"F0.wireOp",EDGE,"E2.38.17.0"),sQuery(id+"F0.wireOp",EDGE,"E2.38.18.0"),sQuery(id+"F0.wireOp",EDGE,"E2.38.19.0"),sQuery(id+"F0.wireOp",EDGE,"E2.38.20.0"),sQuery(id+"F0.wireOp",EDGE,"E2.38.21.0"),sQuery(id+"F0.wireOp",EDGE,"E2.38.22.0"),sQuery(id+"F0.wireOp",EDGE,"E2.38.23.0"),sQuery(id+"F0.wireOp",EDGE,"E2.38.24.0"),sQuery(id+"F0.wireOp",EDGE,"E2.38.25.0"),sQuery(id+"F0.wireOp",EDGE,"E2.38.26.0"),sQuery(id+"F0.wireOp",EDGE,"E2.38.27.0"),sQuery(id+"F0.wireOp",EDGE,"E2.38.28.0"),sQuery(id+"F0.wireOp",EDGE,"E2.38.29.0"),sQuery(id+"F0.wireOp",EDGE,"E2.38.30.0"),sQuery(id+"F0.wireOp",EDGE,"E2.38.31.0"),sQuery(id+"F0.wireOp",EDGE,"E2.38.32.0"),sQuery(id+"F0.wireOp",EDGE,"E2.38.33.0"),sQuery(id+"F0.wireOp",EDGE,"E2.38.34.0"),sQuery(id+"F0.wireOp",EDGE,"E2.38.35.0"),sQuery(id+"F0.wireOp",EDGE,"E2.38.36.0"),sQuery(id+"F0.wireOp",EDGE,"E2.38.37.0"),sQuery(id+"F0.wireOp",EDGE,"E2.38.38.0"),sQuery(id+"F0.wireOp",EDGE,"E2.38.39.0"),sQuery(id+"F0.wireOp",EDGE,"E2.38.40.0"),sQuery(id+"F0.wireOp",EDGE,"E2.38.41.0"),sQuery(id+"F0.wireOp",EDGE,"E2.38.42.0"),sQuery(id+"F0.wireOp",EDGE,"E2.38.43.0"),sQuery(id+"F0.wireOp",EDGE,"E2.38.44.0"),sQuery(id+"F0.wireOp",EDGE,"E2.39.0.0"),sQuery(id+"F0.wireOp",EDGE,"E2.39.1.0"),sQuery(id+"F0.wireOp",EDGE,"E2.39.2.0"),sQuery(id+"F0.wireOp",EDGE,"E2.39.3.0"),sQuery(id+"F0.wireOp",EDGE,"E2.39.4.0"),sQuery(id+"F0.wireOp",EDGE,"E2.39.5.0"),sQuery(id+"F0.wireOp",EDGE,"E2.39.6.0"),sQuery(id+"F0.wireOp",EDGE,"E2.39.7.0"),sQuery(id+"F0.wireOp",EDGE,"E2.39.8.0"),sQuery(id+"F0.wireOp",EDGE,"E2.39.9.0"),sQuery(id+"F0.wireOp",EDGE,"E2.39.10.0"),sQuery(id+"F0.wireOp",EDGE,"E2.39.11.0"),sQuery(id+"F0.wireOp",EDGE,"E2.39.12.0"),sQuery(id+"F0.wireOp",EDGE,"E2.39.13.0"),sQuery(id+"F0.wireOp",EDGE,"E2.39.14.0"),sQuery(id+"F0.wireOp",EDGE,"E2.39.15.0"),sQuery(id+"F0.wireOp",EDGE,"E2.39.16.0"),sQuery(id+"F0.wireOp",EDGE,"E2.39.17.0"),sQuery(id+"F0.wireOp",EDGE,"E2.39.18.0"),sQuery(id+"F0.wireOp",EDGE,"E2.39.19.0"),sQuery(id+"F0.wireOp",EDGE,"E2.39.20.0"),sQuery(id+"F0.wireOp",EDGE,"E2.39.21.0"),sQuery(id+"F0.wireOp",EDGE,"E2.39.22.0"),sQuery(id+"F0.wireOp",EDGE,"E2.39.23.0"),sQuery(id+"F0.wireOp",EDGE,"E2.39.24.0"),sQuery(id+"F0.wireOp",EDGE,"E2.39.25.0"),sQuery(id+"F0.wireOp",EDGE,"E2.39.26.0"),sQuery(id+"F0.wireOp",EDGE,"E2.39.27.0"),sQuery(id+"F0.wireOp",EDGE,"E2.39.28.0"),sQuery(id+"F0.wireOp",EDGE,"E2.39.29.0"),sQuery(id+"F0.wireOp",EDGE,"E2.39.30.0"),sQuery(id+"F0.wireOp",EDGE,"E2.39.31.0"),sQuery(id+"F0.wireOp",EDGE,"E2.39.32.0"),sQuery(id+"F0.wireOp",EDGE,"E2.39.33.0"),sQuery(id+"F0.wireOp",EDGE,"E2.39.34.0"),sQuery(id+"F0.wireOp",EDGE,"E2.39.35.0"),sQuery(id+"F0.wireOp",EDGE,"E2.39.36.0"),sQuery(id+"F0.wireOp",EDGE,"E2.39.37.0"),sQuery(id+"F0.wireOp",EDGE,"E2.39.38.0"),sQuery(id+"F0.wireOp",EDGE,"E2.39.39.0"),sQuery(id+"F0.wireOp",EDGE,"E2.39.40.0"),sQuery(id+"F0.wireOp",EDGE,"E2.39.41.0"),sQuery(id+"F0.wireOp",EDGE,"E2.39.42.0"),sQuery(id+"F0.wireOp",EDGE,"E2.39.43.0"),sQuery(id+"F0.wireOp",EDGE,"E2.39.44.0"),sQuery(id+"F0.wireOp",EDGE,"E2.40.0.0"),sQuery(id+"F0.wireOp",EDGE,"E2.40.1.0"),sQuery(id+"F0.wireOp",EDGE,"E2.40.2.0"),sQuery(id+"F0.wireOp",EDGE,"E2.40.3.0"),sQuery(id+"F0.wireOp",EDGE,"E2.40.4.0"),sQuery(id+"F0.wireOp",EDGE,"E2.40.5.0"),sQuery(id+"F0.wireOp",EDGE,"E2.40.6.0"),sQuery(id+"F0.wireOp",EDGE,"E2.40.7.0"),sQuery(id+"F0.wireOp",EDGE,"E2.40.8.0"),sQuery(id+"F0.wireOp",EDGE,"E2.40.9.0"),sQuery(id+"F0.wireOp",EDGE,"E2.40.10.0"),sQuery(id+"F0.wireOp",EDGE,"E2.40.11.0"),sQuery(id+"F0.wireOp",EDGE,"E2.40.12.0"),sQuery(id+"F0.wireOp",EDGE,"E2.40.13.0"),sQuery(id+"F0.wireOp",EDGE,"E2.40.14.0"),sQuery(id+"F0.wireOp",EDGE,"E2.40.15.0"),sQuery(id+"F0.wireOp",EDGE,"E2.40.16.0"),sQuery(id+"F0.wireOp",EDGE,"E2.40.17.0"),sQuery(id+"F0.wireOp",EDGE,"E2.40.18.0"),sQuery(id+"F0.wireOp",EDGE,"E2.40.19.0"),sQuery(id+"F0.wireOp",EDGE,"E2.40.20.0"),sQuery(id+"F0.wireOp",EDGE,"E2.40.21.0"),sQuery(id+"F0.wireOp",EDGE,"E2.40.22.0"),sQuery(id+"F0.wireOp",EDGE,"E2.40.23.0"),sQuery(id+"F0.wireOp",EDGE,"E2.40.24.0"),sQuery(id+"F0.wireOp",EDGE,"E2.40.25.0"),sQuery(id+"F0.wireOp",EDGE,"E2.40.26.0"),sQuery(id+"F0.wireOp",EDGE,"E2.40.27.0"),sQuery(id+"F0.wireOp",EDGE,"E2.40.28.0"),sQuery(id+"F0.wireOp",EDGE,"E2.40.29.0"),sQuery(id+"F0.wireOp",EDGE,"E2.40.30.0"),sQuery(id+"F0.wireOp",EDGE,"E2.40.31.0"),sQuery(id+"F0.wireOp",EDGE,"E2.40.32.0"),sQuery(id+"F0.wireOp",EDGE,"E2.40.33.0"),sQuery(id+"F0.wireOp",EDGE,"E2.40.34.0"),sQuery(id+"F0.wireOp",EDGE,"E2.40.35.0"),sQuery(id+"F0.wireOp",EDGE,"E2.40.36.0"),sQuery(id+"F0.wireOp",EDGE,"E2.40.37.0"),sQuery(id+"F0.wireOp",EDGE,"E2.40.38.0"),sQuery(id+"F0.wireOp",EDGE,"E2.40.39.0"),sQuery(id+"F0.wireOp",EDGE,"E2.40.40.0"),sQuery(id+"F0.wireOp",EDGE,"E2.40.41.0"),sQuery(id+"F0.wireOp",EDGE,"E2.40.42.0"),sQuery(id+"F0.wireOp",EDGE,"E2.40.43.0"),sQuery(id+"F0.wireOp",EDGE,"E2.40.44.0"),sQuery(id+"F0.wireOp",EDGE,"E2.41.0.0"),sQuery(id+"F0.wireOp",EDGE,"E2.41.1.0"),sQuery(id+"F0.wireOp",EDGE,"E2.41.2.0"),sQuery(id+"F0.wireOp",EDGE,"E2.41.3.0"),sQuery(id+"F0.wireOp",EDGE,"E2.41.4.0"),sQuery(id+"F0.wireOp",EDGE,"E2.41.5.0"),sQuery(id+"F0.wireOp",EDGE,"E2.41.6.0"),sQuery(id+"F0.wireOp",EDGE,"E2.41.7.0"),sQuery(id+"F0.wireOp",EDGE,"E2.41.8.0"),sQuery(id+"F0.wireOp",EDGE,"E2.41.9.0"),sQuery(id+"F0.wireOp",EDGE,"E2.41.10.0"),sQuery(id+"F0.wireOp",EDGE,"E2.41.11.0"),sQuery(id+"F0.wireOp",EDGE,"E2.41.12.0"),sQuery(id+"F0.wireOp",EDGE,"E2.41.13.0"),sQuery(id+"F0.wireOp",EDGE,"E2.41.14.0"),sQuery(id+"F0.wireOp",EDGE,"E2.41.15.0"),sQuery(id+"F0.wireOp",EDGE,"E2.41.16.0"),sQuery(id+"F0.wireOp",EDGE,"E2.41.17.0"),sQuery(id+"F0.wireOp",EDGE,"E2.41.18.0"),sQuery(id+"F0.wireOp",EDGE,"E2.41.19.0"),sQuery(id+"F0.wireOp",EDGE,"E2.41.20.0"),sQuery(id+"F0.wireOp",EDGE,"E2.41.21.0"),sQuery(id+"F0.wireOp",EDGE,"E2.41.22.0"),sQuery(id+"F0.wireOp",EDGE,"E2.41.23.0"),sQuery(id+"F0.wireOp",EDGE,"E2.41.24.0"),sQuery(id+"F0.wireOp",EDGE,"E2.41.25.0"),sQuery(id+"F0.wireOp",EDGE,"E2.41.26.0"),sQuery(id+"F0.wireOp",EDGE,"E2.41.27.0"),sQuery(id+"F0.wireOp",EDGE,"E2.41.28.0"),sQuery(id+"F0.wireOp",EDGE,"E2.41.29.0"),sQuery(id+"F0.wireOp",EDGE,"E2.41.30.0"),sQuery(id+"F0.wireOp",EDGE,"E2.41.31.0"),sQuery(id+"F0.wireOp",EDGE,"E2.41.32.0"),sQuery(id+"F0.wireOp",EDGE,"E2.41.33.0"),sQuery(id+"F0.wireOp",EDGE,"E2.41.34.0"),sQuery(id+"F0.wireOp",EDGE,"E2.41.35.0"),sQuery(id+"F0.wireOp",EDGE,"E2.41.36.0"),sQuery(id+"F0.wireOp",EDGE,"E2.41.37.0"),sQuery(id+"F0.wireOp",EDGE,"E2.41.38.0"),sQuery(id+"F0.wireOp",EDGE,"E2.41.39.0"),sQuery(id+"F0.wireOp",EDGE,"E2.41.40.0"),sQuery(id+"F0.wireOp",EDGE,"E2.41.41.0"),sQuery(id+"F0.wireOp",EDGE,"E2.41.42.0"),sQuery(id+"F0.wireOp",EDGE,"E2.41.43.0"),sQuery(id+"F0.wireOp",EDGE,"E2.41.44.0"),sQuery(id+"F0.wireOp",EDGE,"E2.42.0.0"),sQuery(id+"F0.wireOp",EDGE,"E2.42.1.0"),sQuery(id+"F0.wireOp",EDGE,"E2.42.2.0"),sQuery(id+"F0.wireOp",EDGE,"E2.42.3.0"),sQuery(id+"F0.wireOp",EDGE,"E2.42.4.0"),sQuery(id+"F0.wireOp",EDGE,"E2.42.5.0"),sQuery(id+"F0.wireOp",EDGE,"E2.42.6.0"),sQuery(id+"F0.wireOp",EDGE,"E2.42.7.0"),sQuery(id+"F0.wireOp",EDGE,"E2.42.8.0"),sQuery(id+"F0.wireOp",EDGE,"E2.42.9.0"),sQuery(id+"F0.wireOp",EDGE,"E2.42.10.0"),sQuery(id+"F0.wireOp",EDGE,"E2.42.11.0"),sQuery(id+"F0.wireOp",EDGE,"E2.42.12.0"),sQuery(id+"F0.wireOp",EDGE,"E2.42.13.0"),sQuery(id+"F0.wireOp",EDGE,"E2.42.14.0"),sQuery(id+"F0.wireOp",EDGE,"E2.42.15.0"),sQuery(id+"F0.wireOp",EDGE,"E2.42.16.0"),sQuery(id+"F0.wireOp",EDGE,"E2.42.17.0"),sQuery(id+"F0.wireOp",EDGE,"E2.42.18.0"),sQuery(id+"F0.wireOp",EDGE,"E2.42.19.0"),sQuery(id+"F0.wireOp",EDGE,"E2.42.20.0"),sQuery(id+"F0.wireOp",EDGE,"E2.42.21.0"),sQuery(id+"F0.wireOp",EDGE,"E2.42.22.0"),sQuery(id+"F0.wireOp",EDGE,"E2.42.23.0"),sQuery(id+"F0.wireOp",EDGE,"E2.42.24.0"),sQuery(id+"F0.wireOp",EDGE,"E2.42.25.0"),sQuery(id+"F0.wireOp",EDGE,"E2.42.26.0"),sQuery(id+"F0.wireOp",EDGE,"E2.42.27.0"),sQuery(id+"F0.wireOp",EDGE,"E2.42.28.0"),sQuery(id+"F0.wireOp",EDGE,"E2.42.29.0"),sQuery(id+"F0.wireOp",EDGE,"E2.42.30.0"),sQuery(id+"F0.wireOp",EDGE,"E2.42.31.0"),sQuery(id+"F0.wireOp",EDGE,"E2.42.32.0"),sQuery(id+"F0.wireOp",EDGE,"E2.42.33.0"),sQuery(id+"F0.wireOp",EDGE,"E2.42.34.0"),sQuery(id+"F0.wireOp",EDGE,"E2.42.35.0"),sQuery(id+"F0.wireOp",EDGE,"E2.42.36.0"),sQuery(id+"F0.wireOp",EDGE,"E2.42.37.0"),sQuery(id+"F0.wireOp",EDGE,"E2.42.38.0"),sQuery(id+"F0.wireOp",EDGE,"E2.42.39.0"),sQuery(id+"F0.wireOp",EDGE,"E2.42.40.0"),sQuery(id+"F0.wireOp",EDGE,"E2.42.41.0"),sQuery(id+"F0.wireOp",EDGE,"E2.42.42.0"),sQuery(id+"F0.wireOp",EDGE,"E2.42.43.0"),sQuery(id+"F0.wireOp",EDGE,"E2.42.44.0"),sQuery(id+"F0.wireOp",EDGE,"E2.43.0.0"),sQuery(id+"F0.wireOp",EDGE,"E2.43.1.0"),sQuery(id+"F0.wireOp",EDGE,"E2.43.2.0"),sQuery(id+"F0.wireOp",EDGE,"E2.43.3.0"),sQuery(id+"F0.wireOp",EDGE,"E2.43.4.0"),sQuery(id+"F0.wireOp",EDGE,"E2.43.5.0"),sQuery(id+"F0.wireOp",EDGE,"E2.43.6.0"),sQuery(id+"F0.wireOp",EDGE,"E2.43.7.0"),sQuery(id+"F0.wireOp",EDGE,"E2.43.8.0"),sQuery(id+"F0.wireOp",EDGE,"E2.43.9.0"),sQuery(id+"F0.wireOp",EDGE,"E2.43.10.0"),sQuery(id+"F0.wireOp",EDGE,"E2.43.11.0"),sQuery(id+"F0.wireOp",EDGE,"E2.43.12.0"),sQuery(id+"F0.wireOp",EDGE,"E2.43.13.0"),sQuery(id+"F0.wireOp",EDGE,"E2.43.14.0"),sQuery(id+"F0.wireOp",EDGE,"E2.43.15.0"),sQuery(id+"F0.wireOp",EDGE,"E2.43.16.0"),sQuery(id+"F0.wireOp",EDGE,"E2.43.17.0"),sQuery(id+"F0.wireOp",EDGE,"E2.43.18.0"),sQuery(id+"F0.wireOp",EDGE,"E2.43.19.0"),sQuery(id+"F0.wireOp",EDGE,"E2.43.20.0"),sQuery(id+"F0.wireOp",EDGE,"E2.43.21.0"),sQuery(id+"F0.wireOp",EDGE,"E2.43.22.0"),sQuery(id+"F0.wireOp",EDGE,"E2.43.23.0"),sQuery(id+"F0.wireOp",EDGE,"E2.43.24.0"),sQuery(id+"F0.wireOp",EDGE,"E2.43.25.0"),sQuery(id+"F0.wireOp",EDGE,"E2.43.26.0"),sQuery(id+"F0.wireOp",EDGE,"E2.43.27.0"),sQuery(id+"F0.wireOp",EDGE,"E2.43.28.0"),sQuery(id+"F0.wireOp",EDGE,"E2.43.29.0"),sQuery(id+"F0.wireOp",EDGE,"E2.43.30.0"),sQuery(id+"F0.wireOp",EDGE,"E2.43.31.0"),sQuery(id+"F0.wireOp",EDGE,"E2.43.32.0"),sQuery(id+"F0.wireOp",EDGE,"E2.43.33.0"),sQuery(id+"F0.wireOp",EDGE,"E2.43.34.0"),sQuery(id+"F0.wireOp",EDGE,"E2.43.35.0"),sQuery(id+"F0.wireOp",EDGE,"E2.43.36.0"),sQuery(id+"F0.wireOp",EDGE,"E2.43.37.0"),sQuery(id+"F0.wireOp",EDGE,"E2.43.38.0"),sQuery(id+"F0.wireOp",EDGE,"E2.43.39.0"),sQuery(id+"F0.wireOp",EDGE,"E2.43.40.0"),sQuery(id+"F0.wireOp",EDGE,"E2.43.41.0"),sQuery(id+"F0.wireOp",EDGE,"E2.43.42.0"),sQuery(id+"F0.wireOp",EDGE,"E2.43.43.0"),sQuery(id+"F0.wireOp",EDGE,"E2.43.44.0"),sQuery(id+"F0.wireOp",EDGE,"E2.44.0.0"),sQuery(id+"F0.wireOp",EDGE,"E2.44.1.0"),sQuery(id+"F0.wireOp",EDGE,"E2.44.2.0"),sQuery(id+"F0.wireOp",EDGE,"E2.44.3.0"),sQuery(id+"F0.wireOp",EDGE,"E2.44.4.0"),sQuery(id+"F0.wireOp",EDGE,"E2.44.5.0"),sQuery(id+"F0.wireOp",EDGE,"E2.44.6.0"),sQuery(id+"F0.wireOp",EDGE,"E2.44.7.0"),sQuery(id+"F0.wireOp",EDGE,"E2.44.8.0"),sQuery(id+"F0.wireOp",EDGE,"E2.44.9.0"),sQuery(id+"F0.wireOp",EDGE,"E2.44.10.0"),sQuery(id+"F0.wireOp",EDGE,"E2.44.11.0"),sQuery(id+"F0.wireOp",EDGE,"E2.44.12.0"),sQuery(id+"F0.wireOp",EDGE,"E2.44.13.0"),sQuery(id+"F0.wireOp",EDGE,"E2.44.14.0"),sQuery(id+"F0.wireOp",EDGE,"E2.44.15.0"),sQuery(id+"F0.wireOp",EDGE,"E2.44.16.0"),sQuery(id+"F0.wireOp",EDGE,"E2.44.17.0"),sQuery(id+"F0.wireOp",EDGE,"E2.44.18.0"),sQuery(id+"F0.wireOp",EDGE,"E2.44.19.0"),sQuery(id+"F0.wireOp",EDGE,"E2.44.20.0"),sQuery(id+"F0.wireOp",EDGE,"E2.44.21.0"),sQuery(id+"F0.wireOp",EDGE,"E2.44.22.0"),sQuery(id+"F0.wireOp",EDGE,"E2.44.23.0"),sQuery(id+"F0.wireOp",EDGE,"E2.44.24.0"),sQuery(id+"F0.wireOp",EDGE,"E2.44.25.0"),sQuery(id+"F0.wireOp",EDGE,"E2.44.26.0"),sQuery(id+"F0.wireOp",EDGE,"E2.44.27.0"),sQuery(id+"F0.wireOp",EDGE,"E2.44.28.0"),sQuery(id+"F0.wireOp",EDGE,"E2.44.29.0"),sQuery(id+"F0.wireOp",EDGE,"E2.44.30.0"),sQuery(id+"F0.wireOp",EDGE,"E2.44.31.0"),sQuery(id+"F0.wireOp",EDGE,"E2.44.32.0"),sQuery(id+"F0.wireOp",EDGE,"E2.44.33.0"),sQuery(id+"F0.wireOp",EDGE,"E2.44.34.0"),sQuery(id+"F0.wireOp",EDGE,"E2.44.35.0"),sQuery(id+"F0.wireOp",EDGE,"E2.44.36.0"),sQuery(id+"F0.wireOp",EDGE,"E2.44.37.0"),sQuery(id+"F0.wireOp",EDGE,"E2.44.38.0"),sQuery(id+"F0.wireOp",EDGE,"E2.44.39.0"),sQuery(id+"F0.wireOp",EDGE,"E2.44.40.0"),sQuery(id+"F0.wireOp",EDGE,"E2.44.41.0"),sQuery(id+"F0.wireOp",EDGE,"E2.44.42.0"),sQuery(id+"F0.wireOp",EDGE,"E2.44.43.0"),sQuery(id+"F0.wireOp",EDGE,"E2.44.44.0")])],"isStart":false});
            shell(context, id + "F2", {"entities" : qUnion([Q0]), "thickness" : 3.17 * mm});
        }
        {
            var Q0;
            Q0=makeQuery(id+"F2.opShell","OFFSET_FACE",FACE,{"disambiguationData":[OSD([sQuery(id+"F0.wireOp",EDGE,"E0.top")])]});
            var Q1;
            Q1=makeQuery(id+"F2.opShell","OFFSET_FACE",FACE,{"disambiguationData":[OSD([sQuery(id+"F0.wireOp",EDGE,"E0.bottom")])]});
            extrude(context, id + "F3", {"entities" : qUnion([Q0]), "operationType" : NewBodyOperationType.REMOVE, "endBound" : BoundingType.UP_TO_SURFACE, "depth" : 25.4 * mm, "endBoundEntityFace" : qUnion([Q1]), "offsetDistance" : 25.4 * mm});
        }
    });
